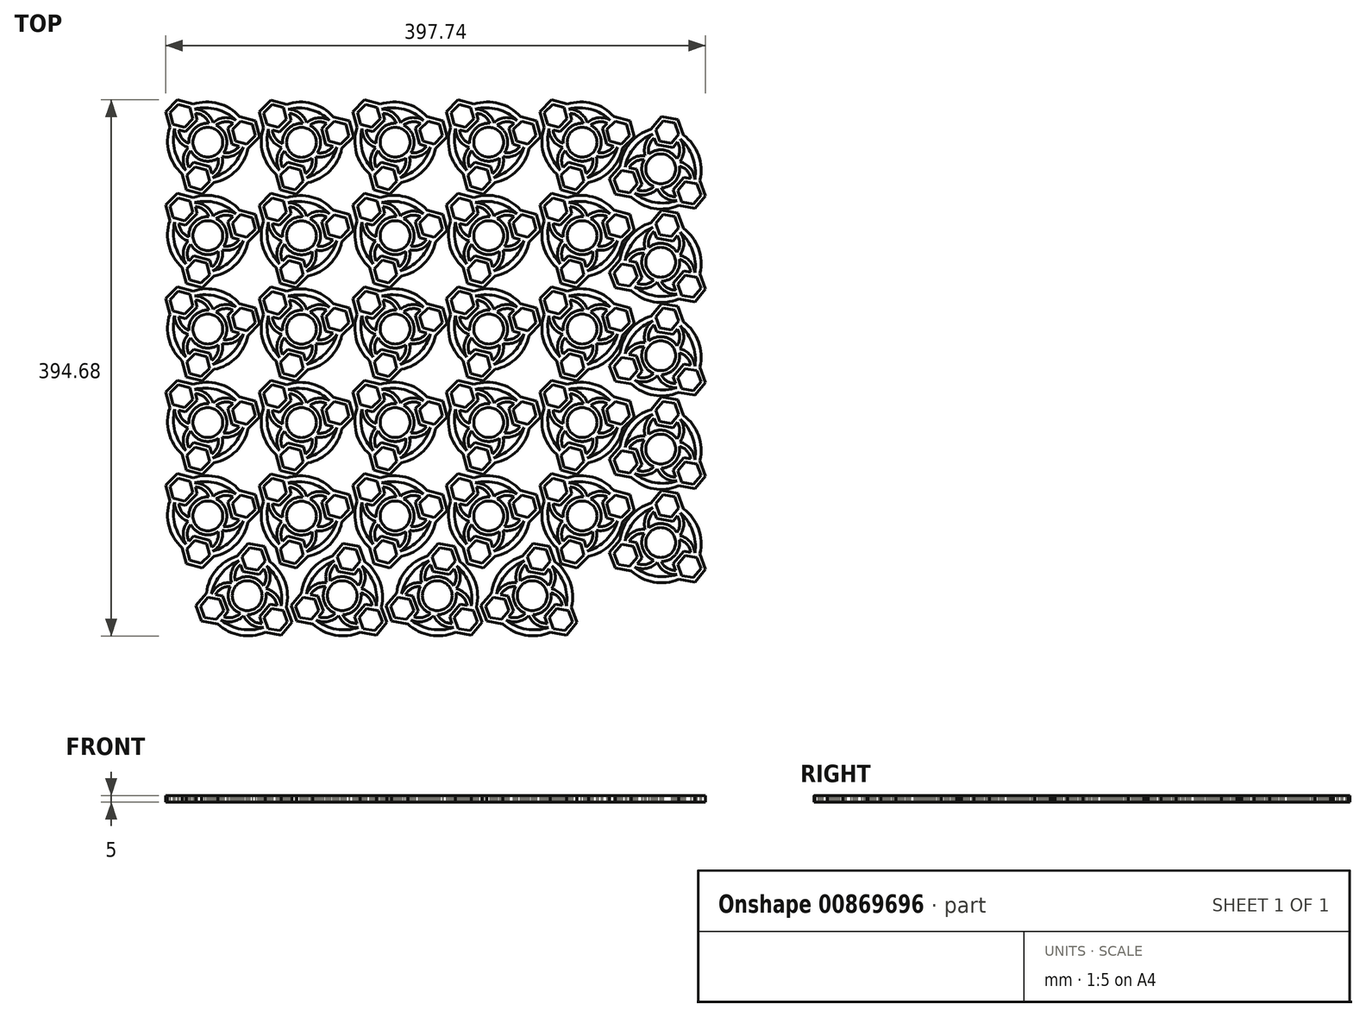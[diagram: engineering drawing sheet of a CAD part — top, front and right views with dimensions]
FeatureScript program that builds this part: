
annotation { "Feature Type Name" : "Feature", "Feature Type Description" : "" }
export const myFeature = defineFeature(function(context is Context, id is Id, definition is map)
    precondition{}
    {
        {
            var Q0;
            Q0=qCreatedBy(makeId("Top.planeOp"),FACE);
            var sketch = newSketch(context, id + "F0", { "sketchPlane" : qUnion([Q0])});
            skArc(sketch, "E0", {"start": v(-13.28, 4.44) * mm, "mid": v(-12.12, -7) * mm, "end": v(-2.8, -13.72) * mm});
            skCircle(sketch, "E1", {"center": v(0, 0) * mm, "radius": 11 * mm});
            skLineSegment(sketch, "E2.0", {"start": v(-4.34, 34.98) * mm, "end": v(4.34, 34.98) * mm});
            skLineSegment(sketch, "E2.1", {"start": v(4.34, 34.98) * mm, "end": v(8.68, 27.46) * mm});
            skLineSegment(sketch, "E2.2", {"start": v(8.68, 27.46) * mm, "end": v(4.34, 19.95) * mm});
            skLineSegment(sketch, "E2.3", {"start": v(4.34, 19.95) * mm, "end": v(-4.34, 19.95) * mm});
            skLineSegment(sketch, "E2.4", {"start": v(-4.34, 19.95) * mm, "end": v(-8.68, 27.46) * mm});
            skLineSegment(sketch, "E2.5", {"start": v(-8.68, 27.46) * mm, "end": v(-4.34, 34.98) * mm});
            skPoint(sketch, "E2.0.midPoint", {"position": v(0, 34.98) * mm});
            skArc(sketch, "E3", {"start": v(-10.28, 24.23) * mm, "mid": v(-14.32, 16.28) * mm, "end": v(-12.95, 7.48) * mm});
            skArc(sketch, "E4", {"start": v(-8.7, 21.51) * mm, "mid": v(-11.38, 15.65) * mm, "end": v(-10.49, 9.28) * mm});
            skLineSegment(sketch, "E5.0", {"start": v(-6.07, 37.98) * mm, "end": v(6.07, 37.98) * mm});
            skLineSegment(sketch, "E5.1", {"start": v(6.07, 37.98) * mm, "end": v(12.14, 27.46) * mm});
            skLineSegment(sketch, "E5.3", {"start": v(6.07, 16.95) * mm, "end": v(-6.07, 16.95) * mm});
            skLineSegment(sketch, "E5.4", {"start": v(-6.07, 16.95) * mm, "end": v(-8.7, 21.51) * mm});
            skLineSegment(sketch, "E5.5", {"start": v(-12.14, 27.46) * mm, "end": v(-6.07, 37.98) * mm});
            skPoint(sketch, "E5.0.midPoint", {"position": v(0, 37.98) * mm});
            skLineSegment(sketch, "E6.trimOffspring", {"start": v(8.7, 21.51) * mm, "end": v(6.07, 16.95) * mm});
            skArc(sketch, "E7.trimOffspring", {"start": v(10.49, 9.28) * mm, "mid": v(11.38, 15.65) * mm, "end": v(8.7, 21.51) * mm});
            skArc(sketch, "E8.trimOffspring", {"start": v(10.49, 9.28) * mm, "mid": v(0, 14) * mm, "end": v(-10.49, 9.28) * mm});
            skArc(sketch, "E9.trimOffspring", {"start": v(12.95, 7.48) * mm, "mid": v(14.32, 16.28) * mm, "end": v(10.28, 24.23) * mm});
            skLineSegment(sketch, "E10.1.0", {"start": v(-32.46, -13.73) * mm, "end": v(-28.12, -6.22) * mm});
            skLineSegment(sketch, "E10.1.1", {"start": v(-17.71, -3.22) * mm, "end": v(-11.64, -13.73) * mm});
            skLineSegment(sketch, "E10.1.2", {"start": v(-22.98, -3.22) * mm, "end": v(-17.71, -3.22) * mm});
            skArc(sketch, "E10.1.3", {"start": v(-12.95, 7.48) * mm, "mid": v(-21.26, 4.26) * mm, "end": v(-26.12, -3.22) * mm});
            skLineSegment(sketch, "E10.1.5", {"start": v(-29.85, -24.25) * mm, "end": v(-35.92, -13.73) * mm});
            skArc(sketch, "E10.1.6", {"start": v(2.8, -13.72) * mm, "mid": v(12.12, -7) * mm, "end": v(13.28, 4.44) * mm});
            skArc(sketch, "E10.1.7", {"start": v(-13.28, 4.44) * mm, "mid": v(-19.25, 2.03) * mm, "end": v(-22.98, -3.22) * mm});
            skLineSegment(sketch, "E10.1.8", {"start": v(-15.1, -13.73) * mm, "end": v(-19.44, -21.25) * mm});
            skLineSegment(sketch, "E10.1.9", {"start": v(-28.12, -6.22) * mm, "end": v(-19.44, -6.22) * mm});
            skLineSegment(sketch, "E10.1.10", {"start": v(-19.44, -6.22) * mm, "end": v(-15.1, -13.73) * mm});
            skLineSegment(sketch, "E10.1.11", {"start": v(-11.64, -13.73) * mm, "end": v(-14.28, -18.3) * mm});
            skArc(sketch, "E10.1.12", {"start": v(-14.28, -18.3) * mm, "mid": v(-7.87, -17.68) * mm, "end": v(-2.8, -13.72) * mm});
            skArc(sketch, "E10.1.14", {"start": v(-15.85, -21.01) * mm, "mid": v(-6.94, -20.54) * mm, "end": v(0, -14.95) * mm});
            skLineSegment(sketch, "E10.1.15", {"start": v(-17.71, -24.25) * mm, "end": v(-29.85, -24.25) * mm});
            skLineSegment(sketch, "E10.1.16", {"start": v(-19.44, -21.25) * mm, "end": v(-28.12, -21.25) * mm});
            skPoint(sketch, "E10.1.17", {"position": v(-30.29, -17.49) * mm});
            skLineSegment(sketch, "E10.1.18", {"start": v(-35.92, -13.73) * mm, "end": v(-29.85, -3.22) * mm});
            skPoint(sketch, "E10.1.19", {"position": v(-32.89, -18.99) * mm});
            skLineSegment(sketch, "E10.1.20", {"start": v(-28.12, -21.25) * mm, "end": v(-32.46, -13.73) * mm});
            skLineSegment(sketch, "E10.2.0", {"start": v(28.12, -21.25) * mm, "end": v(19.44, -21.25) * mm});
            skLineSegment(sketch, "E10.2.1", {"start": v(11.64, -13.73) * mm, "end": v(17.71, -3.22) * mm});
            skLineSegment(sketch, "E10.2.2", {"start": v(14.28, -18.3) * mm, "end": v(11.64, -13.73) * mm});
            skArc(sketch, "E10.2.3", {"start": v(0, -14.95) * mm, "mid": v(6.94, -20.54) * mm, "end": v(15.85, -21.01) * mm});
            skArc(sketch, "E10.2.4", {"start": v(2.8, -13.72) * mm, "mid": v(12.12, -7) * mm, "end": v(13.28, 4.44) * mm});
            skLineSegment(sketch, "E10.2.5", {"start": v(35.92, -13.73) * mm, "end": v(29.85, -24.25) * mm});
            skArc(sketch, "E10.2.7", {"start": v(2.8, -13.72) * mm, "mid": v(7.87, -17.68) * mm, "end": v(14.28, -18.3) * mm});
            skLineSegment(sketch, "E10.2.8", {"start": v(19.44, -6.22) * mm, "end": v(28.12, -6.22) * mm});
            skLineSegment(sketch, "E10.2.9", {"start": v(19.44, -21.25) * mm, "end": v(15.1, -13.73) * mm});
            skLineSegment(sketch, "E10.2.10", {"start": v(15.1, -13.73) * mm, "end": v(19.44, -6.22) * mm});
            skLineSegment(sketch, "E10.2.11", {"start": v(17.71, -3.22) * mm, "end": v(22.98, -3.22) * mm});
            skArc(sketch, "E10.2.12", {"start": v(22.98, -3.22) * mm, "mid": v(19.25, 2.03) * mm, "end": v(13.28, 4.44) * mm});
            skArc(sketch, "E10.2.14", {"start": v(26.12, -3.22) * mm, "mid": v(21.26, 4.26) * mm, "end": v(12.95, 7.48) * mm});
            skLineSegment(sketch, "E10.2.15", {"start": v(29.85, -3.22) * mm, "end": v(35.92, -13.73) * mm});
            skLineSegment(sketch, "E10.2.16", {"start": v(28.12, -6.22) * mm, "end": v(32.46, -13.73) * mm});
            skPoint(sketch, "E10.2.17", {"position": v(30.29, -17.49) * mm});
            skLineSegment(sketch, "E10.2.18", {"start": v(29.85, -24.25) * mm, "end": v(17.71, -24.25) * mm});
            skPoint(sketch, "E10.2.19", {"position": v(32.89, -18.99) * mm});
            skLineSegment(sketch, "E10.2.20", {"start": v(32.46, -13.73) * mm, "end": v(28.12, -21.25) * mm});
            skArc(sketch, "E11", {"start": v(-10.28, 24.23) * mm, "mid": v(-21.68, 12.52) * mm, "end": v(-26.12, -3.22) * mm});
            skArc(sketch, "E12", {"start": v(-12.14, 27.46) * mm, "mid": v(-25.63, 14.8) * mm, "end": v(-29.85, -3.22) * mm});
            skArc(sketch, "E13.1.0", {"start": v(-15.85, -21.01) * mm, "mid": v(0, -25.04) * mm, "end": v(15.85, -21.01) * mm});
            skArc(sketch, "E13.1.1", {"start": v(-17.71, -24.25) * mm, "mid": v(0, -29.6) * mm, "end": v(17.71, -24.25) * mm});
            skArc(sketch, "E13.2.0", {"start": v(26.12, -3.22) * mm, "mid": v(21.68, 12.52) * mm, "end": v(10.28, 24.23) * mm});
            skArc(sketch, "E13.2.1", {"start": v(29.85, -3.22) * mm, "mid": v(25.63, 14.8) * mm, "end": v(12.14, 27.46) * mm});
            skSolve(sketch);
        }
        {
            var Q0;
            Q0=makeQuery(id+"F0.imprint","IMPRINT",FACE,{"disambiguationData":[TD([[makeQuery(id+"F0.imprint","IMPRINT",EDGE,{"derivedFrom":sQuery(id+"F0.wireOp",EDGE,"E2.0")}),1.0]])]});
            extrude(context, id + "F1", {"entities" : qUnion([Q0]), "depth" : 5 * mm, "offsetDistance" : 25 * mm});
        }
        {
            var Q0;
            Q0=makeQuery(id+"F1.opExtrude","SWEPT_BODY",BODY,{"disambiguationData":[OSD([sQuery(id+"F0.wireOp",EDGE,"E2.0"),sQuery(id+"F0.wireOp",EDGE,"E2.1"),sQuery(id+"F0.wireOp",EDGE,"E2.2"),sQuery(id+"F0.wireOp",EDGE,"E2.3"),sQuery(id+"F0.wireOp",EDGE,"E2.4"),sQuery(id+"F0.wireOp",EDGE,"E2.5"),sQuery(id+"F0.wireOp",EDGE,"E3"),sQuery(id+"F0.wireOp",EDGE,"E4"),sQuery(id+"F0.wireOp",EDGE,"E5.0"),sQuery(id+"F0.wireOp",EDGE,"E5.1"),sQuery(id+"F0.wireOp",EDGE,"E5.3"),sQuery(id+"F0.wireOp",EDGE,"E5.4"),sQuery(id+"F0.wireOp",EDGE,"E5.5"),sQuery(id+"F0.wireOp",EDGE,"E6.trimOffspring"),sQuery(id+"F0.wireOp",EDGE,"E7.trimOffspring"),sQuery(id+"F0.wireOp",EDGE,"E9.trimOffspring"),sQuery(id+"F0.wireOp",EDGE,"E10.1.0"),sQuery(id+"F0.wireOp",EDGE,"E10.1.1"),sQuery(id+"F0.wireOp",EDGE,"E10.1.2"),sQuery(id+"F0.wireOp",EDGE,"E10.1.3"),sQuery(id+"F0.wireOp",EDGE,"E10.1.5"),sQuery(id+"F0.wireOp",EDGE,"E10.1.7"),sQuery(id+"F0.wireOp",EDGE,"E10.1.8"),sQuery(id+"F0.wireOp",EDGE,"E10.1.9"),sQuery(id+"F0.wireOp",EDGE,"E10.1.10"),sQuery(id+"F0.wireOp",EDGE,"E10.1.11"),sQuery(id+"F0.wireOp",EDGE,"E10.1.12"),sQuery(id+"F0.wireOp",EDGE,"E10.1.14"),sQuery(id+"F0.wireOp",EDGE,"E10.1.15"),sQuery(id+"F0.wireOp",EDGE,"E10.1.16"),sQuery(id+"F0.wireOp",EDGE,"E10.1.18"),sQuery(id+"F0.wireOp",EDGE,"E10.1.20"),sQuery(id+"F0.wireOp",EDGE,"E10.2.0"),sQuery(id+"F0.wireOp",EDGE,"E10.2.1"),sQuery(id+"F0.wireOp",EDGE,"E10.2.2"),sQuery(id+"F0.wireOp",EDGE,"E10.2.3"),sQuery(id+"F0.wireOp",EDGE,"E10.2.5"),sQuery(id+"F0.wireOp",EDGE,"E10.2.7"),sQuery(id+"F0.wireOp",EDGE,"E10.2.8"),sQuery(id+"F0.wireOp",EDGE,"E10.2.9"),sQuery(id+"F0.wireOp",EDGE,"E10.2.10"),sQuery(id+"F0.wireOp",EDGE,"E10.2.11"),sQuery(id+"F0.wireOp",EDGE,"E10.2.12"),sQuery(id+"F0.wireOp",EDGE,"E1"),sQuery(id+"F0.wireOp",EDGE,"E10.2.14"),sQuery(id+"F0.wireOp",EDGE,"E10.2.15"),sQuery(id+"F0.wireOp",EDGE,"E10.2.16"),sQuery(id+"F0.wireOp",EDGE,"E10.2.18"),sQuery(id+"F0.wireOp",EDGE,"E10.2.20"),sQuery(id+"F0.wireOp",EDGE,"E8.trimOffspring"),sQuery(id+"F0.wireOp",EDGE,"E0"),sQuery(id+"F0.wireOp",EDGE,"E10.1.6"),sQuery(id+"F0.wireOp",EDGE,"E11"),sQuery(id+"F0.wireOp",EDGE,"E12"),sQuery(id+"F0.wireOp",EDGE,"E13.1.0"),sQuery(id+"F0.wireOp",EDGE,"E13.1.1"),sQuery(id+"F0.wireOp",EDGE,"E13.2.0"),sQuery(id+"F0.wireOp",EDGE,"E13.2.1")])]});
            transform(context, id + "F2", {"entities" : qUnion([Q0]), "transformType" : TransformType.TRANSLATION_3D, "dx" : -159 * mm, "dy" : 162 * mm, "dz" : 0 * mm, "makeCopy" : false});
        }
        {
            var Q0;
            Q0=makeQuery(id+"F1.opExtrude","SWEPT_BODY",BODY,{"disambiguationData":[OSD([sQuery(id+"F0.wireOp",EDGE,"E2.0"),sQuery(id+"F0.wireOp",EDGE,"E2.1"),sQuery(id+"F0.wireOp",EDGE,"E2.2"),sQuery(id+"F0.wireOp",EDGE,"E2.3"),sQuery(id+"F0.wireOp",EDGE,"E2.4"),sQuery(id+"F0.wireOp",EDGE,"E2.5"),sQuery(id+"F0.wireOp",EDGE,"E3"),sQuery(id+"F0.wireOp",EDGE,"E4"),sQuery(id+"F0.wireOp",EDGE,"E5.0"),sQuery(id+"F0.wireOp",EDGE,"E5.1"),sQuery(id+"F0.wireOp",EDGE,"E5.3"),sQuery(id+"F0.wireOp",EDGE,"E5.4"),sQuery(id+"F0.wireOp",EDGE,"E5.5"),sQuery(id+"F0.wireOp",EDGE,"E6.trimOffspring"),sQuery(id+"F0.wireOp",EDGE,"E7.trimOffspring"),sQuery(id+"F0.wireOp",EDGE,"E9.trimOffspring"),sQuery(id+"F0.wireOp",EDGE,"E10.1.0"),sQuery(id+"F0.wireOp",EDGE,"E10.1.1"),sQuery(id+"F0.wireOp",EDGE,"E10.1.2"),sQuery(id+"F0.wireOp",EDGE,"E10.1.3"),sQuery(id+"F0.wireOp",EDGE,"E10.1.5"),sQuery(id+"F0.wireOp",EDGE,"E10.1.7"),sQuery(id+"F0.wireOp",EDGE,"E10.1.8"),sQuery(id+"F0.wireOp",EDGE,"E10.1.9"),sQuery(id+"F0.wireOp",EDGE,"E10.1.10"),sQuery(id+"F0.wireOp",EDGE,"E10.1.11"),sQuery(id+"F0.wireOp",EDGE,"E10.1.12"),sQuery(id+"F0.wireOp",EDGE,"E10.1.14"),sQuery(id+"F0.wireOp",EDGE,"E10.1.15"),sQuery(id+"F0.wireOp",EDGE,"E10.1.16"),sQuery(id+"F0.wireOp",EDGE,"E10.1.18"),sQuery(id+"F0.wireOp",EDGE,"E10.1.20"),sQuery(id+"F0.wireOp",EDGE,"E10.2.0"),sQuery(id+"F0.wireOp",EDGE,"E10.2.1"),sQuery(id+"F0.wireOp",EDGE,"E10.2.2"),sQuery(id+"F0.wireOp",EDGE,"E10.2.3"),sQuery(id+"F0.wireOp",EDGE,"E10.2.5"),sQuery(id+"F0.wireOp",EDGE,"E10.2.7"),sQuery(id+"F0.wireOp",EDGE,"E10.2.8"),sQuery(id+"F0.wireOp",EDGE,"E10.2.9"),sQuery(id+"F0.wireOp",EDGE,"E10.2.10"),sQuery(id+"F0.wireOp",EDGE,"E10.2.11"),sQuery(id+"F0.wireOp",EDGE,"E10.2.12"),sQuery(id+"F0.wireOp",EDGE,"E1"),sQuery(id+"F0.wireOp",EDGE,"E10.2.14"),sQuery(id+"F0.wireOp",EDGE,"E10.2.15"),sQuery(id+"F0.wireOp",EDGE,"E10.2.16"),sQuery(id+"F0.wireOp",EDGE,"E10.2.18"),sQuery(id+"F0.wireOp",EDGE,"E10.2.20"),sQuery(id+"F0.wireOp",EDGE,"E8.trimOffspring"),sQuery(id+"F0.wireOp",EDGE,"E0"),sQuery(id+"F0.wireOp",EDGE,"E10.1.6"),sQuery(id+"F0.wireOp",EDGE,"E11"),sQuery(id+"F0.wireOp",EDGE,"E12"),sQuery(id+"F0.wireOp",EDGE,"E13.1.0"),sQuery(id+"F0.wireOp",EDGE,"E13.1.1"),sQuery(id+"F0.wireOp",EDGE,"E13.2.0"),sQuery(id+"F0.wireOp",EDGE,"E13.2.1")])]});
            var Q1;
            Q1=makeQuery(id+"F1.opExtrude","CAP_EDGE",EDGE,{"disambiguationData":[OSD([sQuery(id+"F0.wireOp",EDGE,"E1")])],"isStart":false});
            transform(context, id + "F3", {"entities" : qUnion([Q0]), "transformType" : TransformType.ROTATION, "transformAxis" : qUnion([Q1]), "angle" : 45 * degree, "makeCopy" : false});
        }
        {
            var Q0;
            Q0=makeQuery(id+"F1.opExtrude","SWEPT_BODY",BODY,{"disambiguationData":[OSD([sQuery(id+"F0.wireOp",EDGE,"E2.0"),sQuery(id+"F0.wireOp",EDGE,"E2.1"),sQuery(id+"F0.wireOp",EDGE,"E2.2"),sQuery(id+"F0.wireOp",EDGE,"E2.3"),sQuery(id+"F0.wireOp",EDGE,"E2.4"),sQuery(id+"F0.wireOp",EDGE,"E2.5"),sQuery(id+"F0.wireOp",EDGE,"E3"),sQuery(id+"F0.wireOp",EDGE,"E4"),sQuery(id+"F0.wireOp",EDGE,"E5.0"),sQuery(id+"F0.wireOp",EDGE,"E5.1"),sQuery(id+"F0.wireOp",EDGE,"E5.3"),sQuery(id+"F0.wireOp",EDGE,"E5.4"),sQuery(id+"F0.wireOp",EDGE,"E5.5"),sQuery(id+"F0.wireOp",EDGE,"E6.trimOffspring"),sQuery(id+"F0.wireOp",EDGE,"E7.trimOffspring"),sQuery(id+"F0.wireOp",EDGE,"E9.trimOffspring"),sQuery(id+"F0.wireOp",EDGE,"E10.1.0"),sQuery(id+"F0.wireOp",EDGE,"E10.1.1"),sQuery(id+"F0.wireOp",EDGE,"E10.1.2"),sQuery(id+"F0.wireOp",EDGE,"E10.1.3"),sQuery(id+"F0.wireOp",EDGE,"E10.1.5"),sQuery(id+"F0.wireOp",EDGE,"E10.1.7"),sQuery(id+"F0.wireOp",EDGE,"E10.1.8"),sQuery(id+"F0.wireOp",EDGE,"E10.1.9"),sQuery(id+"F0.wireOp",EDGE,"E10.1.10"),sQuery(id+"F0.wireOp",EDGE,"E10.1.11"),sQuery(id+"F0.wireOp",EDGE,"E10.1.12"),sQuery(id+"F0.wireOp",EDGE,"E10.1.14"),sQuery(id+"F0.wireOp",EDGE,"E10.1.15"),sQuery(id+"F0.wireOp",EDGE,"E10.1.16"),sQuery(id+"F0.wireOp",EDGE,"E10.1.18"),sQuery(id+"F0.wireOp",EDGE,"E10.1.20"),sQuery(id+"F0.wireOp",EDGE,"E10.2.0"),sQuery(id+"F0.wireOp",EDGE,"E10.2.1"),sQuery(id+"F0.wireOp",EDGE,"E10.2.2"),sQuery(id+"F0.wireOp",EDGE,"E10.2.3"),sQuery(id+"F0.wireOp",EDGE,"E10.2.5"),sQuery(id+"F0.wireOp",EDGE,"E10.2.7"),sQuery(id+"F0.wireOp",EDGE,"E10.2.8"),sQuery(id+"F0.wireOp",EDGE,"E10.2.9"),sQuery(id+"F0.wireOp",EDGE,"E10.2.10"),sQuery(id+"F0.wireOp",EDGE,"E10.2.11"),sQuery(id+"F0.wireOp",EDGE,"E10.2.12"),sQuery(id+"F0.wireOp",EDGE,"E1"),sQuery(id+"F0.wireOp",EDGE,"E10.2.14"),sQuery(id+"F0.wireOp",EDGE,"E10.2.15"),sQuery(id+"F0.wireOp",EDGE,"E10.2.16"),sQuery(id+"F0.wireOp",EDGE,"E10.2.18"),sQuery(id+"F0.wireOp",EDGE,"E10.2.20"),sQuery(id+"F0.wireOp",EDGE,"E8.trimOffspring"),sQuery(id+"F0.wireOp",EDGE,"E0"),sQuery(id+"F0.wireOp",EDGE,"E10.1.6"),sQuery(id+"F0.wireOp",EDGE,"E11"),sQuery(id+"F0.wireOp",EDGE,"E12"),sQuery(id+"F0.wireOp",EDGE,"E13.1.0"),sQuery(id+"F0.wireOp",EDGE,"E13.1.1"),sQuery(id+"F0.wireOp",EDGE,"E13.2.0"),sQuery(id+"F0.wireOp",EDGE,"E13.2.1")])]});
            transform(context, id + "F4", {"entities" : qUnion([Q0]), "transformType" : TransformType.TRANSLATION_3D, "dx" : -4.9 * mm, "dy" : 7.3 * mm, "dz" : 0 * mm, "makeCopy" : false});
        }
        {
            var Q0;
            Q0=makeQuery(id+"F1.opExtrude","SWEPT_BODY",BODY,{"disambiguationData":[OSD([sQuery(id+"F0.wireOp",EDGE,"E2.0"),sQuery(id+"F0.wireOp",EDGE,"E2.1"),sQuery(id+"F0.wireOp",EDGE,"E2.2"),sQuery(id+"F0.wireOp",EDGE,"E2.3"),sQuery(id+"F0.wireOp",EDGE,"E2.4"),sQuery(id+"F0.wireOp",EDGE,"E2.5"),sQuery(id+"F0.wireOp",EDGE,"E3"),sQuery(id+"F0.wireOp",EDGE,"E4"),sQuery(id+"F0.wireOp",EDGE,"E5.0"),sQuery(id+"F0.wireOp",EDGE,"E5.1"),sQuery(id+"F0.wireOp",EDGE,"E5.3"),sQuery(id+"F0.wireOp",EDGE,"E5.4"),sQuery(id+"F0.wireOp",EDGE,"E5.5"),sQuery(id+"F0.wireOp",EDGE,"E6.trimOffspring"),sQuery(id+"F0.wireOp",EDGE,"E7.trimOffspring"),sQuery(id+"F0.wireOp",EDGE,"E9.trimOffspring"),sQuery(id+"F0.wireOp",EDGE,"E10.1.0"),sQuery(id+"F0.wireOp",EDGE,"E10.1.1"),sQuery(id+"F0.wireOp",EDGE,"E10.1.2"),sQuery(id+"F0.wireOp",EDGE,"E10.1.3"),sQuery(id+"F0.wireOp",EDGE,"E10.1.5"),sQuery(id+"F0.wireOp",EDGE,"E10.1.7"),sQuery(id+"F0.wireOp",EDGE,"E10.1.8"),sQuery(id+"F0.wireOp",EDGE,"E10.1.9"),sQuery(id+"F0.wireOp",EDGE,"E10.1.10"),sQuery(id+"F0.wireOp",EDGE,"E10.1.11"),sQuery(id+"F0.wireOp",EDGE,"E10.1.12"),sQuery(id+"F0.wireOp",EDGE,"E10.1.14"),sQuery(id+"F0.wireOp",EDGE,"E10.1.15"),sQuery(id+"F0.wireOp",EDGE,"E10.1.16"),sQuery(id+"F0.wireOp",EDGE,"E10.1.18"),sQuery(id+"F0.wireOp",EDGE,"E10.1.20"),sQuery(id+"F0.wireOp",EDGE,"E10.2.0"),sQuery(id+"F0.wireOp",EDGE,"E10.2.1"),sQuery(id+"F0.wireOp",EDGE,"E10.2.2"),sQuery(id+"F0.wireOp",EDGE,"E10.2.3"),sQuery(id+"F0.wireOp",EDGE,"E10.2.5"),sQuery(id+"F0.wireOp",EDGE,"E10.2.7"),sQuery(id+"F0.wireOp",EDGE,"E10.2.8"),sQuery(id+"F0.wireOp",EDGE,"E10.2.9"),sQuery(id+"F0.wireOp",EDGE,"E10.2.10"),sQuery(id+"F0.wireOp",EDGE,"E10.2.11"),sQuery(id+"F0.wireOp",EDGE,"E10.2.12"),sQuery(id+"F0.wireOp",EDGE,"E1"),sQuery(id+"F0.wireOp",EDGE,"E10.2.14"),sQuery(id+"F0.wireOp",EDGE,"E10.2.15"),sQuery(id+"F0.wireOp",EDGE,"E10.2.16"),sQuery(id+"F0.wireOp",EDGE,"E10.2.18"),sQuery(id+"F0.wireOp",EDGE,"E10.2.20"),sQuery(id+"F0.wireOp",EDGE,"E8.trimOffspring"),sQuery(id+"F0.wireOp",EDGE,"E0"),sQuery(id+"F0.wireOp",EDGE,"E10.1.6"),sQuery(id+"F0.wireOp",EDGE,"E11"),sQuery(id+"F0.wireOp",EDGE,"E12"),sQuery(id+"F0.wireOp",EDGE,"E13.1.0"),sQuery(id+"F0.wireOp",EDGE,"E13.1.1"),sQuery(id+"F0.wireOp",EDGE,"E13.2.0"),sQuery(id+"F0.wireOp",EDGE,"E13.2.1")])]});
            transform(context, id + "F5", {"entities" : qUnion([Q0]), "transformType" : TransformType.TRANSLATION_3D, "dx" : 69 * mm, "dy" : -0.1 * mm, "dz" : 0 * mm, "makeCopy" : true});
        }
        {
            var Q0;
            Q0=makeQuery(id+"F5.opPattern","COPY",BODY,{"derivedFrom":makeQuery(id+"F1.opExtrude","SWEPT_BODY",BODY,{"disambiguationData":[OSD([sQuery(id+"F0.wireOp",EDGE,"E2.0"),sQuery(id+"F0.wireOp",EDGE,"E2.1"),sQuery(id+"F0.wireOp",EDGE,"E2.2"),sQuery(id+"F0.wireOp",EDGE,"E2.3"),sQuery(id+"F0.wireOp",EDGE,"E2.4"),sQuery(id+"F0.wireOp",EDGE,"E2.5"),sQuery(id+"F0.wireOp",EDGE,"E3"),sQuery(id+"F0.wireOp",EDGE,"E4"),sQuery(id+"F0.wireOp",EDGE,"E5.0"),sQuery(id+"F0.wireOp",EDGE,"E5.1"),sQuery(id+"F0.wireOp",EDGE,"E5.3"),sQuery(id+"F0.wireOp",EDGE,"E5.4"),sQuery(id+"F0.wireOp",EDGE,"E5.5"),sQuery(id+"F0.wireOp",EDGE,"E6.trimOffspring"),sQuery(id+"F0.wireOp",EDGE,"E7.trimOffspring"),sQuery(id+"F0.wireOp",EDGE,"E9.trimOffspring"),sQuery(id+"F0.wireOp",EDGE,"E10.1.0"),sQuery(id+"F0.wireOp",EDGE,"E10.1.1"),sQuery(id+"F0.wireOp",EDGE,"E10.1.2"),sQuery(id+"F0.wireOp",EDGE,"E10.1.3"),sQuery(id+"F0.wireOp",EDGE,"E10.1.5"),sQuery(id+"F0.wireOp",EDGE,"E10.1.7"),sQuery(id+"F0.wireOp",EDGE,"E10.1.8"),sQuery(id+"F0.wireOp",EDGE,"E10.1.9"),sQuery(id+"F0.wireOp",EDGE,"E10.1.10"),sQuery(id+"F0.wireOp",EDGE,"E10.1.11"),sQuery(id+"F0.wireOp",EDGE,"E10.1.12"),sQuery(id+"F0.wireOp",EDGE,"E10.1.14"),sQuery(id+"F0.wireOp",EDGE,"E10.1.15"),sQuery(id+"F0.wireOp",EDGE,"E10.1.16"),sQuery(id+"F0.wireOp",EDGE,"E10.1.18"),sQuery(id+"F0.wireOp",EDGE,"E10.1.20"),sQuery(id+"F0.wireOp",EDGE,"E10.2.0"),sQuery(id+"F0.wireOp",EDGE,"E10.2.1"),sQuery(id+"F0.wireOp",EDGE,"E10.2.2"),sQuery(id+"F0.wireOp",EDGE,"E10.2.3"),sQuery(id+"F0.wireOp",EDGE,"E10.2.5"),sQuery(id+"F0.wireOp",EDGE,"E10.2.7"),sQuery(id+"F0.wireOp",EDGE,"E10.2.8"),sQuery(id+"F0.wireOp",EDGE,"E10.2.9"),sQuery(id+"F0.wireOp",EDGE,"E10.2.10"),sQuery(id+"F0.wireOp",EDGE,"E10.2.11"),sQuery(id+"F0.wireOp",EDGE,"E10.2.12"),sQuery(id+"F0.wireOp",EDGE,"E1"),sQuery(id+"F0.wireOp",EDGE,"E10.2.14"),sQuery(id+"F0.wireOp",EDGE,"E10.2.15"),sQuery(id+"F0.wireOp",EDGE,"E10.2.16"),sQuery(id+"F0.wireOp",EDGE,"E10.2.18"),sQuery(id+"F0.wireOp",EDGE,"E10.2.20"),sQuery(id+"F0.wireOp",EDGE,"E8.trimOffspring"),sQuery(id+"F0.wireOp",EDGE,"E0"),sQuery(id+"F0.wireOp",EDGE,"E10.1.6"),sQuery(id+"F0.wireOp",EDGE,"E11"),sQuery(id+"F0.wireOp",EDGE,"E12"),sQuery(id+"F0.wireOp",EDGE,"E13.1.0"),sQuery(id+"F0.wireOp",EDGE,"E13.1.1"),sQuery(id+"F0.wireOp",EDGE,"E13.2.0"),sQuery(id+"F0.wireOp",EDGE,"E13.2.1")])]}),"instanceName":"1"});
            var Q1;
            Q1=makeQuery(id+"F5.opPattern","COPY",EDGE,{"derivedFrom":makeQuery(id+"F1.opExtrude","CAP_EDGE",EDGE,{"disambiguationData":[OSD([sQuery(id+"F0.wireOp",EDGE,"E1")])],"isStart":false}),"instanceName":"1"});
            transform(context, id + "F6", {"entities" : qUnion([Q0]), "transformType" : TransformType.ROTATION, "transformAxis" : qUnion([Q1]), "angle" : 120 * degree, "makeCopy" : false});
        }
        {
            var Q0;
            Q0=makeQuery(id+"F1.opExtrude","SWEPT_BODY",BODY,{"disambiguationData":[OSD([sQuery(id+"F0.wireOp",EDGE,"E2.0"),sQuery(id+"F0.wireOp",EDGE,"E2.1"),sQuery(id+"F0.wireOp",EDGE,"E2.2"),sQuery(id+"F0.wireOp",EDGE,"E2.3"),sQuery(id+"F0.wireOp",EDGE,"E2.4"),sQuery(id+"F0.wireOp",EDGE,"E2.5"),sQuery(id+"F0.wireOp",EDGE,"E3"),sQuery(id+"F0.wireOp",EDGE,"E4"),sQuery(id+"F0.wireOp",EDGE,"E5.0"),sQuery(id+"F0.wireOp",EDGE,"E5.1"),sQuery(id+"F0.wireOp",EDGE,"E5.3"),sQuery(id+"F0.wireOp",EDGE,"E5.4"),sQuery(id+"F0.wireOp",EDGE,"E5.5"),sQuery(id+"F0.wireOp",EDGE,"E6.trimOffspring"),sQuery(id+"F0.wireOp",EDGE,"E7.trimOffspring"),sQuery(id+"F0.wireOp",EDGE,"E9.trimOffspring"),sQuery(id+"F0.wireOp",EDGE,"E10.1.0"),sQuery(id+"F0.wireOp",EDGE,"E10.1.1"),sQuery(id+"F0.wireOp",EDGE,"E10.1.2"),sQuery(id+"F0.wireOp",EDGE,"E10.1.3"),sQuery(id+"F0.wireOp",EDGE,"E10.1.5"),sQuery(id+"F0.wireOp",EDGE,"E10.1.7"),sQuery(id+"F0.wireOp",EDGE,"E10.1.8"),sQuery(id+"F0.wireOp",EDGE,"E10.1.9"),sQuery(id+"F0.wireOp",EDGE,"E10.1.10"),sQuery(id+"F0.wireOp",EDGE,"E10.1.11"),sQuery(id+"F0.wireOp",EDGE,"E10.1.12"),sQuery(id+"F0.wireOp",EDGE,"E10.1.14"),sQuery(id+"F0.wireOp",EDGE,"E10.1.15"),sQuery(id+"F0.wireOp",EDGE,"E10.1.16"),sQuery(id+"F0.wireOp",EDGE,"E10.1.18"),sQuery(id+"F0.wireOp",EDGE,"E10.1.20"),sQuery(id+"F0.wireOp",EDGE,"E10.2.0"),sQuery(id+"F0.wireOp",EDGE,"E10.2.1"),sQuery(id+"F0.wireOp",EDGE,"E10.2.2"),sQuery(id+"F0.wireOp",EDGE,"E10.2.3"),sQuery(id+"F0.wireOp",EDGE,"E10.2.5"),sQuery(id+"F0.wireOp",EDGE,"E10.2.7"),sQuery(id+"F0.wireOp",EDGE,"E10.2.8"),sQuery(id+"F0.wireOp",EDGE,"E10.2.9"),sQuery(id+"F0.wireOp",EDGE,"E10.2.10"),sQuery(id+"F0.wireOp",EDGE,"E10.2.11"),sQuery(id+"F0.wireOp",EDGE,"E10.2.12"),sQuery(id+"F0.wireOp",EDGE,"E1"),sQuery(id+"F0.wireOp",EDGE,"E10.2.14"),sQuery(id+"F0.wireOp",EDGE,"E10.2.15"),sQuery(id+"F0.wireOp",EDGE,"E10.2.16"),sQuery(id+"F0.wireOp",EDGE,"E10.2.18"),sQuery(id+"F0.wireOp",EDGE,"E10.2.20"),sQuery(id+"F0.wireOp",EDGE,"E8.trimOffspring"),sQuery(id+"F0.wireOp",EDGE,"E0"),sQuery(id+"F0.wireOp",EDGE,"E10.1.6"),sQuery(id+"F0.wireOp",EDGE,"E11"),sQuery(id+"F0.wireOp",EDGE,"E12"),sQuery(id+"F0.wireOp",EDGE,"E13.1.0"),sQuery(id+"F0.wireOp",EDGE,"E13.1.1"),sQuery(id+"F0.wireOp",EDGE,"E13.2.0"),sQuery(id+"F0.wireOp",EDGE,"E13.2.1")])]});
            transform(context, id + "F7", {"entities" : qUnion([Q0]), "transformType" : TransformType.TRANSLATION_3D, "dx" : 138 * mm, "dy" : 0 * mm, "dz" : 0 * mm, "makeCopy" : true});
        }
        {
            var Q0;
            Q0=makeQuery(id+"F7.opPattern","COPY",BODY,{"derivedFrom":makeQuery(id+"F1.opExtrude","SWEPT_BODY",BODY,{"disambiguationData":[OSD([sQuery(id+"F0.wireOp",EDGE,"E2.0"),sQuery(id+"F0.wireOp",EDGE,"E2.1"),sQuery(id+"F0.wireOp",EDGE,"E2.2"),sQuery(id+"F0.wireOp",EDGE,"E2.3"),sQuery(id+"F0.wireOp",EDGE,"E2.4"),sQuery(id+"F0.wireOp",EDGE,"E2.5"),sQuery(id+"F0.wireOp",EDGE,"E3"),sQuery(id+"F0.wireOp",EDGE,"E4"),sQuery(id+"F0.wireOp",EDGE,"E5.0"),sQuery(id+"F0.wireOp",EDGE,"E5.1"),sQuery(id+"F0.wireOp",EDGE,"E5.3"),sQuery(id+"F0.wireOp",EDGE,"E5.4"),sQuery(id+"F0.wireOp",EDGE,"E5.5"),sQuery(id+"F0.wireOp",EDGE,"E6.trimOffspring"),sQuery(id+"F0.wireOp",EDGE,"E7.trimOffspring"),sQuery(id+"F0.wireOp",EDGE,"E9.trimOffspring"),sQuery(id+"F0.wireOp",EDGE,"E10.1.0"),sQuery(id+"F0.wireOp",EDGE,"E10.1.1"),sQuery(id+"F0.wireOp",EDGE,"E10.1.2"),sQuery(id+"F0.wireOp",EDGE,"E10.1.3"),sQuery(id+"F0.wireOp",EDGE,"E10.1.5"),sQuery(id+"F0.wireOp",EDGE,"E10.1.7"),sQuery(id+"F0.wireOp",EDGE,"E10.1.8"),sQuery(id+"F0.wireOp",EDGE,"E10.1.9"),sQuery(id+"F0.wireOp",EDGE,"E10.1.10"),sQuery(id+"F0.wireOp",EDGE,"E10.1.11"),sQuery(id+"F0.wireOp",EDGE,"E10.1.12"),sQuery(id+"F0.wireOp",EDGE,"E10.1.14"),sQuery(id+"F0.wireOp",EDGE,"E10.1.15"),sQuery(id+"F0.wireOp",EDGE,"E10.1.16"),sQuery(id+"F0.wireOp",EDGE,"E10.1.18"),sQuery(id+"F0.wireOp",EDGE,"E10.1.20"),sQuery(id+"F0.wireOp",EDGE,"E10.2.0"),sQuery(id+"F0.wireOp",EDGE,"E10.2.1"),sQuery(id+"F0.wireOp",EDGE,"E10.2.2"),sQuery(id+"F0.wireOp",EDGE,"E10.2.3"),sQuery(id+"F0.wireOp",EDGE,"E10.2.5"),sQuery(id+"F0.wireOp",EDGE,"E10.2.7"),sQuery(id+"F0.wireOp",EDGE,"E10.2.8"),sQuery(id+"F0.wireOp",EDGE,"E10.2.9"),sQuery(id+"F0.wireOp",EDGE,"E10.2.10"),sQuery(id+"F0.wireOp",EDGE,"E10.2.11"),sQuery(id+"F0.wireOp",EDGE,"E10.2.12"),sQuery(id+"F0.wireOp",EDGE,"E1"),sQuery(id+"F0.wireOp",EDGE,"E10.2.14"),sQuery(id+"F0.wireOp",EDGE,"E10.2.15"),sQuery(id+"F0.wireOp",EDGE,"E10.2.16"),sQuery(id+"F0.wireOp",EDGE,"E10.2.18"),sQuery(id+"F0.wireOp",EDGE,"E10.2.20"),sQuery(id+"F0.wireOp",EDGE,"E8.trimOffspring"),sQuery(id+"F0.wireOp",EDGE,"E0"),sQuery(id+"F0.wireOp",EDGE,"E10.1.6"),sQuery(id+"F0.wireOp",EDGE,"E11"),sQuery(id+"F0.wireOp",EDGE,"E12"),sQuery(id+"F0.wireOp",EDGE,"E13.1.0"),sQuery(id+"F0.wireOp",EDGE,"E13.1.1"),sQuery(id+"F0.wireOp",EDGE,"E13.2.0"),sQuery(id+"F0.wireOp",EDGE,"E13.2.1")])]}),"instanceName":"1"});
            transform(context, id + "F8", {"entities" : qUnion([Q0]), "transformType" : TransformType.TRANSLATION_3D, "dx" : 68.9 * mm, "dy" : 0 * mm, "dz" : 0 * mm, "makeCopy" : true});
        }
        {
            var Q0;
            Q0=makeQuery(id+"F8.opPattern","COPY",BODY,{"derivedFrom":makeQuery(id+"F7.opPattern","COPY",BODY,{"derivedFrom":makeQuery(id+"F1.opExtrude","SWEPT_BODY",BODY,{"disambiguationData":[OSD([sQuery(id+"F0.wireOp",EDGE,"E2.0"),sQuery(id+"F0.wireOp",EDGE,"E2.1"),sQuery(id+"F0.wireOp",EDGE,"E2.2"),sQuery(id+"F0.wireOp",EDGE,"E2.3"),sQuery(id+"F0.wireOp",EDGE,"E2.4"),sQuery(id+"F0.wireOp",EDGE,"E2.5"),sQuery(id+"F0.wireOp",EDGE,"E3"),sQuery(id+"F0.wireOp",EDGE,"E4"),sQuery(id+"F0.wireOp",EDGE,"E5.0"),sQuery(id+"F0.wireOp",EDGE,"E5.1"),sQuery(id+"F0.wireOp",EDGE,"E5.3"),sQuery(id+"F0.wireOp",EDGE,"E5.4"),sQuery(id+"F0.wireOp",EDGE,"E5.5"),sQuery(id+"F0.wireOp",EDGE,"E6.trimOffspring"),sQuery(id+"F0.wireOp",EDGE,"E7.trimOffspring"),sQuery(id+"F0.wireOp",EDGE,"E9.trimOffspring"),sQuery(id+"F0.wireOp",EDGE,"E10.1.0"),sQuery(id+"F0.wireOp",EDGE,"E10.1.1"),sQuery(id+"F0.wireOp",EDGE,"E10.1.2"),sQuery(id+"F0.wireOp",EDGE,"E10.1.3"),sQuery(id+"F0.wireOp",EDGE,"E10.1.5"),sQuery(id+"F0.wireOp",EDGE,"E10.1.7"),sQuery(id+"F0.wireOp",EDGE,"E10.1.8"),sQuery(id+"F0.wireOp",EDGE,"E10.1.9"),sQuery(id+"F0.wireOp",EDGE,"E10.1.10"),sQuery(id+"F0.wireOp",EDGE,"E10.1.11"),sQuery(id+"F0.wireOp",EDGE,"E10.1.12"),sQuery(id+"F0.wireOp",EDGE,"E10.1.14"),sQuery(id+"F0.wireOp",EDGE,"E10.1.15"),sQuery(id+"F0.wireOp",EDGE,"E10.1.16"),sQuery(id+"F0.wireOp",EDGE,"E10.1.18"),sQuery(id+"F0.wireOp",EDGE,"E10.1.20"),sQuery(id+"F0.wireOp",EDGE,"E10.2.0"),sQuery(id+"F0.wireOp",EDGE,"E10.2.1"),sQuery(id+"F0.wireOp",EDGE,"E10.2.2"),sQuery(id+"F0.wireOp",EDGE,"E10.2.3"),sQuery(id+"F0.wireOp",EDGE,"E10.2.5"),sQuery(id+"F0.wireOp",EDGE,"E10.2.7"),sQuery(id+"F0.wireOp",EDGE,"E10.2.8"),sQuery(id+"F0.wireOp",EDGE,"E10.2.9"),sQuery(id+"F0.wireOp",EDGE,"E10.2.10"),sQuery(id+"F0.wireOp",EDGE,"E10.2.11"),sQuery(id+"F0.wireOp",EDGE,"E10.2.12"),sQuery(id+"F0.wireOp",EDGE,"E1"),sQuery(id+"F0.wireOp",EDGE,"E10.2.14"),sQuery(id+"F0.wireOp",EDGE,"E10.2.15"),sQuery(id+"F0.wireOp",EDGE,"E10.2.16"),sQuery(id+"F0.wireOp",EDGE,"E10.2.18"),sQuery(id+"F0.wireOp",EDGE,"E10.2.20"),sQuery(id+"F0.wireOp",EDGE,"E8.trimOffspring"),sQuery(id+"F0.wireOp",EDGE,"E0"),sQuery(id+"F0.wireOp",EDGE,"E10.1.6"),sQuery(id+"F0.wireOp",EDGE,"E11"),sQuery(id+"F0.wireOp",EDGE,"E12"),sQuery(id+"F0.wireOp",EDGE,"E13.1.0"),sQuery(id+"F0.wireOp",EDGE,"E13.1.1"),sQuery(id+"F0.wireOp",EDGE,"E13.2.0"),sQuery(id+"F0.wireOp",EDGE,"E13.2.1")])]}),"instanceName":"1"}),"instanceName":"1"});
            transform(context, id + "F9", {"entities" : qUnion([Q0]), "transformType" : TransformType.TRANSLATION_3D, "dx" : 68.8 * mm, "dy" : 0 * mm, "dz" : 0 * mm, "makeCopy" : true});
        }
        {
            var Q0;
            Q0=makeQuery(id+"F9.opPattern","COPY",BODY,{"derivedFrom":makeQuery(id+"F8.opPattern","COPY",BODY,{"derivedFrom":makeQuery(id+"F7.opPattern","COPY",BODY,{"derivedFrom":makeQuery(id+"F1.opExtrude","SWEPT_BODY",BODY,{"disambiguationData":[OSD([sQuery(id+"F0.wireOp",EDGE,"E2.0"),sQuery(id+"F0.wireOp",EDGE,"E2.1"),sQuery(id+"F0.wireOp",EDGE,"E2.2"),sQuery(id+"F0.wireOp",EDGE,"E2.3"),sQuery(id+"F0.wireOp",EDGE,"E2.4"),sQuery(id+"F0.wireOp",EDGE,"E2.5"),sQuery(id+"F0.wireOp",EDGE,"E3"),sQuery(id+"F0.wireOp",EDGE,"E4"),sQuery(id+"F0.wireOp",EDGE,"E5.0"),sQuery(id+"F0.wireOp",EDGE,"E5.1"),sQuery(id+"F0.wireOp",EDGE,"E5.3"),sQuery(id+"F0.wireOp",EDGE,"E5.4"),sQuery(id+"F0.wireOp",EDGE,"E5.5"),sQuery(id+"F0.wireOp",EDGE,"E6.trimOffspring"),sQuery(id+"F0.wireOp",EDGE,"E7.trimOffspring"),sQuery(id+"F0.wireOp",EDGE,"E9.trimOffspring"),sQuery(id+"F0.wireOp",EDGE,"E10.1.0"),sQuery(id+"F0.wireOp",EDGE,"E10.1.1"),sQuery(id+"F0.wireOp",EDGE,"E10.1.2"),sQuery(id+"F0.wireOp",EDGE,"E10.1.3"),sQuery(id+"F0.wireOp",EDGE,"E10.1.5"),sQuery(id+"F0.wireOp",EDGE,"E10.1.7"),sQuery(id+"F0.wireOp",EDGE,"E10.1.8"),sQuery(id+"F0.wireOp",EDGE,"E10.1.9"),sQuery(id+"F0.wireOp",EDGE,"E10.1.10"),sQuery(id+"F0.wireOp",EDGE,"E10.1.11"),sQuery(id+"F0.wireOp",EDGE,"E10.1.12"),sQuery(id+"F0.wireOp",EDGE,"E10.1.14"),sQuery(id+"F0.wireOp",EDGE,"E10.1.15"),sQuery(id+"F0.wireOp",EDGE,"E10.1.16"),sQuery(id+"F0.wireOp",EDGE,"E10.1.18"),sQuery(id+"F0.wireOp",EDGE,"E10.1.20"),sQuery(id+"F0.wireOp",EDGE,"E10.2.0"),sQuery(id+"F0.wireOp",EDGE,"E10.2.1"),sQuery(id+"F0.wireOp",EDGE,"E10.2.2"),sQuery(id+"F0.wireOp",EDGE,"E10.2.3"),sQuery(id+"F0.wireOp",EDGE,"E10.2.5"),sQuery(id+"F0.wireOp",EDGE,"E10.2.7"),sQuery(id+"F0.wireOp",EDGE,"E10.2.8"),sQuery(id+"F0.wireOp",EDGE,"E10.2.9"),sQuery(id+"F0.wireOp",EDGE,"E10.2.10"),sQuery(id+"F0.wireOp",EDGE,"E10.2.11"),sQuery(id+"F0.wireOp",EDGE,"E10.2.12"),sQuery(id+"F0.wireOp",EDGE,"E1"),sQuery(id+"F0.wireOp",EDGE,"E10.2.14"),sQuery(id+"F0.wireOp",EDGE,"E10.2.15"),sQuery(id+"F0.wireOp",EDGE,"E10.2.16"),sQuery(id+"F0.wireOp",EDGE,"E10.2.18"),sQuery(id+"F0.wireOp",EDGE,"E10.2.20"),sQuery(id+"F0.wireOp",EDGE,"E8.trimOffspring"),sQuery(id+"F0.wireOp",EDGE,"E0"),sQuery(id+"F0.wireOp",EDGE,"E10.1.6"),sQuery(id+"F0.wireOp",EDGE,"E11"),sQuery(id+"F0.wireOp",EDGE,"E12"),sQuery(id+"F0.wireOp",EDGE,"E13.1.0"),sQuery(id+"F0.wireOp",EDGE,"E13.1.1"),sQuery(id+"F0.wireOp",EDGE,"E13.2.0"),sQuery(id+"F0.wireOp",EDGE,"E13.2.1")])]}),"instanceName":"1"}),"instanceName":"1"}),"instanceName":"1"});
            transform(context, id + "F10", {"entities" : qUnion([Q0]), "transformType" : TransformType.TRANSLATION_3D, "dx" : 53.1 * mm, "dy" : -25.6 * mm, "dz" : 0 * mm, "makeCopy" : true});
        }
        {
            var Q0;
            Q0=makeQuery(id+"F10.opPattern","COPY",BODY,{"derivedFrom":makeQuery(id+"F9.opPattern","COPY",BODY,{"derivedFrom":makeQuery(id+"F8.opPattern","COPY",BODY,{"derivedFrom":makeQuery(id+"F7.opPattern","COPY",BODY,{"derivedFrom":makeQuery(id+"F1.opExtrude","SWEPT_BODY",BODY,{"disambiguationData":[OSD([sQuery(id+"F0.wireOp",EDGE,"E2.0"),sQuery(id+"F0.wireOp",EDGE,"E2.1"),sQuery(id+"F0.wireOp",EDGE,"E2.2"),sQuery(id+"F0.wireOp",EDGE,"E2.3"),sQuery(id+"F0.wireOp",EDGE,"E2.4"),sQuery(id+"F0.wireOp",EDGE,"E2.5"),sQuery(id+"F0.wireOp",EDGE,"E3"),sQuery(id+"F0.wireOp",EDGE,"E4"),sQuery(id+"F0.wireOp",EDGE,"E5.0"),sQuery(id+"F0.wireOp",EDGE,"E5.1"),sQuery(id+"F0.wireOp",EDGE,"E5.3"),sQuery(id+"F0.wireOp",EDGE,"E5.4"),sQuery(id+"F0.wireOp",EDGE,"E5.5"),sQuery(id+"F0.wireOp",EDGE,"E6.trimOffspring"),sQuery(id+"F0.wireOp",EDGE,"E7.trimOffspring"),sQuery(id+"F0.wireOp",EDGE,"E9.trimOffspring"),sQuery(id+"F0.wireOp",EDGE,"E10.1.0"),sQuery(id+"F0.wireOp",EDGE,"E10.1.1"),sQuery(id+"F0.wireOp",EDGE,"E10.1.2"),sQuery(id+"F0.wireOp",EDGE,"E10.1.3"),sQuery(id+"F0.wireOp",EDGE,"E10.1.5"),sQuery(id+"F0.wireOp",EDGE,"E10.1.7"),sQuery(id+"F0.wireOp",EDGE,"E10.1.8"),sQuery(id+"F0.wireOp",EDGE,"E10.1.9"),sQuery(id+"F0.wireOp",EDGE,"E10.1.10"),sQuery(id+"F0.wireOp",EDGE,"E10.1.11"),sQuery(id+"F0.wireOp",EDGE,"E10.1.12"),sQuery(id+"F0.wireOp",EDGE,"E10.1.14"),sQuery(id+"F0.wireOp",EDGE,"E10.1.15"),sQuery(id+"F0.wireOp",EDGE,"E10.1.16"),sQuery(id+"F0.wireOp",EDGE,"E10.1.18"),sQuery(id+"F0.wireOp",EDGE,"E10.1.20"),sQuery(id+"F0.wireOp",EDGE,"E10.2.0"),sQuery(id+"F0.wireOp",EDGE,"E10.2.1"),sQuery(id+"F0.wireOp",EDGE,"E10.2.2"),sQuery(id+"F0.wireOp",EDGE,"E10.2.3"),sQuery(id+"F0.wireOp",EDGE,"E10.2.5"),sQuery(id+"F0.wireOp",EDGE,"E10.2.7"),sQuery(id+"F0.wireOp",EDGE,"E10.2.8"),sQuery(id+"F0.wireOp",EDGE,"E10.2.9"),sQuery(id+"F0.wireOp",EDGE,"E10.2.10"),sQuery(id+"F0.wireOp",EDGE,"E10.2.11"),sQuery(id+"F0.wireOp",EDGE,"E10.2.12"),sQuery(id+"F0.wireOp",EDGE,"E1"),sQuery(id+"F0.wireOp",EDGE,"E10.2.14"),sQuery(id+"F0.wireOp",EDGE,"E10.2.15"),sQuery(id+"F0.wireOp",EDGE,"E10.2.16"),sQuery(id+"F0.wireOp",EDGE,"E10.2.18"),sQuery(id+"F0.wireOp",EDGE,"E10.2.20"),sQuery(id+"F0.wireOp",EDGE,"E8.trimOffspring"),sQuery(id+"F0.wireOp",EDGE,"E0"),sQuery(id+"F0.wireOp",EDGE,"E10.1.6"),sQuery(id+"F0.wireOp",EDGE,"E11"),sQuery(id+"F0.wireOp",EDGE,"E12"),sQuery(id+"F0.wireOp",EDGE,"E13.1.0"),sQuery(id+"F0.wireOp",EDGE,"E13.1.1"),sQuery(id+"F0.wireOp",EDGE,"E13.2.0"),sQuery(id+"F0.wireOp",EDGE,"E13.2.1")])]}),"instanceName":"1"}),"instanceName":"1"}),"instanceName":"1"}),"instanceName":"1"});
            var Q1;
            Q1=makeQuery(id+"F10.opPattern","COPY",EDGE,{"derivedFrom":makeQuery(id+"F9.opPattern","COPY",EDGE,{"derivedFrom":makeQuery(id+"F8.opPattern","COPY",EDGE,{"derivedFrom":makeQuery(id+"F7.opPattern","COPY",EDGE,{"derivedFrom":makeQuery(id+"F1.opExtrude","CAP_EDGE",EDGE,{"disambiguationData":[OSD([sQuery(id+"F0.wireOp",EDGE,"E1")])],"isStart":false}),"instanceName":"1"}),"instanceName":"1"}),"instanceName":"1"}),"instanceName":"1"});
            transform(context, id + "F11", {"entities" : qUnion([Q0]), "transformType" : TransformType.ROTATION, "transformAxis" : qUnion([Q1]), "angle" : 55 * degree, "oppositeDirection" : true, "makeCopy" : false});
        }
        {
            var Q0;
            Q0=makeQuery(id+"F10.opPattern","COPY",BODY,{"derivedFrom":makeQuery(id+"F9.opPattern","COPY",BODY,{"derivedFrom":makeQuery(id+"F8.opPattern","COPY",BODY,{"derivedFrom":makeQuery(id+"F7.opPattern","COPY",BODY,{"derivedFrom":makeQuery(id+"F1.opExtrude","SWEPT_BODY",BODY,{"disambiguationData":[OSD([sQuery(id+"F0.wireOp",EDGE,"E2.0"),sQuery(id+"F0.wireOp",EDGE,"E2.1"),sQuery(id+"F0.wireOp",EDGE,"E2.2"),sQuery(id+"F0.wireOp",EDGE,"E2.3"),sQuery(id+"F0.wireOp",EDGE,"E2.4"),sQuery(id+"F0.wireOp",EDGE,"E2.5"),sQuery(id+"F0.wireOp",EDGE,"E3"),sQuery(id+"F0.wireOp",EDGE,"E4"),sQuery(id+"F0.wireOp",EDGE,"E5.0"),sQuery(id+"F0.wireOp",EDGE,"E5.1"),sQuery(id+"F0.wireOp",EDGE,"E5.3"),sQuery(id+"F0.wireOp",EDGE,"E5.4"),sQuery(id+"F0.wireOp",EDGE,"E5.5"),sQuery(id+"F0.wireOp",EDGE,"E6.trimOffspring"),sQuery(id+"F0.wireOp",EDGE,"E7.trimOffspring"),sQuery(id+"F0.wireOp",EDGE,"E9.trimOffspring"),sQuery(id+"F0.wireOp",EDGE,"E10.1.0"),sQuery(id+"F0.wireOp",EDGE,"E10.1.1"),sQuery(id+"F0.wireOp",EDGE,"E10.1.2"),sQuery(id+"F0.wireOp",EDGE,"E10.1.3"),sQuery(id+"F0.wireOp",EDGE,"E10.1.5"),sQuery(id+"F0.wireOp",EDGE,"E10.1.7"),sQuery(id+"F0.wireOp",EDGE,"E10.1.8"),sQuery(id+"F0.wireOp",EDGE,"E10.1.9"),sQuery(id+"F0.wireOp",EDGE,"E10.1.10"),sQuery(id+"F0.wireOp",EDGE,"E10.1.11"),sQuery(id+"F0.wireOp",EDGE,"E10.1.12"),sQuery(id+"F0.wireOp",EDGE,"E10.1.14"),sQuery(id+"F0.wireOp",EDGE,"E10.1.15"),sQuery(id+"F0.wireOp",EDGE,"E10.1.16"),sQuery(id+"F0.wireOp",EDGE,"E10.1.18"),sQuery(id+"F0.wireOp",EDGE,"E10.1.20"),sQuery(id+"F0.wireOp",EDGE,"E10.2.0"),sQuery(id+"F0.wireOp",EDGE,"E10.2.1"),sQuery(id+"F0.wireOp",EDGE,"E10.2.2"),sQuery(id+"F0.wireOp",EDGE,"E10.2.3"),sQuery(id+"F0.wireOp",EDGE,"E10.2.5"),sQuery(id+"F0.wireOp",EDGE,"E10.2.7"),sQuery(id+"F0.wireOp",EDGE,"E10.2.8"),sQuery(id+"F0.wireOp",EDGE,"E10.2.9"),sQuery(id+"F0.wireOp",EDGE,"E10.2.10"),sQuery(id+"F0.wireOp",EDGE,"E10.2.11"),sQuery(id+"F0.wireOp",EDGE,"E10.2.12"),sQuery(id+"F0.wireOp",EDGE,"E1"),sQuery(id+"F0.wireOp",EDGE,"E10.2.14"),sQuery(id+"F0.wireOp",EDGE,"E10.2.15"),sQuery(id+"F0.wireOp",EDGE,"E10.2.16"),sQuery(id+"F0.wireOp",EDGE,"E10.2.18"),sQuery(id+"F0.wireOp",EDGE,"E10.2.20"),sQuery(id+"F0.wireOp",EDGE,"E8.trimOffspring"),sQuery(id+"F0.wireOp",EDGE,"E0"),sQuery(id+"F0.wireOp",EDGE,"E10.1.6"),sQuery(id+"F0.wireOp",EDGE,"E11"),sQuery(id+"F0.wireOp",EDGE,"E12"),sQuery(id+"F0.wireOp",EDGE,"E13.1.0"),sQuery(id+"F0.wireOp",EDGE,"E13.1.1"),sQuery(id+"F0.wireOp",EDGE,"E13.2.0"),sQuery(id+"F0.wireOp",EDGE,"E13.2.1")])]}),"instanceName":"1"}),"instanceName":"1"}),"instanceName":"1"}),"instanceName":"1"});
            transform(context, id + "F12", {"entities" : qUnion([Q0]), "transformType" : TransformType.TRANSLATION_3D, "dx" : 4.8 * mm, "dy" : 6 * mm, "dz" : 0 * mm, "makeCopy" : false});
        }
        {
            var Q0;
            Q0=makeQuery(id+"F1.opExtrude","SWEPT_BODY",BODY,{"disambiguationData":[OSD([sQuery(id+"F0.wireOp",EDGE,"E2.0"),sQuery(id+"F0.wireOp",EDGE,"E2.1"),sQuery(id+"F0.wireOp",EDGE,"E2.2"),sQuery(id+"F0.wireOp",EDGE,"E2.3"),sQuery(id+"F0.wireOp",EDGE,"E2.4"),sQuery(id+"F0.wireOp",EDGE,"E2.5"),sQuery(id+"F0.wireOp",EDGE,"E3"),sQuery(id+"F0.wireOp",EDGE,"E4"),sQuery(id+"F0.wireOp",EDGE,"E5.0"),sQuery(id+"F0.wireOp",EDGE,"E5.1"),sQuery(id+"F0.wireOp",EDGE,"E5.3"),sQuery(id+"F0.wireOp",EDGE,"E5.4"),sQuery(id+"F0.wireOp",EDGE,"E5.5"),sQuery(id+"F0.wireOp",EDGE,"E6.trimOffspring"),sQuery(id+"F0.wireOp",EDGE,"E7.trimOffspring"),sQuery(id+"F0.wireOp",EDGE,"E9.trimOffspring"),sQuery(id+"F0.wireOp",EDGE,"E10.1.0"),sQuery(id+"F0.wireOp",EDGE,"E10.1.1"),sQuery(id+"F0.wireOp",EDGE,"E10.1.2"),sQuery(id+"F0.wireOp",EDGE,"E10.1.3"),sQuery(id+"F0.wireOp",EDGE,"E10.1.5"),sQuery(id+"F0.wireOp",EDGE,"E10.1.7"),sQuery(id+"F0.wireOp",EDGE,"E10.1.8"),sQuery(id+"F0.wireOp",EDGE,"E10.1.9"),sQuery(id+"F0.wireOp",EDGE,"E10.1.10"),sQuery(id+"F0.wireOp",EDGE,"E10.1.11"),sQuery(id+"F0.wireOp",EDGE,"E10.1.12"),sQuery(id+"F0.wireOp",EDGE,"E10.1.14"),sQuery(id+"F0.wireOp",EDGE,"E10.1.15"),sQuery(id+"F0.wireOp",EDGE,"E10.1.16"),sQuery(id+"F0.wireOp",EDGE,"E10.1.18"),sQuery(id+"F0.wireOp",EDGE,"E10.1.20"),sQuery(id+"F0.wireOp",EDGE,"E10.2.0"),sQuery(id+"F0.wireOp",EDGE,"E10.2.1"),sQuery(id+"F0.wireOp",EDGE,"E10.2.2"),sQuery(id+"F0.wireOp",EDGE,"E10.2.3"),sQuery(id+"F0.wireOp",EDGE,"E10.2.5"),sQuery(id+"F0.wireOp",EDGE,"E10.2.7"),sQuery(id+"F0.wireOp",EDGE,"E10.2.8"),sQuery(id+"F0.wireOp",EDGE,"E10.2.9"),sQuery(id+"F0.wireOp",EDGE,"E10.2.10"),sQuery(id+"F0.wireOp",EDGE,"E10.2.11"),sQuery(id+"F0.wireOp",EDGE,"E10.2.12"),sQuery(id+"F0.wireOp",EDGE,"E1"),sQuery(id+"F0.wireOp",EDGE,"E10.2.14"),sQuery(id+"F0.wireOp",EDGE,"E10.2.15"),sQuery(id+"F0.wireOp",EDGE,"E10.2.16"),sQuery(id+"F0.wireOp",EDGE,"E10.2.18"),sQuery(id+"F0.wireOp",EDGE,"E10.2.20"),sQuery(id+"F0.wireOp",EDGE,"E8.trimOffspring"),sQuery(id+"F0.wireOp",EDGE,"E0"),sQuery(id+"F0.wireOp",EDGE,"E10.1.6"),sQuery(id+"F0.wireOp",EDGE,"E11"),sQuery(id+"F0.wireOp",EDGE,"E12"),sQuery(id+"F0.wireOp",EDGE,"E13.1.0"),sQuery(id+"F0.wireOp",EDGE,"E13.1.1"),sQuery(id+"F0.wireOp",EDGE,"E13.2.0"),sQuery(id+"F0.wireOp",EDGE,"E13.2.1")])]});
            transform(context, id + "F13", {"entities" : qUnion([Q0]), "transformType" : TransformType.TRANSLATION_3D, "dx" : 36.7 * mm, "dy" : -60.6 * mm, "dz" : 0 * mm, "makeCopy" : true});
        }
        {
            var Q0;
            Q0=makeQuery(id+"F13.opPattern","COPY",BODY,{"derivedFrom":makeQuery(id+"F1.opExtrude","SWEPT_BODY",BODY,{"disambiguationData":[OSD([sQuery(id+"F0.wireOp",EDGE,"E2.0"),sQuery(id+"F0.wireOp",EDGE,"E2.1"),sQuery(id+"F0.wireOp",EDGE,"E2.2"),sQuery(id+"F0.wireOp",EDGE,"E2.3"),sQuery(id+"F0.wireOp",EDGE,"E2.4"),sQuery(id+"F0.wireOp",EDGE,"E2.5"),sQuery(id+"F0.wireOp",EDGE,"E3"),sQuery(id+"F0.wireOp",EDGE,"E4"),sQuery(id+"F0.wireOp",EDGE,"E5.0"),sQuery(id+"F0.wireOp",EDGE,"E5.1"),sQuery(id+"F0.wireOp",EDGE,"E5.3"),sQuery(id+"F0.wireOp",EDGE,"E5.4"),sQuery(id+"F0.wireOp",EDGE,"E5.5"),sQuery(id+"F0.wireOp",EDGE,"E6.trimOffspring"),sQuery(id+"F0.wireOp",EDGE,"E7.trimOffspring"),sQuery(id+"F0.wireOp",EDGE,"E9.trimOffspring"),sQuery(id+"F0.wireOp",EDGE,"E10.1.0"),sQuery(id+"F0.wireOp",EDGE,"E10.1.1"),sQuery(id+"F0.wireOp",EDGE,"E10.1.2"),sQuery(id+"F0.wireOp",EDGE,"E10.1.3"),sQuery(id+"F0.wireOp",EDGE,"E10.1.5"),sQuery(id+"F0.wireOp",EDGE,"E10.1.7"),sQuery(id+"F0.wireOp",EDGE,"E10.1.8"),sQuery(id+"F0.wireOp",EDGE,"E10.1.9"),sQuery(id+"F0.wireOp",EDGE,"E10.1.10"),sQuery(id+"F0.wireOp",EDGE,"E10.1.11"),sQuery(id+"F0.wireOp",EDGE,"E10.1.12"),sQuery(id+"F0.wireOp",EDGE,"E10.1.14"),sQuery(id+"F0.wireOp",EDGE,"E10.1.15"),sQuery(id+"F0.wireOp",EDGE,"E10.1.16"),sQuery(id+"F0.wireOp",EDGE,"E10.1.18"),sQuery(id+"F0.wireOp",EDGE,"E10.1.20"),sQuery(id+"F0.wireOp",EDGE,"E10.2.0"),sQuery(id+"F0.wireOp",EDGE,"E10.2.1"),sQuery(id+"F0.wireOp",EDGE,"E10.2.2"),sQuery(id+"F0.wireOp",EDGE,"E10.2.3"),sQuery(id+"F0.wireOp",EDGE,"E10.2.5"),sQuery(id+"F0.wireOp",EDGE,"E10.2.7"),sQuery(id+"F0.wireOp",EDGE,"E10.2.8"),sQuery(id+"F0.wireOp",EDGE,"E10.2.9"),sQuery(id+"F0.wireOp",EDGE,"E10.2.10"),sQuery(id+"F0.wireOp",EDGE,"E10.2.11"),sQuery(id+"F0.wireOp",EDGE,"E10.2.12"),sQuery(id+"F0.wireOp",EDGE,"E1"),sQuery(id+"F0.wireOp",EDGE,"E10.2.14"),sQuery(id+"F0.wireOp",EDGE,"E10.2.15"),sQuery(id+"F0.wireOp",EDGE,"E10.2.16"),sQuery(id+"F0.wireOp",EDGE,"E10.2.18"),sQuery(id+"F0.wireOp",EDGE,"E10.2.20"),sQuery(id+"F0.wireOp",EDGE,"E8.trimOffspring"),sQuery(id+"F0.wireOp",EDGE,"E0"),sQuery(id+"F0.wireOp",EDGE,"E10.1.6"),sQuery(id+"F0.wireOp",EDGE,"E11"),sQuery(id+"F0.wireOp",EDGE,"E12"),sQuery(id+"F0.wireOp",EDGE,"E13.1.0"),sQuery(id+"F0.wireOp",EDGE,"E13.1.1"),sQuery(id+"F0.wireOp",EDGE,"E13.2.0"),sQuery(id+"F0.wireOp",EDGE,"E13.2.1")])]}),"instanceName":"1"});
            var Q1;
            Q1=makeQuery(id+"F13.opPattern","COPY",EDGE,{"derivedFrom":makeQuery(id+"F1.opExtrude","CAP_EDGE",EDGE,{"disambiguationData":[OSD([sQuery(id+"F0.wireOp",EDGE,"E1")])],"isStart":false}),"instanceName":"1"});
            transform(context, id + "F14", {"entities" : qUnion([Q0]), "transformType" : TransformType.ROTATION, "transformAxis" : qUnion([Q1]), "angle" : 45 * degree, "oppositeDirection" : true, "makeCopy" : false});
        }
        {
            var Q0;
            Q0=makeQuery(id+"F13.opPattern","COPY",BODY,{"derivedFrom":makeQuery(id+"F1.opExtrude","SWEPT_BODY",BODY,{"disambiguationData":[OSD([sQuery(id+"F0.wireOp",EDGE,"E2.0"),sQuery(id+"F0.wireOp",EDGE,"E2.1"),sQuery(id+"F0.wireOp",EDGE,"E2.2"),sQuery(id+"F0.wireOp",EDGE,"E2.3"),sQuery(id+"F0.wireOp",EDGE,"E2.4"),sQuery(id+"F0.wireOp",EDGE,"E2.5"),sQuery(id+"F0.wireOp",EDGE,"E3"),sQuery(id+"F0.wireOp",EDGE,"E4"),sQuery(id+"F0.wireOp",EDGE,"E5.0"),sQuery(id+"F0.wireOp",EDGE,"E5.1"),sQuery(id+"F0.wireOp",EDGE,"E5.3"),sQuery(id+"F0.wireOp",EDGE,"E5.4"),sQuery(id+"F0.wireOp",EDGE,"E5.5"),sQuery(id+"F0.wireOp",EDGE,"E6.trimOffspring"),sQuery(id+"F0.wireOp",EDGE,"E7.trimOffspring"),sQuery(id+"F0.wireOp",EDGE,"E9.trimOffspring"),sQuery(id+"F0.wireOp",EDGE,"E10.1.0"),sQuery(id+"F0.wireOp",EDGE,"E10.1.1"),sQuery(id+"F0.wireOp",EDGE,"E10.1.2"),sQuery(id+"F0.wireOp",EDGE,"E10.1.3"),sQuery(id+"F0.wireOp",EDGE,"E10.1.5"),sQuery(id+"F0.wireOp",EDGE,"E10.1.7"),sQuery(id+"F0.wireOp",EDGE,"E10.1.8"),sQuery(id+"F0.wireOp",EDGE,"E10.1.9"),sQuery(id+"F0.wireOp",EDGE,"E10.1.10"),sQuery(id+"F0.wireOp",EDGE,"E10.1.11"),sQuery(id+"F0.wireOp",EDGE,"E10.1.12"),sQuery(id+"F0.wireOp",EDGE,"E10.1.14"),sQuery(id+"F0.wireOp",EDGE,"E10.1.15"),sQuery(id+"F0.wireOp",EDGE,"E10.1.16"),sQuery(id+"F0.wireOp",EDGE,"E10.1.18"),sQuery(id+"F0.wireOp",EDGE,"E10.1.20"),sQuery(id+"F0.wireOp",EDGE,"E10.2.0"),sQuery(id+"F0.wireOp",EDGE,"E10.2.1"),sQuery(id+"F0.wireOp",EDGE,"E10.2.2"),sQuery(id+"F0.wireOp",EDGE,"E10.2.3"),sQuery(id+"F0.wireOp",EDGE,"E10.2.5"),sQuery(id+"F0.wireOp",EDGE,"E10.2.7"),sQuery(id+"F0.wireOp",EDGE,"E10.2.8"),sQuery(id+"F0.wireOp",EDGE,"E10.2.9"),sQuery(id+"F0.wireOp",EDGE,"E10.2.10"),sQuery(id+"F0.wireOp",EDGE,"E10.2.11"),sQuery(id+"F0.wireOp",EDGE,"E10.2.12"),sQuery(id+"F0.wireOp",EDGE,"E1"),sQuery(id+"F0.wireOp",EDGE,"E10.2.14"),sQuery(id+"F0.wireOp",EDGE,"E10.2.15"),sQuery(id+"F0.wireOp",EDGE,"E10.2.16"),sQuery(id+"F0.wireOp",EDGE,"E10.2.18"),sQuery(id+"F0.wireOp",EDGE,"E10.2.20"),sQuery(id+"F0.wireOp",EDGE,"E8.trimOffspring"),sQuery(id+"F0.wireOp",EDGE,"E0"),sQuery(id+"F0.wireOp",EDGE,"E10.1.6"),sQuery(id+"F0.wireOp",EDGE,"E11"),sQuery(id+"F0.wireOp",EDGE,"E12"),sQuery(id+"F0.wireOp",EDGE,"E13.1.0"),sQuery(id+"F0.wireOp",EDGE,"E13.1.1"),sQuery(id+"F0.wireOp",EDGE,"E13.2.0"),sQuery(id+"F0.wireOp",EDGE,"E13.2.1")])]}),"instanceName":"1"});
            transform(context, id + "F15", {"entities" : qUnion([Q0]), "transformType" : TransformType.TRANSLATION_3D, "dx" : -10.1 * mm, "dy" : 10.3 * mm, "dz" : 0 * mm, "makeCopy" : false});
        }
        {
            var Q0;
            Q0=makeQuery(id+"F13.opPattern","COPY",BODY,{"derivedFrom":makeQuery(id+"F1.opExtrude","SWEPT_BODY",BODY,{"disambiguationData":[OSD([sQuery(id+"F0.wireOp",EDGE,"E2.0"),sQuery(id+"F0.wireOp",EDGE,"E2.1"),sQuery(id+"F0.wireOp",EDGE,"E2.2"),sQuery(id+"F0.wireOp",EDGE,"E2.3"),sQuery(id+"F0.wireOp",EDGE,"E2.4"),sQuery(id+"F0.wireOp",EDGE,"E2.5"),sQuery(id+"F0.wireOp",EDGE,"E3"),sQuery(id+"F0.wireOp",EDGE,"E4"),sQuery(id+"F0.wireOp",EDGE,"E5.0"),sQuery(id+"F0.wireOp",EDGE,"E5.1"),sQuery(id+"F0.wireOp",EDGE,"E5.3"),sQuery(id+"F0.wireOp",EDGE,"E5.4"),sQuery(id+"F0.wireOp",EDGE,"E5.5"),sQuery(id+"F0.wireOp",EDGE,"E6.trimOffspring"),sQuery(id+"F0.wireOp",EDGE,"E7.trimOffspring"),sQuery(id+"F0.wireOp",EDGE,"E9.trimOffspring"),sQuery(id+"F0.wireOp",EDGE,"E10.1.0"),sQuery(id+"F0.wireOp",EDGE,"E10.1.1"),sQuery(id+"F0.wireOp",EDGE,"E10.1.2"),sQuery(id+"F0.wireOp",EDGE,"E10.1.3"),sQuery(id+"F0.wireOp",EDGE,"E10.1.5"),sQuery(id+"F0.wireOp",EDGE,"E10.1.7"),sQuery(id+"F0.wireOp",EDGE,"E10.1.8"),sQuery(id+"F0.wireOp",EDGE,"E10.1.9"),sQuery(id+"F0.wireOp",EDGE,"E10.1.10"),sQuery(id+"F0.wireOp",EDGE,"E10.1.11"),sQuery(id+"F0.wireOp",EDGE,"E10.1.12"),sQuery(id+"F0.wireOp",EDGE,"E10.1.14"),sQuery(id+"F0.wireOp",EDGE,"E10.1.15"),sQuery(id+"F0.wireOp",EDGE,"E10.1.16"),sQuery(id+"F0.wireOp",EDGE,"E10.1.18"),sQuery(id+"F0.wireOp",EDGE,"E10.1.20"),sQuery(id+"F0.wireOp",EDGE,"E10.2.0"),sQuery(id+"F0.wireOp",EDGE,"E10.2.1"),sQuery(id+"F0.wireOp",EDGE,"E10.2.2"),sQuery(id+"F0.wireOp",EDGE,"E10.2.3"),sQuery(id+"F0.wireOp",EDGE,"E10.2.5"),sQuery(id+"F0.wireOp",EDGE,"E10.2.7"),sQuery(id+"F0.wireOp",EDGE,"E10.2.8"),sQuery(id+"F0.wireOp",EDGE,"E10.2.9"),sQuery(id+"F0.wireOp",EDGE,"E10.2.10"),sQuery(id+"F0.wireOp",EDGE,"E10.2.11"),sQuery(id+"F0.wireOp",EDGE,"E10.2.12"),sQuery(id+"F0.wireOp",EDGE,"E1"),sQuery(id+"F0.wireOp",EDGE,"E10.2.14"),sQuery(id+"F0.wireOp",EDGE,"E10.2.15"),sQuery(id+"F0.wireOp",EDGE,"E10.2.16"),sQuery(id+"F0.wireOp",EDGE,"E10.2.18"),sQuery(id+"F0.wireOp",EDGE,"E10.2.20"),sQuery(id+"F0.wireOp",EDGE,"E8.trimOffspring"),sQuery(id+"F0.wireOp",EDGE,"E0"),sQuery(id+"F0.wireOp",EDGE,"E10.1.6"),sQuery(id+"F0.wireOp",EDGE,"E11"),sQuery(id+"F0.wireOp",EDGE,"E12"),sQuery(id+"F0.wireOp",EDGE,"E13.1.0"),sQuery(id+"F0.wireOp",EDGE,"E13.1.1"),sQuery(id+"F0.wireOp",EDGE,"E13.2.0"),sQuery(id+"F0.wireOp",EDGE,"E13.2.1")])]}),"instanceName":"1"});
            var Q1;
            Q1=makeQuery(id+"F13.opPattern","COPY",EDGE,{"derivedFrom":makeQuery(id+"F1.opExtrude","CAP_EDGE",EDGE,{"disambiguationData":[OSD([sQuery(id+"F0.wireOp",EDGE,"E1")])],"isStart":false}),"instanceName":"1"});
            transform(context, id + "F16", {"entities" : qUnion([Q0]), "transformType" : TransformType.ROTATION, "transformAxis" : qUnion([Q1]), "angle" : 15 * degree, "oppositeDirection" : true, "makeCopy" : false});
        }
        {
            var Q0;
            Q0=makeQuery(id+"F13.opPattern","COPY",BODY,{"derivedFrom":makeQuery(id+"F1.opExtrude","SWEPT_BODY",BODY,{"disambiguationData":[OSD([sQuery(id+"F0.wireOp",EDGE,"E2.0"),sQuery(id+"F0.wireOp",EDGE,"E2.1"),sQuery(id+"F0.wireOp",EDGE,"E2.2"),sQuery(id+"F0.wireOp",EDGE,"E2.3"),sQuery(id+"F0.wireOp",EDGE,"E2.4"),sQuery(id+"F0.wireOp",EDGE,"E2.5"),sQuery(id+"F0.wireOp",EDGE,"E3"),sQuery(id+"F0.wireOp",EDGE,"E4"),sQuery(id+"F0.wireOp",EDGE,"E5.0"),sQuery(id+"F0.wireOp",EDGE,"E5.1"),sQuery(id+"F0.wireOp",EDGE,"E5.3"),sQuery(id+"F0.wireOp",EDGE,"E5.4"),sQuery(id+"F0.wireOp",EDGE,"E5.5"),sQuery(id+"F0.wireOp",EDGE,"E6.trimOffspring"),sQuery(id+"F0.wireOp",EDGE,"E7.trimOffspring"),sQuery(id+"F0.wireOp",EDGE,"E9.trimOffspring"),sQuery(id+"F0.wireOp",EDGE,"E10.1.0"),sQuery(id+"F0.wireOp",EDGE,"E10.1.1"),sQuery(id+"F0.wireOp",EDGE,"E10.1.2"),sQuery(id+"F0.wireOp",EDGE,"E10.1.3"),sQuery(id+"F0.wireOp",EDGE,"E10.1.5"),sQuery(id+"F0.wireOp",EDGE,"E10.1.7"),sQuery(id+"F0.wireOp",EDGE,"E10.1.8"),sQuery(id+"F0.wireOp",EDGE,"E10.1.9"),sQuery(id+"F0.wireOp",EDGE,"E10.1.10"),sQuery(id+"F0.wireOp",EDGE,"E10.1.11"),sQuery(id+"F0.wireOp",EDGE,"E10.1.12"),sQuery(id+"F0.wireOp",EDGE,"E10.1.14"),sQuery(id+"F0.wireOp",EDGE,"E10.1.15"),sQuery(id+"F0.wireOp",EDGE,"E10.1.16"),sQuery(id+"F0.wireOp",EDGE,"E10.1.18"),sQuery(id+"F0.wireOp",EDGE,"E10.1.20"),sQuery(id+"F0.wireOp",EDGE,"E10.2.0"),sQuery(id+"F0.wireOp",EDGE,"E10.2.1"),sQuery(id+"F0.wireOp",EDGE,"E10.2.2"),sQuery(id+"F0.wireOp",EDGE,"E10.2.3"),sQuery(id+"F0.wireOp",EDGE,"E10.2.5"),sQuery(id+"F0.wireOp",EDGE,"E10.2.7"),sQuery(id+"F0.wireOp",EDGE,"E10.2.8"),sQuery(id+"F0.wireOp",EDGE,"E10.2.9"),sQuery(id+"F0.wireOp",EDGE,"E10.2.10"),sQuery(id+"F0.wireOp",EDGE,"E10.2.11"),sQuery(id+"F0.wireOp",EDGE,"E10.2.12"),sQuery(id+"F0.wireOp",EDGE,"E1"),sQuery(id+"F0.wireOp",EDGE,"E10.2.14"),sQuery(id+"F0.wireOp",EDGE,"E10.2.15"),sQuery(id+"F0.wireOp",EDGE,"E10.2.16"),sQuery(id+"F0.wireOp",EDGE,"E10.2.18"),sQuery(id+"F0.wireOp",EDGE,"E10.2.20"),sQuery(id+"F0.wireOp",EDGE,"E8.trimOffspring"),sQuery(id+"F0.wireOp",EDGE,"E0"),sQuery(id+"F0.wireOp",EDGE,"E10.1.6"),sQuery(id+"F0.wireOp",EDGE,"E11"),sQuery(id+"F0.wireOp",EDGE,"E12"),sQuery(id+"F0.wireOp",EDGE,"E13.1.0"),sQuery(id+"F0.wireOp",EDGE,"E13.1.1"),sQuery(id+"F0.wireOp",EDGE,"E13.2.0"),sQuery(id+"F0.wireOp",EDGE,"E13.2.1")])]}),"instanceName":"1"});
            transform(context, id + "F17", {"entities" : qUnion([Q0]), "transformType" : TransformType.TRANSLATION_3D, "dx" : 1.6 * mm, "dy" : -3.2 * mm, "dz" : 0 * mm, "makeCopy" : false});
        }
        {
            var Q0;
            Q0=makeQuery(id+"F13.opPattern","COPY",BODY,{"derivedFrom":makeQuery(id+"F1.opExtrude","SWEPT_BODY",BODY,{"disambiguationData":[OSD([sQuery(id+"F0.wireOp",EDGE,"E2.0"),sQuery(id+"F0.wireOp",EDGE,"E2.1"),sQuery(id+"F0.wireOp",EDGE,"E2.2"),sQuery(id+"F0.wireOp",EDGE,"E2.3"),sQuery(id+"F0.wireOp",EDGE,"E2.4"),sQuery(id+"F0.wireOp",EDGE,"E2.5"),sQuery(id+"F0.wireOp",EDGE,"E3"),sQuery(id+"F0.wireOp",EDGE,"E4"),sQuery(id+"F0.wireOp",EDGE,"E5.0"),sQuery(id+"F0.wireOp",EDGE,"E5.1"),sQuery(id+"F0.wireOp",EDGE,"E5.3"),sQuery(id+"F0.wireOp",EDGE,"E5.4"),sQuery(id+"F0.wireOp",EDGE,"E5.5"),sQuery(id+"F0.wireOp",EDGE,"E6.trimOffspring"),sQuery(id+"F0.wireOp",EDGE,"E7.trimOffspring"),sQuery(id+"F0.wireOp",EDGE,"E9.trimOffspring"),sQuery(id+"F0.wireOp",EDGE,"E10.1.0"),sQuery(id+"F0.wireOp",EDGE,"E10.1.1"),sQuery(id+"F0.wireOp",EDGE,"E10.1.2"),sQuery(id+"F0.wireOp",EDGE,"E10.1.3"),sQuery(id+"F0.wireOp",EDGE,"E10.1.5"),sQuery(id+"F0.wireOp",EDGE,"E10.1.7"),sQuery(id+"F0.wireOp",EDGE,"E10.1.8"),sQuery(id+"F0.wireOp",EDGE,"E10.1.9"),sQuery(id+"F0.wireOp",EDGE,"E10.1.10"),sQuery(id+"F0.wireOp",EDGE,"E10.1.11"),sQuery(id+"F0.wireOp",EDGE,"E10.1.12"),sQuery(id+"F0.wireOp",EDGE,"E10.1.14"),sQuery(id+"F0.wireOp",EDGE,"E10.1.15"),sQuery(id+"F0.wireOp",EDGE,"E10.1.16"),sQuery(id+"F0.wireOp",EDGE,"E10.1.18"),sQuery(id+"F0.wireOp",EDGE,"E10.1.20"),sQuery(id+"F0.wireOp",EDGE,"E10.2.0"),sQuery(id+"F0.wireOp",EDGE,"E10.2.1"),sQuery(id+"F0.wireOp",EDGE,"E10.2.2"),sQuery(id+"F0.wireOp",EDGE,"E10.2.3"),sQuery(id+"F0.wireOp",EDGE,"E10.2.5"),sQuery(id+"F0.wireOp",EDGE,"E10.2.7"),sQuery(id+"F0.wireOp",EDGE,"E10.2.8"),sQuery(id+"F0.wireOp",EDGE,"E10.2.9"),sQuery(id+"F0.wireOp",EDGE,"E10.2.10"),sQuery(id+"F0.wireOp",EDGE,"E10.2.11"),sQuery(id+"F0.wireOp",EDGE,"E10.2.12"),sQuery(id+"F0.wireOp",EDGE,"E1"),sQuery(id+"F0.wireOp",EDGE,"E10.2.14"),sQuery(id+"F0.wireOp",EDGE,"E10.2.15"),sQuery(id+"F0.wireOp",EDGE,"E10.2.16"),sQuery(id+"F0.wireOp",EDGE,"E10.2.18"),sQuery(id+"F0.wireOp",EDGE,"E10.2.20"),sQuery(id+"F0.wireOp",EDGE,"E8.trimOffspring"),sQuery(id+"F0.wireOp",EDGE,"E0"),sQuery(id+"F0.wireOp",EDGE,"E10.1.6"),sQuery(id+"F0.wireOp",EDGE,"E11"),sQuery(id+"F0.wireOp",EDGE,"E12"),sQuery(id+"F0.wireOp",EDGE,"E13.1.0"),sQuery(id+"F0.wireOp",EDGE,"E13.1.1"),sQuery(id+"F0.wireOp",EDGE,"E13.2.0"),sQuery(id+"F0.wireOp",EDGE,"E13.2.1")])]}),"instanceName":"1"});
            transform(context, id + "F18", {"entities" : qUnion([Q0]), "transformType" : TransformType.TRANSLATION_3D, "dx" : 69.1 * mm, "dy" : 0 * mm, "dz" : 0 * mm, "makeCopy" : true});
        }
        {
            var Q0;
            Q0=makeQuery(id+"F18.opPattern","COPY",BODY,{"derivedFrom":makeQuery(id+"F13.opPattern","COPY",BODY,{"derivedFrom":makeQuery(id+"F1.opExtrude","SWEPT_BODY",BODY,{"disambiguationData":[OSD([sQuery(id+"F0.wireOp",EDGE,"E2.0"),sQuery(id+"F0.wireOp",EDGE,"E2.1"),sQuery(id+"F0.wireOp",EDGE,"E2.2"),sQuery(id+"F0.wireOp",EDGE,"E2.3"),sQuery(id+"F0.wireOp",EDGE,"E2.4"),sQuery(id+"F0.wireOp",EDGE,"E2.5"),sQuery(id+"F0.wireOp",EDGE,"E3"),sQuery(id+"F0.wireOp",EDGE,"E4"),sQuery(id+"F0.wireOp",EDGE,"E5.0"),sQuery(id+"F0.wireOp",EDGE,"E5.1"),sQuery(id+"F0.wireOp",EDGE,"E5.3"),sQuery(id+"F0.wireOp",EDGE,"E5.4"),sQuery(id+"F0.wireOp",EDGE,"E5.5"),sQuery(id+"F0.wireOp",EDGE,"E6.trimOffspring"),sQuery(id+"F0.wireOp",EDGE,"E7.trimOffspring"),sQuery(id+"F0.wireOp",EDGE,"E9.trimOffspring"),sQuery(id+"F0.wireOp",EDGE,"E10.1.0"),sQuery(id+"F0.wireOp",EDGE,"E10.1.1"),sQuery(id+"F0.wireOp",EDGE,"E10.1.2"),sQuery(id+"F0.wireOp",EDGE,"E10.1.3"),sQuery(id+"F0.wireOp",EDGE,"E10.1.5"),sQuery(id+"F0.wireOp",EDGE,"E10.1.7"),sQuery(id+"F0.wireOp",EDGE,"E10.1.8"),sQuery(id+"F0.wireOp",EDGE,"E10.1.9"),sQuery(id+"F0.wireOp",EDGE,"E10.1.10"),sQuery(id+"F0.wireOp",EDGE,"E10.1.11"),sQuery(id+"F0.wireOp",EDGE,"E10.1.12"),sQuery(id+"F0.wireOp",EDGE,"E10.1.14"),sQuery(id+"F0.wireOp",EDGE,"E10.1.15"),sQuery(id+"F0.wireOp",EDGE,"E10.1.16"),sQuery(id+"F0.wireOp",EDGE,"E10.1.18"),sQuery(id+"F0.wireOp",EDGE,"E10.1.20"),sQuery(id+"F0.wireOp",EDGE,"E10.2.0"),sQuery(id+"F0.wireOp",EDGE,"E10.2.1"),sQuery(id+"F0.wireOp",EDGE,"E10.2.2"),sQuery(id+"F0.wireOp",EDGE,"E10.2.3"),sQuery(id+"F0.wireOp",EDGE,"E10.2.5"),sQuery(id+"F0.wireOp",EDGE,"E10.2.7"),sQuery(id+"F0.wireOp",EDGE,"E10.2.8"),sQuery(id+"F0.wireOp",EDGE,"E10.2.9"),sQuery(id+"F0.wireOp",EDGE,"E10.2.10"),sQuery(id+"F0.wireOp",EDGE,"E10.2.11"),sQuery(id+"F0.wireOp",EDGE,"E10.2.12"),sQuery(id+"F0.wireOp",EDGE,"E1"),sQuery(id+"F0.wireOp",EDGE,"E10.2.14"),sQuery(id+"F0.wireOp",EDGE,"E10.2.15"),sQuery(id+"F0.wireOp",EDGE,"E10.2.16"),sQuery(id+"F0.wireOp",EDGE,"E10.2.18"),sQuery(id+"F0.wireOp",EDGE,"E10.2.20"),sQuery(id+"F0.wireOp",EDGE,"E8.trimOffspring"),sQuery(id+"F0.wireOp",EDGE,"E0"),sQuery(id+"F0.wireOp",EDGE,"E10.1.6"),sQuery(id+"F0.wireOp",EDGE,"E11"),sQuery(id+"F0.wireOp",EDGE,"E12"),sQuery(id+"F0.wireOp",EDGE,"E13.1.0"),sQuery(id+"F0.wireOp",EDGE,"E13.1.1"),sQuery(id+"F0.wireOp",EDGE,"E13.2.0"),sQuery(id+"F0.wireOp",EDGE,"E13.2.1")])]}),"instanceName":"1"}),"instanceName":"1"});
            transform(context, id + "F19", {"entities" : qUnion([Q0]), "transformType" : TransformType.TRANSLATION_3D, "dx" : 69.1 * mm, "dy" : 0 * mm, "dz" : 0 * mm, "makeCopy" : true});
        }
        {
            var Q0;
            Q0=makeQuery(id+"F19.opPattern","COPY",BODY,{"derivedFrom":makeQuery(id+"F18.opPattern","COPY",BODY,{"derivedFrom":makeQuery(id+"F13.opPattern","COPY",BODY,{"derivedFrom":makeQuery(id+"F1.opExtrude","SWEPT_BODY",BODY,{"disambiguationData":[OSD([sQuery(id+"F0.wireOp",EDGE,"E2.0"),sQuery(id+"F0.wireOp",EDGE,"E2.1"),sQuery(id+"F0.wireOp",EDGE,"E2.2"),sQuery(id+"F0.wireOp",EDGE,"E2.3"),sQuery(id+"F0.wireOp",EDGE,"E2.4"),sQuery(id+"F0.wireOp",EDGE,"E2.5"),sQuery(id+"F0.wireOp",EDGE,"E3"),sQuery(id+"F0.wireOp",EDGE,"E4"),sQuery(id+"F0.wireOp",EDGE,"E5.0"),sQuery(id+"F0.wireOp",EDGE,"E5.1"),sQuery(id+"F0.wireOp",EDGE,"E5.3"),sQuery(id+"F0.wireOp",EDGE,"E5.4"),sQuery(id+"F0.wireOp",EDGE,"E5.5"),sQuery(id+"F0.wireOp",EDGE,"E6.trimOffspring"),sQuery(id+"F0.wireOp",EDGE,"E7.trimOffspring"),sQuery(id+"F0.wireOp",EDGE,"E9.trimOffspring"),sQuery(id+"F0.wireOp",EDGE,"E10.1.0"),sQuery(id+"F0.wireOp",EDGE,"E10.1.1"),sQuery(id+"F0.wireOp",EDGE,"E10.1.2"),sQuery(id+"F0.wireOp",EDGE,"E10.1.3"),sQuery(id+"F0.wireOp",EDGE,"E10.1.5"),sQuery(id+"F0.wireOp",EDGE,"E10.1.7"),sQuery(id+"F0.wireOp",EDGE,"E10.1.8"),sQuery(id+"F0.wireOp",EDGE,"E10.1.9"),sQuery(id+"F0.wireOp",EDGE,"E10.1.10"),sQuery(id+"F0.wireOp",EDGE,"E10.1.11"),sQuery(id+"F0.wireOp",EDGE,"E10.1.12"),sQuery(id+"F0.wireOp",EDGE,"E10.1.14"),sQuery(id+"F0.wireOp",EDGE,"E10.1.15"),sQuery(id+"F0.wireOp",EDGE,"E10.1.16"),sQuery(id+"F0.wireOp",EDGE,"E10.1.18"),sQuery(id+"F0.wireOp",EDGE,"E10.1.20"),sQuery(id+"F0.wireOp",EDGE,"E10.2.0"),sQuery(id+"F0.wireOp",EDGE,"E10.2.1"),sQuery(id+"F0.wireOp",EDGE,"E10.2.2"),sQuery(id+"F0.wireOp",EDGE,"E10.2.3"),sQuery(id+"F0.wireOp",EDGE,"E10.2.5"),sQuery(id+"F0.wireOp",EDGE,"E10.2.7"),sQuery(id+"F0.wireOp",EDGE,"E10.2.8"),sQuery(id+"F0.wireOp",EDGE,"E10.2.9"),sQuery(id+"F0.wireOp",EDGE,"E10.2.10"),sQuery(id+"F0.wireOp",EDGE,"E10.2.11"),sQuery(id+"F0.wireOp",EDGE,"E10.2.12"),sQuery(id+"F0.wireOp",EDGE,"E1"),sQuery(id+"F0.wireOp",EDGE,"E10.2.14"),sQuery(id+"F0.wireOp",EDGE,"E10.2.15"),sQuery(id+"F0.wireOp",EDGE,"E10.2.16"),sQuery(id+"F0.wireOp",EDGE,"E10.2.18"),sQuery(id+"F0.wireOp",EDGE,"E10.2.20"),sQuery(id+"F0.wireOp",EDGE,"E8.trimOffspring"),sQuery(id+"F0.wireOp",EDGE,"E0"),sQuery(id+"F0.wireOp",EDGE,"E10.1.6"),sQuery(id+"F0.wireOp",EDGE,"E11"),sQuery(id+"F0.wireOp",EDGE,"E12"),sQuery(id+"F0.wireOp",EDGE,"E13.1.0"),sQuery(id+"F0.wireOp",EDGE,"E13.1.1"),sQuery(id+"F0.wireOp",EDGE,"E13.2.0"),sQuery(id+"F0.wireOp",EDGE,"E13.2.1")])]}),"instanceName":"1"}),"instanceName":"1"}),"instanceName":"1"});
            transform(context, id + "F20", {"entities" : qUnion([Q0]), "transformType" : TransformType.TRANSLATION_3D, "dx" : 69.1 * mm, "dy" : 0 * mm, "dz" : 0 * mm, "makeCopy" : true});
        }
        {
            var Q0;
            Q0=makeQuery(id+"F20.opPattern","COPY",BODY,{"derivedFrom":makeQuery(id+"F19.opPattern","COPY",BODY,{"derivedFrom":makeQuery(id+"F18.opPattern","COPY",BODY,{"derivedFrom":makeQuery(id+"F13.opPattern","COPY",BODY,{"derivedFrom":makeQuery(id+"F1.opExtrude","SWEPT_BODY",BODY,{"disambiguationData":[OSD([sQuery(id+"F0.wireOp",EDGE,"E2.0"),sQuery(id+"F0.wireOp",EDGE,"E2.1"),sQuery(id+"F0.wireOp",EDGE,"E2.2"),sQuery(id+"F0.wireOp",EDGE,"E2.3"),sQuery(id+"F0.wireOp",EDGE,"E2.4"),sQuery(id+"F0.wireOp",EDGE,"E2.5"),sQuery(id+"F0.wireOp",EDGE,"E3"),sQuery(id+"F0.wireOp",EDGE,"E4"),sQuery(id+"F0.wireOp",EDGE,"E5.0"),sQuery(id+"F0.wireOp",EDGE,"E5.1"),sQuery(id+"F0.wireOp",EDGE,"E5.3"),sQuery(id+"F0.wireOp",EDGE,"E5.4"),sQuery(id+"F0.wireOp",EDGE,"E5.5"),sQuery(id+"F0.wireOp",EDGE,"E6.trimOffspring"),sQuery(id+"F0.wireOp",EDGE,"E7.trimOffspring"),sQuery(id+"F0.wireOp",EDGE,"E9.trimOffspring"),sQuery(id+"F0.wireOp",EDGE,"E10.1.0"),sQuery(id+"F0.wireOp",EDGE,"E10.1.1"),sQuery(id+"F0.wireOp",EDGE,"E10.1.2"),sQuery(id+"F0.wireOp",EDGE,"E10.1.3"),sQuery(id+"F0.wireOp",EDGE,"E10.1.5"),sQuery(id+"F0.wireOp",EDGE,"E10.1.7"),sQuery(id+"F0.wireOp",EDGE,"E10.1.8"),sQuery(id+"F0.wireOp",EDGE,"E10.1.9"),sQuery(id+"F0.wireOp",EDGE,"E10.1.10"),sQuery(id+"F0.wireOp",EDGE,"E10.1.11"),sQuery(id+"F0.wireOp",EDGE,"E10.1.12"),sQuery(id+"F0.wireOp",EDGE,"E10.1.14"),sQuery(id+"F0.wireOp",EDGE,"E10.1.15"),sQuery(id+"F0.wireOp",EDGE,"E10.1.16"),sQuery(id+"F0.wireOp",EDGE,"E10.1.18"),sQuery(id+"F0.wireOp",EDGE,"E10.1.20"),sQuery(id+"F0.wireOp",EDGE,"E10.2.0"),sQuery(id+"F0.wireOp",EDGE,"E10.2.1"),sQuery(id+"F0.wireOp",EDGE,"E10.2.2"),sQuery(id+"F0.wireOp",EDGE,"E10.2.3"),sQuery(id+"F0.wireOp",EDGE,"E10.2.5"),sQuery(id+"F0.wireOp",EDGE,"E10.2.7"),sQuery(id+"F0.wireOp",EDGE,"E10.2.8"),sQuery(id+"F0.wireOp",EDGE,"E10.2.9"),sQuery(id+"F0.wireOp",EDGE,"E10.2.10"),sQuery(id+"F0.wireOp",EDGE,"E10.2.11"),sQuery(id+"F0.wireOp",EDGE,"E10.2.12"),sQuery(id+"F0.wireOp",EDGE,"E1"),sQuery(id+"F0.wireOp",EDGE,"E10.2.14"),sQuery(id+"F0.wireOp",EDGE,"E10.2.15"),sQuery(id+"F0.wireOp",EDGE,"E10.2.16"),sQuery(id+"F0.wireOp",EDGE,"E10.2.18"),sQuery(id+"F0.wireOp",EDGE,"E10.2.20"),sQuery(id+"F0.wireOp",EDGE,"E8.trimOffspring"),sQuery(id+"F0.wireOp",EDGE,"E0"),sQuery(id+"F0.wireOp",EDGE,"E10.1.6"),sQuery(id+"F0.wireOp",EDGE,"E11"),sQuery(id+"F0.wireOp",EDGE,"E12"),sQuery(id+"F0.wireOp",EDGE,"E13.1.0"),sQuery(id+"F0.wireOp",EDGE,"E13.1.1"),sQuery(id+"F0.wireOp",EDGE,"E13.2.0"),sQuery(id+"F0.wireOp",EDGE,"E13.2.1")])]}),"instanceName":"1"}),"instanceName":"1"}),"instanceName":"1"}),"instanceName":"1"});
            var Q1;
            Q1=makeQuery(id+"F20.opPattern","COPY",EDGE,{"derivedFrom":makeQuery(id+"F19.opPattern","COPY",EDGE,{"derivedFrom":makeQuery(id+"F18.opPattern","COPY",EDGE,{"derivedFrom":makeQuery(id+"F13.opPattern","COPY",EDGE,{"derivedFrom":makeQuery(id+"F1.opExtrude","CAP_EDGE",EDGE,{"disambiguationData":[OSD([sQuery(id+"F0.wireOp",EDGE,"E1")])],"isStart":false}),"instanceName":"1"}),"instanceName":"1"}),"instanceName":"1"}),"instanceName":"1"});
            transform(context, id + "F21", {"entities" : qUnion([Q0]), "transformType" : TransformType.ROTATION, "transformAxis" : qUnion([Q1]), "angle" : 38 * degree, "makeCopy" : true});
        }
        {
            var Q0;
            Q0=makeQuery(id+"F21.opPattern","COPY",BODY,{"derivedFrom":makeQuery(id+"F20.opPattern","COPY",BODY,{"derivedFrom":makeQuery(id+"F19.opPattern","COPY",BODY,{"derivedFrom":makeQuery(id+"F18.opPattern","COPY",BODY,{"derivedFrom":makeQuery(id+"F13.opPattern","COPY",BODY,{"derivedFrom":makeQuery(id+"F1.opExtrude","SWEPT_BODY",BODY,{"disambiguationData":[OSD([sQuery(id+"F0.wireOp",EDGE,"E2.0"),sQuery(id+"F0.wireOp",EDGE,"E2.1"),sQuery(id+"F0.wireOp",EDGE,"E2.2"),sQuery(id+"F0.wireOp",EDGE,"E2.3"),sQuery(id+"F0.wireOp",EDGE,"E2.4"),sQuery(id+"F0.wireOp",EDGE,"E2.5"),sQuery(id+"F0.wireOp",EDGE,"E3"),sQuery(id+"F0.wireOp",EDGE,"E4"),sQuery(id+"F0.wireOp",EDGE,"E5.0"),sQuery(id+"F0.wireOp",EDGE,"E5.1"),sQuery(id+"F0.wireOp",EDGE,"E5.3"),sQuery(id+"F0.wireOp",EDGE,"E5.4"),sQuery(id+"F0.wireOp",EDGE,"E5.5"),sQuery(id+"F0.wireOp",EDGE,"E6.trimOffspring"),sQuery(id+"F0.wireOp",EDGE,"E7.trimOffspring"),sQuery(id+"F0.wireOp",EDGE,"E9.trimOffspring"),sQuery(id+"F0.wireOp",EDGE,"E10.1.0"),sQuery(id+"F0.wireOp",EDGE,"E10.1.1"),sQuery(id+"F0.wireOp",EDGE,"E10.1.2"),sQuery(id+"F0.wireOp",EDGE,"E10.1.3"),sQuery(id+"F0.wireOp",EDGE,"E10.1.5"),sQuery(id+"F0.wireOp",EDGE,"E10.1.7"),sQuery(id+"F0.wireOp",EDGE,"E10.1.8"),sQuery(id+"F0.wireOp",EDGE,"E10.1.9"),sQuery(id+"F0.wireOp",EDGE,"E10.1.10"),sQuery(id+"F0.wireOp",EDGE,"E10.1.11"),sQuery(id+"F0.wireOp",EDGE,"E10.1.12"),sQuery(id+"F0.wireOp",EDGE,"E10.1.14"),sQuery(id+"F0.wireOp",EDGE,"E10.1.15"),sQuery(id+"F0.wireOp",EDGE,"E10.1.16"),sQuery(id+"F0.wireOp",EDGE,"E10.1.18"),sQuery(id+"F0.wireOp",EDGE,"E10.1.20"),sQuery(id+"F0.wireOp",EDGE,"E10.2.0"),sQuery(id+"F0.wireOp",EDGE,"E10.2.1"),sQuery(id+"F0.wireOp",EDGE,"E10.2.2"),sQuery(id+"F0.wireOp",EDGE,"E10.2.3"),sQuery(id+"F0.wireOp",EDGE,"E10.2.5"),sQuery(id+"F0.wireOp",EDGE,"E10.2.7"),sQuery(id+"F0.wireOp",EDGE,"E10.2.8"),sQuery(id+"F0.wireOp",EDGE,"E10.2.9"),sQuery(id+"F0.wireOp",EDGE,"E10.2.10"),sQuery(id+"F0.wireOp",EDGE,"E10.2.11"),sQuery(id+"F0.wireOp",EDGE,"E10.2.12"),sQuery(id+"F0.wireOp",EDGE,"E1"),sQuery(id+"F0.wireOp",EDGE,"E10.2.14"),sQuery(id+"F0.wireOp",EDGE,"E10.2.15"),sQuery(id+"F0.wireOp",EDGE,"E10.2.16"),sQuery(id+"F0.wireOp",EDGE,"E10.2.18"),sQuery(id+"F0.wireOp",EDGE,"E10.2.20"),sQuery(id+"F0.wireOp",EDGE,"E8.trimOffspring"),sQuery(id+"F0.wireOp",EDGE,"E0"),sQuery(id+"F0.wireOp",EDGE,"E10.1.6"),sQuery(id+"F0.wireOp",EDGE,"E11"),sQuery(id+"F0.wireOp",EDGE,"E12"),sQuery(id+"F0.wireOp",EDGE,"E13.1.0"),sQuery(id+"F0.wireOp",EDGE,"E13.1.1"),sQuery(id+"F0.wireOp",EDGE,"E13.2.0"),sQuery(id+"F0.wireOp",EDGE,"E13.2.1")])]}),"instanceName":"1"}),"instanceName":"1"}),"instanceName":"1"}),"instanceName":"1"}),"instanceName":"1"});
            transform(context, id + "F22", {"entities" : qUnion([Q0]), "transformType" : TransformType.TRANSLATION_3D, "dx" : 61.5 * mm, "dy" : -15.8 * mm, "dz" : 0 * mm, "makeCopy" : false});
        }
        {
            var Q0;
            Q0=makeQuery(id+"F5.opPattern","COPY",BODY,{"derivedFrom":makeQuery(id+"F1.opExtrude","SWEPT_BODY",BODY,{"disambiguationData":[OSD([sQuery(id+"F0.wireOp",EDGE,"E2.0"),sQuery(id+"F0.wireOp",EDGE,"E2.1"),sQuery(id+"F0.wireOp",EDGE,"E2.2"),sQuery(id+"F0.wireOp",EDGE,"E2.3"),sQuery(id+"F0.wireOp",EDGE,"E2.4"),sQuery(id+"F0.wireOp",EDGE,"E2.5"),sQuery(id+"F0.wireOp",EDGE,"E3"),sQuery(id+"F0.wireOp",EDGE,"E4"),sQuery(id+"F0.wireOp",EDGE,"E5.0"),sQuery(id+"F0.wireOp",EDGE,"E5.1"),sQuery(id+"F0.wireOp",EDGE,"E5.3"),sQuery(id+"F0.wireOp",EDGE,"E5.4"),sQuery(id+"F0.wireOp",EDGE,"E5.5"),sQuery(id+"F0.wireOp",EDGE,"E6.trimOffspring"),sQuery(id+"F0.wireOp",EDGE,"E7.trimOffspring"),sQuery(id+"F0.wireOp",EDGE,"E9.trimOffspring"),sQuery(id+"F0.wireOp",EDGE,"E10.1.0"),sQuery(id+"F0.wireOp",EDGE,"E10.1.1"),sQuery(id+"F0.wireOp",EDGE,"E10.1.2"),sQuery(id+"F0.wireOp",EDGE,"E10.1.3"),sQuery(id+"F0.wireOp",EDGE,"E10.1.5"),sQuery(id+"F0.wireOp",EDGE,"E10.1.7"),sQuery(id+"F0.wireOp",EDGE,"E10.1.8"),sQuery(id+"F0.wireOp",EDGE,"E10.1.9"),sQuery(id+"F0.wireOp",EDGE,"E10.1.10"),sQuery(id+"F0.wireOp",EDGE,"E10.1.11"),sQuery(id+"F0.wireOp",EDGE,"E10.1.12"),sQuery(id+"F0.wireOp",EDGE,"E10.1.14"),sQuery(id+"F0.wireOp",EDGE,"E10.1.15"),sQuery(id+"F0.wireOp",EDGE,"E10.1.16"),sQuery(id+"F0.wireOp",EDGE,"E10.1.18"),sQuery(id+"F0.wireOp",EDGE,"E10.1.20"),sQuery(id+"F0.wireOp",EDGE,"E10.2.0"),sQuery(id+"F0.wireOp",EDGE,"E10.2.1"),sQuery(id+"F0.wireOp",EDGE,"E10.2.2"),sQuery(id+"F0.wireOp",EDGE,"E10.2.3"),sQuery(id+"F0.wireOp",EDGE,"E10.2.5"),sQuery(id+"F0.wireOp",EDGE,"E10.2.7"),sQuery(id+"F0.wireOp",EDGE,"E10.2.8"),sQuery(id+"F0.wireOp",EDGE,"E10.2.9"),sQuery(id+"F0.wireOp",EDGE,"E10.2.10"),sQuery(id+"F0.wireOp",EDGE,"E10.2.11"),sQuery(id+"F0.wireOp",EDGE,"E10.2.12"),sQuery(id+"F0.wireOp",EDGE,"E1"),sQuery(id+"F0.wireOp",EDGE,"E10.2.14"),sQuery(id+"F0.wireOp",EDGE,"E10.2.15"),sQuery(id+"F0.wireOp",EDGE,"E10.2.16"),sQuery(id+"F0.wireOp",EDGE,"E10.2.18"),sQuery(id+"F0.wireOp",EDGE,"E10.2.20"),sQuery(id+"F0.wireOp",EDGE,"E8.trimOffspring"),sQuery(id+"F0.wireOp",EDGE,"E0"),sQuery(id+"F0.wireOp",EDGE,"E10.1.6"),sQuery(id+"F0.wireOp",EDGE,"E11"),sQuery(id+"F0.wireOp",EDGE,"E12"),sQuery(id+"F0.wireOp",EDGE,"E13.1.0"),sQuery(id+"F0.wireOp",EDGE,"E13.1.1"),sQuery(id+"F0.wireOp",EDGE,"E13.2.0"),sQuery(id+"F0.wireOp",EDGE,"E13.2.1")])]}),"instanceName":"1"});
            var Q1;
            Q1=makeQuery(id+"F1.opExtrude","SWEPT_BODY",BODY,{"disambiguationData":[OSD([sQuery(id+"F0.wireOp",EDGE,"E2.0"),sQuery(id+"F0.wireOp",EDGE,"E2.1"),sQuery(id+"F0.wireOp",EDGE,"E2.2"),sQuery(id+"F0.wireOp",EDGE,"E2.3"),sQuery(id+"F0.wireOp",EDGE,"E2.4"),sQuery(id+"F0.wireOp",EDGE,"E2.5"),sQuery(id+"F0.wireOp",EDGE,"E3"),sQuery(id+"F0.wireOp",EDGE,"E4"),sQuery(id+"F0.wireOp",EDGE,"E5.0"),sQuery(id+"F0.wireOp",EDGE,"E5.1"),sQuery(id+"F0.wireOp",EDGE,"E5.3"),sQuery(id+"F0.wireOp",EDGE,"E5.4"),sQuery(id+"F0.wireOp",EDGE,"E5.5"),sQuery(id+"F0.wireOp",EDGE,"E6.trimOffspring"),sQuery(id+"F0.wireOp",EDGE,"E7.trimOffspring"),sQuery(id+"F0.wireOp",EDGE,"E9.trimOffspring"),sQuery(id+"F0.wireOp",EDGE,"E10.1.0"),sQuery(id+"F0.wireOp",EDGE,"E10.1.1"),sQuery(id+"F0.wireOp",EDGE,"E10.1.2"),sQuery(id+"F0.wireOp",EDGE,"E10.1.3"),sQuery(id+"F0.wireOp",EDGE,"E10.1.5"),sQuery(id+"F0.wireOp",EDGE,"E10.1.7"),sQuery(id+"F0.wireOp",EDGE,"E10.1.8"),sQuery(id+"F0.wireOp",EDGE,"E10.1.9"),sQuery(id+"F0.wireOp",EDGE,"E10.1.10"),sQuery(id+"F0.wireOp",EDGE,"E10.1.11"),sQuery(id+"F0.wireOp",EDGE,"E10.1.12"),sQuery(id+"F0.wireOp",EDGE,"E10.1.14"),sQuery(id+"F0.wireOp",EDGE,"E10.1.15"),sQuery(id+"F0.wireOp",EDGE,"E10.1.16"),sQuery(id+"F0.wireOp",EDGE,"E10.1.18"),sQuery(id+"F0.wireOp",EDGE,"E10.1.20"),sQuery(id+"F0.wireOp",EDGE,"E10.2.0"),sQuery(id+"F0.wireOp",EDGE,"E10.2.1"),sQuery(id+"F0.wireOp",EDGE,"E10.2.2"),sQuery(id+"F0.wireOp",EDGE,"E10.2.3"),sQuery(id+"F0.wireOp",EDGE,"E10.2.5"),sQuery(id+"F0.wireOp",EDGE,"E10.2.7"),sQuery(id+"F0.wireOp",EDGE,"E10.2.8"),sQuery(id+"F0.wireOp",EDGE,"E10.2.9"),sQuery(id+"F0.wireOp",EDGE,"E10.2.10"),sQuery(id+"F0.wireOp",EDGE,"E10.2.11"),sQuery(id+"F0.wireOp",EDGE,"E10.2.12"),sQuery(id+"F0.wireOp",EDGE,"E1"),sQuery(id+"F0.wireOp",EDGE,"E10.2.14"),sQuery(id+"F0.wireOp",EDGE,"E10.2.15"),sQuery(id+"F0.wireOp",EDGE,"E10.2.16"),sQuery(id+"F0.wireOp",EDGE,"E10.2.18"),sQuery(id+"F0.wireOp",EDGE,"E10.2.20"),sQuery(id+"F0.wireOp",EDGE,"E8.trimOffspring"),sQuery(id+"F0.wireOp",EDGE,"E0"),sQuery(id+"F0.wireOp",EDGE,"E10.1.6"),sQuery(id+"F0.wireOp",EDGE,"E11"),sQuery(id+"F0.wireOp",EDGE,"E12"),sQuery(id+"F0.wireOp",EDGE,"E13.1.0"),sQuery(id+"F0.wireOp",EDGE,"E13.1.1"),sQuery(id+"F0.wireOp",EDGE,"E13.2.0"),sQuery(id+"F0.wireOp",EDGE,"E13.2.1")])]});
            var Q2;
            Q2=makeQuery(id+"F7.opPattern","COPY",BODY,{"derivedFrom":makeQuery(id+"F1.opExtrude","SWEPT_BODY",BODY,{"disambiguationData":[OSD([sQuery(id+"F0.wireOp",EDGE,"E2.0"),sQuery(id+"F0.wireOp",EDGE,"E2.1"),sQuery(id+"F0.wireOp",EDGE,"E2.2"),sQuery(id+"F0.wireOp",EDGE,"E2.3"),sQuery(id+"F0.wireOp",EDGE,"E2.4"),sQuery(id+"F0.wireOp",EDGE,"E2.5"),sQuery(id+"F0.wireOp",EDGE,"E3"),sQuery(id+"F0.wireOp",EDGE,"E4"),sQuery(id+"F0.wireOp",EDGE,"E5.0"),sQuery(id+"F0.wireOp",EDGE,"E5.1"),sQuery(id+"F0.wireOp",EDGE,"E5.3"),sQuery(id+"F0.wireOp",EDGE,"E5.4"),sQuery(id+"F0.wireOp",EDGE,"E5.5"),sQuery(id+"F0.wireOp",EDGE,"E6.trimOffspring"),sQuery(id+"F0.wireOp",EDGE,"E7.trimOffspring"),sQuery(id+"F0.wireOp",EDGE,"E9.trimOffspring"),sQuery(id+"F0.wireOp",EDGE,"E10.1.0"),sQuery(id+"F0.wireOp",EDGE,"E10.1.1"),sQuery(id+"F0.wireOp",EDGE,"E10.1.2"),sQuery(id+"F0.wireOp",EDGE,"E10.1.3"),sQuery(id+"F0.wireOp",EDGE,"E10.1.5"),sQuery(id+"F0.wireOp",EDGE,"E10.1.7"),sQuery(id+"F0.wireOp",EDGE,"E10.1.8"),sQuery(id+"F0.wireOp",EDGE,"E10.1.9"),sQuery(id+"F0.wireOp",EDGE,"E10.1.10"),sQuery(id+"F0.wireOp",EDGE,"E10.1.11"),sQuery(id+"F0.wireOp",EDGE,"E10.1.12"),sQuery(id+"F0.wireOp",EDGE,"E10.1.14"),sQuery(id+"F0.wireOp",EDGE,"E10.1.15"),sQuery(id+"F0.wireOp",EDGE,"E10.1.16"),sQuery(id+"F0.wireOp",EDGE,"E10.1.18"),sQuery(id+"F0.wireOp",EDGE,"E10.1.20"),sQuery(id+"F0.wireOp",EDGE,"E10.2.0"),sQuery(id+"F0.wireOp",EDGE,"E10.2.1"),sQuery(id+"F0.wireOp",EDGE,"E10.2.2"),sQuery(id+"F0.wireOp",EDGE,"E10.2.3"),sQuery(id+"F0.wireOp",EDGE,"E10.2.5"),sQuery(id+"F0.wireOp",EDGE,"E10.2.7"),sQuery(id+"F0.wireOp",EDGE,"E10.2.8"),sQuery(id+"F0.wireOp",EDGE,"E10.2.9"),sQuery(id+"F0.wireOp",EDGE,"E10.2.10"),sQuery(id+"F0.wireOp",EDGE,"E10.2.11"),sQuery(id+"F0.wireOp",EDGE,"E10.2.12"),sQuery(id+"F0.wireOp",EDGE,"E1"),sQuery(id+"F0.wireOp",EDGE,"E10.2.14"),sQuery(id+"F0.wireOp",EDGE,"E10.2.15"),sQuery(id+"F0.wireOp",EDGE,"E10.2.16"),sQuery(id+"F0.wireOp",EDGE,"E10.2.18"),sQuery(id+"F0.wireOp",EDGE,"E10.2.20"),sQuery(id+"F0.wireOp",EDGE,"E8.trimOffspring"),sQuery(id+"F0.wireOp",EDGE,"E0"),sQuery(id+"F0.wireOp",EDGE,"E10.1.6"),sQuery(id+"F0.wireOp",EDGE,"E11"),sQuery(id+"F0.wireOp",EDGE,"E12"),sQuery(id+"F0.wireOp",EDGE,"E13.1.0"),sQuery(id+"F0.wireOp",EDGE,"E13.1.1"),sQuery(id+"F0.wireOp",EDGE,"E13.2.0"),sQuery(id+"F0.wireOp",EDGE,"E13.2.1")])]}),"instanceName":"1"});
            var Q3;
            Q3=makeQuery(id+"F8.opPattern","COPY",BODY,{"derivedFrom":makeQuery(id+"F7.opPattern","COPY",BODY,{"derivedFrom":makeQuery(id+"F1.opExtrude","SWEPT_BODY",BODY,{"disambiguationData":[OSD([sQuery(id+"F0.wireOp",EDGE,"E2.0"),sQuery(id+"F0.wireOp",EDGE,"E2.1"),sQuery(id+"F0.wireOp",EDGE,"E2.2"),sQuery(id+"F0.wireOp",EDGE,"E2.3"),sQuery(id+"F0.wireOp",EDGE,"E2.4"),sQuery(id+"F0.wireOp",EDGE,"E2.5"),sQuery(id+"F0.wireOp",EDGE,"E3"),sQuery(id+"F0.wireOp",EDGE,"E4"),sQuery(id+"F0.wireOp",EDGE,"E5.0"),sQuery(id+"F0.wireOp",EDGE,"E5.1"),sQuery(id+"F0.wireOp",EDGE,"E5.3"),sQuery(id+"F0.wireOp",EDGE,"E5.4"),sQuery(id+"F0.wireOp",EDGE,"E5.5"),sQuery(id+"F0.wireOp",EDGE,"E6.trimOffspring"),sQuery(id+"F0.wireOp",EDGE,"E7.trimOffspring"),sQuery(id+"F0.wireOp",EDGE,"E9.trimOffspring"),sQuery(id+"F0.wireOp",EDGE,"E10.1.0"),sQuery(id+"F0.wireOp",EDGE,"E10.1.1"),sQuery(id+"F0.wireOp",EDGE,"E10.1.2"),sQuery(id+"F0.wireOp",EDGE,"E10.1.3"),sQuery(id+"F0.wireOp",EDGE,"E10.1.5"),sQuery(id+"F0.wireOp",EDGE,"E10.1.7"),sQuery(id+"F0.wireOp",EDGE,"E10.1.8"),sQuery(id+"F0.wireOp",EDGE,"E10.1.9"),sQuery(id+"F0.wireOp",EDGE,"E10.1.10"),sQuery(id+"F0.wireOp",EDGE,"E10.1.11"),sQuery(id+"F0.wireOp",EDGE,"E10.1.12"),sQuery(id+"F0.wireOp",EDGE,"E10.1.14"),sQuery(id+"F0.wireOp",EDGE,"E10.1.15"),sQuery(id+"F0.wireOp",EDGE,"E10.1.16"),sQuery(id+"F0.wireOp",EDGE,"E10.1.18"),sQuery(id+"F0.wireOp",EDGE,"E10.1.20"),sQuery(id+"F0.wireOp",EDGE,"E10.2.0"),sQuery(id+"F0.wireOp",EDGE,"E10.2.1"),sQuery(id+"F0.wireOp",EDGE,"E10.2.2"),sQuery(id+"F0.wireOp",EDGE,"E10.2.3"),sQuery(id+"F0.wireOp",EDGE,"E10.2.5"),sQuery(id+"F0.wireOp",EDGE,"E10.2.7"),sQuery(id+"F0.wireOp",EDGE,"E10.2.8"),sQuery(id+"F0.wireOp",EDGE,"E10.2.9"),sQuery(id+"F0.wireOp",EDGE,"E10.2.10"),sQuery(id+"F0.wireOp",EDGE,"E10.2.11"),sQuery(id+"F0.wireOp",EDGE,"E10.2.12"),sQuery(id+"F0.wireOp",EDGE,"E1"),sQuery(id+"F0.wireOp",EDGE,"E10.2.14"),sQuery(id+"F0.wireOp",EDGE,"E10.2.15"),sQuery(id+"F0.wireOp",EDGE,"E10.2.16"),sQuery(id+"F0.wireOp",EDGE,"E10.2.18"),sQuery(id+"F0.wireOp",EDGE,"E10.2.20"),sQuery(id+"F0.wireOp",EDGE,"E8.trimOffspring"),sQuery(id+"F0.wireOp",EDGE,"E0"),sQuery(id+"F0.wireOp",EDGE,"E10.1.6"),sQuery(id+"F0.wireOp",EDGE,"E11"),sQuery(id+"F0.wireOp",EDGE,"E12"),sQuery(id+"F0.wireOp",EDGE,"E13.1.0"),sQuery(id+"F0.wireOp",EDGE,"E13.1.1"),sQuery(id+"F0.wireOp",EDGE,"E13.2.0"),sQuery(id+"F0.wireOp",EDGE,"E13.2.1")])]}),"instanceName":"1"}),"instanceName":"1"});
            transform(context, id + "F23", {"entities" : qUnion([Q0, Q1, Q2, Q3]), "transformType" : TransformType.TRANSLATION_3D, "dx" : 0 * mm, "dy" : -108 * mm, "dz" : 0 * mm, "makeCopy" : true});
        }
        {
            var Q0;
            Q0=makeQuery(id+"F23.opPattern","COPY",BODY,{"derivedFrom":makeQuery(id+"F5.opPattern","COPY",BODY,{"derivedFrom":makeQuery(id+"F1.opExtrude","SWEPT_BODY",BODY,{"disambiguationData":[OSD([sQuery(id+"F0.wireOp",EDGE,"E2.0"),sQuery(id+"F0.wireOp",EDGE,"E2.1"),sQuery(id+"F0.wireOp",EDGE,"E2.2"),sQuery(id+"F0.wireOp",EDGE,"E2.3"),sQuery(id+"F0.wireOp",EDGE,"E2.4"),sQuery(id+"F0.wireOp",EDGE,"E2.5"),sQuery(id+"F0.wireOp",EDGE,"E3"),sQuery(id+"F0.wireOp",EDGE,"E4"),sQuery(id+"F0.wireOp",EDGE,"E5.0"),sQuery(id+"F0.wireOp",EDGE,"E5.1"),sQuery(id+"F0.wireOp",EDGE,"E5.3"),sQuery(id+"F0.wireOp",EDGE,"E5.4"),sQuery(id+"F0.wireOp",EDGE,"E5.5"),sQuery(id+"F0.wireOp",EDGE,"E6.trimOffspring"),sQuery(id+"F0.wireOp",EDGE,"E7.trimOffspring"),sQuery(id+"F0.wireOp",EDGE,"E9.trimOffspring"),sQuery(id+"F0.wireOp",EDGE,"E10.1.0"),sQuery(id+"F0.wireOp",EDGE,"E10.1.1"),sQuery(id+"F0.wireOp",EDGE,"E10.1.2"),sQuery(id+"F0.wireOp",EDGE,"E10.1.3"),sQuery(id+"F0.wireOp",EDGE,"E10.1.5"),sQuery(id+"F0.wireOp",EDGE,"E10.1.7"),sQuery(id+"F0.wireOp",EDGE,"E10.1.8"),sQuery(id+"F0.wireOp",EDGE,"E10.1.9"),sQuery(id+"F0.wireOp",EDGE,"E10.1.10"),sQuery(id+"F0.wireOp",EDGE,"E10.1.11"),sQuery(id+"F0.wireOp",EDGE,"E10.1.12"),sQuery(id+"F0.wireOp",EDGE,"E10.1.14"),sQuery(id+"F0.wireOp",EDGE,"E10.1.15"),sQuery(id+"F0.wireOp",EDGE,"E10.1.16"),sQuery(id+"F0.wireOp",EDGE,"E10.1.18"),sQuery(id+"F0.wireOp",EDGE,"E10.1.20"),sQuery(id+"F0.wireOp",EDGE,"E10.2.0"),sQuery(id+"F0.wireOp",EDGE,"E10.2.1"),sQuery(id+"F0.wireOp",EDGE,"E10.2.2"),sQuery(id+"F0.wireOp",EDGE,"E10.2.3"),sQuery(id+"F0.wireOp",EDGE,"E10.2.5"),sQuery(id+"F0.wireOp",EDGE,"E10.2.7"),sQuery(id+"F0.wireOp",EDGE,"E10.2.8"),sQuery(id+"F0.wireOp",EDGE,"E10.2.9"),sQuery(id+"F0.wireOp",EDGE,"E10.2.10"),sQuery(id+"F0.wireOp",EDGE,"E10.2.11"),sQuery(id+"F0.wireOp",EDGE,"E10.2.12"),sQuery(id+"F0.wireOp",EDGE,"E1"),sQuery(id+"F0.wireOp",EDGE,"E10.2.14"),sQuery(id+"F0.wireOp",EDGE,"E10.2.15"),sQuery(id+"F0.wireOp",EDGE,"E10.2.16"),sQuery(id+"F0.wireOp",EDGE,"E10.2.18"),sQuery(id+"F0.wireOp",EDGE,"E10.2.20"),sQuery(id+"F0.wireOp",EDGE,"E8.trimOffspring"),sQuery(id+"F0.wireOp",EDGE,"E0"),sQuery(id+"F0.wireOp",EDGE,"E10.1.6"),sQuery(id+"F0.wireOp",EDGE,"E11"),sQuery(id+"F0.wireOp",EDGE,"E12"),sQuery(id+"F0.wireOp",EDGE,"E13.1.0"),sQuery(id+"F0.wireOp",EDGE,"E13.1.1"),sQuery(id+"F0.wireOp",EDGE,"E13.2.0"),sQuery(id+"F0.wireOp",EDGE,"E13.2.1")])]}),"instanceName":"1"}),"instanceName":"1"});
            var Q1;
            Q1=makeQuery(id+"F23.opPattern","COPY",EDGE,{"derivedFrom":makeQuery(id+"F5.opPattern","COPY",EDGE,{"derivedFrom":makeQuery(id+"F1.opExtrude","CAP_EDGE",EDGE,{"disambiguationData":[OSD([sQuery(id+"F0.wireOp",EDGE,"E1")])],"isStart":false}),"instanceName":"1"}),"instanceName":"1"});
            transform(context, id + "F24", {"entities" : qUnion([Q0]), "transformType" : TransformType.ROTATION, "transformAxis" : qUnion([Q1]), "angle" : 42 * degree, "oppositeDirection" : true, "makeCopy" : false});
        }
        {
            var Q0;
            Q0=makeQuery(id+"F23.opPattern","COPY",BODY,{"derivedFrom":makeQuery(id+"F1.opExtrude","SWEPT_BODY",BODY,{"disambiguationData":[OSD([sQuery(id+"F0.wireOp",EDGE,"E2.0"),sQuery(id+"F0.wireOp",EDGE,"E2.1"),sQuery(id+"F0.wireOp",EDGE,"E2.2"),sQuery(id+"F0.wireOp",EDGE,"E2.3"),sQuery(id+"F0.wireOp",EDGE,"E2.4"),sQuery(id+"F0.wireOp",EDGE,"E2.5"),sQuery(id+"F0.wireOp",EDGE,"E3"),sQuery(id+"F0.wireOp",EDGE,"E4"),sQuery(id+"F0.wireOp",EDGE,"E5.0"),sQuery(id+"F0.wireOp",EDGE,"E5.1"),sQuery(id+"F0.wireOp",EDGE,"E5.3"),sQuery(id+"F0.wireOp",EDGE,"E5.4"),sQuery(id+"F0.wireOp",EDGE,"E5.5"),sQuery(id+"F0.wireOp",EDGE,"E6.trimOffspring"),sQuery(id+"F0.wireOp",EDGE,"E7.trimOffspring"),sQuery(id+"F0.wireOp",EDGE,"E9.trimOffspring"),sQuery(id+"F0.wireOp",EDGE,"E10.1.0"),sQuery(id+"F0.wireOp",EDGE,"E10.1.1"),sQuery(id+"F0.wireOp",EDGE,"E10.1.2"),sQuery(id+"F0.wireOp",EDGE,"E10.1.3"),sQuery(id+"F0.wireOp",EDGE,"E10.1.5"),sQuery(id+"F0.wireOp",EDGE,"E10.1.7"),sQuery(id+"F0.wireOp",EDGE,"E10.1.8"),sQuery(id+"F0.wireOp",EDGE,"E10.1.9"),sQuery(id+"F0.wireOp",EDGE,"E10.1.10"),sQuery(id+"F0.wireOp",EDGE,"E10.1.11"),sQuery(id+"F0.wireOp",EDGE,"E10.1.12"),sQuery(id+"F0.wireOp",EDGE,"E10.1.14"),sQuery(id+"F0.wireOp",EDGE,"E10.1.15"),sQuery(id+"F0.wireOp",EDGE,"E10.1.16"),sQuery(id+"F0.wireOp",EDGE,"E10.1.18"),sQuery(id+"F0.wireOp",EDGE,"E10.1.20"),sQuery(id+"F0.wireOp",EDGE,"E10.2.0"),sQuery(id+"F0.wireOp",EDGE,"E10.2.1"),sQuery(id+"F0.wireOp",EDGE,"E10.2.2"),sQuery(id+"F0.wireOp",EDGE,"E10.2.3"),sQuery(id+"F0.wireOp",EDGE,"E10.2.5"),sQuery(id+"F0.wireOp",EDGE,"E10.2.7"),sQuery(id+"F0.wireOp",EDGE,"E10.2.8"),sQuery(id+"F0.wireOp",EDGE,"E10.2.9"),sQuery(id+"F0.wireOp",EDGE,"E10.2.10"),sQuery(id+"F0.wireOp",EDGE,"E10.2.11"),sQuery(id+"F0.wireOp",EDGE,"E10.2.12"),sQuery(id+"F0.wireOp",EDGE,"E1"),sQuery(id+"F0.wireOp",EDGE,"E10.2.14"),sQuery(id+"F0.wireOp",EDGE,"E10.2.15"),sQuery(id+"F0.wireOp",EDGE,"E10.2.16"),sQuery(id+"F0.wireOp",EDGE,"E10.2.18"),sQuery(id+"F0.wireOp",EDGE,"E10.2.20"),sQuery(id+"F0.wireOp",EDGE,"E8.trimOffspring"),sQuery(id+"F0.wireOp",EDGE,"E0"),sQuery(id+"F0.wireOp",EDGE,"E10.1.6"),sQuery(id+"F0.wireOp",EDGE,"E11"),sQuery(id+"F0.wireOp",EDGE,"E12"),sQuery(id+"F0.wireOp",EDGE,"E13.1.0"),sQuery(id+"F0.wireOp",EDGE,"E13.1.1"),sQuery(id+"F0.wireOp",EDGE,"E13.2.0"),sQuery(id+"F0.wireOp",EDGE,"E13.2.1")])]}),"instanceName":"1"});
            var Q1;
            Q1=makeQuery(id+"F23.opPattern","COPY",EDGE,{"derivedFrom":makeQuery(id+"F1.opExtrude","CAP_EDGE",EDGE,{"disambiguationData":[OSD([sQuery(id+"F0.wireOp",EDGE,"E1")])],"isStart":false}),"instanceName":"1"});
            transform(context, id + "F25", {"entities" : qUnion([Q0]), "transformType" : TransformType.ROTATION, "transformAxis" : qUnion([Q1]), "angle" : 10 * degree, "oppositeDirection" : true, "makeCopy" : false});
        }
        {
            var Q0;
            Q0=makeQuery(id+"F23.opPattern","COPY",BODY,{"derivedFrom":makeQuery(id+"F1.opExtrude","SWEPT_BODY",BODY,{"disambiguationData":[OSD([sQuery(id+"F0.wireOp",EDGE,"E2.0"),sQuery(id+"F0.wireOp",EDGE,"E2.1"),sQuery(id+"F0.wireOp",EDGE,"E2.2"),sQuery(id+"F0.wireOp",EDGE,"E2.3"),sQuery(id+"F0.wireOp",EDGE,"E2.4"),sQuery(id+"F0.wireOp",EDGE,"E2.5"),sQuery(id+"F0.wireOp",EDGE,"E3"),sQuery(id+"F0.wireOp",EDGE,"E4"),sQuery(id+"F0.wireOp",EDGE,"E5.0"),sQuery(id+"F0.wireOp",EDGE,"E5.1"),sQuery(id+"F0.wireOp",EDGE,"E5.3"),sQuery(id+"F0.wireOp",EDGE,"E5.4"),sQuery(id+"F0.wireOp",EDGE,"E5.5"),sQuery(id+"F0.wireOp",EDGE,"E6.trimOffspring"),sQuery(id+"F0.wireOp",EDGE,"E7.trimOffspring"),sQuery(id+"F0.wireOp",EDGE,"E9.trimOffspring"),sQuery(id+"F0.wireOp",EDGE,"E10.1.0"),sQuery(id+"F0.wireOp",EDGE,"E10.1.1"),sQuery(id+"F0.wireOp",EDGE,"E10.1.2"),sQuery(id+"F0.wireOp",EDGE,"E10.1.3"),sQuery(id+"F0.wireOp",EDGE,"E10.1.5"),sQuery(id+"F0.wireOp",EDGE,"E10.1.7"),sQuery(id+"F0.wireOp",EDGE,"E10.1.8"),sQuery(id+"F0.wireOp",EDGE,"E10.1.9"),sQuery(id+"F0.wireOp",EDGE,"E10.1.10"),sQuery(id+"F0.wireOp",EDGE,"E10.1.11"),sQuery(id+"F0.wireOp",EDGE,"E10.1.12"),sQuery(id+"F0.wireOp",EDGE,"E10.1.14"),sQuery(id+"F0.wireOp",EDGE,"E10.1.15"),sQuery(id+"F0.wireOp",EDGE,"E10.1.16"),sQuery(id+"F0.wireOp",EDGE,"E10.1.18"),sQuery(id+"F0.wireOp",EDGE,"E10.1.20"),sQuery(id+"F0.wireOp",EDGE,"E10.2.0"),sQuery(id+"F0.wireOp",EDGE,"E10.2.1"),sQuery(id+"F0.wireOp",EDGE,"E10.2.2"),sQuery(id+"F0.wireOp",EDGE,"E10.2.3"),sQuery(id+"F0.wireOp",EDGE,"E10.2.5"),sQuery(id+"F0.wireOp",EDGE,"E10.2.7"),sQuery(id+"F0.wireOp",EDGE,"E10.2.8"),sQuery(id+"F0.wireOp",EDGE,"E10.2.9"),sQuery(id+"F0.wireOp",EDGE,"E10.2.10"),sQuery(id+"F0.wireOp",EDGE,"E10.2.11"),sQuery(id+"F0.wireOp",EDGE,"E10.2.12"),sQuery(id+"F0.wireOp",EDGE,"E1"),sQuery(id+"F0.wireOp",EDGE,"E10.2.14"),sQuery(id+"F0.wireOp",EDGE,"E10.2.15"),sQuery(id+"F0.wireOp",EDGE,"E10.2.16"),sQuery(id+"F0.wireOp",EDGE,"E10.2.18"),sQuery(id+"F0.wireOp",EDGE,"E10.2.20"),sQuery(id+"F0.wireOp",EDGE,"E8.trimOffspring"),sQuery(id+"F0.wireOp",EDGE,"E0"),sQuery(id+"F0.wireOp",EDGE,"E10.1.6"),sQuery(id+"F0.wireOp",EDGE,"E11"),sQuery(id+"F0.wireOp",EDGE,"E12"),sQuery(id+"F0.wireOp",EDGE,"E13.1.0"),sQuery(id+"F0.wireOp",EDGE,"E13.1.1"),sQuery(id+"F0.wireOp",EDGE,"E13.2.0"),sQuery(id+"F0.wireOp",EDGE,"E13.2.1")])]}),"instanceName":"1"});
            transform(context, id + "F26", {"entities" : qUnion([Q0]), "transformType" : TransformType.TRANSLATION_3D, "dx" : 0 * mm, "dy" : 1.1 * mm, "dz" : 0 * mm, "makeCopy" : false});
        }
        {
            var Q0;
            Q0=makeQuery(id+"F23.opPattern","COPY",BODY,{"derivedFrom":makeQuery(id+"F5.opPattern","COPY",BODY,{"derivedFrom":makeQuery(id+"F1.opExtrude","SWEPT_BODY",BODY,{"disambiguationData":[OSD([sQuery(id+"F0.wireOp",EDGE,"E2.0"),sQuery(id+"F0.wireOp",EDGE,"E2.1"),sQuery(id+"F0.wireOp",EDGE,"E2.2"),sQuery(id+"F0.wireOp",EDGE,"E2.3"),sQuery(id+"F0.wireOp",EDGE,"E2.4"),sQuery(id+"F0.wireOp",EDGE,"E2.5"),sQuery(id+"F0.wireOp",EDGE,"E3"),sQuery(id+"F0.wireOp",EDGE,"E4"),sQuery(id+"F0.wireOp",EDGE,"E5.0"),sQuery(id+"F0.wireOp",EDGE,"E5.1"),sQuery(id+"F0.wireOp",EDGE,"E5.3"),sQuery(id+"F0.wireOp",EDGE,"E5.4"),sQuery(id+"F0.wireOp",EDGE,"E5.5"),sQuery(id+"F0.wireOp",EDGE,"E6.trimOffspring"),sQuery(id+"F0.wireOp",EDGE,"E7.trimOffspring"),sQuery(id+"F0.wireOp",EDGE,"E9.trimOffspring"),sQuery(id+"F0.wireOp",EDGE,"E10.1.0"),sQuery(id+"F0.wireOp",EDGE,"E10.1.1"),sQuery(id+"F0.wireOp",EDGE,"E10.1.2"),sQuery(id+"F0.wireOp",EDGE,"E10.1.3"),sQuery(id+"F0.wireOp",EDGE,"E10.1.5"),sQuery(id+"F0.wireOp",EDGE,"E10.1.7"),sQuery(id+"F0.wireOp",EDGE,"E10.1.8"),sQuery(id+"F0.wireOp",EDGE,"E10.1.9"),sQuery(id+"F0.wireOp",EDGE,"E10.1.10"),sQuery(id+"F0.wireOp",EDGE,"E10.1.11"),sQuery(id+"F0.wireOp",EDGE,"E10.1.12"),sQuery(id+"F0.wireOp",EDGE,"E10.1.14"),sQuery(id+"F0.wireOp",EDGE,"E10.1.15"),sQuery(id+"F0.wireOp",EDGE,"E10.1.16"),sQuery(id+"F0.wireOp",EDGE,"E10.1.18"),sQuery(id+"F0.wireOp",EDGE,"E10.1.20"),sQuery(id+"F0.wireOp",EDGE,"E10.2.0"),sQuery(id+"F0.wireOp",EDGE,"E10.2.1"),sQuery(id+"F0.wireOp",EDGE,"E10.2.2"),sQuery(id+"F0.wireOp",EDGE,"E10.2.3"),sQuery(id+"F0.wireOp",EDGE,"E10.2.5"),sQuery(id+"F0.wireOp",EDGE,"E10.2.7"),sQuery(id+"F0.wireOp",EDGE,"E10.2.8"),sQuery(id+"F0.wireOp",EDGE,"E10.2.9"),sQuery(id+"F0.wireOp",EDGE,"E10.2.10"),sQuery(id+"F0.wireOp",EDGE,"E10.2.11"),sQuery(id+"F0.wireOp",EDGE,"E10.2.12"),sQuery(id+"F0.wireOp",EDGE,"E1"),sQuery(id+"F0.wireOp",EDGE,"E10.2.14"),sQuery(id+"F0.wireOp",EDGE,"E10.2.15"),sQuery(id+"F0.wireOp",EDGE,"E10.2.16"),sQuery(id+"F0.wireOp",EDGE,"E10.2.18"),sQuery(id+"F0.wireOp",EDGE,"E10.2.20"),sQuery(id+"F0.wireOp",EDGE,"E8.trimOffspring"),sQuery(id+"F0.wireOp",EDGE,"E0"),sQuery(id+"F0.wireOp",EDGE,"E10.1.6"),sQuery(id+"F0.wireOp",EDGE,"E11"),sQuery(id+"F0.wireOp",EDGE,"E12"),sQuery(id+"F0.wireOp",EDGE,"E13.1.0"),sQuery(id+"F0.wireOp",EDGE,"E13.1.1"),sQuery(id+"F0.wireOp",EDGE,"E13.2.0"),sQuery(id+"F0.wireOp",EDGE,"E13.2.1")])]}),"instanceName":"1"}),"instanceName":"1"});
            transform(context, id + "F27", {"entities" : qUnion([Q0]), "transformType" : TransformType.TRANSLATION_3D, "dx" : 0.2 * mm, "dy" : -4.8 * mm, "dz" : 0 * mm, "makeCopy" : false});
        }
        {
            var Q0;
            Q0=makeQuery(id+"F23.opPattern","COPY",BODY,{"derivedFrom":makeQuery(id+"F7.opPattern","COPY",BODY,{"derivedFrom":makeQuery(id+"F1.opExtrude","SWEPT_BODY",BODY,{"disambiguationData":[OSD([sQuery(id+"F0.wireOp",EDGE,"E2.0"),sQuery(id+"F0.wireOp",EDGE,"E2.1"),sQuery(id+"F0.wireOp",EDGE,"E2.2"),sQuery(id+"F0.wireOp",EDGE,"E2.3"),sQuery(id+"F0.wireOp",EDGE,"E2.4"),sQuery(id+"F0.wireOp",EDGE,"E2.5"),sQuery(id+"F0.wireOp",EDGE,"E3"),sQuery(id+"F0.wireOp",EDGE,"E4"),sQuery(id+"F0.wireOp",EDGE,"E5.0"),sQuery(id+"F0.wireOp",EDGE,"E5.1"),sQuery(id+"F0.wireOp",EDGE,"E5.3"),sQuery(id+"F0.wireOp",EDGE,"E5.4"),sQuery(id+"F0.wireOp",EDGE,"E5.5"),sQuery(id+"F0.wireOp",EDGE,"E6.trimOffspring"),sQuery(id+"F0.wireOp",EDGE,"E7.trimOffspring"),sQuery(id+"F0.wireOp",EDGE,"E9.trimOffspring"),sQuery(id+"F0.wireOp",EDGE,"E10.1.0"),sQuery(id+"F0.wireOp",EDGE,"E10.1.1"),sQuery(id+"F0.wireOp",EDGE,"E10.1.2"),sQuery(id+"F0.wireOp",EDGE,"E10.1.3"),sQuery(id+"F0.wireOp",EDGE,"E10.1.5"),sQuery(id+"F0.wireOp",EDGE,"E10.1.7"),sQuery(id+"F0.wireOp",EDGE,"E10.1.8"),sQuery(id+"F0.wireOp",EDGE,"E10.1.9"),sQuery(id+"F0.wireOp",EDGE,"E10.1.10"),sQuery(id+"F0.wireOp",EDGE,"E10.1.11"),sQuery(id+"F0.wireOp",EDGE,"E10.1.12"),sQuery(id+"F0.wireOp",EDGE,"E10.1.14"),sQuery(id+"F0.wireOp",EDGE,"E10.1.15"),sQuery(id+"F0.wireOp",EDGE,"E10.1.16"),sQuery(id+"F0.wireOp",EDGE,"E10.1.18"),sQuery(id+"F0.wireOp",EDGE,"E10.1.20"),sQuery(id+"F0.wireOp",EDGE,"E10.2.0"),sQuery(id+"F0.wireOp",EDGE,"E10.2.1"),sQuery(id+"F0.wireOp",EDGE,"E10.2.2"),sQuery(id+"F0.wireOp",EDGE,"E10.2.3"),sQuery(id+"F0.wireOp",EDGE,"E10.2.5"),sQuery(id+"F0.wireOp",EDGE,"E10.2.7"),sQuery(id+"F0.wireOp",EDGE,"E10.2.8"),sQuery(id+"F0.wireOp",EDGE,"E10.2.9"),sQuery(id+"F0.wireOp",EDGE,"E10.2.10"),sQuery(id+"F0.wireOp",EDGE,"E10.2.11"),sQuery(id+"F0.wireOp",EDGE,"E10.2.12"),sQuery(id+"F0.wireOp",EDGE,"E1"),sQuery(id+"F0.wireOp",EDGE,"E10.2.14"),sQuery(id+"F0.wireOp",EDGE,"E10.2.15"),sQuery(id+"F0.wireOp",EDGE,"E10.2.16"),sQuery(id+"F0.wireOp",EDGE,"E10.2.18"),sQuery(id+"F0.wireOp",EDGE,"E10.2.20"),sQuery(id+"F0.wireOp",EDGE,"E8.trimOffspring"),sQuery(id+"F0.wireOp",EDGE,"E0"),sQuery(id+"F0.wireOp",EDGE,"E10.1.6"),sQuery(id+"F0.wireOp",EDGE,"E11"),sQuery(id+"F0.wireOp",EDGE,"E12"),sQuery(id+"F0.wireOp",EDGE,"E13.1.0"),sQuery(id+"F0.wireOp",EDGE,"E13.1.1"),sQuery(id+"F0.wireOp",EDGE,"E13.2.0"),sQuery(id+"F0.wireOp",EDGE,"E13.2.1")])]}),"instanceName":"1"}),"instanceName":"1"});
            var Q1;
            Q1=makeQuery(id+"F23.opPattern","COPY",EDGE,{"derivedFrom":makeQuery(id+"F7.opPattern","COPY",EDGE,{"derivedFrom":makeQuery(id+"F1.opExtrude","CAP_EDGE",EDGE,{"disambiguationData":[OSD([sQuery(id+"F0.wireOp",EDGE,"E1")])],"isStart":false}),"instanceName":"1"}),"instanceName":"1"});
            transform(context, id + "F28", {"entities" : qUnion([Q0]), "transformType" : TransformType.ROTATION, "transformAxis" : qUnion([Q1]), "angle" : 42 * degree, "makeCopy" : false});
        }
        {
            var Q0;
            Q0=makeQuery(id+"F23.opPattern","COPY",BODY,{"derivedFrom":makeQuery(id+"F7.opPattern","COPY",BODY,{"derivedFrom":makeQuery(id+"F1.opExtrude","SWEPT_BODY",BODY,{"disambiguationData":[OSD([sQuery(id+"F0.wireOp",EDGE,"E2.0"),sQuery(id+"F0.wireOp",EDGE,"E2.1"),sQuery(id+"F0.wireOp",EDGE,"E2.2"),sQuery(id+"F0.wireOp",EDGE,"E2.3"),sQuery(id+"F0.wireOp",EDGE,"E2.4"),sQuery(id+"F0.wireOp",EDGE,"E2.5"),sQuery(id+"F0.wireOp",EDGE,"E3"),sQuery(id+"F0.wireOp",EDGE,"E4"),sQuery(id+"F0.wireOp",EDGE,"E5.0"),sQuery(id+"F0.wireOp",EDGE,"E5.1"),sQuery(id+"F0.wireOp",EDGE,"E5.3"),sQuery(id+"F0.wireOp",EDGE,"E5.4"),sQuery(id+"F0.wireOp",EDGE,"E5.5"),sQuery(id+"F0.wireOp",EDGE,"E6.trimOffspring"),sQuery(id+"F0.wireOp",EDGE,"E7.trimOffspring"),sQuery(id+"F0.wireOp",EDGE,"E9.trimOffspring"),sQuery(id+"F0.wireOp",EDGE,"E10.1.0"),sQuery(id+"F0.wireOp",EDGE,"E10.1.1"),sQuery(id+"F0.wireOp",EDGE,"E10.1.2"),sQuery(id+"F0.wireOp",EDGE,"E10.1.3"),sQuery(id+"F0.wireOp",EDGE,"E10.1.5"),sQuery(id+"F0.wireOp",EDGE,"E10.1.7"),sQuery(id+"F0.wireOp",EDGE,"E10.1.8"),sQuery(id+"F0.wireOp",EDGE,"E10.1.9"),sQuery(id+"F0.wireOp",EDGE,"E10.1.10"),sQuery(id+"F0.wireOp",EDGE,"E10.1.11"),sQuery(id+"F0.wireOp",EDGE,"E10.1.12"),sQuery(id+"F0.wireOp",EDGE,"E10.1.14"),sQuery(id+"F0.wireOp",EDGE,"E10.1.15"),sQuery(id+"F0.wireOp",EDGE,"E10.1.16"),sQuery(id+"F0.wireOp",EDGE,"E10.1.18"),sQuery(id+"F0.wireOp",EDGE,"E10.1.20"),sQuery(id+"F0.wireOp",EDGE,"E10.2.0"),sQuery(id+"F0.wireOp",EDGE,"E10.2.1"),sQuery(id+"F0.wireOp",EDGE,"E10.2.2"),sQuery(id+"F0.wireOp",EDGE,"E10.2.3"),sQuery(id+"F0.wireOp",EDGE,"E10.2.5"),sQuery(id+"F0.wireOp",EDGE,"E10.2.7"),sQuery(id+"F0.wireOp",EDGE,"E10.2.8"),sQuery(id+"F0.wireOp",EDGE,"E10.2.9"),sQuery(id+"F0.wireOp",EDGE,"E10.2.10"),sQuery(id+"F0.wireOp",EDGE,"E10.2.11"),sQuery(id+"F0.wireOp",EDGE,"E10.2.12"),sQuery(id+"F0.wireOp",EDGE,"E1"),sQuery(id+"F0.wireOp",EDGE,"E10.2.14"),sQuery(id+"F0.wireOp",EDGE,"E10.2.15"),sQuery(id+"F0.wireOp",EDGE,"E10.2.16"),sQuery(id+"F0.wireOp",EDGE,"E10.2.18"),sQuery(id+"F0.wireOp",EDGE,"E10.2.20"),sQuery(id+"F0.wireOp",EDGE,"E8.trimOffspring"),sQuery(id+"F0.wireOp",EDGE,"E0"),sQuery(id+"F0.wireOp",EDGE,"E10.1.6"),sQuery(id+"F0.wireOp",EDGE,"E11"),sQuery(id+"F0.wireOp",EDGE,"E12"),sQuery(id+"F0.wireOp",EDGE,"E13.1.0"),sQuery(id+"F0.wireOp",EDGE,"E13.1.1"),sQuery(id+"F0.wireOp",EDGE,"E13.2.0"),sQuery(id+"F0.wireOp",EDGE,"E13.2.1")])]}),"instanceName":"1"}),"instanceName":"1"});
            var Q1;
            Q1=makeQuery(id+"F23.opPattern","COPY",EDGE,{"derivedFrom":makeQuery(id+"F7.opPattern","COPY",EDGE,{"derivedFrom":makeQuery(id+"F1.opExtrude","CAP_EDGE",EDGE,{"disambiguationData":[OSD([sQuery(id+"F0.wireOp",EDGE,"E1")])],"isStart":false}),"instanceName":"1"}),"instanceName":"1"});
            transform(context, id + "F29", {"entities" : qUnion([Q0]), "transformType" : TransformType.ROTATION, "transformAxis" : qUnion([Q1]), "angle" : 82 * degree, "oppositeDirection" : true, "makeCopy" : false});
        }
        {
            var Q0;
            Q0=makeQuery(id+"F23.opPattern","COPY",BODY,{"derivedFrom":makeQuery(id+"F7.opPattern","COPY",BODY,{"derivedFrom":makeQuery(id+"F1.opExtrude","SWEPT_BODY",BODY,{"disambiguationData":[OSD([sQuery(id+"F0.wireOp",EDGE,"E2.0"),sQuery(id+"F0.wireOp",EDGE,"E2.1"),sQuery(id+"F0.wireOp",EDGE,"E2.2"),sQuery(id+"F0.wireOp",EDGE,"E2.3"),sQuery(id+"F0.wireOp",EDGE,"E2.4"),sQuery(id+"F0.wireOp",EDGE,"E2.5"),sQuery(id+"F0.wireOp",EDGE,"E3"),sQuery(id+"F0.wireOp",EDGE,"E4"),sQuery(id+"F0.wireOp",EDGE,"E5.0"),sQuery(id+"F0.wireOp",EDGE,"E5.1"),sQuery(id+"F0.wireOp",EDGE,"E5.3"),sQuery(id+"F0.wireOp",EDGE,"E5.4"),sQuery(id+"F0.wireOp",EDGE,"E5.5"),sQuery(id+"F0.wireOp",EDGE,"E6.trimOffspring"),sQuery(id+"F0.wireOp",EDGE,"E7.trimOffspring"),sQuery(id+"F0.wireOp",EDGE,"E9.trimOffspring"),sQuery(id+"F0.wireOp",EDGE,"E10.1.0"),sQuery(id+"F0.wireOp",EDGE,"E10.1.1"),sQuery(id+"F0.wireOp",EDGE,"E10.1.2"),sQuery(id+"F0.wireOp",EDGE,"E10.1.3"),sQuery(id+"F0.wireOp",EDGE,"E10.1.5"),sQuery(id+"F0.wireOp",EDGE,"E10.1.7"),sQuery(id+"F0.wireOp",EDGE,"E10.1.8"),sQuery(id+"F0.wireOp",EDGE,"E10.1.9"),sQuery(id+"F0.wireOp",EDGE,"E10.1.10"),sQuery(id+"F0.wireOp",EDGE,"E10.1.11"),sQuery(id+"F0.wireOp",EDGE,"E10.1.12"),sQuery(id+"F0.wireOp",EDGE,"E10.1.14"),sQuery(id+"F0.wireOp",EDGE,"E10.1.15"),sQuery(id+"F0.wireOp",EDGE,"E10.1.16"),sQuery(id+"F0.wireOp",EDGE,"E10.1.18"),sQuery(id+"F0.wireOp",EDGE,"E10.1.20"),sQuery(id+"F0.wireOp",EDGE,"E10.2.0"),sQuery(id+"F0.wireOp",EDGE,"E10.2.1"),sQuery(id+"F0.wireOp",EDGE,"E10.2.2"),sQuery(id+"F0.wireOp",EDGE,"E10.2.3"),sQuery(id+"F0.wireOp",EDGE,"E10.2.5"),sQuery(id+"F0.wireOp",EDGE,"E10.2.7"),sQuery(id+"F0.wireOp",EDGE,"E10.2.8"),sQuery(id+"F0.wireOp",EDGE,"E10.2.9"),sQuery(id+"F0.wireOp",EDGE,"E10.2.10"),sQuery(id+"F0.wireOp",EDGE,"E10.2.11"),sQuery(id+"F0.wireOp",EDGE,"E10.2.12"),sQuery(id+"F0.wireOp",EDGE,"E1"),sQuery(id+"F0.wireOp",EDGE,"E10.2.14"),sQuery(id+"F0.wireOp",EDGE,"E10.2.15"),sQuery(id+"F0.wireOp",EDGE,"E10.2.16"),sQuery(id+"F0.wireOp",EDGE,"E10.2.18"),sQuery(id+"F0.wireOp",EDGE,"E10.2.20"),sQuery(id+"F0.wireOp",EDGE,"E8.trimOffspring"),sQuery(id+"F0.wireOp",EDGE,"E0"),sQuery(id+"F0.wireOp",EDGE,"E10.1.6"),sQuery(id+"F0.wireOp",EDGE,"E11"),sQuery(id+"F0.wireOp",EDGE,"E12"),sQuery(id+"F0.wireOp",EDGE,"E13.1.0"),sQuery(id+"F0.wireOp",EDGE,"E13.1.1"),sQuery(id+"F0.wireOp",EDGE,"E13.2.0"),sQuery(id+"F0.wireOp",EDGE,"E13.2.1")])]}),"instanceName":"1"}),"instanceName":"1"});
            transform(context, id + "F30", {"entities" : qUnion([Q0]), "transformType" : TransformType.TRANSLATION_3D, "dx" : 2.4 * mm, "dy" : -4.7 * mm, "dz" : 0 * mm, "makeCopy" : false});
        }
        {
            var Q0;
            Q0=makeQuery(id+"F23.opPattern","COPY",BODY,{"derivedFrom":makeQuery(id+"F8.opPattern","COPY",BODY,{"derivedFrom":makeQuery(id+"F7.opPattern","COPY",BODY,{"derivedFrom":makeQuery(id+"F1.opExtrude","SWEPT_BODY",BODY,{"disambiguationData":[OSD([sQuery(id+"F0.wireOp",EDGE,"E2.0"),sQuery(id+"F0.wireOp",EDGE,"E2.1"),sQuery(id+"F0.wireOp",EDGE,"E2.2"),sQuery(id+"F0.wireOp",EDGE,"E2.3"),sQuery(id+"F0.wireOp",EDGE,"E2.4"),sQuery(id+"F0.wireOp",EDGE,"E2.5"),sQuery(id+"F0.wireOp",EDGE,"E3"),sQuery(id+"F0.wireOp",EDGE,"E4"),sQuery(id+"F0.wireOp",EDGE,"E5.0"),sQuery(id+"F0.wireOp",EDGE,"E5.1"),sQuery(id+"F0.wireOp",EDGE,"E5.3"),sQuery(id+"F0.wireOp",EDGE,"E5.4"),sQuery(id+"F0.wireOp",EDGE,"E5.5"),sQuery(id+"F0.wireOp",EDGE,"E6.trimOffspring"),sQuery(id+"F0.wireOp",EDGE,"E7.trimOffspring"),sQuery(id+"F0.wireOp",EDGE,"E9.trimOffspring"),sQuery(id+"F0.wireOp",EDGE,"E10.1.0"),sQuery(id+"F0.wireOp",EDGE,"E10.1.1"),sQuery(id+"F0.wireOp",EDGE,"E10.1.2"),sQuery(id+"F0.wireOp",EDGE,"E10.1.3"),sQuery(id+"F0.wireOp",EDGE,"E10.1.5"),sQuery(id+"F0.wireOp",EDGE,"E10.1.7"),sQuery(id+"F0.wireOp",EDGE,"E10.1.8"),sQuery(id+"F0.wireOp",EDGE,"E10.1.9"),sQuery(id+"F0.wireOp",EDGE,"E10.1.10"),sQuery(id+"F0.wireOp",EDGE,"E10.1.11"),sQuery(id+"F0.wireOp",EDGE,"E10.1.12"),sQuery(id+"F0.wireOp",EDGE,"E10.1.14"),sQuery(id+"F0.wireOp",EDGE,"E10.1.15"),sQuery(id+"F0.wireOp",EDGE,"E10.1.16"),sQuery(id+"F0.wireOp",EDGE,"E10.1.18"),sQuery(id+"F0.wireOp",EDGE,"E10.1.20"),sQuery(id+"F0.wireOp",EDGE,"E10.2.0"),sQuery(id+"F0.wireOp",EDGE,"E10.2.1"),sQuery(id+"F0.wireOp",EDGE,"E10.2.2"),sQuery(id+"F0.wireOp",EDGE,"E10.2.3"),sQuery(id+"F0.wireOp",EDGE,"E10.2.5"),sQuery(id+"F0.wireOp",EDGE,"E10.2.7"),sQuery(id+"F0.wireOp",EDGE,"E10.2.8"),sQuery(id+"F0.wireOp",EDGE,"E10.2.9"),sQuery(id+"F0.wireOp",EDGE,"E10.2.10"),sQuery(id+"F0.wireOp",EDGE,"E10.2.11"),sQuery(id+"F0.wireOp",EDGE,"E10.2.12"),sQuery(id+"F0.wireOp",EDGE,"E1"),sQuery(id+"F0.wireOp",EDGE,"E10.2.14"),sQuery(id+"F0.wireOp",EDGE,"E10.2.15"),sQuery(id+"F0.wireOp",EDGE,"E10.2.16"),sQuery(id+"F0.wireOp",EDGE,"E10.2.18"),sQuery(id+"F0.wireOp",EDGE,"E10.2.20"),sQuery(id+"F0.wireOp",EDGE,"E8.trimOffspring"),sQuery(id+"F0.wireOp",EDGE,"E0"),sQuery(id+"F0.wireOp",EDGE,"E10.1.6"),sQuery(id+"F0.wireOp",EDGE,"E11"),sQuery(id+"F0.wireOp",EDGE,"E12"),sQuery(id+"F0.wireOp",EDGE,"E13.1.0"),sQuery(id+"F0.wireOp",EDGE,"E13.1.1"),sQuery(id+"F0.wireOp",EDGE,"E13.2.0"),sQuery(id+"F0.wireOp",EDGE,"E13.2.1")])]}),"instanceName":"1"}),"instanceName":"1"}),"instanceName":"1"});
            var Q1;
            Q1=makeQuery(id+"F23.opPattern","COPY",EDGE,{"derivedFrom":makeQuery(id+"F8.opPattern","COPY",EDGE,{"derivedFrom":makeQuery(id+"F7.opPattern","COPY",EDGE,{"derivedFrom":makeQuery(id+"F1.opExtrude","CAP_EDGE",EDGE,{"disambiguationData":[OSD([sQuery(id+"F0.wireOp",EDGE,"E1")])],"isStart":false}),"instanceName":"1"}),"instanceName":"1"}),"instanceName":"1"});
            transform(context, id + "F31", {"entities" : qUnion([Q0]), "transformType" : TransformType.ROTATION, "transformAxis" : qUnion([Q1]), "angle" : 82 * degree, "makeCopy" : false});
        }
        {
            var Q0;
            Q0=makeQuery(id+"F23.opPattern","COPY",BODY,{"derivedFrom":makeQuery(id+"F8.opPattern","COPY",BODY,{"derivedFrom":makeQuery(id+"F7.opPattern","COPY",BODY,{"derivedFrom":makeQuery(id+"F1.opExtrude","SWEPT_BODY",BODY,{"disambiguationData":[OSD([sQuery(id+"F0.wireOp",EDGE,"E2.0"),sQuery(id+"F0.wireOp",EDGE,"E2.1"),sQuery(id+"F0.wireOp",EDGE,"E2.2"),sQuery(id+"F0.wireOp",EDGE,"E2.3"),sQuery(id+"F0.wireOp",EDGE,"E2.4"),sQuery(id+"F0.wireOp",EDGE,"E2.5"),sQuery(id+"F0.wireOp",EDGE,"E3"),sQuery(id+"F0.wireOp",EDGE,"E4"),sQuery(id+"F0.wireOp",EDGE,"E5.0"),sQuery(id+"F0.wireOp",EDGE,"E5.1"),sQuery(id+"F0.wireOp",EDGE,"E5.3"),sQuery(id+"F0.wireOp",EDGE,"E5.4"),sQuery(id+"F0.wireOp",EDGE,"E5.5"),sQuery(id+"F0.wireOp",EDGE,"E6.trimOffspring"),sQuery(id+"F0.wireOp",EDGE,"E7.trimOffspring"),sQuery(id+"F0.wireOp",EDGE,"E9.trimOffspring"),sQuery(id+"F0.wireOp",EDGE,"E10.1.0"),sQuery(id+"F0.wireOp",EDGE,"E10.1.1"),sQuery(id+"F0.wireOp",EDGE,"E10.1.2"),sQuery(id+"F0.wireOp",EDGE,"E10.1.3"),sQuery(id+"F0.wireOp",EDGE,"E10.1.5"),sQuery(id+"F0.wireOp",EDGE,"E10.1.7"),sQuery(id+"F0.wireOp",EDGE,"E10.1.8"),sQuery(id+"F0.wireOp",EDGE,"E10.1.9"),sQuery(id+"F0.wireOp",EDGE,"E10.1.10"),sQuery(id+"F0.wireOp",EDGE,"E10.1.11"),sQuery(id+"F0.wireOp",EDGE,"E10.1.12"),sQuery(id+"F0.wireOp",EDGE,"E10.1.14"),sQuery(id+"F0.wireOp",EDGE,"E10.1.15"),sQuery(id+"F0.wireOp",EDGE,"E10.1.16"),sQuery(id+"F0.wireOp",EDGE,"E10.1.18"),sQuery(id+"F0.wireOp",EDGE,"E10.1.20"),sQuery(id+"F0.wireOp",EDGE,"E10.2.0"),sQuery(id+"F0.wireOp",EDGE,"E10.2.1"),sQuery(id+"F0.wireOp",EDGE,"E10.2.2"),sQuery(id+"F0.wireOp",EDGE,"E10.2.3"),sQuery(id+"F0.wireOp",EDGE,"E10.2.5"),sQuery(id+"F0.wireOp",EDGE,"E10.2.7"),sQuery(id+"F0.wireOp",EDGE,"E10.2.8"),sQuery(id+"F0.wireOp",EDGE,"E10.2.9"),sQuery(id+"F0.wireOp",EDGE,"E10.2.10"),sQuery(id+"F0.wireOp",EDGE,"E10.2.11"),sQuery(id+"F0.wireOp",EDGE,"E10.2.12"),sQuery(id+"F0.wireOp",EDGE,"E1"),sQuery(id+"F0.wireOp",EDGE,"E10.2.14"),sQuery(id+"F0.wireOp",EDGE,"E10.2.15"),sQuery(id+"F0.wireOp",EDGE,"E10.2.16"),sQuery(id+"F0.wireOp",EDGE,"E10.2.18"),sQuery(id+"F0.wireOp",EDGE,"E10.2.20"),sQuery(id+"F0.wireOp",EDGE,"E8.trimOffspring"),sQuery(id+"F0.wireOp",EDGE,"E0"),sQuery(id+"F0.wireOp",EDGE,"E10.1.6"),sQuery(id+"F0.wireOp",EDGE,"E11"),sQuery(id+"F0.wireOp",EDGE,"E12"),sQuery(id+"F0.wireOp",EDGE,"E13.1.0"),sQuery(id+"F0.wireOp",EDGE,"E13.1.1"),sQuery(id+"F0.wireOp",EDGE,"E13.2.0"),sQuery(id+"F0.wireOp",EDGE,"E13.2.1")])]}),"instanceName":"1"}),"instanceName":"1"}),"instanceName":"1"});
            transform(context, id + "F32", {"entities" : qUnion([Q0]), "transformType" : TransformType.TRANSLATION_3D, "dx" : 3.2 * mm, "dy" : -4.7 * mm, "dz" : 0 * mm, "makeCopy" : false});
        }
        {
            var Q0;
            Q0=makeQuery(id+"F23.opPattern","COPY",BODY,{"derivedFrom":makeQuery(id+"F8.opPattern","COPY",BODY,{"derivedFrom":makeQuery(id+"F7.opPattern","COPY",BODY,{"derivedFrom":makeQuery(id+"F1.opExtrude","SWEPT_BODY",BODY,{"disambiguationData":[OSD([sQuery(id+"F0.wireOp",EDGE,"E2.0"),sQuery(id+"F0.wireOp",EDGE,"E2.1"),sQuery(id+"F0.wireOp",EDGE,"E2.2"),sQuery(id+"F0.wireOp",EDGE,"E2.3"),sQuery(id+"F0.wireOp",EDGE,"E2.4"),sQuery(id+"F0.wireOp",EDGE,"E2.5"),sQuery(id+"F0.wireOp",EDGE,"E3"),sQuery(id+"F0.wireOp",EDGE,"E4"),sQuery(id+"F0.wireOp",EDGE,"E5.0"),sQuery(id+"F0.wireOp",EDGE,"E5.1"),sQuery(id+"F0.wireOp",EDGE,"E5.3"),sQuery(id+"F0.wireOp",EDGE,"E5.4"),sQuery(id+"F0.wireOp",EDGE,"E5.5"),sQuery(id+"F0.wireOp",EDGE,"E6.trimOffspring"),sQuery(id+"F0.wireOp",EDGE,"E7.trimOffspring"),sQuery(id+"F0.wireOp",EDGE,"E9.trimOffspring"),sQuery(id+"F0.wireOp",EDGE,"E10.1.0"),sQuery(id+"F0.wireOp",EDGE,"E10.1.1"),sQuery(id+"F0.wireOp",EDGE,"E10.1.2"),sQuery(id+"F0.wireOp",EDGE,"E10.1.3"),sQuery(id+"F0.wireOp",EDGE,"E10.1.5"),sQuery(id+"F0.wireOp",EDGE,"E10.1.7"),sQuery(id+"F0.wireOp",EDGE,"E10.1.8"),sQuery(id+"F0.wireOp",EDGE,"E10.1.9"),sQuery(id+"F0.wireOp",EDGE,"E10.1.10"),sQuery(id+"F0.wireOp",EDGE,"E10.1.11"),sQuery(id+"F0.wireOp",EDGE,"E10.1.12"),sQuery(id+"F0.wireOp",EDGE,"E10.1.14"),sQuery(id+"F0.wireOp",EDGE,"E10.1.15"),sQuery(id+"F0.wireOp",EDGE,"E10.1.16"),sQuery(id+"F0.wireOp",EDGE,"E10.1.18"),sQuery(id+"F0.wireOp",EDGE,"E10.1.20"),sQuery(id+"F0.wireOp",EDGE,"E10.2.0"),sQuery(id+"F0.wireOp",EDGE,"E10.2.1"),sQuery(id+"F0.wireOp",EDGE,"E10.2.2"),sQuery(id+"F0.wireOp",EDGE,"E10.2.3"),sQuery(id+"F0.wireOp",EDGE,"E10.2.5"),sQuery(id+"F0.wireOp",EDGE,"E10.2.7"),sQuery(id+"F0.wireOp",EDGE,"E10.2.8"),sQuery(id+"F0.wireOp",EDGE,"E10.2.9"),sQuery(id+"F0.wireOp",EDGE,"E10.2.10"),sQuery(id+"F0.wireOp",EDGE,"E10.2.11"),sQuery(id+"F0.wireOp",EDGE,"E10.2.12"),sQuery(id+"F0.wireOp",EDGE,"E1"),sQuery(id+"F0.wireOp",EDGE,"E10.2.14"),sQuery(id+"F0.wireOp",EDGE,"E10.2.15"),sQuery(id+"F0.wireOp",EDGE,"E10.2.16"),sQuery(id+"F0.wireOp",EDGE,"E10.2.18"),sQuery(id+"F0.wireOp",EDGE,"E10.2.20"),sQuery(id+"F0.wireOp",EDGE,"E8.trimOffspring"),sQuery(id+"F0.wireOp",EDGE,"E0"),sQuery(id+"F0.wireOp",EDGE,"E10.1.6"),sQuery(id+"F0.wireOp",EDGE,"E11"),sQuery(id+"F0.wireOp",EDGE,"E12"),sQuery(id+"F0.wireOp",EDGE,"E13.1.0"),sQuery(id+"F0.wireOp",EDGE,"E13.1.1"),sQuery(id+"F0.wireOp",EDGE,"E13.2.0"),sQuery(id+"F0.wireOp",EDGE,"E13.2.1")])]}),"instanceName":"1"}),"instanceName":"1"}),"instanceName":"1"});
            transform(context, id + "F33", {"entities" : qUnion([Q0]), "transformType" : TransformType.TRANSLATION_3D, "dx" : 119 * mm, "dy" : -8 * mm, "dz" : 0 * mm, "makeCopy" : false});
        }
        {
            var Q0;
            Q0=makeQuery(id+"F23.opPattern","COPY",BODY,{"derivedFrom":makeQuery(id+"F8.opPattern","COPY",BODY,{"derivedFrom":makeQuery(id+"F7.opPattern","COPY",BODY,{"derivedFrom":makeQuery(id+"F1.opExtrude","SWEPT_BODY",BODY,{"disambiguationData":[OSD([sQuery(id+"F0.wireOp",EDGE,"E2.0"),sQuery(id+"F0.wireOp",EDGE,"E2.1"),sQuery(id+"F0.wireOp",EDGE,"E2.2"),sQuery(id+"F0.wireOp",EDGE,"E2.3"),sQuery(id+"F0.wireOp",EDGE,"E2.4"),sQuery(id+"F0.wireOp",EDGE,"E2.5"),sQuery(id+"F0.wireOp",EDGE,"E3"),sQuery(id+"F0.wireOp",EDGE,"E4"),sQuery(id+"F0.wireOp",EDGE,"E5.0"),sQuery(id+"F0.wireOp",EDGE,"E5.1"),sQuery(id+"F0.wireOp",EDGE,"E5.3"),sQuery(id+"F0.wireOp",EDGE,"E5.4"),sQuery(id+"F0.wireOp",EDGE,"E5.5"),sQuery(id+"F0.wireOp",EDGE,"E6.trimOffspring"),sQuery(id+"F0.wireOp",EDGE,"E7.trimOffspring"),sQuery(id+"F0.wireOp",EDGE,"E9.trimOffspring"),sQuery(id+"F0.wireOp",EDGE,"E10.1.0"),sQuery(id+"F0.wireOp",EDGE,"E10.1.1"),sQuery(id+"F0.wireOp",EDGE,"E10.1.2"),sQuery(id+"F0.wireOp",EDGE,"E10.1.3"),sQuery(id+"F0.wireOp",EDGE,"E10.1.5"),sQuery(id+"F0.wireOp",EDGE,"E10.1.7"),sQuery(id+"F0.wireOp",EDGE,"E10.1.8"),sQuery(id+"F0.wireOp",EDGE,"E10.1.9"),sQuery(id+"F0.wireOp",EDGE,"E10.1.10"),sQuery(id+"F0.wireOp",EDGE,"E10.1.11"),sQuery(id+"F0.wireOp",EDGE,"E10.1.12"),sQuery(id+"F0.wireOp",EDGE,"E10.1.14"),sQuery(id+"F0.wireOp",EDGE,"E10.1.15"),sQuery(id+"F0.wireOp",EDGE,"E10.1.16"),sQuery(id+"F0.wireOp",EDGE,"E10.1.18"),sQuery(id+"F0.wireOp",EDGE,"E10.1.20"),sQuery(id+"F0.wireOp",EDGE,"E10.2.0"),sQuery(id+"F0.wireOp",EDGE,"E10.2.1"),sQuery(id+"F0.wireOp",EDGE,"E10.2.2"),sQuery(id+"F0.wireOp",EDGE,"E10.2.3"),sQuery(id+"F0.wireOp",EDGE,"E10.2.5"),sQuery(id+"F0.wireOp",EDGE,"E10.2.7"),sQuery(id+"F0.wireOp",EDGE,"E10.2.8"),sQuery(id+"F0.wireOp",EDGE,"E10.2.9"),sQuery(id+"F0.wireOp",EDGE,"E10.2.10"),sQuery(id+"F0.wireOp",EDGE,"E10.2.11"),sQuery(id+"F0.wireOp",EDGE,"E10.2.12"),sQuery(id+"F0.wireOp",EDGE,"E1"),sQuery(id+"F0.wireOp",EDGE,"E10.2.14"),sQuery(id+"F0.wireOp",EDGE,"E10.2.15"),sQuery(id+"F0.wireOp",EDGE,"E10.2.16"),sQuery(id+"F0.wireOp",EDGE,"E10.2.18"),sQuery(id+"F0.wireOp",EDGE,"E10.2.20"),sQuery(id+"F0.wireOp",EDGE,"E8.trimOffspring"),sQuery(id+"F0.wireOp",EDGE,"E0"),sQuery(id+"F0.wireOp",EDGE,"E10.1.6"),sQuery(id+"F0.wireOp",EDGE,"E11"),sQuery(id+"F0.wireOp",EDGE,"E12"),sQuery(id+"F0.wireOp",EDGE,"E13.1.0"),sQuery(id+"F0.wireOp",EDGE,"E13.1.1"),sQuery(id+"F0.wireOp",EDGE,"E13.2.0"),sQuery(id+"F0.wireOp",EDGE,"E13.2.1")])]}),"instanceName":"1"}),"instanceName":"1"}),"instanceName":"1"});
            var Q1;
            Q1=makeQuery(id+"F23.opPattern","COPY",EDGE,{"derivedFrom":makeQuery(id+"F8.opPattern","COPY",EDGE,{"derivedFrom":makeQuery(id+"F7.opPattern","COPY",EDGE,{"derivedFrom":makeQuery(id+"F1.opExtrude","CAP_EDGE",EDGE,{"disambiguationData":[OSD([sQuery(id+"F0.wireOp",EDGE,"E1")])],"isStart":false}),"instanceName":"1"}),"instanceName":"1"}),"instanceName":"1"});
            transform(context, id + "F34", {"entities" : qUnion([Q0]), "transformType" : TransformType.ROTATION, "transformAxis" : qUnion([Q1]), "angle" : 40 * degree, "oppositeDirection" : true, "makeCopy" : false});
        }
        {
            var Q0;
            Q0=makeQuery(id+"F23.opPattern","COPY",BODY,{"derivedFrom":makeQuery(id+"F8.opPattern","COPY",BODY,{"derivedFrom":makeQuery(id+"F7.opPattern","COPY",BODY,{"derivedFrom":makeQuery(id+"F1.opExtrude","SWEPT_BODY",BODY,{"disambiguationData":[OSD([sQuery(id+"F0.wireOp",EDGE,"E2.0"),sQuery(id+"F0.wireOp",EDGE,"E2.1"),sQuery(id+"F0.wireOp",EDGE,"E2.2"),sQuery(id+"F0.wireOp",EDGE,"E2.3"),sQuery(id+"F0.wireOp",EDGE,"E2.4"),sQuery(id+"F0.wireOp",EDGE,"E2.5"),sQuery(id+"F0.wireOp",EDGE,"E3"),sQuery(id+"F0.wireOp",EDGE,"E4"),sQuery(id+"F0.wireOp",EDGE,"E5.0"),sQuery(id+"F0.wireOp",EDGE,"E5.1"),sQuery(id+"F0.wireOp",EDGE,"E5.3"),sQuery(id+"F0.wireOp",EDGE,"E5.4"),sQuery(id+"F0.wireOp",EDGE,"E5.5"),sQuery(id+"F0.wireOp",EDGE,"E6.trimOffspring"),sQuery(id+"F0.wireOp",EDGE,"E7.trimOffspring"),sQuery(id+"F0.wireOp",EDGE,"E9.trimOffspring"),sQuery(id+"F0.wireOp",EDGE,"E10.1.0"),sQuery(id+"F0.wireOp",EDGE,"E10.1.1"),sQuery(id+"F0.wireOp",EDGE,"E10.1.2"),sQuery(id+"F0.wireOp",EDGE,"E10.1.3"),sQuery(id+"F0.wireOp",EDGE,"E10.1.5"),sQuery(id+"F0.wireOp",EDGE,"E10.1.7"),sQuery(id+"F0.wireOp",EDGE,"E10.1.8"),sQuery(id+"F0.wireOp",EDGE,"E10.1.9"),sQuery(id+"F0.wireOp",EDGE,"E10.1.10"),sQuery(id+"F0.wireOp",EDGE,"E10.1.11"),sQuery(id+"F0.wireOp",EDGE,"E10.1.12"),sQuery(id+"F0.wireOp",EDGE,"E10.1.14"),sQuery(id+"F0.wireOp",EDGE,"E10.1.15"),sQuery(id+"F0.wireOp",EDGE,"E10.1.16"),sQuery(id+"F0.wireOp",EDGE,"E10.1.18"),sQuery(id+"F0.wireOp",EDGE,"E10.1.20"),sQuery(id+"F0.wireOp",EDGE,"E10.2.0"),sQuery(id+"F0.wireOp",EDGE,"E10.2.1"),sQuery(id+"F0.wireOp",EDGE,"E10.2.2"),sQuery(id+"F0.wireOp",EDGE,"E10.2.3"),sQuery(id+"F0.wireOp",EDGE,"E10.2.5"),sQuery(id+"F0.wireOp",EDGE,"E10.2.7"),sQuery(id+"F0.wireOp",EDGE,"E10.2.8"),sQuery(id+"F0.wireOp",EDGE,"E10.2.9"),sQuery(id+"F0.wireOp",EDGE,"E10.2.10"),sQuery(id+"F0.wireOp",EDGE,"E10.2.11"),sQuery(id+"F0.wireOp",EDGE,"E10.2.12"),sQuery(id+"F0.wireOp",EDGE,"E1"),sQuery(id+"F0.wireOp",EDGE,"E10.2.14"),sQuery(id+"F0.wireOp",EDGE,"E10.2.15"),sQuery(id+"F0.wireOp",EDGE,"E10.2.16"),sQuery(id+"F0.wireOp",EDGE,"E10.2.18"),sQuery(id+"F0.wireOp",EDGE,"E10.2.20"),sQuery(id+"F0.wireOp",EDGE,"E8.trimOffspring"),sQuery(id+"F0.wireOp",EDGE,"E0"),sQuery(id+"F0.wireOp",EDGE,"E10.1.6"),sQuery(id+"F0.wireOp",EDGE,"E11"),sQuery(id+"F0.wireOp",EDGE,"E12"),sQuery(id+"F0.wireOp",EDGE,"E13.1.0"),sQuery(id+"F0.wireOp",EDGE,"E13.1.1"),sQuery(id+"F0.wireOp",EDGE,"E13.2.0"),sQuery(id+"F0.wireOp",EDGE,"E13.2.1")])]}),"instanceName":"1"}),"instanceName":"1"}),"instanceName":"1"});
            transform(context, id + "F35", {"entities" : qUnion([Q0]), "transformType" : TransformType.TRANSLATION_3D, "dx" : 7.9 * mm, "dy" : 6.2 * mm, "dz" : 0 * mm, "makeCopy" : false});
        }
        {
            var Q0;
            Q0=makeQuery(id+"F23.opPattern","COPY",BODY,{"derivedFrom":makeQuery(id+"F7.opPattern","COPY",BODY,{"derivedFrom":makeQuery(id+"F1.opExtrude","SWEPT_BODY",BODY,{"disambiguationData":[OSD([sQuery(id+"F0.wireOp",EDGE,"E2.0"),sQuery(id+"F0.wireOp",EDGE,"E2.1"),sQuery(id+"F0.wireOp",EDGE,"E2.2"),sQuery(id+"F0.wireOp",EDGE,"E2.3"),sQuery(id+"F0.wireOp",EDGE,"E2.4"),sQuery(id+"F0.wireOp",EDGE,"E2.5"),sQuery(id+"F0.wireOp",EDGE,"E3"),sQuery(id+"F0.wireOp",EDGE,"E4"),sQuery(id+"F0.wireOp",EDGE,"E5.0"),sQuery(id+"F0.wireOp",EDGE,"E5.1"),sQuery(id+"F0.wireOp",EDGE,"E5.3"),sQuery(id+"F0.wireOp",EDGE,"E5.4"),sQuery(id+"F0.wireOp",EDGE,"E5.5"),sQuery(id+"F0.wireOp",EDGE,"E6.trimOffspring"),sQuery(id+"F0.wireOp",EDGE,"E7.trimOffspring"),sQuery(id+"F0.wireOp",EDGE,"E9.trimOffspring"),sQuery(id+"F0.wireOp",EDGE,"E10.1.0"),sQuery(id+"F0.wireOp",EDGE,"E10.1.1"),sQuery(id+"F0.wireOp",EDGE,"E10.1.2"),sQuery(id+"F0.wireOp",EDGE,"E10.1.3"),sQuery(id+"F0.wireOp",EDGE,"E10.1.5"),sQuery(id+"F0.wireOp",EDGE,"E10.1.7"),sQuery(id+"F0.wireOp",EDGE,"E10.1.8"),sQuery(id+"F0.wireOp",EDGE,"E10.1.9"),sQuery(id+"F0.wireOp",EDGE,"E10.1.10"),sQuery(id+"F0.wireOp",EDGE,"E10.1.11"),sQuery(id+"F0.wireOp",EDGE,"E10.1.12"),sQuery(id+"F0.wireOp",EDGE,"E10.1.14"),sQuery(id+"F0.wireOp",EDGE,"E10.1.15"),sQuery(id+"F0.wireOp",EDGE,"E10.1.16"),sQuery(id+"F0.wireOp",EDGE,"E10.1.18"),sQuery(id+"F0.wireOp",EDGE,"E10.1.20"),sQuery(id+"F0.wireOp",EDGE,"E10.2.0"),sQuery(id+"F0.wireOp",EDGE,"E10.2.1"),sQuery(id+"F0.wireOp",EDGE,"E10.2.2"),sQuery(id+"F0.wireOp",EDGE,"E10.2.3"),sQuery(id+"F0.wireOp",EDGE,"E10.2.5"),sQuery(id+"F0.wireOp",EDGE,"E10.2.7"),sQuery(id+"F0.wireOp",EDGE,"E10.2.8"),sQuery(id+"F0.wireOp",EDGE,"E10.2.9"),sQuery(id+"F0.wireOp",EDGE,"E10.2.10"),sQuery(id+"F0.wireOp",EDGE,"E10.2.11"),sQuery(id+"F0.wireOp",EDGE,"E10.2.12"),sQuery(id+"F0.wireOp",EDGE,"E1"),sQuery(id+"F0.wireOp",EDGE,"E10.2.14"),sQuery(id+"F0.wireOp",EDGE,"E10.2.15"),sQuery(id+"F0.wireOp",EDGE,"E10.2.16"),sQuery(id+"F0.wireOp",EDGE,"E10.2.18"),sQuery(id+"F0.wireOp",EDGE,"E10.2.20"),sQuery(id+"F0.wireOp",EDGE,"E8.trimOffspring"),sQuery(id+"F0.wireOp",EDGE,"E0"),sQuery(id+"F0.wireOp",EDGE,"E10.1.6"),sQuery(id+"F0.wireOp",EDGE,"E11"),sQuery(id+"F0.wireOp",EDGE,"E12"),sQuery(id+"F0.wireOp",EDGE,"E13.1.0"),sQuery(id+"F0.wireOp",EDGE,"E13.1.1"),sQuery(id+"F0.wireOp",EDGE,"E13.2.0"),sQuery(id+"F0.wireOp",EDGE,"E13.2.1")])]}),"instanceName":"1"}),"instanceName":"1"});
            transform(context, id + "F36", {"entities" : qUnion([Q0]), "transformType" : TransformType.TRANSLATION_3D, "dx" : 69.7 * mm, "dy" : 0 * mm, "dz" : 0 * mm, "makeCopy" : true});
        }
        {
            var Q0;
            Q0=makeQuery(id+"F36.opPattern","COPY",BODY,{"derivedFrom":makeQuery(id+"F23.opPattern","COPY",BODY,{"derivedFrom":makeQuery(id+"F7.opPattern","COPY",BODY,{"derivedFrom":makeQuery(id+"F1.opExtrude","SWEPT_BODY",BODY,{"disambiguationData":[OSD([sQuery(id+"F0.wireOp",EDGE,"E2.0"),sQuery(id+"F0.wireOp",EDGE,"E2.1"),sQuery(id+"F0.wireOp",EDGE,"E2.2"),sQuery(id+"F0.wireOp",EDGE,"E2.3"),sQuery(id+"F0.wireOp",EDGE,"E2.4"),sQuery(id+"F0.wireOp",EDGE,"E2.5"),sQuery(id+"F0.wireOp",EDGE,"E3"),sQuery(id+"F0.wireOp",EDGE,"E4"),sQuery(id+"F0.wireOp",EDGE,"E5.0"),sQuery(id+"F0.wireOp",EDGE,"E5.1"),sQuery(id+"F0.wireOp",EDGE,"E5.3"),sQuery(id+"F0.wireOp",EDGE,"E5.4"),sQuery(id+"F0.wireOp",EDGE,"E5.5"),sQuery(id+"F0.wireOp",EDGE,"E6.trimOffspring"),sQuery(id+"F0.wireOp",EDGE,"E7.trimOffspring"),sQuery(id+"F0.wireOp",EDGE,"E9.trimOffspring"),sQuery(id+"F0.wireOp",EDGE,"E10.1.0"),sQuery(id+"F0.wireOp",EDGE,"E10.1.1"),sQuery(id+"F0.wireOp",EDGE,"E10.1.2"),sQuery(id+"F0.wireOp",EDGE,"E10.1.3"),sQuery(id+"F0.wireOp",EDGE,"E10.1.5"),sQuery(id+"F0.wireOp",EDGE,"E10.1.7"),sQuery(id+"F0.wireOp",EDGE,"E10.1.8"),sQuery(id+"F0.wireOp",EDGE,"E10.1.9"),sQuery(id+"F0.wireOp",EDGE,"E10.1.10"),sQuery(id+"F0.wireOp",EDGE,"E10.1.11"),sQuery(id+"F0.wireOp",EDGE,"E10.1.12"),sQuery(id+"F0.wireOp",EDGE,"E10.1.14"),sQuery(id+"F0.wireOp",EDGE,"E10.1.15"),sQuery(id+"F0.wireOp",EDGE,"E10.1.16"),sQuery(id+"F0.wireOp",EDGE,"E10.1.18"),sQuery(id+"F0.wireOp",EDGE,"E10.1.20"),sQuery(id+"F0.wireOp",EDGE,"E10.2.0"),sQuery(id+"F0.wireOp",EDGE,"E10.2.1"),sQuery(id+"F0.wireOp",EDGE,"E10.2.2"),sQuery(id+"F0.wireOp",EDGE,"E10.2.3"),sQuery(id+"F0.wireOp",EDGE,"E10.2.5"),sQuery(id+"F0.wireOp",EDGE,"E10.2.7"),sQuery(id+"F0.wireOp",EDGE,"E10.2.8"),sQuery(id+"F0.wireOp",EDGE,"E10.2.9"),sQuery(id+"F0.wireOp",EDGE,"E10.2.10"),sQuery(id+"F0.wireOp",EDGE,"E10.2.11"),sQuery(id+"F0.wireOp",EDGE,"E10.2.12"),sQuery(id+"F0.wireOp",EDGE,"E1"),sQuery(id+"F0.wireOp",EDGE,"E10.2.14"),sQuery(id+"F0.wireOp",EDGE,"E10.2.15"),sQuery(id+"F0.wireOp",EDGE,"E10.2.16"),sQuery(id+"F0.wireOp",EDGE,"E10.2.18"),sQuery(id+"F0.wireOp",EDGE,"E10.2.20"),sQuery(id+"F0.wireOp",EDGE,"E8.trimOffspring"),sQuery(id+"F0.wireOp",EDGE,"E0"),sQuery(id+"F0.wireOp",EDGE,"E10.1.6"),sQuery(id+"F0.wireOp",EDGE,"E11"),sQuery(id+"F0.wireOp",EDGE,"E12"),sQuery(id+"F0.wireOp",EDGE,"E13.1.0"),sQuery(id+"F0.wireOp",EDGE,"E13.1.1"),sQuery(id+"F0.wireOp",EDGE,"E13.2.0"),sQuery(id+"F0.wireOp",EDGE,"E13.2.1")])]}),"instanceName":"1"}),"instanceName":"1"}),"instanceName":"1"});
            var Q1;
            Q1=makeQuery(id+"F36.opPattern","COPY",EDGE,{"derivedFrom":makeQuery(id+"F23.opPattern","COPY",EDGE,{"derivedFrom":makeQuery(id+"F7.opPattern","COPY",EDGE,{"derivedFrom":makeQuery(id+"F1.opExtrude","CAP_EDGE",EDGE,{"disambiguationData":[OSD([sQuery(id+"F0.wireOp",EDGE,"E1")])],"isStart":false}),"instanceName":"1"}),"instanceName":"1"}),"instanceName":"1"});
            transform(context, id + "F37", {"entities" : qUnion([Q0]), "transformType" : TransformType.ROTATION, "transformAxis" : qUnion([Q1]), "angle" : 5 * degree, "makeCopy" : false});
        }
        {
            var Q0;
            Q0=makeQuery(id+"F36.opPattern","COPY",BODY,{"derivedFrom":makeQuery(id+"F23.opPattern","COPY",BODY,{"derivedFrom":makeQuery(id+"F7.opPattern","COPY",BODY,{"derivedFrom":makeQuery(id+"F1.opExtrude","SWEPT_BODY",BODY,{"disambiguationData":[OSD([sQuery(id+"F0.wireOp",EDGE,"E2.0"),sQuery(id+"F0.wireOp",EDGE,"E2.1"),sQuery(id+"F0.wireOp",EDGE,"E2.2"),sQuery(id+"F0.wireOp",EDGE,"E2.3"),sQuery(id+"F0.wireOp",EDGE,"E2.4"),sQuery(id+"F0.wireOp",EDGE,"E2.5"),sQuery(id+"F0.wireOp",EDGE,"E3"),sQuery(id+"F0.wireOp",EDGE,"E4"),sQuery(id+"F0.wireOp",EDGE,"E5.0"),sQuery(id+"F0.wireOp",EDGE,"E5.1"),sQuery(id+"F0.wireOp",EDGE,"E5.3"),sQuery(id+"F0.wireOp",EDGE,"E5.4"),sQuery(id+"F0.wireOp",EDGE,"E5.5"),sQuery(id+"F0.wireOp",EDGE,"E6.trimOffspring"),sQuery(id+"F0.wireOp",EDGE,"E7.trimOffspring"),sQuery(id+"F0.wireOp",EDGE,"E9.trimOffspring"),sQuery(id+"F0.wireOp",EDGE,"E10.1.0"),sQuery(id+"F0.wireOp",EDGE,"E10.1.1"),sQuery(id+"F0.wireOp",EDGE,"E10.1.2"),sQuery(id+"F0.wireOp",EDGE,"E10.1.3"),sQuery(id+"F0.wireOp",EDGE,"E10.1.5"),sQuery(id+"F0.wireOp",EDGE,"E10.1.7"),sQuery(id+"F0.wireOp",EDGE,"E10.1.8"),sQuery(id+"F0.wireOp",EDGE,"E10.1.9"),sQuery(id+"F0.wireOp",EDGE,"E10.1.10"),sQuery(id+"F0.wireOp",EDGE,"E10.1.11"),sQuery(id+"F0.wireOp",EDGE,"E10.1.12"),sQuery(id+"F0.wireOp",EDGE,"E10.1.14"),sQuery(id+"F0.wireOp",EDGE,"E10.1.15"),sQuery(id+"F0.wireOp",EDGE,"E10.1.16"),sQuery(id+"F0.wireOp",EDGE,"E10.1.18"),sQuery(id+"F0.wireOp",EDGE,"E10.1.20"),sQuery(id+"F0.wireOp",EDGE,"E10.2.0"),sQuery(id+"F0.wireOp",EDGE,"E10.2.1"),sQuery(id+"F0.wireOp",EDGE,"E10.2.2"),sQuery(id+"F0.wireOp",EDGE,"E10.2.3"),sQuery(id+"F0.wireOp",EDGE,"E10.2.5"),sQuery(id+"F0.wireOp",EDGE,"E10.2.7"),sQuery(id+"F0.wireOp",EDGE,"E10.2.8"),sQuery(id+"F0.wireOp",EDGE,"E10.2.9"),sQuery(id+"F0.wireOp",EDGE,"E10.2.10"),sQuery(id+"F0.wireOp",EDGE,"E10.2.11"),sQuery(id+"F0.wireOp",EDGE,"E10.2.12"),sQuery(id+"F0.wireOp",EDGE,"E1"),sQuery(id+"F0.wireOp",EDGE,"E10.2.14"),sQuery(id+"F0.wireOp",EDGE,"E10.2.15"),sQuery(id+"F0.wireOp",EDGE,"E10.2.16"),sQuery(id+"F0.wireOp",EDGE,"E10.2.18"),sQuery(id+"F0.wireOp",EDGE,"E10.2.20"),sQuery(id+"F0.wireOp",EDGE,"E8.trimOffspring"),sQuery(id+"F0.wireOp",EDGE,"E0"),sQuery(id+"F0.wireOp",EDGE,"E10.1.6"),sQuery(id+"F0.wireOp",EDGE,"E11"),sQuery(id+"F0.wireOp",EDGE,"E12"),sQuery(id+"F0.wireOp",EDGE,"E13.1.0"),sQuery(id+"F0.wireOp",EDGE,"E13.1.1"),sQuery(id+"F0.wireOp",EDGE,"E13.2.0"),sQuery(id+"F0.wireOp",EDGE,"E13.2.1")])]}),"instanceName":"1"}),"instanceName":"1"}),"instanceName":"1"});
            transform(context, id + "F38", {"entities" : qUnion([Q0]), "transformType" : TransformType.TRANSLATION_3D, "dx" : 2 * mm, "dy" : 0 * mm, "dz" : 0 * mm, "makeCopy" : false});
        }
        {
            var Q0;
            Q0=makeQuery(id+"F36.opPattern","COPY",BODY,{"derivedFrom":makeQuery(id+"F23.opPattern","COPY",BODY,{"derivedFrom":makeQuery(id+"F7.opPattern","COPY",BODY,{"derivedFrom":makeQuery(id+"F1.opExtrude","SWEPT_BODY",BODY,{"disambiguationData":[OSD([sQuery(id+"F0.wireOp",EDGE,"E2.0"),sQuery(id+"F0.wireOp",EDGE,"E2.1"),sQuery(id+"F0.wireOp",EDGE,"E2.2"),sQuery(id+"F0.wireOp",EDGE,"E2.3"),sQuery(id+"F0.wireOp",EDGE,"E2.4"),sQuery(id+"F0.wireOp",EDGE,"E2.5"),sQuery(id+"F0.wireOp",EDGE,"E3"),sQuery(id+"F0.wireOp",EDGE,"E4"),sQuery(id+"F0.wireOp",EDGE,"E5.0"),sQuery(id+"F0.wireOp",EDGE,"E5.1"),sQuery(id+"F0.wireOp",EDGE,"E5.3"),sQuery(id+"F0.wireOp",EDGE,"E5.4"),sQuery(id+"F0.wireOp",EDGE,"E5.5"),sQuery(id+"F0.wireOp",EDGE,"E6.trimOffspring"),sQuery(id+"F0.wireOp",EDGE,"E7.trimOffspring"),sQuery(id+"F0.wireOp",EDGE,"E9.trimOffspring"),sQuery(id+"F0.wireOp",EDGE,"E10.1.0"),sQuery(id+"F0.wireOp",EDGE,"E10.1.1"),sQuery(id+"F0.wireOp",EDGE,"E10.1.2"),sQuery(id+"F0.wireOp",EDGE,"E10.1.3"),sQuery(id+"F0.wireOp",EDGE,"E10.1.5"),sQuery(id+"F0.wireOp",EDGE,"E10.1.7"),sQuery(id+"F0.wireOp",EDGE,"E10.1.8"),sQuery(id+"F0.wireOp",EDGE,"E10.1.9"),sQuery(id+"F0.wireOp",EDGE,"E10.1.10"),sQuery(id+"F0.wireOp",EDGE,"E10.1.11"),sQuery(id+"F0.wireOp",EDGE,"E10.1.12"),sQuery(id+"F0.wireOp",EDGE,"E10.1.14"),sQuery(id+"F0.wireOp",EDGE,"E10.1.15"),sQuery(id+"F0.wireOp",EDGE,"E10.1.16"),sQuery(id+"F0.wireOp",EDGE,"E10.1.18"),sQuery(id+"F0.wireOp",EDGE,"E10.1.20"),sQuery(id+"F0.wireOp",EDGE,"E10.2.0"),sQuery(id+"F0.wireOp",EDGE,"E10.2.1"),sQuery(id+"F0.wireOp",EDGE,"E10.2.2"),sQuery(id+"F0.wireOp",EDGE,"E10.2.3"),sQuery(id+"F0.wireOp",EDGE,"E10.2.5"),sQuery(id+"F0.wireOp",EDGE,"E10.2.7"),sQuery(id+"F0.wireOp",EDGE,"E10.2.8"),sQuery(id+"F0.wireOp",EDGE,"E10.2.9"),sQuery(id+"F0.wireOp",EDGE,"E10.2.10"),sQuery(id+"F0.wireOp",EDGE,"E10.2.11"),sQuery(id+"F0.wireOp",EDGE,"E10.2.12"),sQuery(id+"F0.wireOp",EDGE,"E1"),sQuery(id+"F0.wireOp",EDGE,"E10.2.14"),sQuery(id+"F0.wireOp",EDGE,"E10.2.15"),sQuery(id+"F0.wireOp",EDGE,"E10.2.16"),sQuery(id+"F0.wireOp",EDGE,"E10.2.18"),sQuery(id+"F0.wireOp",EDGE,"E10.2.20"),sQuery(id+"F0.wireOp",EDGE,"E8.trimOffspring"),sQuery(id+"F0.wireOp",EDGE,"E0"),sQuery(id+"F0.wireOp",EDGE,"E10.1.6"),sQuery(id+"F0.wireOp",EDGE,"E11"),sQuery(id+"F0.wireOp",EDGE,"E12"),sQuery(id+"F0.wireOp",EDGE,"E13.1.0"),sQuery(id+"F0.wireOp",EDGE,"E13.1.1"),sQuery(id+"F0.wireOp",EDGE,"E13.2.0"),sQuery(id+"F0.wireOp",EDGE,"E13.2.1")])]}),"instanceName":"1"}),"instanceName":"1"}),"instanceName":"1"});
            transform(context, id + "F39", {"entities" : qUnion([Q0]), "transformType" : TransformType.TRANSLATION_3D, "dx" : 63.8 * mm, "dy" : -27.7 * mm, "dz" : 0 * mm, "makeCopy" : true});
        }
        {
            var Q0;
            Q0=makeQuery(id+"F39.opPattern","COPY",BODY,{"derivedFrom":makeQuery(id+"F36.opPattern","COPY",BODY,{"derivedFrom":makeQuery(id+"F23.opPattern","COPY",BODY,{"derivedFrom":makeQuery(id+"F7.opPattern","COPY",BODY,{"derivedFrom":makeQuery(id+"F1.opExtrude","SWEPT_BODY",BODY,{"disambiguationData":[OSD([sQuery(id+"F0.wireOp",EDGE,"E2.0"),sQuery(id+"F0.wireOp",EDGE,"E2.1"),sQuery(id+"F0.wireOp",EDGE,"E2.2"),sQuery(id+"F0.wireOp",EDGE,"E2.3"),sQuery(id+"F0.wireOp",EDGE,"E2.4"),sQuery(id+"F0.wireOp",EDGE,"E2.5"),sQuery(id+"F0.wireOp",EDGE,"E3"),sQuery(id+"F0.wireOp",EDGE,"E4"),sQuery(id+"F0.wireOp",EDGE,"E5.0"),sQuery(id+"F0.wireOp",EDGE,"E5.1"),sQuery(id+"F0.wireOp",EDGE,"E5.3"),sQuery(id+"F0.wireOp",EDGE,"E5.4"),sQuery(id+"F0.wireOp",EDGE,"E5.5"),sQuery(id+"F0.wireOp",EDGE,"E6.trimOffspring"),sQuery(id+"F0.wireOp",EDGE,"E7.trimOffspring"),sQuery(id+"F0.wireOp",EDGE,"E9.trimOffspring"),sQuery(id+"F0.wireOp",EDGE,"E10.1.0"),sQuery(id+"F0.wireOp",EDGE,"E10.1.1"),sQuery(id+"F0.wireOp",EDGE,"E10.1.2"),sQuery(id+"F0.wireOp",EDGE,"E10.1.3"),sQuery(id+"F0.wireOp",EDGE,"E10.1.5"),sQuery(id+"F0.wireOp",EDGE,"E10.1.7"),sQuery(id+"F0.wireOp",EDGE,"E10.1.8"),sQuery(id+"F0.wireOp",EDGE,"E10.1.9"),sQuery(id+"F0.wireOp",EDGE,"E10.1.10"),sQuery(id+"F0.wireOp",EDGE,"E10.1.11"),sQuery(id+"F0.wireOp",EDGE,"E10.1.12"),sQuery(id+"F0.wireOp",EDGE,"E10.1.14"),sQuery(id+"F0.wireOp",EDGE,"E10.1.15"),sQuery(id+"F0.wireOp",EDGE,"E10.1.16"),sQuery(id+"F0.wireOp",EDGE,"E10.1.18"),sQuery(id+"F0.wireOp",EDGE,"E10.1.20"),sQuery(id+"F0.wireOp",EDGE,"E10.2.0"),sQuery(id+"F0.wireOp",EDGE,"E10.2.1"),sQuery(id+"F0.wireOp",EDGE,"E10.2.2"),sQuery(id+"F0.wireOp",EDGE,"E10.2.3"),sQuery(id+"F0.wireOp",EDGE,"E10.2.5"),sQuery(id+"F0.wireOp",EDGE,"E10.2.7"),sQuery(id+"F0.wireOp",EDGE,"E10.2.8"),sQuery(id+"F0.wireOp",EDGE,"E10.2.9"),sQuery(id+"F0.wireOp",EDGE,"E10.2.10"),sQuery(id+"F0.wireOp",EDGE,"E10.2.11"),sQuery(id+"F0.wireOp",EDGE,"E10.2.12"),sQuery(id+"F0.wireOp",EDGE,"E1"),sQuery(id+"F0.wireOp",EDGE,"E10.2.14"),sQuery(id+"F0.wireOp",EDGE,"E10.2.15"),sQuery(id+"F0.wireOp",EDGE,"E10.2.16"),sQuery(id+"F0.wireOp",EDGE,"E10.2.18"),sQuery(id+"F0.wireOp",EDGE,"E10.2.20"),sQuery(id+"F0.wireOp",EDGE,"E8.trimOffspring"),sQuery(id+"F0.wireOp",EDGE,"E0"),sQuery(id+"F0.wireOp",EDGE,"E10.1.6"),sQuery(id+"F0.wireOp",EDGE,"E11"),sQuery(id+"F0.wireOp",EDGE,"E12"),sQuery(id+"F0.wireOp",EDGE,"E13.1.0"),sQuery(id+"F0.wireOp",EDGE,"E13.1.1"),sQuery(id+"F0.wireOp",EDGE,"E13.2.0"),sQuery(id+"F0.wireOp",EDGE,"E13.2.1")])]}),"instanceName":"1"}),"instanceName":"1"}),"instanceName":"1"}),"instanceName":"1"});
            var Q1;
            Q1=makeQuery(id+"F39.opPattern","COPY",EDGE,{"derivedFrom":makeQuery(id+"F36.opPattern","COPY",EDGE,{"derivedFrom":makeQuery(id+"F23.opPattern","COPY",EDGE,{"derivedFrom":makeQuery(id+"F7.opPattern","COPY",EDGE,{"derivedFrom":makeQuery(id+"F1.opExtrude","CAP_EDGE",EDGE,{"disambiguationData":[OSD([sQuery(id+"F0.wireOp",EDGE,"E1")])],"isStart":false}),"instanceName":"1"}),"instanceName":"1"}),"instanceName":"1"}),"instanceName":"1"});
            transform(context, id + "F40", {"entities" : qUnion([Q0]), "transformType" : TransformType.ROTATION, "transformAxis" : qUnion([Q1]), "angle" : 10 * degree, "makeCopy" : false});
        }
        {
            var Q0;
            Q0=makeQuery(id+"F39.opPattern","COPY",BODY,{"derivedFrom":makeQuery(id+"F36.opPattern","COPY",BODY,{"derivedFrom":makeQuery(id+"F23.opPattern","COPY",BODY,{"derivedFrom":makeQuery(id+"F7.opPattern","COPY",BODY,{"derivedFrom":makeQuery(id+"F1.opExtrude","SWEPT_BODY",BODY,{"disambiguationData":[OSD([sQuery(id+"F0.wireOp",EDGE,"E2.0"),sQuery(id+"F0.wireOp",EDGE,"E2.1"),sQuery(id+"F0.wireOp",EDGE,"E2.2"),sQuery(id+"F0.wireOp",EDGE,"E2.3"),sQuery(id+"F0.wireOp",EDGE,"E2.4"),sQuery(id+"F0.wireOp",EDGE,"E2.5"),sQuery(id+"F0.wireOp",EDGE,"E3"),sQuery(id+"F0.wireOp",EDGE,"E4"),sQuery(id+"F0.wireOp",EDGE,"E5.0"),sQuery(id+"F0.wireOp",EDGE,"E5.1"),sQuery(id+"F0.wireOp",EDGE,"E5.3"),sQuery(id+"F0.wireOp",EDGE,"E5.4"),sQuery(id+"F0.wireOp",EDGE,"E5.5"),sQuery(id+"F0.wireOp",EDGE,"E6.trimOffspring"),sQuery(id+"F0.wireOp",EDGE,"E7.trimOffspring"),sQuery(id+"F0.wireOp",EDGE,"E9.trimOffspring"),sQuery(id+"F0.wireOp",EDGE,"E10.1.0"),sQuery(id+"F0.wireOp",EDGE,"E10.1.1"),sQuery(id+"F0.wireOp",EDGE,"E10.1.2"),sQuery(id+"F0.wireOp",EDGE,"E10.1.3"),sQuery(id+"F0.wireOp",EDGE,"E10.1.5"),sQuery(id+"F0.wireOp",EDGE,"E10.1.7"),sQuery(id+"F0.wireOp",EDGE,"E10.1.8"),sQuery(id+"F0.wireOp",EDGE,"E10.1.9"),sQuery(id+"F0.wireOp",EDGE,"E10.1.10"),sQuery(id+"F0.wireOp",EDGE,"E10.1.11"),sQuery(id+"F0.wireOp",EDGE,"E10.1.12"),sQuery(id+"F0.wireOp",EDGE,"E10.1.14"),sQuery(id+"F0.wireOp",EDGE,"E10.1.15"),sQuery(id+"F0.wireOp",EDGE,"E10.1.16"),sQuery(id+"F0.wireOp",EDGE,"E10.1.18"),sQuery(id+"F0.wireOp",EDGE,"E10.1.20"),sQuery(id+"F0.wireOp",EDGE,"E10.2.0"),sQuery(id+"F0.wireOp",EDGE,"E10.2.1"),sQuery(id+"F0.wireOp",EDGE,"E10.2.2"),sQuery(id+"F0.wireOp",EDGE,"E10.2.3"),sQuery(id+"F0.wireOp",EDGE,"E10.2.5"),sQuery(id+"F0.wireOp",EDGE,"E10.2.7"),sQuery(id+"F0.wireOp",EDGE,"E10.2.8"),sQuery(id+"F0.wireOp",EDGE,"E10.2.9"),sQuery(id+"F0.wireOp",EDGE,"E10.2.10"),sQuery(id+"F0.wireOp",EDGE,"E10.2.11"),sQuery(id+"F0.wireOp",EDGE,"E10.2.12"),sQuery(id+"F0.wireOp",EDGE,"E1"),sQuery(id+"F0.wireOp",EDGE,"E10.2.14"),sQuery(id+"F0.wireOp",EDGE,"E10.2.15"),sQuery(id+"F0.wireOp",EDGE,"E10.2.16"),sQuery(id+"F0.wireOp",EDGE,"E10.2.18"),sQuery(id+"F0.wireOp",EDGE,"E10.2.20"),sQuery(id+"F0.wireOp",EDGE,"E8.trimOffspring"),sQuery(id+"F0.wireOp",EDGE,"E0"),sQuery(id+"F0.wireOp",EDGE,"E10.1.6"),sQuery(id+"F0.wireOp",EDGE,"E11"),sQuery(id+"F0.wireOp",EDGE,"E12"),sQuery(id+"F0.wireOp",EDGE,"E13.1.0"),sQuery(id+"F0.wireOp",EDGE,"E13.1.1"),sQuery(id+"F0.wireOp",EDGE,"E13.2.0"),sQuery(id+"F0.wireOp",EDGE,"E13.2.1")])]}),"instanceName":"1"}),"instanceName":"1"}),"instanceName":"1"}),"instanceName":"1"});
            transform(context, id + "F41", {"entities" : qUnion([Q0]), "transformType" : TransformType.TRANSLATION_3D, "dx" : 0 * mm, "dy" : 1.1 * mm, "dz" : 0 * mm, "makeCopy" : false});
        }
        {
            var Q0;
            Q0=makeQuery(id+"F13.opPattern","COPY",BODY,{"derivedFrom":makeQuery(id+"F1.opExtrude","SWEPT_BODY",BODY,{"disambiguationData":[OSD([sQuery(id+"F0.wireOp",EDGE,"E2.0"),sQuery(id+"F0.wireOp",EDGE,"E2.1"),sQuery(id+"F0.wireOp",EDGE,"E2.2"),sQuery(id+"F0.wireOp",EDGE,"E2.3"),sQuery(id+"F0.wireOp",EDGE,"E2.4"),sQuery(id+"F0.wireOp",EDGE,"E2.5"),sQuery(id+"F0.wireOp",EDGE,"E3"),sQuery(id+"F0.wireOp",EDGE,"E4"),sQuery(id+"F0.wireOp",EDGE,"E5.0"),sQuery(id+"F0.wireOp",EDGE,"E5.1"),sQuery(id+"F0.wireOp",EDGE,"E5.3"),sQuery(id+"F0.wireOp",EDGE,"E5.4"),sQuery(id+"F0.wireOp",EDGE,"E5.5"),sQuery(id+"F0.wireOp",EDGE,"E6.trimOffspring"),sQuery(id+"F0.wireOp",EDGE,"E7.trimOffspring"),sQuery(id+"F0.wireOp",EDGE,"E9.trimOffspring"),sQuery(id+"F0.wireOp",EDGE,"E10.1.0"),sQuery(id+"F0.wireOp",EDGE,"E10.1.1"),sQuery(id+"F0.wireOp",EDGE,"E10.1.2"),sQuery(id+"F0.wireOp",EDGE,"E10.1.3"),sQuery(id+"F0.wireOp",EDGE,"E10.1.5"),sQuery(id+"F0.wireOp",EDGE,"E10.1.7"),sQuery(id+"F0.wireOp",EDGE,"E10.1.8"),sQuery(id+"F0.wireOp",EDGE,"E10.1.9"),sQuery(id+"F0.wireOp",EDGE,"E10.1.10"),sQuery(id+"F0.wireOp",EDGE,"E10.1.11"),sQuery(id+"F0.wireOp",EDGE,"E10.1.12"),sQuery(id+"F0.wireOp",EDGE,"E10.1.14"),sQuery(id+"F0.wireOp",EDGE,"E10.1.15"),sQuery(id+"F0.wireOp",EDGE,"E10.1.16"),sQuery(id+"F0.wireOp",EDGE,"E10.1.18"),sQuery(id+"F0.wireOp",EDGE,"E10.1.20"),sQuery(id+"F0.wireOp",EDGE,"E10.2.0"),sQuery(id+"F0.wireOp",EDGE,"E10.2.1"),sQuery(id+"F0.wireOp",EDGE,"E10.2.2"),sQuery(id+"F0.wireOp",EDGE,"E10.2.3"),sQuery(id+"F0.wireOp",EDGE,"E10.2.5"),sQuery(id+"F0.wireOp",EDGE,"E10.2.7"),sQuery(id+"F0.wireOp",EDGE,"E10.2.8"),sQuery(id+"F0.wireOp",EDGE,"E10.2.9"),sQuery(id+"F0.wireOp",EDGE,"E10.2.10"),sQuery(id+"F0.wireOp",EDGE,"E10.2.11"),sQuery(id+"F0.wireOp",EDGE,"E10.2.12"),sQuery(id+"F0.wireOp",EDGE,"E1"),sQuery(id+"F0.wireOp",EDGE,"E10.2.14"),sQuery(id+"F0.wireOp",EDGE,"E10.2.15"),sQuery(id+"F0.wireOp",EDGE,"E10.2.16"),sQuery(id+"F0.wireOp",EDGE,"E10.2.18"),sQuery(id+"F0.wireOp",EDGE,"E10.2.20"),sQuery(id+"F0.wireOp",EDGE,"E8.trimOffspring"),sQuery(id+"F0.wireOp",EDGE,"E0"),sQuery(id+"F0.wireOp",EDGE,"E10.1.6"),sQuery(id+"F0.wireOp",EDGE,"E11"),sQuery(id+"F0.wireOp",EDGE,"E12"),sQuery(id+"F0.wireOp",EDGE,"E13.1.0"),sQuery(id+"F0.wireOp",EDGE,"E13.1.1"),sQuery(id+"F0.wireOp",EDGE,"E13.2.0"),sQuery(id+"F0.wireOp",EDGE,"E13.2.1")])]}),"instanceName":"1"});
            transform(context, id + "F42", {"entities" : qUnion([Q0]), "transformType" : TransformType.TRANSLATION_3D, "dx" : 0 * mm, "dy" : -114 * mm, "dz" : 0 * mm, "makeCopy" : true});
        }
        {
            var Q0;
            Q0=makeQuery(id+"F42.opPattern","COPY",BODY,{"derivedFrom":makeQuery(id+"F13.opPattern","COPY",BODY,{"derivedFrom":makeQuery(id+"F1.opExtrude","SWEPT_BODY",BODY,{"disambiguationData":[OSD([sQuery(id+"F0.wireOp",EDGE,"E2.0"),sQuery(id+"F0.wireOp",EDGE,"E2.1"),sQuery(id+"F0.wireOp",EDGE,"E2.2"),sQuery(id+"F0.wireOp",EDGE,"E2.3"),sQuery(id+"F0.wireOp",EDGE,"E2.4"),sQuery(id+"F0.wireOp",EDGE,"E2.5"),sQuery(id+"F0.wireOp",EDGE,"E3"),sQuery(id+"F0.wireOp",EDGE,"E4"),sQuery(id+"F0.wireOp",EDGE,"E5.0"),sQuery(id+"F0.wireOp",EDGE,"E5.1"),sQuery(id+"F0.wireOp",EDGE,"E5.3"),sQuery(id+"F0.wireOp",EDGE,"E5.4"),sQuery(id+"F0.wireOp",EDGE,"E5.5"),sQuery(id+"F0.wireOp",EDGE,"E6.trimOffspring"),sQuery(id+"F0.wireOp",EDGE,"E7.trimOffspring"),sQuery(id+"F0.wireOp",EDGE,"E9.trimOffspring"),sQuery(id+"F0.wireOp",EDGE,"E10.1.0"),sQuery(id+"F0.wireOp",EDGE,"E10.1.1"),sQuery(id+"F0.wireOp",EDGE,"E10.1.2"),sQuery(id+"F0.wireOp",EDGE,"E10.1.3"),sQuery(id+"F0.wireOp",EDGE,"E10.1.5"),sQuery(id+"F0.wireOp",EDGE,"E10.1.7"),sQuery(id+"F0.wireOp",EDGE,"E10.1.8"),sQuery(id+"F0.wireOp",EDGE,"E10.1.9"),sQuery(id+"F0.wireOp",EDGE,"E10.1.10"),sQuery(id+"F0.wireOp",EDGE,"E10.1.11"),sQuery(id+"F0.wireOp",EDGE,"E10.1.12"),sQuery(id+"F0.wireOp",EDGE,"E10.1.14"),sQuery(id+"F0.wireOp",EDGE,"E10.1.15"),sQuery(id+"F0.wireOp",EDGE,"E10.1.16"),sQuery(id+"F0.wireOp",EDGE,"E10.1.18"),sQuery(id+"F0.wireOp",EDGE,"E10.1.20"),sQuery(id+"F0.wireOp",EDGE,"E10.2.0"),sQuery(id+"F0.wireOp",EDGE,"E10.2.1"),sQuery(id+"F0.wireOp",EDGE,"E10.2.2"),sQuery(id+"F0.wireOp",EDGE,"E10.2.3"),sQuery(id+"F0.wireOp",EDGE,"E10.2.5"),sQuery(id+"F0.wireOp",EDGE,"E10.2.7"),sQuery(id+"F0.wireOp",EDGE,"E10.2.8"),sQuery(id+"F0.wireOp",EDGE,"E10.2.9"),sQuery(id+"F0.wireOp",EDGE,"E10.2.10"),sQuery(id+"F0.wireOp",EDGE,"E10.2.11"),sQuery(id+"F0.wireOp",EDGE,"E10.2.12"),sQuery(id+"F0.wireOp",EDGE,"E1"),sQuery(id+"F0.wireOp",EDGE,"E10.2.14"),sQuery(id+"F0.wireOp",EDGE,"E10.2.15"),sQuery(id+"F0.wireOp",EDGE,"E10.2.16"),sQuery(id+"F0.wireOp",EDGE,"E10.2.18"),sQuery(id+"F0.wireOp",EDGE,"E10.2.20"),sQuery(id+"F0.wireOp",EDGE,"E8.trimOffspring"),sQuery(id+"F0.wireOp",EDGE,"E0"),sQuery(id+"F0.wireOp",EDGE,"E10.1.6"),sQuery(id+"F0.wireOp",EDGE,"E11"),sQuery(id+"F0.wireOp",EDGE,"E12"),sQuery(id+"F0.wireOp",EDGE,"E13.1.0"),sQuery(id+"F0.wireOp",EDGE,"E13.1.1"),sQuery(id+"F0.wireOp",EDGE,"E13.2.0"),sQuery(id+"F0.wireOp",EDGE,"E13.2.1")])]}),"instanceName":"1"}),"instanceName":"1"});
            var Q1;
            Q1=makeQuery(id+"F42.opPattern","COPY",EDGE,{"derivedFrom":makeQuery(id+"F13.opPattern","COPY",EDGE,{"derivedFrom":makeQuery(id+"F1.opExtrude","CAP_EDGE",EDGE,{"disambiguationData":[OSD([sQuery(id+"F0.wireOp",EDGE,"E1")])],"isStart":false}),"instanceName":"1"}),"instanceName":"1"});
            transform(context, id + "F43", {"entities" : qUnion([Q0]), "transformType" : TransformType.ROTATION, "transformAxis" : qUnion([Q1]), "angle" : 30 * degree, "makeCopy" : false});
        }
        {
            var Q0;
            Q0=makeQuery(id+"F42.opPattern","COPY",BODY,{"derivedFrom":makeQuery(id+"F13.opPattern","COPY",BODY,{"derivedFrom":makeQuery(id+"F1.opExtrude","SWEPT_BODY",BODY,{"disambiguationData":[OSD([sQuery(id+"F0.wireOp",EDGE,"E2.0"),sQuery(id+"F0.wireOp",EDGE,"E2.1"),sQuery(id+"F0.wireOp",EDGE,"E2.2"),sQuery(id+"F0.wireOp",EDGE,"E2.3"),sQuery(id+"F0.wireOp",EDGE,"E2.4"),sQuery(id+"F0.wireOp",EDGE,"E2.5"),sQuery(id+"F0.wireOp",EDGE,"E3"),sQuery(id+"F0.wireOp",EDGE,"E4"),sQuery(id+"F0.wireOp",EDGE,"E5.0"),sQuery(id+"F0.wireOp",EDGE,"E5.1"),sQuery(id+"F0.wireOp",EDGE,"E5.3"),sQuery(id+"F0.wireOp",EDGE,"E5.4"),sQuery(id+"F0.wireOp",EDGE,"E5.5"),sQuery(id+"F0.wireOp",EDGE,"E6.trimOffspring"),sQuery(id+"F0.wireOp",EDGE,"E7.trimOffspring"),sQuery(id+"F0.wireOp",EDGE,"E9.trimOffspring"),sQuery(id+"F0.wireOp",EDGE,"E10.1.0"),sQuery(id+"F0.wireOp",EDGE,"E10.1.1"),sQuery(id+"F0.wireOp",EDGE,"E10.1.2"),sQuery(id+"F0.wireOp",EDGE,"E10.1.3"),sQuery(id+"F0.wireOp",EDGE,"E10.1.5"),sQuery(id+"F0.wireOp",EDGE,"E10.1.7"),sQuery(id+"F0.wireOp",EDGE,"E10.1.8"),sQuery(id+"F0.wireOp",EDGE,"E10.1.9"),sQuery(id+"F0.wireOp",EDGE,"E10.1.10"),sQuery(id+"F0.wireOp",EDGE,"E10.1.11"),sQuery(id+"F0.wireOp",EDGE,"E10.1.12"),sQuery(id+"F0.wireOp",EDGE,"E10.1.14"),sQuery(id+"F0.wireOp",EDGE,"E10.1.15"),sQuery(id+"F0.wireOp",EDGE,"E10.1.16"),sQuery(id+"F0.wireOp",EDGE,"E10.1.18"),sQuery(id+"F0.wireOp",EDGE,"E10.1.20"),sQuery(id+"F0.wireOp",EDGE,"E10.2.0"),sQuery(id+"F0.wireOp",EDGE,"E10.2.1"),sQuery(id+"F0.wireOp",EDGE,"E10.2.2"),sQuery(id+"F0.wireOp",EDGE,"E10.2.3"),sQuery(id+"F0.wireOp",EDGE,"E10.2.5"),sQuery(id+"F0.wireOp",EDGE,"E10.2.7"),sQuery(id+"F0.wireOp",EDGE,"E10.2.8"),sQuery(id+"F0.wireOp",EDGE,"E10.2.9"),sQuery(id+"F0.wireOp",EDGE,"E10.2.10"),sQuery(id+"F0.wireOp",EDGE,"E10.2.11"),sQuery(id+"F0.wireOp",EDGE,"E10.2.12"),sQuery(id+"F0.wireOp",EDGE,"E1"),sQuery(id+"F0.wireOp",EDGE,"E10.2.14"),sQuery(id+"F0.wireOp",EDGE,"E10.2.15"),sQuery(id+"F0.wireOp",EDGE,"E10.2.16"),sQuery(id+"F0.wireOp",EDGE,"E10.2.18"),sQuery(id+"F0.wireOp",EDGE,"E10.2.20"),sQuery(id+"F0.wireOp",EDGE,"E8.trimOffspring"),sQuery(id+"F0.wireOp",EDGE,"E0"),sQuery(id+"F0.wireOp",EDGE,"E10.1.6"),sQuery(id+"F0.wireOp",EDGE,"E11"),sQuery(id+"F0.wireOp",EDGE,"E12"),sQuery(id+"F0.wireOp",EDGE,"E13.1.0"),sQuery(id+"F0.wireOp",EDGE,"E13.1.1"),sQuery(id+"F0.wireOp",EDGE,"E13.2.0"),sQuery(id+"F0.wireOp",EDGE,"E13.2.1")])]}),"instanceName":"1"}),"instanceName":"1"});
            transform(context, id + "F44", {"entities" : qUnion([Q0]), "transformType" : TransformType.TRANSLATION_3D, "dx" : 3.5 * mm, "dy" : -1 * mm, "dz" : 0 * mm, "makeCopy" : false});
        }
        {
            var Q0;
            Q0=makeQuery(id+"F5.opPattern","COPY",BODY,{"derivedFrom":makeQuery(id+"F1.opExtrude","SWEPT_BODY",BODY,{"disambiguationData":[OSD([sQuery(id+"F0.wireOp",EDGE,"E2.0"),sQuery(id+"F0.wireOp",EDGE,"E2.1"),sQuery(id+"F0.wireOp",EDGE,"E2.2"),sQuery(id+"F0.wireOp",EDGE,"E2.3"),sQuery(id+"F0.wireOp",EDGE,"E2.4"),sQuery(id+"F0.wireOp",EDGE,"E2.5"),sQuery(id+"F0.wireOp",EDGE,"E3"),sQuery(id+"F0.wireOp",EDGE,"E4"),sQuery(id+"F0.wireOp",EDGE,"E5.0"),sQuery(id+"F0.wireOp",EDGE,"E5.1"),sQuery(id+"F0.wireOp",EDGE,"E5.3"),sQuery(id+"F0.wireOp",EDGE,"E5.4"),sQuery(id+"F0.wireOp",EDGE,"E5.5"),sQuery(id+"F0.wireOp",EDGE,"E6.trimOffspring"),sQuery(id+"F0.wireOp",EDGE,"E7.trimOffspring"),sQuery(id+"F0.wireOp",EDGE,"E9.trimOffspring"),sQuery(id+"F0.wireOp",EDGE,"E10.1.0"),sQuery(id+"F0.wireOp",EDGE,"E10.1.1"),sQuery(id+"F0.wireOp",EDGE,"E10.1.2"),sQuery(id+"F0.wireOp",EDGE,"E10.1.3"),sQuery(id+"F0.wireOp",EDGE,"E10.1.5"),sQuery(id+"F0.wireOp",EDGE,"E10.1.7"),sQuery(id+"F0.wireOp",EDGE,"E10.1.8"),sQuery(id+"F0.wireOp",EDGE,"E10.1.9"),sQuery(id+"F0.wireOp",EDGE,"E10.1.10"),sQuery(id+"F0.wireOp",EDGE,"E10.1.11"),sQuery(id+"F0.wireOp",EDGE,"E10.1.12"),sQuery(id+"F0.wireOp",EDGE,"E10.1.14"),sQuery(id+"F0.wireOp",EDGE,"E10.1.15"),sQuery(id+"F0.wireOp",EDGE,"E10.1.16"),sQuery(id+"F0.wireOp",EDGE,"E10.1.18"),sQuery(id+"F0.wireOp",EDGE,"E10.1.20"),sQuery(id+"F0.wireOp",EDGE,"E10.2.0"),sQuery(id+"F0.wireOp",EDGE,"E10.2.1"),sQuery(id+"F0.wireOp",EDGE,"E10.2.2"),sQuery(id+"F0.wireOp",EDGE,"E10.2.3"),sQuery(id+"F0.wireOp",EDGE,"E10.2.5"),sQuery(id+"F0.wireOp",EDGE,"E10.2.7"),sQuery(id+"F0.wireOp",EDGE,"E10.2.8"),sQuery(id+"F0.wireOp",EDGE,"E10.2.9"),sQuery(id+"F0.wireOp",EDGE,"E10.2.10"),sQuery(id+"F0.wireOp",EDGE,"E10.2.11"),sQuery(id+"F0.wireOp",EDGE,"E10.2.12"),sQuery(id+"F0.wireOp",EDGE,"E1"),sQuery(id+"F0.wireOp",EDGE,"E10.2.14"),sQuery(id+"F0.wireOp",EDGE,"E10.2.15"),sQuery(id+"F0.wireOp",EDGE,"E10.2.16"),sQuery(id+"F0.wireOp",EDGE,"E10.2.18"),sQuery(id+"F0.wireOp",EDGE,"E10.2.20"),sQuery(id+"F0.wireOp",EDGE,"E8.trimOffspring"),sQuery(id+"F0.wireOp",EDGE,"E0"),sQuery(id+"F0.wireOp",EDGE,"E10.1.6"),sQuery(id+"F0.wireOp",EDGE,"E11"),sQuery(id+"F0.wireOp",EDGE,"E12"),sQuery(id+"F0.wireOp",EDGE,"E13.1.0"),sQuery(id+"F0.wireOp",EDGE,"E13.1.1"),sQuery(id+"F0.wireOp",EDGE,"E13.2.0"),sQuery(id+"F0.wireOp",EDGE,"E13.2.1")])]}),"instanceName":"1"});
            transform(context, id + "F45", {"entities" : qUnion([Q0]), "transformType" : TransformType.TRANSLATION_3D, "dx" : 32 * mm, "dy" : -173.8 * mm, "dz" : 0 * mm, "makeCopy" : true});
        }
        {
            var Q0;
            Q0=makeQuery(id+"F45.opPattern","COPY",BODY,{"derivedFrom":makeQuery(id+"F5.opPattern","COPY",BODY,{"derivedFrom":makeQuery(id+"F1.opExtrude","SWEPT_BODY",BODY,{"disambiguationData":[OSD([sQuery(id+"F0.wireOp",EDGE,"E2.0"),sQuery(id+"F0.wireOp",EDGE,"E2.1"),sQuery(id+"F0.wireOp",EDGE,"E2.2"),sQuery(id+"F0.wireOp",EDGE,"E2.3"),sQuery(id+"F0.wireOp",EDGE,"E2.4"),sQuery(id+"F0.wireOp",EDGE,"E2.5"),sQuery(id+"F0.wireOp",EDGE,"E3"),sQuery(id+"F0.wireOp",EDGE,"E4"),sQuery(id+"F0.wireOp",EDGE,"E5.0"),sQuery(id+"F0.wireOp",EDGE,"E5.1"),sQuery(id+"F0.wireOp",EDGE,"E5.3"),sQuery(id+"F0.wireOp",EDGE,"E5.4"),sQuery(id+"F0.wireOp",EDGE,"E5.5"),sQuery(id+"F0.wireOp",EDGE,"E6.trimOffspring"),sQuery(id+"F0.wireOp",EDGE,"E7.trimOffspring"),sQuery(id+"F0.wireOp",EDGE,"E9.trimOffspring"),sQuery(id+"F0.wireOp",EDGE,"E10.1.0"),sQuery(id+"F0.wireOp",EDGE,"E10.1.1"),sQuery(id+"F0.wireOp",EDGE,"E10.1.2"),sQuery(id+"F0.wireOp",EDGE,"E10.1.3"),sQuery(id+"F0.wireOp",EDGE,"E10.1.5"),sQuery(id+"F0.wireOp",EDGE,"E10.1.7"),sQuery(id+"F0.wireOp",EDGE,"E10.1.8"),sQuery(id+"F0.wireOp",EDGE,"E10.1.9"),sQuery(id+"F0.wireOp",EDGE,"E10.1.10"),sQuery(id+"F0.wireOp",EDGE,"E10.1.11"),sQuery(id+"F0.wireOp",EDGE,"E10.1.12"),sQuery(id+"F0.wireOp",EDGE,"E10.1.14"),sQuery(id+"F0.wireOp",EDGE,"E10.1.15"),sQuery(id+"F0.wireOp",EDGE,"E10.1.16"),sQuery(id+"F0.wireOp",EDGE,"E10.1.18"),sQuery(id+"F0.wireOp",EDGE,"E10.1.20"),sQuery(id+"F0.wireOp",EDGE,"E10.2.0"),sQuery(id+"F0.wireOp",EDGE,"E10.2.1"),sQuery(id+"F0.wireOp",EDGE,"E10.2.2"),sQuery(id+"F0.wireOp",EDGE,"E10.2.3"),sQuery(id+"F0.wireOp",EDGE,"E10.2.5"),sQuery(id+"F0.wireOp",EDGE,"E10.2.7"),sQuery(id+"F0.wireOp",EDGE,"E10.2.8"),sQuery(id+"F0.wireOp",EDGE,"E10.2.9"),sQuery(id+"F0.wireOp",EDGE,"E10.2.10"),sQuery(id+"F0.wireOp",EDGE,"E10.2.11"),sQuery(id+"F0.wireOp",EDGE,"E10.2.12"),sQuery(id+"F0.wireOp",EDGE,"E1"),sQuery(id+"F0.wireOp",EDGE,"E10.2.14"),sQuery(id+"F0.wireOp",EDGE,"E10.2.15"),sQuery(id+"F0.wireOp",EDGE,"E10.2.16"),sQuery(id+"F0.wireOp",EDGE,"E10.2.18"),sQuery(id+"F0.wireOp",EDGE,"E10.2.20"),sQuery(id+"F0.wireOp",EDGE,"E8.trimOffspring"),sQuery(id+"F0.wireOp",EDGE,"E0"),sQuery(id+"F0.wireOp",EDGE,"E10.1.6"),sQuery(id+"F0.wireOp",EDGE,"E11"),sQuery(id+"F0.wireOp",EDGE,"E12"),sQuery(id+"F0.wireOp",EDGE,"E13.1.0"),sQuery(id+"F0.wireOp",EDGE,"E13.1.1"),sQuery(id+"F0.wireOp",EDGE,"E13.2.0"),sQuery(id+"F0.wireOp",EDGE,"E13.2.1")])]}),"instanceName":"1"}),"instanceName":"1"});
            transform(context, id + "F46", {"entities" : qUnion([Q0]), "transformType" : TransformType.TRANSLATION_3D, "dx" : 68.8 * mm, "dy" : 0 * mm, "dz" : 0 * mm, "makeCopy" : true});
        }
        {
            var Q0;
            Q0=makeQuery(id+"F42.opPattern","COPY",BODY,{"derivedFrom":makeQuery(id+"F13.opPattern","COPY",BODY,{"derivedFrom":makeQuery(id+"F1.opExtrude","SWEPT_BODY",BODY,{"disambiguationData":[OSD([sQuery(id+"F0.wireOp",EDGE,"E2.0"),sQuery(id+"F0.wireOp",EDGE,"E2.1"),sQuery(id+"F0.wireOp",EDGE,"E2.2"),sQuery(id+"F0.wireOp",EDGE,"E2.3"),sQuery(id+"F0.wireOp",EDGE,"E2.4"),sQuery(id+"F0.wireOp",EDGE,"E2.5"),sQuery(id+"F0.wireOp",EDGE,"E3"),sQuery(id+"F0.wireOp",EDGE,"E4"),sQuery(id+"F0.wireOp",EDGE,"E5.0"),sQuery(id+"F0.wireOp",EDGE,"E5.1"),sQuery(id+"F0.wireOp",EDGE,"E5.3"),sQuery(id+"F0.wireOp",EDGE,"E5.4"),sQuery(id+"F0.wireOp",EDGE,"E5.5"),sQuery(id+"F0.wireOp",EDGE,"E6.trimOffspring"),sQuery(id+"F0.wireOp",EDGE,"E7.trimOffspring"),sQuery(id+"F0.wireOp",EDGE,"E9.trimOffspring"),sQuery(id+"F0.wireOp",EDGE,"E10.1.0"),sQuery(id+"F0.wireOp",EDGE,"E10.1.1"),sQuery(id+"F0.wireOp",EDGE,"E10.1.2"),sQuery(id+"F0.wireOp",EDGE,"E10.1.3"),sQuery(id+"F0.wireOp",EDGE,"E10.1.5"),sQuery(id+"F0.wireOp",EDGE,"E10.1.7"),sQuery(id+"F0.wireOp",EDGE,"E10.1.8"),sQuery(id+"F0.wireOp",EDGE,"E10.1.9"),sQuery(id+"F0.wireOp",EDGE,"E10.1.10"),sQuery(id+"F0.wireOp",EDGE,"E10.1.11"),sQuery(id+"F0.wireOp",EDGE,"E10.1.12"),sQuery(id+"F0.wireOp",EDGE,"E10.1.14"),sQuery(id+"F0.wireOp",EDGE,"E10.1.15"),sQuery(id+"F0.wireOp",EDGE,"E10.1.16"),sQuery(id+"F0.wireOp",EDGE,"E10.1.18"),sQuery(id+"F0.wireOp",EDGE,"E10.1.20"),sQuery(id+"F0.wireOp",EDGE,"E10.2.0"),sQuery(id+"F0.wireOp",EDGE,"E10.2.1"),sQuery(id+"F0.wireOp",EDGE,"E10.2.2"),sQuery(id+"F0.wireOp",EDGE,"E10.2.3"),sQuery(id+"F0.wireOp",EDGE,"E10.2.5"),sQuery(id+"F0.wireOp",EDGE,"E10.2.7"),sQuery(id+"F0.wireOp",EDGE,"E10.2.8"),sQuery(id+"F0.wireOp",EDGE,"E10.2.9"),sQuery(id+"F0.wireOp",EDGE,"E10.2.10"),sQuery(id+"F0.wireOp",EDGE,"E10.2.11"),sQuery(id+"F0.wireOp",EDGE,"E10.2.12"),sQuery(id+"F0.wireOp",EDGE,"E1"),sQuery(id+"F0.wireOp",EDGE,"E10.2.14"),sQuery(id+"F0.wireOp",EDGE,"E10.2.15"),sQuery(id+"F0.wireOp",EDGE,"E10.2.16"),sQuery(id+"F0.wireOp",EDGE,"E10.2.18"),sQuery(id+"F0.wireOp",EDGE,"E10.2.20"),sQuery(id+"F0.wireOp",EDGE,"E8.trimOffspring"),sQuery(id+"F0.wireOp",EDGE,"E0"),sQuery(id+"F0.wireOp",EDGE,"E10.1.6"),sQuery(id+"F0.wireOp",EDGE,"E11"),sQuery(id+"F0.wireOp",EDGE,"E12"),sQuery(id+"F0.wireOp",EDGE,"E13.1.0"),sQuery(id+"F0.wireOp",EDGE,"E13.1.1"),sQuery(id+"F0.wireOp",EDGE,"E13.2.0"),sQuery(id+"F0.wireOp",EDGE,"E13.2.1")])]}),"instanceName":"1"}),"instanceName":"1"});
            transform(context, id + "F47", {"entities" : qUnion([Q0]), "transformType" : TransformType.TRANSLATION_3D, "dx" : 199 * mm, "dy" : -23.5 * mm, "dz" : 0 * mm, "makeCopy" : true});
        }
        {
            var Q0;
            Q0=makeQuery(id+"F39.opPattern","COPY",BODY,{"derivedFrom":makeQuery(id+"F36.opPattern","COPY",BODY,{"derivedFrom":makeQuery(id+"F23.opPattern","COPY",BODY,{"derivedFrom":makeQuery(id+"F7.opPattern","COPY",BODY,{"derivedFrom":makeQuery(id+"F1.opExtrude","SWEPT_BODY",BODY,{"disambiguationData":[OSD([sQuery(id+"F0.wireOp",EDGE,"E2.0"),sQuery(id+"F0.wireOp",EDGE,"E2.1"),sQuery(id+"F0.wireOp",EDGE,"E2.2"),sQuery(id+"F0.wireOp",EDGE,"E2.3"),sQuery(id+"F0.wireOp",EDGE,"E2.4"),sQuery(id+"F0.wireOp",EDGE,"E2.5"),sQuery(id+"F0.wireOp",EDGE,"E3"),sQuery(id+"F0.wireOp",EDGE,"E4"),sQuery(id+"F0.wireOp",EDGE,"E5.0"),sQuery(id+"F0.wireOp",EDGE,"E5.1"),sQuery(id+"F0.wireOp",EDGE,"E5.3"),sQuery(id+"F0.wireOp",EDGE,"E5.4"),sQuery(id+"F0.wireOp",EDGE,"E5.5"),sQuery(id+"F0.wireOp",EDGE,"E6.trimOffspring"),sQuery(id+"F0.wireOp",EDGE,"E7.trimOffspring"),sQuery(id+"F0.wireOp",EDGE,"E9.trimOffspring"),sQuery(id+"F0.wireOp",EDGE,"E10.1.0"),sQuery(id+"F0.wireOp",EDGE,"E10.1.1"),sQuery(id+"F0.wireOp",EDGE,"E10.1.2"),sQuery(id+"F0.wireOp",EDGE,"E10.1.3"),sQuery(id+"F0.wireOp",EDGE,"E10.1.5"),sQuery(id+"F0.wireOp",EDGE,"E10.1.7"),sQuery(id+"F0.wireOp",EDGE,"E10.1.8"),sQuery(id+"F0.wireOp",EDGE,"E10.1.9"),sQuery(id+"F0.wireOp",EDGE,"E10.1.10"),sQuery(id+"F0.wireOp",EDGE,"E10.1.11"),sQuery(id+"F0.wireOp",EDGE,"E10.1.12"),sQuery(id+"F0.wireOp",EDGE,"E10.1.14"),sQuery(id+"F0.wireOp",EDGE,"E10.1.15"),sQuery(id+"F0.wireOp",EDGE,"E10.1.16"),sQuery(id+"F0.wireOp",EDGE,"E10.1.18"),sQuery(id+"F0.wireOp",EDGE,"E10.1.20"),sQuery(id+"F0.wireOp",EDGE,"E10.2.0"),sQuery(id+"F0.wireOp",EDGE,"E10.2.1"),sQuery(id+"F0.wireOp",EDGE,"E10.2.2"),sQuery(id+"F0.wireOp",EDGE,"E10.2.3"),sQuery(id+"F0.wireOp",EDGE,"E10.2.5"),sQuery(id+"F0.wireOp",EDGE,"E10.2.7"),sQuery(id+"F0.wireOp",EDGE,"E10.2.8"),sQuery(id+"F0.wireOp",EDGE,"E10.2.9"),sQuery(id+"F0.wireOp",EDGE,"E10.2.10"),sQuery(id+"F0.wireOp",EDGE,"E10.2.11"),sQuery(id+"F0.wireOp",EDGE,"E10.2.12"),sQuery(id+"F0.wireOp",EDGE,"E1"),sQuery(id+"F0.wireOp",EDGE,"E10.2.14"),sQuery(id+"F0.wireOp",EDGE,"E10.2.15"),sQuery(id+"F0.wireOp",EDGE,"E10.2.16"),sQuery(id+"F0.wireOp",EDGE,"E10.2.18"),sQuery(id+"F0.wireOp",EDGE,"E10.2.20"),sQuery(id+"F0.wireOp",EDGE,"E8.trimOffspring"),sQuery(id+"F0.wireOp",EDGE,"E0"),sQuery(id+"F0.wireOp",EDGE,"E10.1.6"),sQuery(id+"F0.wireOp",EDGE,"E11"),sQuery(id+"F0.wireOp",EDGE,"E12"),sQuery(id+"F0.wireOp",EDGE,"E13.1.0"),sQuery(id+"F0.wireOp",EDGE,"E13.1.1"),sQuery(id+"F0.wireOp",EDGE,"E13.2.0"),sQuery(id+"F0.wireOp",EDGE,"E13.2.1")])]}),"instanceName":"1"}),"instanceName":"1"}),"instanceName":"1"}),"instanceName":"1"});
            transform(context, id + "F48", {"entities" : qUnion([Q0]), "transformType" : TransformType.TRANSLATION_3D, "dx" : 52.9 * mm, "dy" : -47.6 * mm, "dz" : 0 * mm, "makeCopy" : true});
        }
        {
            var Q0;
            Q0=makeQuery(id+"F48.opPattern","COPY",BODY,{"derivedFrom":makeQuery(id+"F39.opPattern","COPY",BODY,{"derivedFrom":makeQuery(id+"F36.opPattern","COPY",BODY,{"derivedFrom":makeQuery(id+"F23.opPattern","COPY",BODY,{"derivedFrom":makeQuery(id+"F7.opPattern","COPY",BODY,{"derivedFrom":makeQuery(id+"F1.opExtrude","SWEPT_BODY",BODY,{"disambiguationData":[OSD([sQuery(id+"F0.wireOp",EDGE,"E2.0"),sQuery(id+"F0.wireOp",EDGE,"E2.1"),sQuery(id+"F0.wireOp",EDGE,"E2.2"),sQuery(id+"F0.wireOp",EDGE,"E2.3"),sQuery(id+"F0.wireOp",EDGE,"E2.4"),sQuery(id+"F0.wireOp",EDGE,"E2.5"),sQuery(id+"F0.wireOp",EDGE,"E3"),sQuery(id+"F0.wireOp",EDGE,"E4"),sQuery(id+"F0.wireOp",EDGE,"E5.0"),sQuery(id+"F0.wireOp",EDGE,"E5.1"),sQuery(id+"F0.wireOp",EDGE,"E5.3"),sQuery(id+"F0.wireOp",EDGE,"E5.4"),sQuery(id+"F0.wireOp",EDGE,"E5.5"),sQuery(id+"F0.wireOp",EDGE,"E6.trimOffspring"),sQuery(id+"F0.wireOp",EDGE,"E7.trimOffspring"),sQuery(id+"F0.wireOp",EDGE,"E9.trimOffspring"),sQuery(id+"F0.wireOp",EDGE,"E10.1.0"),sQuery(id+"F0.wireOp",EDGE,"E10.1.1"),sQuery(id+"F0.wireOp",EDGE,"E10.1.2"),sQuery(id+"F0.wireOp",EDGE,"E10.1.3"),sQuery(id+"F0.wireOp",EDGE,"E10.1.5"),sQuery(id+"F0.wireOp",EDGE,"E10.1.7"),sQuery(id+"F0.wireOp",EDGE,"E10.1.8"),sQuery(id+"F0.wireOp",EDGE,"E10.1.9"),sQuery(id+"F0.wireOp",EDGE,"E10.1.10"),sQuery(id+"F0.wireOp",EDGE,"E10.1.11"),sQuery(id+"F0.wireOp",EDGE,"E10.1.12"),sQuery(id+"F0.wireOp",EDGE,"E10.1.14"),sQuery(id+"F0.wireOp",EDGE,"E10.1.15"),sQuery(id+"F0.wireOp",EDGE,"E10.1.16"),sQuery(id+"F0.wireOp",EDGE,"E10.1.18"),sQuery(id+"F0.wireOp",EDGE,"E10.1.20"),sQuery(id+"F0.wireOp",EDGE,"E10.2.0"),sQuery(id+"F0.wireOp",EDGE,"E10.2.1"),sQuery(id+"F0.wireOp",EDGE,"E10.2.2"),sQuery(id+"F0.wireOp",EDGE,"E10.2.3"),sQuery(id+"F0.wireOp",EDGE,"E10.2.5"),sQuery(id+"F0.wireOp",EDGE,"E10.2.7"),sQuery(id+"F0.wireOp",EDGE,"E10.2.8"),sQuery(id+"F0.wireOp",EDGE,"E10.2.9"),sQuery(id+"F0.wireOp",EDGE,"E10.2.10"),sQuery(id+"F0.wireOp",EDGE,"E10.2.11"),sQuery(id+"F0.wireOp",EDGE,"E10.2.12"),sQuery(id+"F0.wireOp",EDGE,"E1"),sQuery(id+"F0.wireOp",EDGE,"E10.2.14"),sQuery(id+"F0.wireOp",EDGE,"E10.2.15"),sQuery(id+"F0.wireOp",EDGE,"E10.2.16"),sQuery(id+"F0.wireOp",EDGE,"E10.2.18"),sQuery(id+"F0.wireOp",EDGE,"E10.2.20"),sQuery(id+"F0.wireOp",EDGE,"E8.trimOffspring"),sQuery(id+"F0.wireOp",EDGE,"E0"),sQuery(id+"F0.wireOp",EDGE,"E10.1.6"),sQuery(id+"F0.wireOp",EDGE,"E11"),sQuery(id+"F0.wireOp",EDGE,"E12"),sQuery(id+"F0.wireOp",EDGE,"E13.1.0"),sQuery(id+"F0.wireOp",EDGE,"E13.1.1"),sQuery(id+"F0.wireOp",EDGE,"E13.2.0"),sQuery(id+"F0.wireOp",EDGE,"E13.2.1")])]}),"instanceName":"1"}),"instanceName":"1"}),"instanceName":"1"}),"instanceName":"1"}),"instanceName":"1"});
            var Q1;
            Q1=makeQuery(id+"F48.opPattern","COPY",EDGE,{"derivedFrom":makeQuery(id+"F39.opPattern","COPY",EDGE,{"derivedFrom":makeQuery(id+"F36.opPattern","COPY",EDGE,{"derivedFrom":makeQuery(id+"F23.opPattern","COPY",EDGE,{"derivedFrom":makeQuery(id+"F7.opPattern","COPY",EDGE,{"derivedFrom":makeQuery(id+"F1.opExtrude","CAP_EDGE",EDGE,{"disambiguationData":[OSD([sQuery(id+"F0.wireOp",EDGE,"E1")])],"isStart":false}),"instanceName":"1"}),"instanceName":"1"}),"instanceName":"1"}),"instanceName":"1"}),"instanceName":"1"});
            transform(context, id + "F49", {"entities" : qUnion([Q0]), "transformType" : TransformType.ROTATION, "transformAxis" : qUnion([Q1]), "angle" : 70 * degree, "makeCopy" : false});
        }
        {
            var Q0;
            Q0=makeQuery(id+"F48.opPattern","COPY",BODY,{"derivedFrom":makeQuery(id+"F39.opPattern","COPY",BODY,{"derivedFrom":makeQuery(id+"F36.opPattern","COPY",BODY,{"derivedFrom":makeQuery(id+"F23.opPattern","COPY",BODY,{"derivedFrom":makeQuery(id+"F7.opPattern","COPY",BODY,{"derivedFrom":makeQuery(id+"F1.opExtrude","SWEPT_BODY",BODY,{"disambiguationData":[OSD([sQuery(id+"F0.wireOp",EDGE,"E2.0"),sQuery(id+"F0.wireOp",EDGE,"E2.1"),sQuery(id+"F0.wireOp",EDGE,"E2.2"),sQuery(id+"F0.wireOp",EDGE,"E2.3"),sQuery(id+"F0.wireOp",EDGE,"E2.4"),sQuery(id+"F0.wireOp",EDGE,"E2.5"),sQuery(id+"F0.wireOp",EDGE,"E3"),sQuery(id+"F0.wireOp",EDGE,"E4"),sQuery(id+"F0.wireOp",EDGE,"E5.0"),sQuery(id+"F0.wireOp",EDGE,"E5.1"),sQuery(id+"F0.wireOp",EDGE,"E5.3"),sQuery(id+"F0.wireOp",EDGE,"E5.4"),sQuery(id+"F0.wireOp",EDGE,"E5.5"),sQuery(id+"F0.wireOp",EDGE,"E6.trimOffspring"),sQuery(id+"F0.wireOp",EDGE,"E7.trimOffspring"),sQuery(id+"F0.wireOp",EDGE,"E9.trimOffspring"),sQuery(id+"F0.wireOp",EDGE,"E10.1.0"),sQuery(id+"F0.wireOp",EDGE,"E10.1.1"),sQuery(id+"F0.wireOp",EDGE,"E10.1.2"),sQuery(id+"F0.wireOp",EDGE,"E10.1.3"),sQuery(id+"F0.wireOp",EDGE,"E10.1.5"),sQuery(id+"F0.wireOp",EDGE,"E10.1.7"),sQuery(id+"F0.wireOp",EDGE,"E10.1.8"),sQuery(id+"F0.wireOp",EDGE,"E10.1.9"),sQuery(id+"F0.wireOp",EDGE,"E10.1.10"),sQuery(id+"F0.wireOp",EDGE,"E10.1.11"),sQuery(id+"F0.wireOp",EDGE,"E10.1.12"),sQuery(id+"F0.wireOp",EDGE,"E10.1.14"),sQuery(id+"F0.wireOp",EDGE,"E10.1.15"),sQuery(id+"F0.wireOp",EDGE,"E10.1.16"),sQuery(id+"F0.wireOp",EDGE,"E10.1.18"),sQuery(id+"F0.wireOp",EDGE,"E10.1.20"),sQuery(id+"F0.wireOp",EDGE,"E10.2.0"),sQuery(id+"F0.wireOp",EDGE,"E10.2.1"),sQuery(id+"F0.wireOp",EDGE,"E10.2.2"),sQuery(id+"F0.wireOp",EDGE,"E10.2.3"),sQuery(id+"F0.wireOp",EDGE,"E10.2.5"),sQuery(id+"F0.wireOp",EDGE,"E10.2.7"),sQuery(id+"F0.wireOp",EDGE,"E10.2.8"),sQuery(id+"F0.wireOp",EDGE,"E10.2.9"),sQuery(id+"F0.wireOp",EDGE,"E10.2.10"),sQuery(id+"F0.wireOp",EDGE,"E10.2.11"),sQuery(id+"F0.wireOp",EDGE,"E10.2.12"),sQuery(id+"F0.wireOp",EDGE,"E1"),sQuery(id+"F0.wireOp",EDGE,"E10.2.14"),sQuery(id+"F0.wireOp",EDGE,"E10.2.15"),sQuery(id+"F0.wireOp",EDGE,"E10.2.16"),sQuery(id+"F0.wireOp",EDGE,"E10.2.18"),sQuery(id+"F0.wireOp",EDGE,"E10.2.20"),sQuery(id+"F0.wireOp",EDGE,"E8.trimOffspring"),sQuery(id+"F0.wireOp",EDGE,"E0"),sQuery(id+"F0.wireOp",EDGE,"E10.1.6"),sQuery(id+"F0.wireOp",EDGE,"E11"),sQuery(id+"F0.wireOp",EDGE,"E12"),sQuery(id+"F0.wireOp",EDGE,"E13.1.0"),sQuery(id+"F0.wireOp",EDGE,"E13.1.1"),sQuery(id+"F0.wireOp",EDGE,"E13.2.0"),sQuery(id+"F0.wireOp",EDGE,"E13.2.1")])]}),"instanceName":"1"}),"instanceName":"1"}),"instanceName":"1"}),"instanceName":"1"}),"instanceName":"1"});
            transform(context, id + "F50", {"entities" : qUnion([Q0]), "transformType" : TransformType.TRANSLATION_3D, "dx" : 9.2 * mm, "dy" : 0 * mm, "dz" : 0 * mm, "makeCopy" : false});
        }
        {
            var Q0;
            Q0=makeQuery(id+"F39.opPattern","COPY",BODY,{"derivedFrom":makeQuery(id+"F36.opPattern","COPY",BODY,{"derivedFrom":makeQuery(id+"F23.opPattern","COPY",BODY,{"derivedFrom":makeQuery(id+"F7.opPattern","COPY",BODY,{"derivedFrom":makeQuery(id+"F1.opExtrude","SWEPT_BODY",BODY,{"disambiguationData":[OSD([sQuery(id+"F0.wireOp",EDGE,"E2.0"),sQuery(id+"F0.wireOp",EDGE,"E2.1"),sQuery(id+"F0.wireOp",EDGE,"E2.2"),sQuery(id+"F0.wireOp",EDGE,"E2.3"),sQuery(id+"F0.wireOp",EDGE,"E2.4"),sQuery(id+"F0.wireOp",EDGE,"E2.5"),sQuery(id+"F0.wireOp",EDGE,"E3"),sQuery(id+"F0.wireOp",EDGE,"E4"),sQuery(id+"F0.wireOp",EDGE,"E5.0"),sQuery(id+"F0.wireOp",EDGE,"E5.1"),sQuery(id+"F0.wireOp",EDGE,"E5.3"),sQuery(id+"F0.wireOp",EDGE,"E5.4"),sQuery(id+"F0.wireOp",EDGE,"E5.5"),sQuery(id+"F0.wireOp",EDGE,"E6.trimOffspring"),sQuery(id+"F0.wireOp",EDGE,"E7.trimOffspring"),sQuery(id+"F0.wireOp",EDGE,"E9.trimOffspring"),sQuery(id+"F0.wireOp",EDGE,"E10.1.0"),sQuery(id+"F0.wireOp",EDGE,"E10.1.1"),sQuery(id+"F0.wireOp",EDGE,"E10.1.2"),sQuery(id+"F0.wireOp",EDGE,"E10.1.3"),sQuery(id+"F0.wireOp",EDGE,"E10.1.5"),sQuery(id+"F0.wireOp",EDGE,"E10.1.7"),sQuery(id+"F0.wireOp",EDGE,"E10.1.8"),sQuery(id+"F0.wireOp",EDGE,"E10.1.9"),sQuery(id+"F0.wireOp",EDGE,"E10.1.10"),sQuery(id+"F0.wireOp",EDGE,"E10.1.11"),sQuery(id+"F0.wireOp",EDGE,"E10.1.12"),sQuery(id+"F0.wireOp",EDGE,"E10.1.14"),sQuery(id+"F0.wireOp",EDGE,"E10.1.15"),sQuery(id+"F0.wireOp",EDGE,"E10.1.16"),sQuery(id+"F0.wireOp",EDGE,"E10.1.18"),sQuery(id+"F0.wireOp",EDGE,"E10.1.20"),sQuery(id+"F0.wireOp",EDGE,"E10.2.0"),sQuery(id+"F0.wireOp",EDGE,"E10.2.1"),sQuery(id+"F0.wireOp",EDGE,"E10.2.2"),sQuery(id+"F0.wireOp",EDGE,"E10.2.3"),sQuery(id+"F0.wireOp",EDGE,"E10.2.5"),sQuery(id+"F0.wireOp",EDGE,"E10.2.7"),sQuery(id+"F0.wireOp",EDGE,"E10.2.8"),sQuery(id+"F0.wireOp",EDGE,"E10.2.9"),sQuery(id+"F0.wireOp",EDGE,"E10.2.10"),sQuery(id+"F0.wireOp",EDGE,"E10.2.11"),sQuery(id+"F0.wireOp",EDGE,"E10.2.12"),sQuery(id+"F0.wireOp",EDGE,"E1"),sQuery(id+"F0.wireOp",EDGE,"E10.2.14"),sQuery(id+"F0.wireOp",EDGE,"E10.2.15"),sQuery(id+"F0.wireOp",EDGE,"E10.2.16"),sQuery(id+"F0.wireOp",EDGE,"E10.2.18"),sQuery(id+"F0.wireOp",EDGE,"E10.2.20"),sQuery(id+"F0.wireOp",EDGE,"E8.trimOffspring"),sQuery(id+"F0.wireOp",EDGE,"E0"),sQuery(id+"F0.wireOp",EDGE,"E10.1.6"),sQuery(id+"F0.wireOp",EDGE,"E11"),sQuery(id+"F0.wireOp",EDGE,"E12"),sQuery(id+"F0.wireOp",EDGE,"E13.1.0"),sQuery(id+"F0.wireOp",EDGE,"E13.1.1"),sQuery(id+"F0.wireOp",EDGE,"E13.2.0"),sQuery(id+"F0.wireOp",EDGE,"E13.2.1")])]}),"instanceName":"1"}),"instanceName":"1"}),"instanceName":"1"}),"instanceName":"1"});
            transform(context, id + "F51", {"entities" : qUnion([Q0]), "transformType" : TransformType.TRANSLATION_3D, "dx" : 14.9 * mm, "dy" : -87 * mm, "dz" : 0 * mm, "makeCopy" : true});
        }
        {
            var Q0;
            Q0=makeQuery(id+"F39.opPattern","COPY",BODY,{"derivedFrom":makeQuery(id+"F36.opPattern","COPY",BODY,{"derivedFrom":makeQuery(id+"F23.opPattern","COPY",BODY,{"derivedFrom":makeQuery(id+"F7.opPattern","COPY",BODY,{"derivedFrom":makeQuery(id+"F1.opExtrude","SWEPT_BODY",BODY,{"disambiguationData":[OSD([sQuery(id+"F0.wireOp",EDGE,"E2.0"),sQuery(id+"F0.wireOp",EDGE,"E2.1"),sQuery(id+"F0.wireOp",EDGE,"E2.2"),sQuery(id+"F0.wireOp",EDGE,"E2.3"),sQuery(id+"F0.wireOp",EDGE,"E2.4"),sQuery(id+"F0.wireOp",EDGE,"E2.5"),sQuery(id+"F0.wireOp",EDGE,"E3"),sQuery(id+"F0.wireOp",EDGE,"E4"),sQuery(id+"F0.wireOp",EDGE,"E5.0"),sQuery(id+"F0.wireOp",EDGE,"E5.1"),sQuery(id+"F0.wireOp",EDGE,"E5.3"),sQuery(id+"F0.wireOp",EDGE,"E5.4"),sQuery(id+"F0.wireOp",EDGE,"E5.5"),sQuery(id+"F0.wireOp",EDGE,"E6.trimOffspring"),sQuery(id+"F0.wireOp",EDGE,"E7.trimOffspring"),sQuery(id+"F0.wireOp",EDGE,"E9.trimOffspring"),sQuery(id+"F0.wireOp",EDGE,"E10.1.0"),sQuery(id+"F0.wireOp",EDGE,"E10.1.1"),sQuery(id+"F0.wireOp",EDGE,"E10.1.2"),sQuery(id+"F0.wireOp",EDGE,"E10.1.3"),sQuery(id+"F0.wireOp",EDGE,"E10.1.5"),sQuery(id+"F0.wireOp",EDGE,"E10.1.7"),sQuery(id+"F0.wireOp",EDGE,"E10.1.8"),sQuery(id+"F0.wireOp",EDGE,"E10.1.9"),sQuery(id+"F0.wireOp",EDGE,"E10.1.10"),sQuery(id+"F0.wireOp",EDGE,"E10.1.11"),sQuery(id+"F0.wireOp",EDGE,"E10.1.12"),sQuery(id+"F0.wireOp",EDGE,"E10.1.14"),sQuery(id+"F0.wireOp",EDGE,"E10.1.15"),sQuery(id+"F0.wireOp",EDGE,"E10.1.16"),sQuery(id+"F0.wireOp",EDGE,"E10.1.18"),sQuery(id+"F0.wireOp",EDGE,"E10.1.20"),sQuery(id+"F0.wireOp",EDGE,"E10.2.0"),sQuery(id+"F0.wireOp",EDGE,"E10.2.1"),sQuery(id+"F0.wireOp",EDGE,"E10.2.2"),sQuery(id+"F0.wireOp",EDGE,"E10.2.3"),sQuery(id+"F0.wireOp",EDGE,"E10.2.5"),sQuery(id+"F0.wireOp",EDGE,"E10.2.7"),sQuery(id+"F0.wireOp",EDGE,"E10.2.8"),sQuery(id+"F0.wireOp",EDGE,"E10.2.9"),sQuery(id+"F0.wireOp",EDGE,"E10.2.10"),sQuery(id+"F0.wireOp",EDGE,"E10.2.11"),sQuery(id+"F0.wireOp",EDGE,"E10.2.12"),sQuery(id+"F0.wireOp",EDGE,"E1"),sQuery(id+"F0.wireOp",EDGE,"E10.2.14"),sQuery(id+"F0.wireOp",EDGE,"E10.2.15"),sQuery(id+"F0.wireOp",EDGE,"E10.2.16"),sQuery(id+"F0.wireOp",EDGE,"E10.2.18"),sQuery(id+"F0.wireOp",EDGE,"E10.2.20"),sQuery(id+"F0.wireOp",EDGE,"E8.trimOffspring"),sQuery(id+"F0.wireOp",EDGE,"E0"),sQuery(id+"F0.wireOp",EDGE,"E10.1.6"),sQuery(id+"F0.wireOp",EDGE,"E11"),sQuery(id+"F0.wireOp",EDGE,"E12"),sQuery(id+"F0.wireOp",EDGE,"E13.1.0"),sQuery(id+"F0.wireOp",EDGE,"E13.1.1"),sQuery(id+"F0.wireOp",EDGE,"E13.2.0"),sQuery(id+"F0.wireOp",EDGE,"E13.2.1")])]}),"instanceName":"1"}),"instanceName":"1"}),"instanceName":"1"}),"instanceName":"1"});
            transform(context, id + "F52", {"entities" : qUnion([Q0]), "transformType" : TransformType.TRANSLATION_3D, "dx" : -277.2 * mm, "dy" : -90.1 * mm, "dz" : 0 * mm, "makeCopy" : true});
        }
        {
            var Q0;
            Q0=makeQuery(id+"F52.opPattern","COPY",BODY,{"derivedFrom":makeQuery(id+"F39.opPattern","COPY",BODY,{"derivedFrom":makeQuery(id+"F36.opPattern","COPY",BODY,{"derivedFrom":makeQuery(id+"F23.opPattern","COPY",BODY,{"derivedFrom":makeQuery(id+"F7.opPattern","COPY",BODY,{"derivedFrom":makeQuery(id+"F1.opExtrude","SWEPT_BODY",BODY,{"disambiguationData":[OSD([sQuery(id+"F0.wireOp",EDGE,"E2.0"),sQuery(id+"F0.wireOp",EDGE,"E2.1"),sQuery(id+"F0.wireOp",EDGE,"E2.2"),sQuery(id+"F0.wireOp",EDGE,"E2.3"),sQuery(id+"F0.wireOp",EDGE,"E2.4"),sQuery(id+"F0.wireOp",EDGE,"E2.5"),sQuery(id+"F0.wireOp",EDGE,"E3"),sQuery(id+"F0.wireOp",EDGE,"E4"),sQuery(id+"F0.wireOp",EDGE,"E5.0"),sQuery(id+"F0.wireOp",EDGE,"E5.1"),sQuery(id+"F0.wireOp",EDGE,"E5.3"),sQuery(id+"F0.wireOp",EDGE,"E5.4"),sQuery(id+"F0.wireOp",EDGE,"E5.5"),sQuery(id+"F0.wireOp",EDGE,"E6.trimOffspring"),sQuery(id+"F0.wireOp",EDGE,"E7.trimOffspring"),sQuery(id+"F0.wireOp",EDGE,"E9.trimOffspring"),sQuery(id+"F0.wireOp",EDGE,"E10.1.0"),sQuery(id+"F0.wireOp",EDGE,"E10.1.1"),sQuery(id+"F0.wireOp",EDGE,"E10.1.2"),sQuery(id+"F0.wireOp",EDGE,"E10.1.3"),sQuery(id+"F0.wireOp",EDGE,"E10.1.5"),sQuery(id+"F0.wireOp",EDGE,"E10.1.7"),sQuery(id+"F0.wireOp",EDGE,"E10.1.8"),sQuery(id+"F0.wireOp",EDGE,"E10.1.9"),sQuery(id+"F0.wireOp",EDGE,"E10.1.10"),sQuery(id+"F0.wireOp",EDGE,"E10.1.11"),sQuery(id+"F0.wireOp",EDGE,"E10.1.12"),sQuery(id+"F0.wireOp",EDGE,"E10.1.14"),sQuery(id+"F0.wireOp",EDGE,"E10.1.15"),sQuery(id+"F0.wireOp",EDGE,"E10.1.16"),sQuery(id+"F0.wireOp",EDGE,"E10.1.18"),sQuery(id+"F0.wireOp",EDGE,"E10.1.20"),sQuery(id+"F0.wireOp",EDGE,"E10.2.0"),sQuery(id+"F0.wireOp",EDGE,"E10.2.1"),sQuery(id+"F0.wireOp",EDGE,"E10.2.2"),sQuery(id+"F0.wireOp",EDGE,"E10.2.3"),sQuery(id+"F0.wireOp",EDGE,"E10.2.5"),sQuery(id+"F0.wireOp",EDGE,"E10.2.7"),sQuery(id+"F0.wireOp",EDGE,"E10.2.8"),sQuery(id+"F0.wireOp",EDGE,"E10.2.9"),sQuery(id+"F0.wireOp",EDGE,"E10.2.10"),sQuery(id+"F0.wireOp",EDGE,"E10.2.11"),sQuery(id+"F0.wireOp",EDGE,"E10.2.12"),sQuery(id+"F0.wireOp",EDGE,"E1"),sQuery(id+"F0.wireOp",EDGE,"E10.2.14"),sQuery(id+"F0.wireOp",EDGE,"E10.2.15"),sQuery(id+"F0.wireOp",EDGE,"E10.2.16"),sQuery(id+"F0.wireOp",EDGE,"E10.2.18"),sQuery(id+"F0.wireOp",EDGE,"E10.2.20"),sQuery(id+"F0.wireOp",EDGE,"E8.trimOffspring"),sQuery(id+"F0.wireOp",EDGE,"E0"),sQuery(id+"F0.wireOp",EDGE,"E10.1.6"),sQuery(id+"F0.wireOp",EDGE,"E11"),sQuery(id+"F0.wireOp",EDGE,"E12"),sQuery(id+"F0.wireOp",EDGE,"E13.1.0"),sQuery(id+"F0.wireOp",EDGE,"E13.1.1"),sQuery(id+"F0.wireOp",EDGE,"E13.2.0"),sQuery(id+"F0.wireOp",EDGE,"E13.2.1")])]}),"instanceName":"1"}),"instanceName":"1"}),"instanceName":"1"}),"instanceName":"1"}),"instanceName":"1"});
            transform(context, id + "F53", {"entities" : qUnion([Q0]), "transformType" : TransformType.TRANSLATION_3D, "dx" : 69.1 * mm, "dy" : -4.4 * mm, "dz" : 0 * mm, "makeCopy" : true});
        }
        {
            var Q0;
            Q0=makeQuery(id+"F36.opPattern","COPY",BODY,{"derivedFrom":makeQuery(id+"F23.opPattern","COPY",BODY,{"derivedFrom":makeQuery(id+"F7.opPattern","COPY",BODY,{"derivedFrom":makeQuery(id+"F1.opExtrude","SWEPT_BODY",BODY,{"disambiguationData":[OSD([sQuery(id+"F0.wireOp",EDGE,"E2.0"),sQuery(id+"F0.wireOp",EDGE,"E2.1"),sQuery(id+"F0.wireOp",EDGE,"E2.2"),sQuery(id+"F0.wireOp",EDGE,"E2.3"),sQuery(id+"F0.wireOp",EDGE,"E2.4"),sQuery(id+"F0.wireOp",EDGE,"E2.5"),sQuery(id+"F0.wireOp",EDGE,"E3"),sQuery(id+"F0.wireOp",EDGE,"E4"),sQuery(id+"F0.wireOp",EDGE,"E5.0"),sQuery(id+"F0.wireOp",EDGE,"E5.1"),sQuery(id+"F0.wireOp",EDGE,"E5.3"),sQuery(id+"F0.wireOp",EDGE,"E5.4"),sQuery(id+"F0.wireOp",EDGE,"E5.5"),sQuery(id+"F0.wireOp",EDGE,"E6.trimOffspring"),sQuery(id+"F0.wireOp",EDGE,"E7.trimOffspring"),sQuery(id+"F0.wireOp",EDGE,"E9.trimOffspring"),sQuery(id+"F0.wireOp",EDGE,"E10.1.0"),sQuery(id+"F0.wireOp",EDGE,"E10.1.1"),sQuery(id+"F0.wireOp",EDGE,"E10.1.2"),sQuery(id+"F0.wireOp",EDGE,"E10.1.3"),sQuery(id+"F0.wireOp",EDGE,"E10.1.5"),sQuery(id+"F0.wireOp",EDGE,"E10.1.7"),sQuery(id+"F0.wireOp",EDGE,"E10.1.8"),sQuery(id+"F0.wireOp",EDGE,"E10.1.9"),sQuery(id+"F0.wireOp",EDGE,"E10.1.10"),sQuery(id+"F0.wireOp",EDGE,"E10.1.11"),sQuery(id+"F0.wireOp",EDGE,"E10.1.12"),sQuery(id+"F0.wireOp",EDGE,"E10.1.14"),sQuery(id+"F0.wireOp",EDGE,"E10.1.15"),sQuery(id+"F0.wireOp",EDGE,"E10.1.16"),sQuery(id+"F0.wireOp",EDGE,"E10.1.18"),sQuery(id+"F0.wireOp",EDGE,"E10.1.20"),sQuery(id+"F0.wireOp",EDGE,"E10.2.0"),sQuery(id+"F0.wireOp",EDGE,"E10.2.1"),sQuery(id+"F0.wireOp",EDGE,"E10.2.2"),sQuery(id+"F0.wireOp",EDGE,"E10.2.3"),sQuery(id+"F0.wireOp",EDGE,"E10.2.5"),sQuery(id+"F0.wireOp",EDGE,"E10.2.7"),sQuery(id+"F0.wireOp",EDGE,"E10.2.8"),sQuery(id+"F0.wireOp",EDGE,"E10.2.9"),sQuery(id+"F0.wireOp",EDGE,"E10.2.10"),sQuery(id+"F0.wireOp",EDGE,"E10.2.11"),sQuery(id+"F0.wireOp",EDGE,"E10.2.12"),sQuery(id+"F0.wireOp",EDGE,"E1"),sQuery(id+"F0.wireOp",EDGE,"E10.2.14"),sQuery(id+"F0.wireOp",EDGE,"E10.2.15"),sQuery(id+"F0.wireOp",EDGE,"E10.2.16"),sQuery(id+"F0.wireOp",EDGE,"E10.2.18"),sQuery(id+"F0.wireOp",EDGE,"E10.2.20"),sQuery(id+"F0.wireOp",EDGE,"E8.trimOffspring"),sQuery(id+"F0.wireOp",EDGE,"E0"),sQuery(id+"F0.wireOp",EDGE,"E10.1.6"),sQuery(id+"F0.wireOp",EDGE,"E11"),sQuery(id+"F0.wireOp",EDGE,"E12"),sQuery(id+"F0.wireOp",EDGE,"E13.1.0"),sQuery(id+"F0.wireOp",EDGE,"E13.1.1"),sQuery(id+"F0.wireOp",EDGE,"E13.2.0"),sQuery(id+"F0.wireOp",EDGE,"E13.2.1")])]}),"instanceName":"1"}),"instanceName":"1"}),"instanceName":"1"});
            transform(context, id + "F54", {"entities" : qUnion([Q0]), "transformType" : TransformType.TRANSLATION_3D, "dx" : -74.8 * mm, "dy" : -122.1 * mm, "dz" : 0 * mm, "makeCopy" : true});
        }
        {
            var Q0;
            Q0=makeQuery(id+"F46.opPattern","COPY",BODY,{"derivedFrom":makeQuery(id+"F45.opPattern","COPY",BODY,{"derivedFrom":makeQuery(id+"F5.opPattern","COPY",BODY,{"derivedFrom":makeQuery(id+"F1.opExtrude","SWEPT_BODY",BODY,{"disambiguationData":[OSD([sQuery(id+"F0.wireOp",EDGE,"E2.0"),sQuery(id+"F0.wireOp",EDGE,"E2.1"),sQuery(id+"F0.wireOp",EDGE,"E2.2"),sQuery(id+"F0.wireOp",EDGE,"E2.3"),sQuery(id+"F0.wireOp",EDGE,"E2.4"),sQuery(id+"F0.wireOp",EDGE,"E2.5"),sQuery(id+"F0.wireOp",EDGE,"E3"),sQuery(id+"F0.wireOp",EDGE,"E4"),sQuery(id+"F0.wireOp",EDGE,"E5.0"),sQuery(id+"F0.wireOp",EDGE,"E5.1"),sQuery(id+"F0.wireOp",EDGE,"E5.3"),sQuery(id+"F0.wireOp",EDGE,"E5.4"),sQuery(id+"F0.wireOp",EDGE,"E5.5"),sQuery(id+"F0.wireOp",EDGE,"E6.trimOffspring"),sQuery(id+"F0.wireOp",EDGE,"E7.trimOffspring"),sQuery(id+"F0.wireOp",EDGE,"E9.trimOffspring"),sQuery(id+"F0.wireOp",EDGE,"E10.1.0"),sQuery(id+"F0.wireOp",EDGE,"E10.1.1"),sQuery(id+"F0.wireOp",EDGE,"E10.1.2"),sQuery(id+"F0.wireOp",EDGE,"E10.1.3"),sQuery(id+"F0.wireOp",EDGE,"E10.1.5"),sQuery(id+"F0.wireOp",EDGE,"E10.1.7"),sQuery(id+"F0.wireOp",EDGE,"E10.1.8"),sQuery(id+"F0.wireOp",EDGE,"E10.1.9"),sQuery(id+"F0.wireOp",EDGE,"E10.1.10"),sQuery(id+"F0.wireOp",EDGE,"E10.1.11"),sQuery(id+"F0.wireOp",EDGE,"E10.1.12"),sQuery(id+"F0.wireOp",EDGE,"E10.1.14"),sQuery(id+"F0.wireOp",EDGE,"E10.1.15"),sQuery(id+"F0.wireOp",EDGE,"E10.1.16"),sQuery(id+"F0.wireOp",EDGE,"E10.1.18"),sQuery(id+"F0.wireOp",EDGE,"E10.1.20"),sQuery(id+"F0.wireOp",EDGE,"E10.2.0"),sQuery(id+"F0.wireOp",EDGE,"E10.2.1"),sQuery(id+"F0.wireOp",EDGE,"E10.2.2"),sQuery(id+"F0.wireOp",EDGE,"E10.2.3"),sQuery(id+"F0.wireOp",EDGE,"E10.2.5"),sQuery(id+"F0.wireOp",EDGE,"E10.2.7"),sQuery(id+"F0.wireOp",EDGE,"E10.2.8"),sQuery(id+"F0.wireOp",EDGE,"E10.2.9"),sQuery(id+"F0.wireOp",EDGE,"E10.2.10"),sQuery(id+"F0.wireOp",EDGE,"E10.2.11"),sQuery(id+"F0.wireOp",EDGE,"E10.2.12"),sQuery(id+"F0.wireOp",EDGE,"E1"),sQuery(id+"F0.wireOp",EDGE,"E10.2.14"),sQuery(id+"F0.wireOp",EDGE,"E10.2.15"),sQuery(id+"F0.wireOp",EDGE,"E10.2.16"),sQuery(id+"F0.wireOp",EDGE,"E10.2.18"),sQuery(id+"F0.wireOp",EDGE,"E10.2.20"),sQuery(id+"F0.wireOp",EDGE,"E8.trimOffspring"),sQuery(id+"F0.wireOp",EDGE,"E0"),sQuery(id+"F0.wireOp",EDGE,"E10.1.6"),sQuery(id+"F0.wireOp",EDGE,"E11"),sQuery(id+"F0.wireOp",EDGE,"E12"),sQuery(id+"F0.wireOp",EDGE,"E13.1.0"),sQuery(id+"F0.wireOp",EDGE,"E13.1.1"),sQuery(id+"F0.wireOp",EDGE,"E13.2.0"),sQuery(id+"F0.wireOp",EDGE,"E13.2.1")])]}),"instanceName":"1"}),"instanceName":"1"}),"instanceName":"1"});
            transform(context, id + "F55", {"entities" : qUnion([Q0]), "transformType" : TransformType.TRANSLATION_3D, "dx" : 35.5 * mm, "dy" : -80.4 * mm, "dz" : 0 * mm, "makeCopy" : true});
        }
        {
            var Q0;
            Q0=makeQuery(id+"F18.opPattern","COPY",BODY,{"derivedFrom":makeQuery(id+"F13.opPattern","COPY",BODY,{"derivedFrom":makeQuery(id+"F1.opExtrude","SWEPT_BODY",BODY,{"disambiguationData":[OSD([sQuery(id+"F0.wireOp",EDGE,"E2.0"),sQuery(id+"F0.wireOp",EDGE,"E2.1"),sQuery(id+"F0.wireOp",EDGE,"E2.2"),sQuery(id+"F0.wireOp",EDGE,"E2.3"),sQuery(id+"F0.wireOp",EDGE,"E2.4"),sQuery(id+"F0.wireOp",EDGE,"E2.5"),sQuery(id+"F0.wireOp",EDGE,"E3"),sQuery(id+"F0.wireOp",EDGE,"E4"),sQuery(id+"F0.wireOp",EDGE,"E5.0"),sQuery(id+"F0.wireOp",EDGE,"E5.1"),sQuery(id+"F0.wireOp",EDGE,"E5.3"),sQuery(id+"F0.wireOp",EDGE,"E5.4"),sQuery(id+"F0.wireOp",EDGE,"E5.5"),sQuery(id+"F0.wireOp",EDGE,"E6.trimOffspring"),sQuery(id+"F0.wireOp",EDGE,"E7.trimOffspring"),sQuery(id+"F0.wireOp",EDGE,"E9.trimOffspring"),sQuery(id+"F0.wireOp",EDGE,"E10.1.0"),sQuery(id+"F0.wireOp",EDGE,"E10.1.1"),sQuery(id+"F0.wireOp",EDGE,"E10.1.2"),sQuery(id+"F0.wireOp",EDGE,"E10.1.3"),sQuery(id+"F0.wireOp",EDGE,"E10.1.5"),sQuery(id+"F0.wireOp",EDGE,"E10.1.7"),sQuery(id+"F0.wireOp",EDGE,"E10.1.8"),sQuery(id+"F0.wireOp",EDGE,"E10.1.9"),sQuery(id+"F0.wireOp",EDGE,"E10.1.10"),sQuery(id+"F0.wireOp",EDGE,"E10.1.11"),sQuery(id+"F0.wireOp",EDGE,"E10.1.12"),sQuery(id+"F0.wireOp",EDGE,"E10.1.14"),sQuery(id+"F0.wireOp",EDGE,"E10.1.15"),sQuery(id+"F0.wireOp",EDGE,"E10.1.16"),sQuery(id+"F0.wireOp",EDGE,"E10.1.18"),sQuery(id+"F0.wireOp",EDGE,"E10.1.20"),sQuery(id+"F0.wireOp",EDGE,"E10.2.0"),sQuery(id+"F0.wireOp",EDGE,"E10.2.1"),sQuery(id+"F0.wireOp",EDGE,"E10.2.2"),sQuery(id+"F0.wireOp",EDGE,"E10.2.3"),sQuery(id+"F0.wireOp",EDGE,"E10.2.5"),sQuery(id+"F0.wireOp",EDGE,"E10.2.7"),sQuery(id+"F0.wireOp",EDGE,"E10.2.8"),sQuery(id+"F0.wireOp",EDGE,"E10.2.9"),sQuery(id+"F0.wireOp",EDGE,"E10.2.10"),sQuery(id+"F0.wireOp",EDGE,"E10.2.11"),sQuery(id+"F0.wireOp",EDGE,"E10.2.12"),sQuery(id+"F0.wireOp",EDGE,"E1"),sQuery(id+"F0.wireOp",EDGE,"E10.2.14"),sQuery(id+"F0.wireOp",EDGE,"E10.2.15"),sQuery(id+"F0.wireOp",EDGE,"E10.2.16"),sQuery(id+"F0.wireOp",EDGE,"E10.2.18"),sQuery(id+"F0.wireOp",EDGE,"E10.2.20"),sQuery(id+"F0.wireOp",EDGE,"E8.trimOffspring"),sQuery(id+"F0.wireOp",EDGE,"E0"),sQuery(id+"F0.wireOp",EDGE,"E10.1.6"),sQuery(id+"F0.wireOp",EDGE,"E11"),sQuery(id+"F0.wireOp",EDGE,"E12"),sQuery(id+"F0.wireOp",EDGE,"E13.1.0"),sQuery(id+"F0.wireOp",EDGE,"E13.1.1"),sQuery(id+"F0.wireOp",EDGE,"E13.2.0"),sQuery(id+"F0.wireOp",EDGE,"E13.2.1")])]}),"instanceName":"1"}),"instanceName":"1"});
            var Q1;
            Q1=makeQuery(id+"F13.opPattern","COPY",BODY,{"derivedFrom":makeQuery(id+"F1.opExtrude","SWEPT_BODY",BODY,{"disambiguationData":[OSD([sQuery(id+"F0.wireOp",EDGE,"E2.0"),sQuery(id+"F0.wireOp",EDGE,"E2.1"),sQuery(id+"F0.wireOp",EDGE,"E2.2"),sQuery(id+"F0.wireOp",EDGE,"E2.3"),sQuery(id+"F0.wireOp",EDGE,"E2.4"),sQuery(id+"F0.wireOp",EDGE,"E2.5"),sQuery(id+"F0.wireOp",EDGE,"E3"),sQuery(id+"F0.wireOp",EDGE,"E4"),sQuery(id+"F0.wireOp",EDGE,"E5.0"),sQuery(id+"F0.wireOp",EDGE,"E5.1"),sQuery(id+"F0.wireOp",EDGE,"E5.3"),sQuery(id+"F0.wireOp",EDGE,"E5.4"),sQuery(id+"F0.wireOp",EDGE,"E5.5"),sQuery(id+"F0.wireOp",EDGE,"E6.trimOffspring"),sQuery(id+"F0.wireOp",EDGE,"E7.trimOffspring"),sQuery(id+"F0.wireOp",EDGE,"E9.trimOffspring"),sQuery(id+"F0.wireOp",EDGE,"E10.1.0"),sQuery(id+"F0.wireOp",EDGE,"E10.1.1"),sQuery(id+"F0.wireOp",EDGE,"E10.1.2"),sQuery(id+"F0.wireOp",EDGE,"E10.1.3"),sQuery(id+"F0.wireOp",EDGE,"E10.1.5"),sQuery(id+"F0.wireOp",EDGE,"E10.1.7"),sQuery(id+"F0.wireOp",EDGE,"E10.1.8"),sQuery(id+"F0.wireOp",EDGE,"E10.1.9"),sQuery(id+"F0.wireOp",EDGE,"E10.1.10"),sQuery(id+"F0.wireOp",EDGE,"E10.1.11"),sQuery(id+"F0.wireOp",EDGE,"E10.1.12"),sQuery(id+"F0.wireOp",EDGE,"E10.1.14"),sQuery(id+"F0.wireOp",EDGE,"E10.1.15"),sQuery(id+"F0.wireOp",EDGE,"E10.1.16"),sQuery(id+"F0.wireOp",EDGE,"E10.1.18"),sQuery(id+"F0.wireOp",EDGE,"E10.1.20"),sQuery(id+"F0.wireOp",EDGE,"E10.2.0"),sQuery(id+"F0.wireOp",EDGE,"E10.2.1"),sQuery(id+"F0.wireOp",EDGE,"E10.2.2"),sQuery(id+"F0.wireOp",EDGE,"E10.2.3"),sQuery(id+"F0.wireOp",EDGE,"E10.2.5"),sQuery(id+"F0.wireOp",EDGE,"E10.2.7"),sQuery(id+"F0.wireOp",EDGE,"E10.2.8"),sQuery(id+"F0.wireOp",EDGE,"E10.2.9"),sQuery(id+"F0.wireOp",EDGE,"E10.2.10"),sQuery(id+"F0.wireOp",EDGE,"E10.2.11"),sQuery(id+"F0.wireOp",EDGE,"E10.2.12"),sQuery(id+"F0.wireOp",EDGE,"E1"),sQuery(id+"F0.wireOp",EDGE,"E10.2.14"),sQuery(id+"F0.wireOp",EDGE,"E10.2.15"),sQuery(id+"F0.wireOp",EDGE,"E10.2.16"),sQuery(id+"F0.wireOp",EDGE,"E10.2.18"),sQuery(id+"F0.wireOp",EDGE,"E10.2.20"),sQuery(id+"F0.wireOp",EDGE,"E8.trimOffspring"),sQuery(id+"F0.wireOp",EDGE,"E0"),sQuery(id+"F0.wireOp",EDGE,"E10.1.6"),sQuery(id+"F0.wireOp",EDGE,"E11"),sQuery(id+"F0.wireOp",EDGE,"E12"),sQuery(id+"F0.wireOp",EDGE,"E13.1.0"),sQuery(id+"F0.wireOp",EDGE,"E13.1.1"),sQuery(id+"F0.wireOp",EDGE,"E13.2.0"),sQuery(id+"F0.wireOp",EDGE,"E13.2.1")])]}),"instanceName":"1"});
            var Q2;
            Q2=makeQuery(id+"F19.opPattern","COPY",BODY,{"derivedFrom":makeQuery(id+"F18.opPattern","COPY",BODY,{"derivedFrom":makeQuery(id+"F13.opPattern","COPY",BODY,{"derivedFrom":makeQuery(id+"F1.opExtrude","SWEPT_BODY",BODY,{"disambiguationData":[OSD([sQuery(id+"F0.wireOp",EDGE,"E2.0"),sQuery(id+"F0.wireOp",EDGE,"E2.1"),sQuery(id+"F0.wireOp",EDGE,"E2.2"),sQuery(id+"F0.wireOp",EDGE,"E2.3"),sQuery(id+"F0.wireOp",EDGE,"E2.4"),sQuery(id+"F0.wireOp",EDGE,"E2.5"),sQuery(id+"F0.wireOp",EDGE,"E3"),sQuery(id+"F0.wireOp",EDGE,"E4"),sQuery(id+"F0.wireOp",EDGE,"E5.0"),sQuery(id+"F0.wireOp",EDGE,"E5.1"),sQuery(id+"F0.wireOp",EDGE,"E5.3"),sQuery(id+"F0.wireOp",EDGE,"E5.4"),sQuery(id+"F0.wireOp",EDGE,"E5.5"),sQuery(id+"F0.wireOp",EDGE,"E6.trimOffspring"),sQuery(id+"F0.wireOp",EDGE,"E7.trimOffspring"),sQuery(id+"F0.wireOp",EDGE,"E9.trimOffspring"),sQuery(id+"F0.wireOp",EDGE,"E10.1.0"),sQuery(id+"F0.wireOp",EDGE,"E10.1.1"),sQuery(id+"F0.wireOp",EDGE,"E10.1.2"),sQuery(id+"F0.wireOp",EDGE,"E10.1.3"),sQuery(id+"F0.wireOp",EDGE,"E10.1.5"),sQuery(id+"F0.wireOp",EDGE,"E10.1.7"),sQuery(id+"F0.wireOp",EDGE,"E10.1.8"),sQuery(id+"F0.wireOp",EDGE,"E10.1.9"),sQuery(id+"F0.wireOp",EDGE,"E10.1.10"),sQuery(id+"F0.wireOp",EDGE,"E10.1.11"),sQuery(id+"F0.wireOp",EDGE,"E10.1.12"),sQuery(id+"F0.wireOp",EDGE,"E10.1.14"),sQuery(id+"F0.wireOp",EDGE,"E10.1.15"),sQuery(id+"F0.wireOp",EDGE,"E10.1.16"),sQuery(id+"F0.wireOp",EDGE,"E10.1.18"),sQuery(id+"F0.wireOp",EDGE,"E10.1.20"),sQuery(id+"F0.wireOp",EDGE,"E10.2.0"),sQuery(id+"F0.wireOp",EDGE,"E10.2.1"),sQuery(id+"F0.wireOp",EDGE,"E10.2.2"),sQuery(id+"F0.wireOp",EDGE,"E10.2.3"),sQuery(id+"F0.wireOp",EDGE,"E10.2.5"),sQuery(id+"F0.wireOp",EDGE,"E10.2.7"),sQuery(id+"F0.wireOp",EDGE,"E10.2.8"),sQuery(id+"F0.wireOp",EDGE,"E10.2.9"),sQuery(id+"F0.wireOp",EDGE,"E10.2.10"),sQuery(id+"F0.wireOp",EDGE,"E10.2.11"),sQuery(id+"F0.wireOp",EDGE,"E10.2.12"),sQuery(id+"F0.wireOp",EDGE,"E1"),sQuery(id+"F0.wireOp",EDGE,"E10.2.14"),sQuery(id+"F0.wireOp",EDGE,"E10.2.15"),sQuery(id+"F0.wireOp",EDGE,"E10.2.16"),sQuery(id+"F0.wireOp",EDGE,"E10.2.18"),sQuery(id+"F0.wireOp",EDGE,"E10.2.20"),sQuery(id+"F0.wireOp",EDGE,"E8.trimOffspring"),sQuery(id+"F0.wireOp",EDGE,"E0"),sQuery(id+"F0.wireOp",EDGE,"E10.1.6"),sQuery(id+"F0.wireOp",EDGE,"E11"),sQuery(id+"F0.wireOp",EDGE,"E12"),sQuery(id+"F0.wireOp",EDGE,"E13.1.0"),sQuery(id+"F0.wireOp",EDGE,"E13.1.1"),sQuery(id+"F0.wireOp",EDGE,"E13.2.0"),sQuery(id+"F0.wireOp",EDGE,"E13.2.1")])]}),"instanceName":"1"}),"instanceName":"1"}),"instanceName":"1"});
            transform(context, id + "F56", {"entities" : qUnion([Q0, Q1, Q2]), "transformType" : TransformType.TRANSLATION_3D, "dx" : -8.9 * mm, "dy" : -236.7 * mm, "dz" : 0 * mm, "makeCopy" : true});
        }
        {
            var Q0;
            Q0=makeQuery(id+"F18.opPattern","COPY",BODY,{"derivedFrom":makeQuery(id+"F13.opPattern","COPY",BODY,{"derivedFrom":makeQuery(id+"F1.opExtrude","SWEPT_BODY",BODY,{"disambiguationData":[OSD([sQuery(id+"F0.wireOp",EDGE,"E2.0"),sQuery(id+"F0.wireOp",EDGE,"E2.1"),sQuery(id+"F0.wireOp",EDGE,"E2.2"),sQuery(id+"F0.wireOp",EDGE,"E2.3"),sQuery(id+"F0.wireOp",EDGE,"E2.4"),sQuery(id+"F0.wireOp",EDGE,"E2.5"),sQuery(id+"F0.wireOp",EDGE,"E3"),sQuery(id+"F0.wireOp",EDGE,"E4"),sQuery(id+"F0.wireOp",EDGE,"E5.0"),sQuery(id+"F0.wireOp",EDGE,"E5.1"),sQuery(id+"F0.wireOp",EDGE,"E5.3"),sQuery(id+"F0.wireOp",EDGE,"E5.4"),sQuery(id+"F0.wireOp",EDGE,"E5.5"),sQuery(id+"F0.wireOp",EDGE,"E6.trimOffspring"),sQuery(id+"F0.wireOp",EDGE,"E7.trimOffspring"),sQuery(id+"F0.wireOp",EDGE,"E9.trimOffspring"),sQuery(id+"F0.wireOp",EDGE,"E10.1.0"),sQuery(id+"F0.wireOp",EDGE,"E10.1.1"),sQuery(id+"F0.wireOp",EDGE,"E10.1.2"),sQuery(id+"F0.wireOp",EDGE,"E10.1.3"),sQuery(id+"F0.wireOp",EDGE,"E10.1.5"),sQuery(id+"F0.wireOp",EDGE,"E10.1.7"),sQuery(id+"F0.wireOp",EDGE,"E10.1.8"),sQuery(id+"F0.wireOp",EDGE,"E10.1.9"),sQuery(id+"F0.wireOp",EDGE,"E10.1.10"),sQuery(id+"F0.wireOp",EDGE,"E10.1.11"),sQuery(id+"F0.wireOp",EDGE,"E10.1.12"),sQuery(id+"F0.wireOp",EDGE,"E10.1.14"),sQuery(id+"F0.wireOp",EDGE,"E10.1.15"),sQuery(id+"F0.wireOp",EDGE,"E10.1.16"),sQuery(id+"F0.wireOp",EDGE,"E10.1.18"),sQuery(id+"F0.wireOp",EDGE,"E10.1.20"),sQuery(id+"F0.wireOp",EDGE,"E10.2.0"),sQuery(id+"F0.wireOp",EDGE,"E10.2.1"),sQuery(id+"F0.wireOp",EDGE,"E10.2.2"),sQuery(id+"F0.wireOp",EDGE,"E10.2.3"),sQuery(id+"F0.wireOp",EDGE,"E10.2.5"),sQuery(id+"F0.wireOp",EDGE,"E10.2.7"),sQuery(id+"F0.wireOp",EDGE,"E10.2.8"),sQuery(id+"F0.wireOp",EDGE,"E10.2.9"),sQuery(id+"F0.wireOp",EDGE,"E10.2.10"),sQuery(id+"F0.wireOp",EDGE,"E10.2.11"),sQuery(id+"F0.wireOp",EDGE,"E10.2.12"),sQuery(id+"F0.wireOp",EDGE,"E1"),sQuery(id+"F0.wireOp",EDGE,"E10.2.14"),sQuery(id+"F0.wireOp",EDGE,"E10.2.15"),sQuery(id+"F0.wireOp",EDGE,"E10.2.16"),sQuery(id+"F0.wireOp",EDGE,"E10.2.18"),sQuery(id+"F0.wireOp",EDGE,"E10.2.20"),sQuery(id+"F0.wireOp",EDGE,"E8.trimOffspring"),sQuery(id+"F0.wireOp",EDGE,"E0"),sQuery(id+"F0.wireOp",EDGE,"E10.1.6"),sQuery(id+"F0.wireOp",EDGE,"E11"),sQuery(id+"F0.wireOp",EDGE,"E12"),sQuery(id+"F0.wireOp",EDGE,"E13.1.0"),sQuery(id+"F0.wireOp",EDGE,"E13.1.1"),sQuery(id+"F0.wireOp",EDGE,"E13.2.0"),sQuery(id+"F0.wireOp",EDGE,"E13.2.1")])]}),"instanceName":"1"}),"instanceName":"1"});
            transform(context, id + "F57", {"entities" : qUnion([Q0]), "transformType" : TransformType.TRANSLATION_3D, "dx" : 0 * mm, "dy" : -1.5 * mm, "dz" : 0 * mm, "makeCopy" : false});
        }
        {
            var Q0;
            Q0=makeQuery(id+"F13.opPattern","COPY",BODY,{"derivedFrom":makeQuery(id+"F1.opExtrude","SWEPT_BODY",BODY,{"disambiguationData":[OSD([sQuery(id+"F0.wireOp",EDGE,"E2.0"),sQuery(id+"F0.wireOp",EDGE,"E2.1"),sQuery(id+"F0.wireOp",EDGE,"E2.2"),sQuery(id+"F0.wireOp",EDGE,"E2.3"),sQuery(id+"F0.wireOp",EDGE,"E2.4"),sQuery(id+"F0.wireOp",EDGE,"E2.5"),sQuery(id+"F0.wireOp",EDGE,"E3"),sQuery(id+"F0.wireOp",EDGE,"E4"),sQuery(id+"F0.wireOp",EDGE,"E5.0"),sQuery(id+"F0.wireOp",EDGE,"E5.1"),sQuery(id+"F0.wireOp",EDGE,"E5.3"),sQuery(id+"F0.wireOp",EDGE,"E5.4"),sQuery(id+"F0.wireOp",EDGE,"E5.5"),sQuery(id+"F0.wireOp",EDGE,"E6.trimOffspring"),sQuery(id+"F0.wireOp",EDGE,"E7.trimOffspring"),sQuery(id+"F0.wireOp",EDGE,"E9.trimOffspring"),sQuery(id+"F0.wireOp",EDGE,"E10.1.0"),sQuery(id+"F0.wireOp",EDGE,"E10.1.1"),sQuery(id+"F0.wireOp",EDGE,"E10.1.2"),sQuery(id+"F0.wireOp",EDGE,"E10.1.3"),sQuery(id+"F0.wireOp",EDGE,"E10.1.5"),sQuery(id+"F0.wireOp",EDGE,"E10.1.7"),sQuery(id+"F0.wireOp",EDGE,"E10.1.8"),sQuery(id+"F0.wireOp",EDGE,"E10.1.9"),sQuery(id+"F0.wireOp",EDGE,"E10.1.10"),sQuery(id+"F0.wireOp",EDGE,"E10.1.11"),sQuery(id+"F0.wireOp",EDGE,"E10.1.12"),sQuery(id+"F0.wireOp",EDGE,"E10.1.14"),sQuery(id+"F0.wireOp",EDGE,"E10.1.15"),sQuery(id+"F0.wireOp",EDGE,"E10.1.16"),sQuery(id+"F0.wireOp",EDGE,"E10.1.18"),sQuery(id+"F0.wireOp",EDGE,"E10.1.20"),sQuery(id+"F0.wireOp",EDGE,"E10.2.0"),sQuery(id+"F0.wireOp",EDGE,"E10.2.1"),sQuery(id+"F0.wireOp",EDGE,"E10.2.2"),sQuery(id+"F0.wireOp",EDGE,"E10.2.3"),sQuery(id+"F0.wireOp",EDGE,"E10.2.5"),sQuery(id+"F0.wireOp",EDGE,"E10.2.7"),sQuery(id+"F0.wireOp",EDGE,"E10.2.8"),sQuery(id+"F0.wireOp",EDGE,"E10.2.9"),sQuery(id+"F0.wireOp",EDGE,"E10.2.10"),sQuery(id+"F0.wireOp",EDGE,"E10.2.11"),sQuery(id+"F0.wireOp",EDGE,"E10.2.12"),sQuery(id+"F0.wireOp",EDGE,"E1"),sQuery(id+"F0.wireOp",EDGE,"E10.2.14"),sQuery(id+"F0.wireOp",EDGE,"E10.2.15"),sQuery(id+"F0.wireOp",EDGE,"E10.2.16"),sQuery(id+"F0.wireOp",EDGE,"E10.2.18"),sQuery(id+"F0.wireOp",EDGE,"E10.2.20"),sQuery(id+"F0.wireOp",EDGE,"E8.trimOffspring"),sQuery(id+"F0.wireOp",EDGE,"E0"),sQuery(id+"F0.wireOp",EDGE,"E10.1.6"),sQuery(id+"F0.wireOp",EDGE,"E11"),sQuery(id+"F0.wireOp",EDGE,"E12"),sQuery(id+"F0.wireOp",EDGE,"E13.1.0"),sQuery(id+"F0.wireOp",EDGE,"E13.1.1"),sQuery(id+"F0.wireOp",EDGE,"E13.2.0"),sQuery(id+"F0.wireOp",EDGE,"E13.2.1")])]}),"instanceName":"1"});
            transform(context, id + "F58", {"entities" : qUnion([Q0]), "transformType" : TransformType.TRANSLATION_3D, "dx" : 0.3 * mm, "dy" : 3.2 * mm, "dz" : 0 * mm, "makeCopy" : false});
        }
        {
            var Q0;
            Q0=makeQuery(id+"F19.opPattern","COPY",BODY,{"derivedFrom":makeQuery(id+"F18.opPattern","COPY",BODY,{"derivedFrom":makeQuery(id+"F13.opPattern","COPY",BODY,{"derivedFrom":makeQuery(id+"F1.opExtrude","SWEPT_BODY",BODY,{"disambiguationData":[OSD([sQuery(id+"F0.wireOp",EDGE,"E2.0"),sQuery(id+"F0.wireOp",EDGE,"E2.1"),sQuery(id+"F0.wireOp",EDGE,"E2.2"),sQuery(id+"F0.wireOp",EDGE,"E2.3"),sQuery(id+"F0.wireOp",EDGE,"E2.4"),sQuery(id+"F0.wireOp",EDGE,"E2.5"),sQuery(id+"F0.wireOp",EDGE,"E3"),sQuery(id+"F0.wireOp",EDGE,"E4"),sQuery(id+"F0.wireOp",EDGE,"E5.0"),sQuery(id+"F0.wireOp",EDGE,"E5.1"),sQuery(id+"F0.wireOp",EDGE,"E5.3"),sQuery(id+"F0.wireOp",EDGE,"E5.4"),sQuery(id+"F0.wireOp",EDGE,"E5.5"),sQuery(id+"F0.wireOp",EDGE,"E6.trimOffspring"),sQuery(id+"F0.wireOp",EDGE,"E7.trimOffspring"),sQuery(id+"F0.wireOp",EDGE,"E9.trimOffspring"),sQuery(id+"F0.wireOp",EDGE,"E10.1.0"),sQuery(id+"F0.wireOp",EDGE,"E10.1.1"),sQuery(id+"F0.wireOp",EDGE,"E10.1.2"),sQuery(id+"F0.wireOp",EDGE,"E10.1.3"),sQuery(id+"F0.wireOp",EDGE,"E10.1.5"),sQuery(id+"F0.wireOp",EDGE,"E10.1.7"),sQuery(id+"F0.wireOp",EDGE,"E10.1.8"),sQuery(id+"F0.wireOp",EDGE,"E10.1.9"),sQuery(id+"F0.wireOp",EDGE,"E10.1.10"),sQuery(id+"F0.wireOp",EDGE,"E10.1.11"),sQuery(id+"F0.wireOp",EDGE,"E10.1.12"),sQuery(id+"F0.wireOp",EDGE,"E10.1.14"),sQuery(id+"F0.wireOp",EDGE,"E10.1.15"),sQuery(id+"F0.wireOp",EDGE,"E10.1.16"),sQuery(id+"F0.wireOp",EDGE,"E10.1.18"),sQuery(id+"F0.wireOp",EDGE,"E10.1.20"),sQuery(id+"F0.wireOp",EDGE,"E10.2.0"),sQuery(id+"F0.wireOp",EDGE,"E10.2.1"),sQuery(id+"F0.wireOp",EDGE,"E10.2.2"),sQuery(id+"F0.wireOp",EDGE,"E10.2.3"),sQuery(id+"F0.wireOp",EDGE,"E10.2.5"),sQuery(id+"F0.wireOp",EDGE,"E10.2.7"),sQuery(id+"F0.wireOp",EDGE,"E10.2.8"),sQuery(id+"F0.wireOp",EDGE,"E10.2.9"),sQuery(id+"F0.wireOp",EDGE,"E10.2.10"),sQuery(id+"F0.wireOp",EDGE,"E10.2.11"),sQuery(id+"F0.wireOp",EDGE,"E10.2.12"),sQuery(id+"F0.wireOp",EDGE,"E1"),sQuery(id+"F0.wireOp",EDGE,"E10.2.14"),sQuery(id+"F0.wireOp",EDGE,"E10.2.15"),sQuery(id+"F0.wireOp",EDGE,"E10.2.16"),sQuery(id+"F0.wireOp",EDGE,"E10.2.18"),sQuery(id+"F0.wireOp",EDGE,"E10.2.20"),sQuery(id+"F0.wireOp",EDGE,"E8.trimOffspring"),sQuery(id+"F0.wireOp",EDGE,"E0"),sQuery(id+"F0.wireOp",EDGE,"E10.1.6"),sQuery(id+"F0.wireOp",EDGE,"E11"),sQuery(id+"F0.wireOp",EDGE,"E12"),sQuery(id+"F0.wireOp",EDGE,"E13.1.0"),sQuery(id+"F0.wireOp",EDGE,"E13.1.1"),sQuery(id+"F0.wireOp",EDGE,"E13.2.0"),sQuery(id+"F0.wireOp",EDGE,"E13.2.1")])]}),"instanceName":"1"}),"instanceName":"1"}),"instanceName":"1"});
            transform(context, id + "F59", {"entities" : qUnion([Q0]), "transformType" : TransformType.TRANSLATION_3D, "dx" : 0 * mm, "dy" : -7.9 * mm, "dz" : 0 * mm, "makeCopy" : false});
        }
        {
            var Q0;
            Q0=makeQuery(id+"F56.opPattern","COPY",BODY,{"derivedFrom":makeQuery(id+"F18.opPattern","COPY",BODY,{"derivedFrom":makeQuery(id+"F13.opPattern","COPY",BODY,{"derivedFrom":makeQuery(id+"F1.opExtrude","SWEPT_BODY",BODY,{"disambiguationData":[OSD([sQuery(id+"F0.wireOp",EDGE,"E2.0"),sQuery(id+"F0.wireOp",EDGE,"E2.1"),sQuery(id+"F0.wireOp",EDGE,"E2.2"),sQuery(id+"F0.wireOp",EDGE,"E2.3"),sQuery(id+"F0.wireOp",EDGE,"E2.4"),sQuery(id+"F0.wireOp",EDGE,"E2.5"),sQuery(id+"F0.wireOp",EDGE,"E3"),sQuery(id+"F0.wireOp",EDGE,"E4"),sQuery(id+"F0.wireOp",EDGE,"E5.0"),sQuery(id+"F0.wireOp",EDGE,"E5.1"),sQuery(id+"F0.wireOp",EDGE,"E5.3"),sQuery(id+"F0.wireOp",EDGE,"E5.4"),sQuery(id+"F0.wireOp",EDGE,"E5.5"),sQuery(id+"F0.wireOp",EDGE,"E6.trimOffspring"),sQuery(id+"F0.wireOp",EDGE,"E7.trimOffspring"),sQuery(id+"F0.wireOp",EDGE,"E9.trimOffspring"),sQuery(id+"F0.wireOp",EDGE,"E10.1.0"),sQuery(id+"F0.wireOp",EDGE,"E10.1.1"),sQuery(id+"F0.wireOp",EDGE,"E10.1.2"),sQuery(id+"F0.wireOp",EDGE,"E10.1.3"),sQuery(id+"F0.wireOp",EDGE,"E10.1.5"),sQuery(id+"F0.wireOp",EDGE,"E10.1.7"),sQuery(id+"F0.wireOp",EDGE,"E10.1.8"),sQuery(id+"F0.wireOp",EDGE,"E10.1.9"),sQuery(id+"F0.wireOp",EDGE,"E10.1.10"),sQuery(id+"F0.wireOp",EDGE,"E10.1.11"),sQuery(id+"F0.wireOp",EDGE,"E10.1.12"),sQuery(id+"F0.wireOp",EDGE,"E10.1.14"),sQuery(id+"F0.wireOp",EDGE,"E10.1.15"),sQuery(id+"F0.wireOp",EDGE,"E10.1.16"),sQuery(id+"F0.wireOp",EDGE,"E10.1.18"),sQuery(id+"F0.wireOp",EDGE,"E10.1.20"),sQuery(id+"F0.wireOp",EDGE,"E10.2.0"),sQuery(id+"F0.wireOp",EDGE,"E10.2.1"),sQuery(id+"F0.wireOp",EDGE,"E10.2.2"),sQuery(id+"F0.wireOp",EDGE,"E10.2.3"),sQuery(id+"F0.wireOp",EDGE,"E10.2.5"),sQuery(id+"F0.wireOp",EDGE,"E10.2.7"),sQuery(id+"F0.wireOp",EDGE,"E10.2.8"),sQuery(id+"F0.wireOp",EDGE,"E10.2.9"),sQuery(id+"F0.wireOp",EDGE,"E10.2.10"),sQuery(id+"F0.wireOp",EDGE,"E10.2.11"),sQuery(id+"F0.wireOp",EDGE,"E10.2.12"),sQuery(id+"F0.wireOp",EDGE,"E1"),sQuery(id+"F0.wireOp",EDGE,"E10.2.14"),sQuery(id+"F0.wireOp",EDGE,"E10.2.15"),sQuery(id+"F0.wireOp",EDGE,"E10.2.16"),sQuery(id+"F0.wireOp",EDGE,"E10.2.18"),sQuery(id+"F0.wireOp",EDGE,"E10.2.20"),sQuery(id+"F0.wireOp",EDGE,"E8.trimOffspring"),sQuery(id+"F0.wireOp",EDGE,"E0"),sQuery(id+"F0.wireOp",EDGE,"E10.1.6"),sQuery(id+"F0.wireOp",EDGE,"E11"),sQuery(id+"F0.wireOp",EDGE,"E12"),sQuery(id+"F0.wireOp",EDGE,"E13.1.0"),sQuery(id+"F0.wireOp",EDGE,"E13.1.1"),sQuery(id+"F0.wireOp",EDGE,"E13.2.0"),sQuery(id+"F0.wireOp",EDGE,"E13.2.1")])]}),"instanceName":"1"}),"instanceName":"1"}),"instanceName":"1"});
            transform(context, id + "F60", {"entities" : qUnion([Q0]), "transformType" : TransformType.TRANSLATION_3D, "dx" : 0 * mm, "dy" : -3 * mm, "dz" : 0 * mm, "makeCopy" : false});
        }
        {
            var Q0;
            Q0=makeQuery(id+"F56.opPattern","COPY",BODY,{"derivedFrom":makeQuery(id+"F18.opPattern","COPY",BODY,{"derivedFrom":makeQuery(id+"F13.opPattern","COPY",BODY,{"derivedFrom":makeQuery(id+"F1.opExtrude","SWEPT_BODY",BODY,{"disambiguationData":[OSD([sQuery(id+"F0.wireOp",EDGE,"E2.0"),sQuery(id+"F0.wireOp",EDGE,"E2.1"),sQuery(id+"F0.wireOp",EDGE,"E2.2"),sQuery(id+"F0.wireOp",EDGE,"E2.3"),sQuery(id+"F0.wireOp",EDGE,"E2.4"),sQuery(id+"F0.wireOp",EDGE,"E2.5"),sQuery(id+"F0.wireOp",EDGE,"E3"),sQuery(id+"F0.wireOp",EDGE,"E4"),sQuery(id+"F0.wireOp",EDGE,"E5.0"),sQuery(id+"F0.wireOp",EDGE,"E5.1"),sQuery(id+"F0.wireOp",EDGE,"E5.3"),sQuery(id+"F0.wireOp",EDGE,"E5.4"),sQuery(id+"F0.wireOp",EDGE,"E5.5"),sQuery(id+"F0.wireOp",EDGE,"E6.trimOffspring"),sQuery(id+"F0.wireOp",EDGE,"E7.trimOffspring"),sQuery(id+"F0.wireOp",EDGE,"E9.trimOffspring"),sQuery(id+"F0.wireOp",EDGE,"E10.1.0"),sQuery(id+"F0.wireOp",EDGE,"E10.1.1"),sQuery(id+"F0.wireOp",EDGE,"E10.1.2"),sQuery(id+"F0.wireOp",EDGE,"E10.1.3"),sQuery(id+"F0.wireOp",EDGE,"E10.1.5"),sQuery(id+"F0.wireOp",EDGE,"E10.1.7"),sQuery(id+"F0.wireOp",EDGE,"E10.1.8"),sQuery(id+"F0.wireOp",EDGE,"E10.1.9"),sQuery(id+"F0.wireOp",EDGE,"E10.1.10"),sQuery(id+"F0.wireOp",EDGE,"E10.1.11"),sQuery(id+"F0.wireOp",EDGE,"E10.1.12"),sQuery(id+"F0.wireOp",EDGE,"E10.1.14"),sQuery(id+"F0.wireOp",EDGE,"E10.1.15"),sQuery(id+"F0.wireOp",EDGE,"E10.1.16"),sQuery(id+"F0.wireOp",EDGE,"E10.1.18"),sQuery(id+"F0.wireOp",EDGE,"E10.1.20"),sQuery(id+"F0.wireOp",EDGE,"E10.2.0"),sQuery(id+"F0.wireOp",EDGE,"E10.2.1"),sQuery(id+"F0.wireOp",EDGE,"E10.2.2"),sQuery(id+"F0.wireOp",EDGE,"E10.2.3"),sQuery(id+"F0.wireOp",EDGE,"E10.2.5"),sQuery(id+"F0.wireOp",EDGE,"E10.2.7"),sQuery(id+"F0.wireOp",EDGE,"E10.2.8"),sQuery(id+"F0.wireOp",EDGE,"E10.2.9"),sQuery(id+"F0.wireOp",EDGE,"E10.2.10"),sQuery(id+"F0.wireOp",EDGE,"E10.2.11"),sQuery(id+"F0.wireOp",EDGE,"E10.2.12"),sQuery(id+"F0.wireOp",EDGE,"E1"),sQuery(id+"F0.wireOp",EDGE,"E10.2.14"),sQuery(id+"F0.wireOp",EDGE,"E10.2.15"),sQuery(id+"F0.wireOp",EDGE,"E10.2.16"),sQuery(id+"F0.wireOp",EDGE,"E10.2.18"),sQuery(id+"F0.wireOp",EDGE,"E10.2.20"),sQuery(id+"F0.wireOp",EDGE,"E8.trimOffspring"),sQuery(id+"F0.wireOp",EDGE,"E0"),sQuery(id+"F0.wireOp",EDGE,"E10.1.6"),sQuery(id+"F0.wireOp",EDGE,"E11"),sQuery(id+"F0.wireOp",EDGE,"E12"),sQuery(id+"F0.wireOp",EDGE,"E13.1.0"),sQuery(id+"F0.wireOp",EDGE,"E13.1.1"),sQuery(id+"F0.wireOp",EDGE,"E13.2.0"),sQuery(id+"F0.wireOp",EDGE,"E13.2.1")])]}),"instanceName":"1"}),"instanceName":"1"}),"instanceName":"1"});
            transform(context, id + "F61", {"entities" : qUnion([Q0]), "transformType" : TransformType.TRANSLATION_3D, "dx" : 0 * mm, "dy" : -2 * mm, "dz" : 0 * mm, "makeCopy" : false});
        }
        {
            var Q0;
            Q0=makeQuery(id+"F56.opPattern","COPY",BODY,{"derivedFrom":makeQuery(id+"F19.opPattern","COPY",BODY,{"derivedFrom":makeQuery(id+"F18.opPattern","COPY",BODY,{"derivedFrom":makeQuery(id+"F13.opPattern","COPY",BODY,{"derivedFrom":makeQuery(id+"F1.opExtrude","SWEPT_BODY",BODY,{"disambiguationData":[OSD([sQuery(id+"F0.wireOp",EDGE,"E2.0"),sQuery(id+"F0.wireOp",EDGE,"E2.1"),sQuery(id+"F0.wireOp",EDGE,"E2.2"),sQuery(id+"F0.wireOp",EDGE,"E2.3"),sQuery(id+"F0.wireOp",EDGE,"E2.4"),sQuery(id+"F0.wireOp",EDGE,"E2.5"),sQuery(id+"F0.wireOp",EDGE,"E3"),sQuery(id+"F0.wireOp",EDGE,"E4"),sQuery(id+"F0.wireOp",EDGE,"E5.0"),sQuery(id+"F0.wireOp",EDGE,"E5.1"),sQuery(id+"F0.wireOp",EDGE,"E5.3"),sQuery(id+"F0.wireOp",EDGE,"E5.4"),sQuery(id+"F0.wireOp",EDGE,"E5.5"),sQuery(id+"F0.wireOp",EDGE,"E6.trimOffspring"),sQuery(id+"F0.wireOp",EDGE,"E7.trimOffspring"),sQuery(id+"F0.wireOp",EDGE,"E9.trimOffspring"),sQuery(id+"F0.wireOp",EDGE,"E10.1.0"),sQuery(id+"F0.wireOp",EDGE,"E10.1.1"),sQuery(id+"F0.wireOp",EDGE,"E10.1.2"),sQuery(id+"F0.wireOp",EDGE,"E10.1.3"),sQuery(id+"F0.wireOp",EDGE,"E10.1.5"),sQuery(id+"F0.wireOp",EDGE,"E10.1.7"),sQuery(id+"F0.wireOp",EDGE,"E10.1.8"),sQuery(id+"F0.wireOp",EDGE,"E10.1.9"),sQuery(id+"F0.wireOp",EDGE,"E10.1.10"),sQuery(id+"F0.wireOp",EDGE,"E10.1.11"),sQuery(id+"F0.wireOp",EDGE,"E10.1.12"),sQuery(id+"F0.wireOp",EDGE,"E10.1.14"),sQuery(id+"F0.wireOp",EDGE,"E10.1.15"),sQuery(id+"F0.wireOp",EDGE,"E10.1.16"),sQuery(id+"F0.wireOp",EDGE,"E10.1.18"),sQuery(id+"F0.wireOp",EDGE,"E10.1.20"),sQuery(id+"F0.wireOp",EDGE,"E10.2.0"),sQuery(id+"F0.wireOp",EDGE,"E10.2.1"),sQuery(id+"F0.wireOp",EDGE,"E10.2.2"),sQuery(id+"F0.wireOp",EDGE,"E10.2.3"),sQuery(id+"F0.wireOp",EDGE,"E10.2.5"),sQuery(id+"F0.wireOp",EDGE,"E10.2.7"),sQuery(id+"F0.wireOp",EDGE,"E10.2.8"),sQuery(id+"F0.wireOp",EDGE,"E10.2.9"),sQuery(id+"F0.wireOp",EDGE,"E10.2.10"),sQuery(id+"F0.wireOp",EDGE,"E10.2.11"),sQuery(id+"F0.wireOp",EDGE,"E10.2.12"),sQuery(id+"F0.wireOp",EDGE,"E1"),sQuery(id+"F0.wireOp",EDGE,"E10.2.14"),sQuery(id+"F0.wireOp",EDGE,"E10.2.15"),sQuery(id+"F0.wireOp",EDGE,"E10.2.16"),sQuery(id+"F0.wireOp",EDGE,"E10.2.18"),sQuery(id+"F0.wireOp",EDGE,"E10.2.20"),sQuery(id+"F0.wireOp",EDGE,"E8.trimOffspring"),sQuery(id+"F0.wireOp",EDGE,"E0"),sQuery(id+"F0.wireOp",EDGE,"E10.1.6"),sQuery(id+"F0.wireOp",EDGE,"E11"),sQuery(id+"F0.wireOp",EDGE,"E12"),sQuery(id+"F0.wireOp",EDGE,"E13.1.0"),sQuery(id+"F0.wireOp",EDGE,"E13.1.1"),sQuery(id+"F0.wireOp",EDGE,"E13.2.0"),sQuery(id+"F0.wireOp",EDGE,"E13.2.1")])]}),"instanceName":"1"}),"instanceName":"1"}),"instanceName":"1"}),"instanceName":"1"});
            transform(context, id + "F62", {"entities" : qUnion([Q0]), "transformType" : TransformType.TRANSLATION_3D, "dx" : 0.8 * mm, "dy" : -9 * mm, "dz" : 0 * mm, "makeCopy" : false});
        }
        {
            var Q0;
            Q0=makeQuery(id+"F47.opPattern","COPY",BODY,{"derivedFrom":makeQuery(id+"F42.opPattern","COPY",BODY,{"derivedFrom":makeQuery(id+"F13.opPattern","COPY",BODY,{"derivedFrom":makeQuery(id+"F1.opExtrude","SWEPT_BODY",BODY,{"disambiguationData":[OSD([sQuery(id+"F0.wireOp",EDGE,"E2.0"),sQuery(id+"F0.wireOp",EDGE,"E2.1"),sQuery(id+"F0.wireOp",EDGE,"E2.2"),sQuery(id+"F0.wireOp",EDGE,"E2.3"),sQuery(id+"F0.wireOp",EDGE,"E2.4"),sQuery(id+"F0.wireOp",EDGE,"E2.5"),sQuery(id+"F0.wireOp",EDGE,"E3"),sQuery(id+"F0.wireOp",EDGE,"E4"),sQuery(id+"F0.wireOp",EDGE,"E5.0"),sQuery(id+"F0.wireOp",EDGE,"E5.1"),sQuery(id+"F0.wireOp",EDGE,"E5.3"),sQuery(id+"F0.wireOp",EDGE,"E5.4"),sQuery(id+"F0.wireOp",EDGE,"E5.5"),sQuery(id+"F0.wireOp",EDGE,"E6.trimOffspring"),sQuery(id+"F0.wireOp",EDGE,"E7.trimOffspring"),sQuery(id+"F0.wireOp",EDGE,"E9.trimOffspring"),sQuery(id+"F0.wireOp",EDGE,"E10.1.0"),sQuery(id+"F0.wireOp",EDGE,"E10.1.1"),sQuery(id+"F0.wireOp",EDGE,"E10.1.2"),sQuery(id+"F0.wireOp",EDGE,"E10.1.3"),sQuery(id+"F0.wireOp",EDGE,"E10.1.5"),sQuery(id+"F0.wireOp",EDGE,"E10.1.7"),sQuery(id+"F0.wireOp",EDGE,"E10.1.8"),sQuery(id+"F0.wireOp",EDGE,"E10.1.9"),sQuery(id+"F0.wireOp",EDGE,"E10.1.10"),sQuery(id+"F0.wireOp",EDGE,"E10.1.11"),sQuery(id+"F0.wireOp",EDGE,"E10.1.12"),sQuery(id+"F0.wireOp",EDGE,"E10.1.14"),sQuery(id+"F0.wireOp",EDGE,"E10.1.15"),sQuery(id+"F0.wireOp",EDGE,"E10.1.16"),sQuery(id+"F0.wireOp",EDGE,"E10.1.18"),sQuery(id+"F0.wireOp",EDGE,"E10.1.20"),sQuery(id+"F0.wireOp",EDGE,"E10.2.0"),sQuery(id+"F0.wireOp",EDGE,"E10.2.1"),sQuery(id+"F0.wireOp",EDGE,"E10.2.2"),sQuery(id+"F0.wireOp",EDGE,"E10.2.3"),sQuery(id+"F0.wireOp",EDGE,"E10.2.5"),sQuery(id+"F0.wireOp",EDGE,"E10.2.7"),sQuery(id+"F0.wireOp",EDGE,"E10.2.8"),sQuery(id+"F0.wireOp",EDGE,"E10.2.9"),sQuery(id+"F0.wireOp",EDGE,"E10.2.10"),sQuery(id+"F0.wireOp",EDGE,"E10.2.11"),sQuery(id+"F0.wireOp",EDGE,"E10.2.12"),sQuery(id+"F0.wireOp",EDGE,"E1"),sQuery(id+"F0.wireOp",EDGE,"E10.2.14"),sQuery(id+"F0.wireOp",EDGE,"E10.2.15"),sQuery(id+"F0.wireOp",EDGE,"E10.2.16"),sQuery(id+"F0.wireOp",EDGE,"E10.2.18"),sQuery(id+"F0.wireOp",EDGE,"E10.2.20"),sQuery(id+"F0.wireOp",EDGE,"E8.trimOffspring"),sQuery(id+"F0.wireOp",EDGE,"E0"),sQuery(id+"F0.wireOp",EDGE,"E10.1.6"),sQuery(id+"F0.wireOp",EDGE,"E11"),sQuery(id+"F0.wireOp",EDGE,"E12"),sQuery(id+"F0.wireOp",EDGE,"E13.1.0"),sQuery(id+"F0.wireOp",EDGE,"E13.1.1"),sQuery(id+"F0.wireOp",EDGE,"E13.2.0"),sQuery(id+"F0.wireOp",EDGE,"E13.2.1")])]}),"instanceName":"1"}),"instanceName":"1"}),"instanceName":"1"});
            transform(context, id + "F63", {"entities" : qUnion([Q0]), "transformType" : TransformType.TRANSLATION_3D, "dx" : 30.5 * mm, "dy" : -98.2 * mm, "dz" : 0 * mm, "makeCopy" : true});
        }
        {
            var Q0;
            Q0=makeQuery(id+"F48.opPattern","COPY",BODY,{"derivedFrom":makeQuery(id+"F39.opPattern","COPY",BODY,{"derivedFrom":makeQuery(id+"F36.opPattern","COPY",BODY,{"derivedFrom":makeQuery(id+"F23.opPattern","COPY",BODY,{"derivedFrom":makeQuery(id+"F7.opPattern","COPY",BODY,{"derivedFrom":makeQuery(id+"F1.opExtrude","SWEPT_BODY",BODY,{"disambiguationData":[OSD([sQuery(id+"F0.wireOp",EDGE,"E2.0"),sQuery(id+"F0.wireOp",EDGE,"E2.1"),sQuery(id+"F0.wireOp",EDGE,"E2.2"),sQuery(id+"F0.wireOp",EDGE,"E2.3"),sQuery(id+"F0.wireOp",EDGE,"E2.4"),sQuery(id+"F0.wireOp",EDGE,"E2.5"),sQuery(id+"F0.wireOp",EDGE,"E3"),sQuery(id+"F0.wireOp",EDGE,"E4"),sQuery(id+"F0.wireOp",EDGE,"E5.0"),sQuery(id+"F0.wireOp",EDGE,"E5.1"),sQuery(id+"F0.wireOp",EDGE,"E5.3"),sQuery(id+"F0.wireOp",EDGE,"E5.4"),sQuery(id+"F0.wireOp",EDGE,"E5.5"),sQuery(id+"F0.wireOp",EDGE,"E6.trimOffspring"),sQuery(id+"F0.wireOp",EDGE,"E7.trimOffspring"),sQuery(id+"F0.wireOp",EDGE,"E9.trimOffspring"),sQuery(id+"F0.wireOp",EDGE,"E10.1.0"),sQuery(id+"F0.wireOp",EDGE,"E10.1.1"),sQuery(id+"F0.wireOp",EDGE,"E10.1.2"),sQuery(id+"F0.wireOp",EDGE,"E10.1.3"),sQuery(id+"F0.wireOp",EDGE,"E10.1.5"),sQuery(id+"F0.wireOp",EDGE,"E10.1.7"),sQuery(id+"F0.wireOp",EDGE,"E10.1.8"),sQuery(id+"F0.wireOp",EDGE,"E10.1.9"),sQuery(id+"F0.wireOp",EDGE,"E10.1.10"),sQuery(id+"F0.wireOp",EDGE,"E10.1.11"),sQuery(id+"F0.wireOp",EDGE,"E10.1.12"),sQuery(id+"F0.wireOp",EDGE,"E10.1.14"),sQuery(id+"F0.wireOp",EDGE,"E10.1.15"),sQuery(id+"F0.wireOp",EDGE,"E10.1.16"),sQuery(id+"F0.wireOp",EDGE,"E10.1.18"),sQuery(id+"F0.wireOp",EDGE,"E10.1.20"),sQuery(id+"F0.wireOp",EDGE,"E10.2.0"),sQuery(id+"F0.wireOp",EDGE,"E10.2.1"),sQuery(id+"F0.wireOp",EDGE,"E10.2.2"),sQuery(id+"F0.wireOp",EDGE,"E10.2.3"),sQuery(id+"F0.wireOp",EDGE,"E10.2.5"),sQuery(id+"F0.wireOp",EDGE,"E10.2.7"),sQuery(id+"F0.wireOp",EDGE,"E10.2.8"),sQuery(id+"F0.wireOp",EDGE,"E10.2.9"),sQuery(id+"F0.wireOp",EDGE,"E10.2.10"),sQuery(id+"F0.wireOp",EDGE,"E10.2.11"),sQuery(id+"F0.wireOp",EDGE,"E10.2.12"),sQuery(id+"F0.wireOp",EDGE,"E1"),sQuery(id+"F0.wireOp",EDGE,"E10.2.14"),sQuery(id+"F0.wireOp",EDGE,"E10.2.15"),sQuery(id+"F0.wireOp",EDGE,"E10.2.16"),sQuery(id+"F0.wireOp",EDGE,"E10.2.18"),sQuery(id+"F0.wireOp",EDGE,"E10.2.20"),sQuery(id+"F0.wireOp",EDGE,"E8.trimOffspring"),sQuery(id+"F0.wireOp",EDGE,"E0"),sQuery(id+"F0.wireOp",EDGE,"E10.1.6"),sQuery(id+"F0.wireOp",EDGE,"E11"),sQuery(id+"F0.wireOp",EDGE,"E12"),sQuery(id+"F0.wireOp",EDGE,"E13.1.0"),sQuery(id+"F0.wireOp",EDGE,"E13.1.1"),sQuery(id+"F0.wireOp",EDGE,"E13.2.0"),sQuery(id+"F0.wireOp",EDGE,"E13.2.1")])]}),"instanceName":"1"}),"instanceName":"1"}),"instanceName":"1"}),"instanceName":"1"}),"instanceName":"1"});
            transform(context, id + "F64", {"entities" : qUnion([Q0]), "transformType" : TransformType.TRANSLATION_3D, "dx" : 0 * mm, "dy" : -84.1 * mm, "dz" : 0 * mm, "makeCopy" : true});
        }
        {
            var Q0;
            Q0=makeQuery(id+"F48.opPattern","COPY",BODY,{"derivedFrom":makeQuery(id+"F39.opPattern","COPY",BODY,{"derivedFrom":makeQuery(id+"F36.opPattern","COPY",BODY,{"derivedFrom":makeQuery(id+"F23.opPattern","COPY",BODY,{"derivedFrom":makeQuery(id+"F7.opPattern","COPY",BODY,{"derivedFrom":makeQuery(id+"F1.opExtrude","SWEPT_BODY",BODY,{"disambiguationData":[OSD([sQuery(id+"F0.wireOp",EDGE,"E2.0"),sQuery(id+"F0.wireOp",EDGE,"E2.1"),sQuery(id+"F0.wireOp",EDGE,"E2.2"),sQuery(id+"F0.wireOp",EDGE,"E2.3"),sQuery(id+"F0.wireOp",EDGE,"E2.4"),sQuery(id+"F0.wireOp",EDGE,"E2.5"),sQuery(id+"F0.wireOp",EDGE,"E3"),sQuery(id+"F0.wireOp",EDGE,"E4"),sQuery(id+"F0.wireOp",EDGE,"E5.0"),sQuery(id+"F0.wireOp",EDGE,"E5.1"),sQuery(id+"F0.wireOp",EDGE,"E5.3"),sQuery(id+"F0.wireOp",EDGE,"E5.4"),sQuery(id+"F0.wireOp",EDGE,"E5.5"),sQuery(id+"F0.wireOp",EDGE,"E6.trimOffspring"),sQuery(id+"F0.wireOp",EDGE,"E7.trimOffspring"),sQuery(id+"F0.wireOp",EDGE,"E9.trimOffspring"),sQuery(id+"F0.wireOp",EDGE,"E10.1.0"),sQuery(id+"F0.wireOp",EDGE,"E10.1.1"),sQuery(id+"F0.wireOp",EDGE,"E10.1.2"),sQuery(id+"F0.wireOp",EDGE,"E10.1.3"),sQuery(id+"F0.wireOp",EDGE,"E10.1.5"),sQuery(id+"F0.wireOp",EDGE,"E10.1.7"),sQuery(id+"F0.wireOp",EDGE,"E10.1.8"),sQuery(id+"F0.wireOp",EDGE,"E10.1.9"),sQuery(id+"F0.wireOp",EDGE,"E10.1.10"),sQuery(id+"F0.wireOp",EDGE,"E10.1.11"),sQuery(id+"F0.wireOp",EDGE,"E10.1.12"),sQuery(id+"F0.wireOp",EDGE,"E10.1.14"),sQuery(id+"F0.wireOp",EDGE,"E10.1.15"),sQuery(id+"F0.wireOp",EDGE,"E10.1.16"),sQuery(id+"F0.wireOp",EDGE,"E10.1.18"),sQuery(id+"F0.wireOp",EDGE,"E10.1.20"),sQuery(id+"F0.wireOp",EDGE,"E10.2.0"),sQuery(id+"F0.wireOp",EDGE,"E10.2.1"),sQuery(id+"F0.wireOp",EDGE,"E10.2.2"),sQuery(id+"F0.wireOp",EDGE,"E10.2.3"),sQuery(id+"F0.wireOp",EDGE,"E10.2.5"),sQuery(id+"F0.wireOp",EDGE,"E10.2.7"),sQuery(id+"F0.wireOp",EDGE,"E10.2.8"),sQuery(id+"F0.wireOp",EDGE,"E10.2.9"),sQuery(id+"F0.wireOp",EDGE,"E10.2.10"),sQuery(id+"F0.wireOp",EDGE,"E10.2.11"),sQuery(id+"F0.wireOp",EDGE,"E10.2.12"),sQuery(id+"F0.wireOp",EDGE,"E1"),sQuery(id+"F0.wireOp",EDGE,"E10.2.14"),sQuery(id+"F0.wireOp",EDGE,"E10.2.15"),sQuery(id+"F0.wireOp",EDGE,"E10.2.16"),sQuery(id+"F0.wireOp",EDGE,"E10.2.18"),sQuery(id+"F0.wireOp",EDGE,"E10.2.20"),sQuery(id+"F0.wireOp",EDGE,"E8.trimOffspring"),sQuery(id+"F0.wireOp",EDGE,"E0"),sQuery(id+"F0.wireOp",EDGE,"E10.1.6"),sQuery(id+"F0.wireOp",EDGE,"E11"),sQuery(id+"F0.wireOp",EDGE,"E12"),sQuery(id+"F0.wireOp",EDGE,"E13.1.0"),sQuery(id+"F0.wireOp",EDGE,"E13.1.1"),sQuery(id+"F0.wireOp",EDGE,"E13.2.0"),sQuery(id+"F0.wireOp",EDGE,"E13.2.1")])]}),"instanceName":"1"}),"instanceName":"1"}),"instanceName":"1"}),"instanceName":"1"}),"instanceName":"1"});
            transform(context, id + "F65", {"entities" : qUnion([Q0]), "transformType" : TransformType.TRANSLATION_3D, "dx" : -1 * mm, "dy" : 0 * mm, "dz" : 0 * mm, "makeCopy" : false});
        }
        {
            var Q0;
            Q0=makeQuery(id+"F48.opPattern","COPY",BODY,{"derivedFrom":makeQuery(id+"F39.opPattern","COPY",BODY,{"derivedFrom":makeQuery(id+"F36.opPattern","COPY",BODY,{"derivedFrom":makeQuery(id+"F23.opPattern","COPY",BODY,{"derivedFrom":makeQuery(id+"F7.opPattern","COPY",BODY,{"derivedFrom":makeQuery(id+"F1.opExtrude","SWEPT_BODY",BODY,{"disambiguationData":[OSD([sQuery(id+"F0.wireOp",EDGE,"E2.0"),sQuery(id+"F0.wireOp",EDGE,"E2.1"),sQuery(id+"F0.wireOp",EDGE,"E2.2"),sQuery(id+"F0.wireOp",EDGE,"E2.3"),sQuery(id+"F0.wireOp",EDGE,"E2.4"),sQuery(id+"F0.wireOp",EDGE,"E2.5"),sQuery(id+"F0.wireOp",EDGE,"E3"),sQuery(id+"F0.wireOp",EDGE,"E4"),sQuery(id+"F0.wireOp",EDGE,"E5.0"),sQuery(id+"F0.wireOp",EDGE,"E5.1"),sQuery(id+"F0.wireOp",EDGE,"E5.3"),sQuery(id+"F0.wireOp",EDGE,"E5.4"),sQuery(id+"F0.wireOp",EDGE,"E5.5"),sQuery(id+"F0.wireOp",EDGE,"E6.trimOffspring"),sQuery(id+"F0.wireOp",EDGE,"E7.trimOffspring"),sQuery(id+"F0.wireOp",EDGE,"E9.trimOffspring"),sQuery(id+"F0.wireOp",EDGE,"E10.1.0"),sQuery(id+"F0.wireOp",EDGE,"E10.1.1"),sQuery(id+"F0.wireOp",EDGE,"E10.1.2"),sQuery(id+"F0.wireOp",EDGE,"E10.1.3"),sQuery(id+"F0.wireOp",EDGE,"E10.1.5"),sQuery(id+"F0.wireOp",EDGE,"E10.1.7"),sQuery(id+"F0.wireOp",EDGE,"E10.1.8"),sQuery(id+"F0.wireOp",EDGE,"E10.1.9"),sQuery(id+"F0.wireOp",EDGE,"E10.1.10"),sQuery(id+"F0.wireOp",EDGE,"E10.1.11"),sQuery(id+"F0.wireOp",EDGE,"E10.1.12"),sQuery(id+"F0.wireOp",EDGE,"E10.1.14"),sQuery(id+"F0.wireOp",EDGE,"E10.1.15"),sQuery(id+"F0.wireOp",EDGE,"E10.1.16"),sQuery(id+"F0.wireOp",EDGE,"E10.1.18"),sQuery(id+"F0.wireOp",EDGE,"E10.1.20"),sQuery(id+"F0.wireOp",EDGE,"E10.2.0"),sQuery(id+"F0.wireOp",EDGE,"E10.2.1"),sQuery(id+"F0.wireOp",EDGE,"E10.2.2"),sQuery(id+"F0.wireOp",EDGE,"E10.2.3"),sQuery(id+"F0.wireOp",EDGE,"E10.2.5"),sQuery(id+"F0.wireOp",EDGE,"E10.2.7"),sQuery(id+"F0.wireOp",EDGE,"E10.2.8"),sQuery(id+"F0.wireOp",EDGE,"E10.2.9"),sQuery(id+"F0.wireOp",EDGE,"E10.2.10"),sQuery(id+"F0.wireOp",EDGE,"E10.2.11"),sQuery(id+"F0.wireOp",EDGE,"E10.2.12"),sQuery(id+"F0.wireOp",EDGE,"E1"),sQuery(id+"F0.wireOp",EDGE,"E10.2.14"),sQuery(id+"F0.wireOp",EDGE,"E10.2.15"),sQuery(id+"F0.wireOp",EDGE,"E10.2.16"),sQuery(id+"F0.wireOp",EDGE,"E10.2.18"),sQuery(id+"F0.wireOp",EDGE,"E10.2.20"),sQuery(id+"F0.wireOp",EDGE,"E8.trimOffspring"),sQuery(id+"F0.wireOp",EDGE,"E0"),sQuery(id+"F0.wireOp",EDGE,"E10.1.6"),sQuery(id+"F0.wireOp",EDGE,"E11"),sQuery(id+"F0.wireOp",EDGE,"E12"),sQuery(id+"F0.wireOp",EDGE,"E13.1.0"),sQuery(id+"F0.wireOp",EDGE,"E13.1.1"),sQuery(id+"F0.wireOp",EDGE,"E13.2.0"),sQuery(id+"F0.wireOp",EDGE,"E13.2.1")])]}),"instanceName":"1"}),"instanceName":"1"}),"instanceName":"1"}),"instanceName":"1"}),"instanceName":"1"});
            var Q1;
            Q1=makeQuery(id+"F48.opPattern","COPY",EDGE,{"derivedFrom":makeQuery(id+"F39.opPattern","COPY",EDGE,{"derivedFrom":makeQuery(id+"F36.opPattern","COPY",EDGE,{"derivedFrom":makeQuery(id+"F23.opPattern","COPY",EDGE,{"derivedFrom":makeQuery(id+"F7.opPattern","COPY",EDGE,{"derivedFrom":makeQuery(id+"F1.opExtrude","CAP_EDGE",EDGE,{"disambiguationData":[OSD([sQuery(id+"F0.wireOp",EDGE,"E1")])],"isStart":false}),"instanceName":"1"}),"instanceName":"1"}),"instanceName":"1"}),"instanceName":"1"}),"instanceName":"1"});
            transform(context, id + "F66", {"entities" : qUnion([Q0]), "transformType" : TransformType.ROTATION, "transformAxis" : qUnion([Q1]), "angle" : 10 * degree, "oppositeDirection" : true, "makeCopy" : false});
        }
        {
            var Q0;
            Q0=makeQuery(id+"F51.opPattern","COPY",BODY,{"derivedFrom":makeQuery(id+"F39.opPattern","COPY",BODY,{"derivedFrom":makeQuery(id+"F36.opPattern","COPY",BODY,{"derivedFrom":makeQuery(id+"F23.opPattern","COPY",BODY,{"derivedFrom":makeQuery(id+"F7.opPattern","COPY",BODY,{"derivedFrom":makeQuery(id+"F1.opExtrude","SWEPT_BODY",BODY,{"disambiguationData":[OSD([sQuery(id+"F0.wireOp",EDGE,"E2.0"),sQuery(id+"F0.wireOp",EDGE,"E2.1"),sQuery(id+"F0.wireOp",EDGE,"E2.2"),sQuery(id+"F0.wireOp",EDGE,"E2.3"),sQuery(id+"F0.wireOp",EDGE,"E2.4"),sQuery(id+"F0.wireOp",EDGE,"E2.5"),sQuery(id+"F0.wireOp",EDGE,"E3"),sQuery(id+"F0.wireOp",EDGE,"E4"),sQuery(id+"F0.wireOp",EDGE,"E5.0"),sQuery(id+"F0.wireOp",EDGE,"E5.1"),sQuery(id+"F0.wireOp",EDGE,"E5.3"),sQuery(id+"F0.wireOp",EDGE,"E5.4"),sQuery(id+"F0.wireOp",EDGE,"E5.5"),sQuery(id+"F0.wireOp",EDGE,"E6.trimOffspring"),sQuery(id+"F0.wireOp",EDGE,"E7.trimOffspring"),sQuery(id+"F0.wireOp",EDGE,"E9.trimOffspring"),sQuery(id+"F0.wireOp",EDGE,"E10.1.0"),sQuery(id+"F0.wireOp",EDGE,"E10.1.1"),sQuery(id+"F0.wireOp",EDGE,"E10.1.2"),sQuery(id+"F0.wireOp",EDGE,"E10.1.3"),sQuery(id+"F0.wireOp",EDGE,"E10.1.5"),sQuery(id+"F0.wireOp",EDGE,"E10.1.7"),sQuery(id+"F0.wireOp",EDGE,"E10.1.8"),sQuery(id+"F0.wireOp",EDGE,"E10.1.9"),sQuery(id+"F0.wireOp",EDGE,"E10.1.10"),sQuery(id+"F0.wireOp",EDGE,"E10.1.11"),sQuery(id+"F0.wireOp",EDGE,"E10.1.12"),sQuery(id+"F0.wireOp",EDGE,"E10.1.14"),sQuery(id+"F0.wireOp",EDGE,"E10.1.15"),sQuery(id+"F0.wireOp",EDGE,"E10.1.16"),sQuery(id+"F0.wireOp",EDGE,"E10.1.18"),sQuery(id+"F0.wireOp",EDGE,"E10.1.20"),sQuery(id+"F0.wireOp",EDGE,"E10.2.0"),sQuery(id+"F0.wireOp",EDGE,"E10.2.1"),sQuery(id+"F0.wireOp",EDGE,"E10.2.2"),sQuery(id+"F0.wireOp",EDGE,"E10.2.3"),sQuery(id+"F0.wireOp",EDGE,"E10.2.5"),sQuery(id+"F0.wireOp",EDGE,"E10.2.7"),sQuery(id+"F0.wireOp",EDGE,"E10.2.8"),sQuery(id+"F0.wireOp",EDGE,"E10.2.9"),sQuery(id+"F0.wireOp",EDGE,"E10.2.10"),sQuery(id+"F0.wireOp",EDGE,"E10.2.11"),sQuery(id+"F0.wireOp",EDGE,"E10.2.12"),sQuery(id+"F0.wireOp",EDGE,"E1"),sQuery(id+"F0.wireOp",EDGE,"E10.2.14"),sQuery(id+"F0.wireOp",EDGE,"E10.2.15"),sQuery(id+"F0.wireOp",EDGE,"E10.2.16"),sQuery(id+"F0.wireOp",EDGE,"E10.2.18"),sQuery(id+"F0.wireOp",EDGE,"E10.2.20"),sQuery(id+"F0.wireOp",EDGE,"E8.trimOffspring"),sQuery(id+"F0.wireOp",EDGE,"E0"),sQuery(id+"F0.wireOp",EDGE,"E10.1.6"),sQuery(id+"F0.wireOp",EDGE,"E11"),sQuery(id+"F0.wireOp",EDGE,"E12"),sQuery(id+"F0.wireOp",EDGE,"E13.1.0"),sQuery(id+"F0.wireOp",EDGE,"E13.1.1"),sQuery(id+"F0.wireOp",EDGE,"E13.2.0"),sQuery(id+"F0.wireOp",EDGE,"E13.2.1")])]}),"instanceName":"1"}),"instanceName":"1"}),"instanceName":"1"}),"instanceName":"1"}),"instanceName":"1"});
            transform(context, id + "F67", {"entities" : qUnion([Q0]), "transformType" : TransformType.TRANSLATION_3D, "dx" : 34 * mm, "dy" : -107 * mm, "dz" : 0 * mm, "makeCopy" : true});
        }
        {
            var Q0;
            Q0=makeQuery(id+"F13.opPattern","COPY",BODY,{"derivedFrom":makeQuery(id+"F1.opExtrude","SWEPT_BODY",BODY,{"disambiguationData":[OSD([sQuery(id+"F0.wireOp",EDGE,"E2.0"),sQuery(id+"F0.wireOp",EDGE,"E2.1"),sQuery(id+"F0.wireOp",EDGE,"E2.2"),sQuery(id+"F0.wireOp",EDGE,"E2.3"),sQuery(id+"F0.wireOp",EDGE,"E2.4"),sQuery(id+"F0.wireOp",EDGE,"E2.5"),sQuery(id+"F0.wireOp",EDGE,"E3"),sQuery(id+"F0.wireOp",EDGE,"E4"),sQuery(id+"F0.wireOp",EDGE,"E5.0"),sQuery(id+"F0.wireOp",EDGE,"E5.1"),sQuery(id+"F0.wireOp",EDGE,"E5.3"),sQuery(id+"F0.wireOp",EDGE,"E5.4"),sQuery(id+"F0.wireOp",EDGE,"E5.5"),sQuery(id+"F0.wireOp",EDGE,"E6.trimOffspring"),sQuery(id+"F0.wireOp",EDGE,"E7.trimOffspring"),sQuery(id+"F0.wireOp",EDGE,"E9.trimOffspring"),sQuery(id+"F0.wireOp",EDGE,"E10.1.0"),sQuery(id+"F0.wireOp",EDGE,"E10.1.1"),sQuery(id+"F0.wireOp",EDGE,"E10.1.2"),sQuery(id+"F0.wireOp",EDGE,"E10.1.3"),sQuery(id+"F0.wireOp",EDGE,"E10.1.5"),sQuery(id+"F0.wireOp",EDGE,"E10.1.7"),sQuery(id+"F0.wireOp",EDGE,"E10.1.8"),sQuery(id+"F0.wireOp",EDGE,"E10.1.9"),sQuery(id+"F0.wireOp",EDGE,"E10.1.10"),sQuery(id+"F0.wireOp",EDGE,"E10.1.11"),sQuery(id+"F0.wireOp",EDGE,"E10.1.12"),sQuery(id+"F0.wireOp",EDGE,"E10.1.14"),sQuery(id+"F0.wireOp",EDGE,"E10.1.15"),sQuery(id+"F0.wireOp",EDGE,"E10.1.16"),sQuery(id+"F0.wireOp",EDGE,"E10.1.18"),sQuery(id+"F0.wireOp",EDGE,"E10.1.20"),sQuery(id+"F0.wireOp",EDGE,"E10.2.0"),sQuery(id+"F0.wireOp",EDGE,"E10.2.1"),sQuery(id+"F0.wireOp",EDGE,"E10.2.2"),sQuery(id+"F0.wireOp",EDGE,"E10.2.3"),sQuery(id+"F0.wireOp",EDGE,"E10.2.5"),sQuery(id+"F0.wireOp",EDGE,"E10.2.7"),sQuery(id+"F0.wireOp",EDGE,"E10.2.8"),sQuery(id+"F0.wireOp",EDGE,"E10.2.9"),sQuery(id+"F0.wireOp",EDGE,"E10.2.10"),sQuery(id+"F0.wireOp",EDGE,"E10.2.11"),sQuery(id+"F0.wireOp",EDGE,"E10.2.12"),sQuery(id+"F0.wireOp",EDGE,"E1"),sQuery(id+"F0.wireOp",EDGE,"E10.2.14"),sQuery(id+"F0.wireOp",EDGE,"E10.2.15"),sQuery(id+"F0.wireOp",EDGE,"E10.2.16"),sQuery(id+"F0.wireOp",EDGE,"E10.2.18"),sQuery(id+"F0.wireOp",EDGE,"E10.2.20"),sQuery(id+"F0.wireOp",EDGE,"E8.trimOffspring"),sQuery(id+"F0.wireOp",EDGE,"E0"),sQuery(id+"F0.wireOp",EDGE,"E10.1.6"),sQuery(id+"F0.wireOp",EDGE,"E11"),sQuery(id+"F0.wireOp",EDGE,"E12"),sQuery(id+"F0.wireOp",EDGE,"E13.1.0"),sQuery(id+"F0.wireOp",EDGE,"E13.1.1"),sQuery(id+"F0.wireOp",EDGE,"E13.2.0"),sQuery(id+"F0.wireOp",EDGE,"E13.2.1")])]}),"instanceName":"1"});
            var Q1;
            Q1=makeQuery(id+"F18.opPattern","COPY",BODY,{"derivedFrom":makeQuery(id+"F13.opPattern","COPY",BODY,{"derivedFrom":makeQuery(id+"F1.opExtrude","SWEPT_BODY",BODY,{"disambiguationData":[OSD([sQuery(id+"F0.wireOp",EDGE,"E2.0"),sQuery(id+"F0.wireOp",EDGE,"E2.1"),sQuery(id+"F0.wireOp",EDGE,"E2.2"),sQuery(id+"F0.wireOp",EDGE,"E2.3"),sQuery(id+"F0.wireOp",EDGE,"E2.4"),sQuery(id+"F0.wireOp",EDGE,"E2.5"),sQuery(id+"F0.wireOp",EDGE,"E3"),sQuery(id+"F0.wireOp",EDGE,"E4"),sQuery(id+"F0.wireOp",EDGE,"E5.0"),sQuery(id+"F0.wireOp",EDGE,"E5.1"),sQuery(id+"F0.wireOp",EDGE,"E5.3"),sQuery(id+"F0.wireOp",EDGE,"E5.4"),sQuery(id+"F0.wireOp",EDGE,"E5.5"),sQuery(id+"F0.wireOp",EDGE,"E6.trimOffspring"),sQuery(id+"F0.wireOp",EDGE,"E7.trimOffspring"),sQuery(id+"F0.wireOp",EDGE,"E9.trimOffspring"),sQuery(id+"F0.wireOp",EDGE,"E10.1.0"),sQuery(id+"F0.wireOp",EDGE,"E10.1.1"),sQuery(id+"F0.wireOp",EDGE,"E10.1.2"),sQuery(id+"F0.wireOp",EDGE,"E10.1.3"),sQuery(id+"F0.wireOp",EDGE,"E10.1.5"),sQuery(id+"F0.wireOp",EDGE,"E10.1.7"),sQuery(id+"F0.wireOp",EDGE,"E10.1.8"),sQuery(id+"F0.wireOp",EDGE,"E10.1.9"),sQuery(id+"F0.wireOp",EDGE,"E10.1.10"),sQuery(id+"F0.wireOp",EDGE,"E10.1.11"),sQuery(id+"F0.wireOp",EDGE,"E10.1.12"),sQuery(id+"F0.wireOp",EDGE,"E10.1.14"),sQuery(id+"F0.wireOp",EDGE,"E10.1.15"),sQuery(id+"F0.wireOp",EDGE,"E10.1.16"),sQuery(id+"F0.wireOp",EDGE,"E10.1.18"),sQuery(id+"F0.wireOp",EDGE,"E10.1.20"),sQuery(id+"F0.wireOp",EDGE,"E10.2.0"),sQuery(id+"F0.wireOp",EDGE,"E10.2.1"),sQuery(id+"F0.wireOp",EDGE,"E10.2.2"),sQuery(id+"F0.wireOp",EDGE,"E10.2.3"),sQuery(id+"F0.wireOp",EDGE,"E10.2.5"),sQuery(id+"F0.wireOp",EDGE,"E10.2.7"),sQuery(id+"F0.wireOp",EDGE,"E10.2.8"),sQuery(id+"F0.wireOp",EDGE,"E10.2.9"),sQuery(id+"F0.wireOp",EDGE,"E10.2.10"),sQuery(id+"F0.wireOp",EDGE,"E10.2.11"),sQuery(id+"F0.wireOp",EDGE,"E10.2.12"),sQuery(id+"F0.wireOp",EDGE,"E1"),sQuery(id+"F0.wireOp",EDGE,"E10.2.14"),sQuery(id+"F0.wireOp",EDGE,"E10.2.15"),sQuery(id+"F0.wireOp",EDGE,"E10.2.16"),sQuery(id+"F0.wireOp",EDGE,"E10.2.18"),sQuery(id+"F0.wireOp",EDGE,"E10.2.20"),sQuery(id+"F0.wireOp",EDGE,"E8.trimOffspring"),sQuery(id+"F0.wireOp",EDGE,"E0"),sQuery(id+"F0.wireOp",EDGE,"E10.1.6"),sQuery(id+"F0.wireOp",EDGE,"E11"),sQuery(id+"F0.wireOp",EDGE,"E12"),sQuery(id+"F0.wireOp",EDGE,"E13.1.0"),sQuery(id+"F0.wireOp",EDGE,"E13.1.1"),sQuery(id+"F0.wireOp",EDGE,"E13.2.0"),sQuery(id+"F0.wireOp",EDGE,"E13.2.1")])]}),"instanceName":"1"}),"instanceName":"1"});
            var Q2;
            Q2=makeQuery(id+"F19.opPattern","COPY",BODY,{"derivedFrom":makeQuery(id+"F18.opPattern","COPY",BODY,{"derivedFrom":makeQuery(id+"F13.opPattern","COPY",BODY,{"derivedFrom":makeQuery(id+"F1.opExtrude","SWEPT_BODY",BODY,{"disambiguationData":[OSD([sQuery(id+"F0.wireOp",EDGE,"E2.0"),sQuery(id+"F0.wireOp",EDGE,"E2.1"),sQuery(id+"F0.wireOp",EDGE,"E2.2"),sQuery(id+"F0.wireOp",EDGE,"E2.3"),sQuery(id+"F0.wireOp",EDGE,"E2.4"),sQuery(id+"F0.wireOp",EDGE,"E2.5"),sQuery(id+"F0.wireOp",EDGE,"E3"),sQuery(id+"F0.wireOp",EDGE,"E4"),sQuery(id+"F0.wireOp",EDGE,"E5.0"),sQuery(id+"F0.wireOp",EDGE,"E5.1"),sQuery(id+"F0.wireOp",EDGE,"E5.3"),sQuery(id+"F0.wireOp",EDGE,"E5.4"),sQuery(id+"F0.wireOp",EDGE,"E5.5"),sQuery(id+"F0.wireOp",EDGE,"E6.trimOffspring"),sQuery(id+"F0.wireOp",EDGE,"E7.trimOffspring"),sQuery(id+"F0.wireOp",EDGE,"E9.trimOffspring"),sQuery(id+"F0.wireOp",EDGE,"E10.1.0"),sQuery(id+"F0.wireOp",EDGE,"E10.1.1"),sQuery(id+"F0.wireOp",EDGE,"E10.1.2"),sQuery(id+"F0.wireOp",EDGE,"E10.1.3"),sQuery(id+"F0.wireOp",EDGE,"E10.1.5"),sQuery(id+"F0.wireOp",EDGE,"E10.1.7"),sQuery(id+"F0.wireOp",EDGE,"E10.1.8"),sQuery(id+"F0.wireOp",EDGE,"E10.1.9"),sQuery(id+"F0.wireOp",EDGE,"E10.1.10"),sQuery(id+"F0.wireOp",EDGE,"E10.1.11"),sQuery(id+"F0.wireOp",EDGE,"E10.1.12"),sQuery(id+"F0.wireOp",EDGE,"E10.1.14"),sQuery(id+"F0.wireOp",EDGE,"E10.1.15"),sQuery(id+"F0.wireOp",EDGE,"E10.1.16"),sQuery(id+"F0.wireOp",EDGE,"E10.1.18"),sQuery(id+"F0.wireOp",EDGE,"E10.1.20"),sQuery(id+"F0.wireOp",EDGE,"E10.2.0"),sQuery(id+"F0.wireOp",EDGE,"E10.2.1"),sQuery(id+"F0.wireOp",EDGE,"E10.2.2"),sQuery(id+"F0.wireOp",EDGE,"E10.2.3"),sQuery(id+"F0.wireOp",EDGE,"E10.2.5"),sQuery(id+"F0.wireOp",EDGE,"E10.2.7"),sQuery(id+"F0.wireOp",EDGE,"E10.2.8"),sQuery(id+"F0.wireOp",EDGE,"E10.2.9"),sQuery(id+"F0.wireOp",EDGE,"E10.2.10"),sQuery(id+"F0.wireOp",EDGE,"E10.2.11"),sQuery(id+"F0.wireOp",EDGE,"E10.2.12"),sQuery(id+"F0.wireOp",EDGE,"E1"),sQuery(id+"F0.wireOp",EDGE,"E10.2.14"),sQuery(id+"F0.wireOp",EDGE,"E10.2.15"),sQuery(id+"F0.wireOp",EDGE,"E10.2.16"),sQuery(id+"F0.wireOp",EDGE,"E10.2.18"),sQuery(id+"F0.wireOp",EDGE,"E10.2.20"),sQuery(id+"F0.wireOp",EDGE,"E8.trimOffspring"),sQuery(id+"F0.wireOp",EDGE,"E0"),sQuery(id+"F0.wireOp",EDGE,"E10.1.6"),sQuery(id+"F0.wireOp",EDGE,"E11"),sQuery(id+"F0.wireOp",EDGE,"E12"),sQuery(id+"F0.wireOp",EDGE,"E13.1.0"),sQuery(id+"F0.wireOp",EDGE,"E13.1.1"),sQuery(id+"F0.wireOp",EDGE,"E13.2.0"),sQuery(id+"F0.wireOp",EDGE,"E13.2.1")])]}),"instanceName":"1"}),"instanceName":"1"}),"instanceName":"1"});
            var Q3;
            Q3=makeQuery(id+"F20.opPattern","COPY",BODY,{"derivedFrom":makeQuery(id+"F19.opPattern","COPY",BODY,{"derivedFrom":makeQuery(id+"F18.opPattern","COPY",BODY,{"derivedFrom":makeQuery(id+"F13.opPattern","COPY",BODY,{"derivedFrom":makeQuery(id+"F1.opExtrude","SWEPT_BODY",BODY,{"disambiguationData":[OSD([sQuery(id+"F0.wireOp",EDGE,"E2.0"),sQuery(id+"F0.wireOp",EDGE,"E2.1"),sQuery(id+"F0.wireOp",EDGE,"E2.2"),sQuery(id+"F0.wireOp",EDGE,"E2.3"),sQuery(id+"F0.wireOp",EDGE,"E2.4"),sQuery(id+"F0.wireOp",EDGE,"E2.5"),sQuery(id+"F0.wireOp",EDGE,"E3"),sQuery(id+"F0.wireOp",EDGE,"E4"),sQuery(id+"F0.wireOp",EDGE,"E5.0"),sQuery(id+"F0.wireOp",EDGE,"E5.1"),sQuery(id+"F0.wireOp",EDGE,"E5.3"),sQuery(id+"F0.wireOp",EDGE,"E5.4"),sQuery(id+"F0.wireOp",EDGE,"E5.5"),sQuery(id+"F0.wireOp",EDGE,"E6.trimOffspring"),sQuery(id+"F0.wireOp",EDGE,"E7.trimOffspring"),sQuery(id+"F0.wireOp",EDGE,"E9.trimOffspring"),sQuery(id+"F0.wireOp",EDGE,"E10.1.0"),sQuery(id+"F0.wireOp",EDGE,"E10.1.1"),sQuery(id+"F0.wireOp",EDGE,"E10.1.2"),sQuery(id+"F0.wireOp",EDGE,"E10.1.3"),sQuery(id+"F0.wireOp",EDGE,"E10.1.5"),sQuery(id+"F0.wireOp",EDGE,"E10.1.7"),sQuery(id+"F0.wireOp",EDGE,"E10.1.8"),sQuery(id+"F0.wireOp",EDGE,"E10.1.9"),sQuery(id+"F0.wireOp",EDGE,"E10.1.10"),sQuery(id+"F0.wireOp",EDGE,"E10.1.11"),sQuery(id+"F0.wireOp",EDGE,"E10.1.12"),sQuery(id+"F0.wireOp",EDGE,"E10.1.14"),sQuery(id+"F0.wireOp",EDGE,"E10.1.15"),sQuery(id+"F0.wireOp",EDGE,"E10.1.16"),sQuery(id+"F0.wireOp",EDGE,"E10.1.18"),sQuery(id+"F0.wireOp",EDGE,"E10.1.20"),sQuery(id+"F0.wireOp",EDGE,"E10.2.0"),sQuery(id+"F0.wireOp",EDGE,"E10.2.1"),sQuery(id+"F0.wireOp",EDGE,"E10.2.2"),sQuery(id+"F0.wireOp",EDGE,"E10.2.3"),sQuery(id+"F0.wireOp",EDGE,"E10.2.5"),sQuery(id+"F0.wireOp",EDGE,"E10.2.7"),sQuery(id+"F0.wireOp",EDGE,"E10.2.8"),sQuery(id+"F0.wireOp",EDGE,"E10.2.9"),sQuery(id+"F0.wireOp",EDGE,"E10.2.10"),sQuery(id+"F0.wireOp",EDGE,"E10.2.11"),sQuery(id+"F0.wireOp",EDGE,"E10.2.12"),sQuery(id+"F0.wireOp",EDGE,"E1"),sQuery(id+"F0.wireOp",EDGE,"E10.2.14"),sQuery(id+"F0.wireOp",EDGE,"E10.2.15"),sQuery(id+"F0.wireOp",EDGE,"E10.2.16"),sQuery(id+"F0.wireOp",EDGE,"E10.2.18"),sQuery(id+"F0.wireOp",EDGE,"E10.2.20"),sQuery(id+"F0.wireOp",EDGE,"E8.trimOffspring"),sQuery(id+"F0.wireOp",EDGE,"E0"),sQuery(id+"F0.wireOp",EDGE,"E10.1.6"),sQuery(id+"F0.wireOp",EDGE,"E11"),sQuery(id+"F0.wireOp",EDGE,"E12"),sQuery(id+"F0.wireOp",EDGE,"E13.1.0"),sQuery(id+"F0.wireOp",EDGE,"E13.1.1"),sQuery(id+"F0.wireOp",EDGE,"E13.2.0"),sQuery(id+"F0.wireOp",EDGE,"E13.2.1")])]}),"instanceName":"1"}),"instanceName":"1"}),"instanceName":"1"}),"instanceName":"1"});
            var Q4;
            Q4=makeQuery(id+"F21.opPattern","COPY",BODY,{"derivedFrom":makeQuery(id+"F20.opPattern","COPY",BODY,{"derivedFrom":makeQuery(id+"F19.opPattern","COPY",BODY,{"derivedFrom":makeQuery(id+"F18.opPattern","COPY",BODY,{"derivedFrom":makeQuery(id+"F13.opPattern","COPY",BODY,{"derivedFrom":makeQuery(id+"F1.opExtrude","SWEPT_BODY",BODY,{"disambiguationData":[OSD([sQuery(id+"F0.wireOp",EDGE,"E2.0"),sQuery(id+"F0.wireOp",EDGE,"E2.1"),sQuery(id+"F0.wireOp",EDGE,"E2.2"),sQuery(id+"F0.wireOp",EDGE,"E2.3"),sQuery(id+"F0.wireOp",EDGE,"E2.4"),sQuery(id+"F0.wireOp",EDGE,"E2.5"),sQuery(id+"F0.wireOp",EDGE,"E3"),sQuery(id+"F0.wireOp",EDGE,"E4"),sQuery(id+"F0.wireOp",EDGE,"E5.0"),sQuery(id+"F0.wireOp",EDGE,"E5.1"),sQuery(id+"F0.wireOp",EDGE,"E5.3"),sQuery(id+"F0.wireOp",EDGE,"E5.4"),sQuery(id+"F0.wireOp",EDGE,"E5.5"),sQuery(id+"F0.wireOp",EDGE,"E6.trimOffspring"),sQuery(id+"F0.wireOp",EDGE,"E7.trimOffspring"),sQuery(id+"F0.wireOp",EDGE,"E9.trimOffspring"),sQuery(id+"F0.wireOp",EDGE,"E10.1.0"),sQuery(id+"F0.wireOp",EDGE,"E10.1.1"),sQuery(id+"F0.wireOp",EDGE,"E10.1.2"),sQuery(id+"F0.wireOp",EDGE,"E10.1.3"),sQuery(id+"F0.wireOp",EDGE,"E10.1.5"),sQuery(id+"F0.wireOp",EDGE,"E10.1.7"),sQuery(id+"F0.wireOp",EDGE,"E10.1.8"),sQuery(id+"F0.wireOp",EDGE,"E10.1.9"),sQuery(id+"F0.wireOp",EDGE,"E10.1.10"),sQuery(id+"F0.wireOp",EDGE,"E10.1.11"),sQuery(id+"F0.wireOp",EDGE,"E10.1.12"),sQuery(id+"F0.wireOp",EDGE,"E10.1.14"),sQuery(id+"F0.wireOp",EDGE,"E10.1.15"),sQuery(id+"F0.wireOp",EDGE,"E10.1.16"),sQuery(id+"F0.wireOp",EDGE,"E10.1.18"),sQuery(id+"F0.wireOp",EDGE,"E10.1.20"),sQuery(id+"F0.wireOp",EDGE,"E10.2.0"),sQuery(id+"F0.wireOp",EDGE,"E10.2.1"),sQuery(id+"F0.wireOp",EDGE,"E10.2.2"),sQuery(id+"F0.wireOp",EDGE,"E10.2.3"),sQuery(id+"F0.wireOp",EDGE,"E10.2.5"),sQuery(id+"F0.wireOp",EDGE,"E10.2.7"),sQuery(id+"F0.wireOp",EDGE,"E10.2.8"),sQuery(id+"F0.wireOp",EDGE,"E10.2.9"),sQuery(id+"F0.wireOp",EDGE,"E10.2.10"),sQuery(id+"F0.wireOp",EDGE,"E10.2.11"),sQuery(id+"F0.wireOp",EDGE,"E10.2.12"),sQuery(id+"F0.wireOp",EDGE,"E1"),sQuery(id+"F0.wireOp",EDGE,"E10.2.14"),sQuery(id+"F0.wireOp",EDGE,"E10.2.15"),sQuery(id+"F0.wireOp",EDGE,"E10.2.16"),sQuery(id+"F0.wireOp",EDGE,"E10.2.18"),sQuery(id+"F0.wireOp",EDGE,"E10.2.20"),sQuery(id+"F0.wireOp",EDGE,"E8.trimOffspring"),sQuery(id+"F0.wireOp",EDGE,"E0"),sQuery(id+"F0.wireOp",EDGE,"E10.1.6"),sQuery(id+"F0.wireOp",EDGE,"E11"),sQuery(id+"F0.wireOp",EDGE,"E12"),sQuery(id+"F0.wireOp",EDGE,"E13.1.0"),sQuery(id+"F0.wireOp",EDGE,"E13.1.1"),sQuery(id+"F0.wireOp",EDGE,"E13.2.0"),sQuery(id+"F0.wireOp",EDGE,"E13.2.1")])]}),"instanceName":"1"}),"instanceName":"1"}),"instanceName":"1"}),"instanceName":"1"}),"instanceName":"1"});
            var Q5;
            Q5=makeQuery(id+"F23.opPattern","COPY",BODY,{"derivedFrom":makeQuery(id+"F1.opExtrude","SWEPT_BODY",BODY,{"disambiguationData":[OSD([sQuery(id+"F0.wireOp",EDGE,"E2.0"),sQuery(id+"F0.wireOp",EDGE,"E2.1"),sQuery(id+"F0.wireOp",EDGE,"E2.2"),sQuery(id+"F0.wireOp",EDGE,"E2.3"),sQuery(id+"F0.wireOp",EDGE,"E2.4"),sQuery(id+"F0.wireOp",EDGE,"E2.5"),sQuery(id+"F0.wireOp",EDGE,"E3"),sQuery(id+"F0.wireOp",EDGE,"E4"),sQuery(id+"F0.wireOp",EDGE,"E5.0"),sQuery(id+"F0.wireOp",EDGE,"E5.1"),sQuery(id+"F0.wireOp",EDGE,"E5.3"),sQuery(id+"F0.wireOp",EDGE,"E5.4"),sQuery(id+"F0.wireOp",EDGE,"E5.5"),sQuery(id+"F0.wireOp",EDGE,"E6.trimOffspring"),sQuery(id+"F0.wireOp",EDGE,"E7.trimOffspring"),sQuery(id+"F0.wireOp",EDGE,"E9.trimOffspring"),sQuery(id+"F0.wireOp",EDGE,"E10.1.0"),sQuery(id+"F0.wireOp",EDGE,"E10.1.1"),sQuery(id+"F0.wireOp",EDGE,"E10.1.2"),sQuery(id+"F0.wireOp",EDGE,"E10.1.3"),sQuery(id+"F0.wireOp",EDGE,"E10.1.5"),sQuery(id+"F0.wireOp",EDGE,"E10.1.7"),sQuery(id+"F0.wireOp",EDGE,"E10.1.8"),sQuery(id+"F0.wireOp",EDGE,"E10.1.9"),sQuery(id+"F0.wireOp",EDGE,"E10.1.10"),sQuery(id+"F0.wireOp",EDGE,"E10.1.11"),sQuery(id+"F0.wireOp",EDGE,"E10.1.12"),sQuery(id+"F0.wireOp",EDGE,"E10.1.14"),sQuery(id+"F0.wireOp",EDGE,"E10.1.15"),sQuery(id+"F0.wireOp",EDGE,"E10.1.16"),sQuery(id+"F0.wireOp",EDGE,"E10.1.18"),sQuery(id+"F0.wireOp",EDGE,"E10.1.20"),sQuery(id+"F0.wireOp",EDGE,"E10.2.0"),sQuery(id+"F0.wireOp",EDGE,"E10.2.1"),sQuery(id+"F0.wireOp",EDGE,"E10.2.2"),sQuery(id+"F0.wireOp",EDGE,"E10.2.3"),sQuery(id+"F0.wireOp",EDGE,"E10.2.5"),sQuery(id+"F0.wireOp",EDGE,"E10.2.7"),sQuery(id+"F0.wireOp",EDGE,"E10.2.8"),sQuery(id+"F0.wireOp",EDGE,"E10.2.9"),sQuery(id+"F0.wireOp",EDGE,"E10.2.10"),sQuery(id+"F0.wireOp",EDGE,"E10.2.11"),sQuery(id+"F0.wireOp",EDGE,"E10.2.12"),sQuery(id+"F0.wireOp",EDGE,"E1"),sQuery(id+"F0.wireOp",EDGE,"E10.2.14"),sQuery(id+"F0.wireOp",EDGE,"E10.2.15"),sQuery(id+"F0.wireOp",EDGE,"E10.2.16"),sQuery(id+"F0.wireOp",EDGE,"E10.2.18"),sQuery(id+"F0.wireOp",EDGE,"E10.2.20"),sQuery(id+"F0.wireOp",EDGE,"E8.trimOffspring"),sQuery(id+"F0.wireOp",EDGE,"E0"),sQuery(id+"F0.wireOp",EDGE,"E10.1.6"),sQuery(id+"F0.wireOp",EDGE,"E11"),sQuery(id+"F0.wireOp",EDGE,"E12"),sQuery(id+"F0.wireOp",EDGE,"E13.1.0"),sQuery(id+"F0.wireOp",EDGE,"E13.1.1"),sQuery(id+"F0.wireOp",EDGE,"E13.2.0"),sQuery(id+"F0.wireOp",EDGE,"E13.2.1")])]}),"instanceName":"1"});
            var Q6;
            Q6=makeQuery(id+"F23.opPattern","COPY",BODY,{"derivedFrom":makeQuery(id+"F5.opPattern","COPY",BODY,{"derivedFrom":makeQuery(id+"F1.opExtrude","SWEPT_BODY",BODY,{"disambiguationData":[OSD([sQuery(id+"F0.wireOp",EDGE,"E2.0"),sQuery(id+"F0.wireOp",EDGE,"E2.1"),sQuery(id+"F0.wireOp",EDGE,"E2.2"),sQuery(id+"F0.wireOp",EDGE,"E2.3"),sQuery(id+"F0.wireOp",EDGE,"E2.4"),sQuery(id+"F0.wireOp",EDGE,"E2.5"),sQuery(id+"F0.wireOp",EDGE,"E3"),sQuery(id+"F0.wireOp",EDGE,"E4"),sQuery(id+"F0.wireOp",EDGE,"E5.0"),sQuery(id+"F0.wireOp",EDGE,"E5.1"),sQuery(id+"F0.wireOp",EDGE,"E5.3"),sQuery(id+"F0.wireOp",EDGE,"E5.4"),sQuery(id+"F0.wireOp",EDGE,"E5.5"),sQuery(id+"F0.wireOp",EDGE,"E6.trimOffspring"),sQuery(id+"F0.wireOp",EDGE,"E7.trimOffspring"),sQuery(id+"F0.wireOp",EDGE,"E9.trimOffspring"),sQuery(id+"F0.wireOp",EDGE,"E10.1.0"),sQuery(id+"F0.wireOp",EDGE,"E10.1.1"),sQuery(id+"F0.wireOp",EDGE,"E10.1.2"),sQuery(id+"F0.wireOp",EDGE,"E10.1.3"),sQuery(id+"F0.wireOp",EDGE,"E10.1.5"),sQuery(id+"F0.wireOp",EDGE,"E10.1.7"),sQuery(id+"F0.wireOp",EDGE,"E10.1.8"),sQuery(id+"F0.wireOp",EDGE,"E10.1.9"),sQuery(id+"F0.wireOp",EDGE,"E10.1.10"),sQuery(id+"F0.wireOp",EDGE,"E10.1.11"),sQuery(id+"F0.wireOp",EDGE,"E10.1.12"),sQuery(id+"F0.wireOp",EDGE,"E10.1.14"),sQuery(id+"F0.wireOp",EDGE,"E10.1.15"),sQuery(id+"F0.wireOp",EDGE,"E10.1.16"),sQuery(id+"F0.wireOp",EDGE,"E10.1.18"),sQuery(id+"F0.wireOp",EDGE,"E10.1.20"),sQuery(id+"F0.wireOp",EDGE,"E10.2.0"),sQuery(id+"F0.wireOp",EDGE,"E10.2.1"),sQuery(id+"F0.wireOp",EDGE,"E10.2.2"),sQuery(id+"F0.wireOp",EDGE,"E10.2.3"),sQuery(id+"F0.wireOp",EDGE,"E10.2.5"),sQuery(id+"F0.wireOp",EDGE,"E10.2.7"),sQuery(id+"F0.wireOp",EDGE,"E10.2.8"),sQuery(id+"F0.wireOp",EDGE,"E10.2.9"),sQuery(id+"F0.wireOp",EDGE,"E10.2.10"),sQuery(id+"F0.wireOp",EDGE,"E10.2.11"),sQuery(id+"F0.wireOp",EDGE,"E10.2.12"),sQuery(id+"F0.wireOp",EDGE,"E1"),sQuery(id+"F0.wireOp",EDGE,"E10.2.14"),sQuery(id+"F0.wireOp",EDGE,"E10.2.15"),sQuery(id+"F0.wireOp",EDGE,"E10.2.16"),sQuery(id+"F0.wireOp",EDGE,"E10.2.18"),sQuery(id+"F0.wireOp",EDGE,"E10.2.20"),sQuery(id+"F0.wireOp",EDGE,"E8.trimOffspring"),sQuery(id+"F0.wireOp",EDGE,"E0"),sQuery(id+"F0.wireOp",EDGE,"E10.1.6"),sQuery(id+"F0.wireOp",EDGE,"E11"),sQuery(id+"F0.wireOp",EDGE,"E12"),sQuery(id+"F0.wireOp",EDGE,"E13.1.0"),sQuery(id+"F0.wireOp",EDGE,"E13.1.1"),sQuery(id+"F0.wireOp",EDGE,"E13.2.0"),sQuery(id+"F0.wireOp",EDGE,"E13.2.1")])]}),"instanceName":"1"}),"instanceName":"1"});
            var Q7;
            Q7=makeQuery(id+"F23.opPattern","COPY",BODY,{"derivedFrom":makeQuery(id+"F7.opPattern","COPY",BODY,{"derivedFrom":makeQuery(id+"F1.opExtrude","SWEPT_BODY",BODY,{"disambiguationData":[OSD([sQuery(id+"F0.wireOp",EDGE,"E2.0"),sQuery(id+"F0.wireOp",EDGE,"E2.1"),sQuery(id+"F0.wireOp",EDGE,"E2.2"),sQuery(id+"F0.wireOp",EDGE,"E2.3"),sQuery(id+"F0.wireOp",EDGE,"E2.4"),sQuery(id+"F0.wireOp",EDGE,"E2.5"),sQuery(id+"F0.wireOp",EDGE,"E3"),sQuery(id+"F0.wireOp",EDGE,"E4"),sQuery(id+"F0.wireOp",EDGE,"E5.0"),sQuery(id+"F0.wireOp",EDGE,"E5.1"),sQuery(id+"F0.wireOp",EDGE,"E5.3"),sQuery(id+"F0.wireOp",EDGE,"E5.4"),sQuery(id+"F0.wireOp",EDGE,"E5.5"),sQuery(id+"F0.wireOp",EDGE,"E6.trimOffspring"),sQuery(id+"F0.wireOp",EDGE,"E7.trimOffspring"),sQuery(id+"F0.wireOp",EDGE,"E9.trimOffspring"),sQuery(id+"F0.wireOp",EDGE,"E10.1.0"),sQuery(id+"F0.wireOp",EDGE,"E10.1.1"),sQuery(id+"F0.wireOp",EDGE,"E10.1.2"),sQuery(id+"F0.wireOp",EDGE,"E10.1.3"),sQuery(id+"F0.wireOp",EDGE,"E10.1.5"),sQuery(id+"F0.wireOp",EDGE,"E10.1.7"),sQuery(id+"F0.wireOp",EDGE,"E10.1.8"),sQuery(id+"F0.wireOp",EDGE,"E10.1.9"),sQuery(id+"F0.wireOp",EDGE,"E10.1.10"),sQuery(id+"F0.wireOp",EDGE,"E10.1.11"),sQuery(id+"F0.wireOp",EDGE,"E10.1.12"),sQuery(id+"F0.wireOp",EDGE,"E10.1.14"),sQuery(id+"F0.wireOp",EDGE,"E10.1.15"),sQuery(id+"F0.wireOp",EDGE,"E10.1.16"),sQuery(id+"F0.wireOp",EDGE,"E10.1.18"),sQuery(id+"F0.wireOp",EDGE,"E10.1.20"),sQuery(id+"F0.wireOp",EDGE,"E10.2.0"),sQuery(id+"F0.wireOp",EDGE,"E10.2.1"),sQuery(id+"F0.wireOp",EDGE,"E10.2.2"),sQuery(id+"F0.wireOp",EDGE,"E10.2.3"),sQuery(id+"F0.wireOp",EDGE,"E10.2.5"),sQuery(id+"F0.wireOp",EDGE,"E10.2.7"),sQuery(id+"F0.wireOp",EDGE,"E10.2.8"),sQuery(id+"F0.wireOp",EDGE,"E10.2.9"),sQuery(id+"F0.wireOp",EDGE,"E10.2.10"),sQuery(id+"F0.wireOp",EDGE,"E10.2.11"),sQuery(id+"F0.wireOp",EDGE,"E10.2.12"),sQuery(id+"F0.wireOp",EDGE,"E1"),sQuery(id+"F0.wireOp",EDGE,"E10.2.14"),sQuery(id+"F0.wireOp",EDGE,"E10.2.15"),sQuery(id+"F0.wireOp",EDGE,"E10.2.16"),sQuery(id+"F0.wireOp",EDGE,"E10.2.18"),sQuery(id+"F0.wireOp",EDGE,"E10.2.20"),sQuery(id+"F0.wireOp",EDGE,"E8.trimOffspring"),sQuery(id+"F0.wireOp",EDGE,"E0"),sQuery(id+"F0.wireOp",EDGE,"E10.1.6"),sQuery(id+"F0.wireOp",EDGE,"E11"),sQuery(id+"F0.wireOp",EDGE,"E12"),sQuery(id+"F0.wireOp",EDGE,"E13.1.0"),sQuery(id+"F0.wireOp",EDGE,"E13.1.1"),sQuery(id+"F0.wireOp",EDGE,"E13.2.0"),sQuery(id+"F0.wireOp",EDGE,"E13.2.1")])]}),"instanceName":"1"}),"instanceName":"1"});
            var Q8;
            Q8=makeQuery(id+"F23.opPattern","COPY",BODY,{"derivedFrom":makeQuery(id+"F8.opPattern","COPY",BODY,{"derivedFrom":makeQuery(id+"F7.opPattern","COPY",BODY,{"derivedFrom":makeQuery(id+"F1.opExtrude","SWEPT_BODY",BODY,{"disambiguationData":[OSD([sQuery(id+"F0.wireOp",EDGE,"E2.0"),sQuery(id+"F0.wireOp",EDGE,"E2.1"),sQuery(id+"F0.wireOp",EDGE,"E2.2"),sQuery(id+"F0.wireOp",EDGE,"E2.3"),sQuery(id+"F0.wireOp",EDGE,"E2.4"),sQuery(id+"F0.wireOp",EDGE,"E2.5"),sQuery(id+"F0.wireOp",EDGE,"E3"),sQuery(id+"F0.wireOp",EDGE,"E4"),sQuery(id+"F0.wireOp",EDGE,"E5.0"),sQuery(id+"F0.wireOp",EDGE,"E5.1"),sQuery(id+"F0.wireOp",EDGE,"E5.3"),sQuery(id+"F0.wireOp",EDGE,"E5.4"),sQuery(id+"F0.wireOp",EDGE,"E5.5"),sQuery(id+"F0.wireOp",EDGE,"E6.trimOffspring"),sQuery(id+"F0.wireOp",EDGE,"E7.trimOffspring"),sQuery(id+"F0.wireOp",EDGE,"E9.trimOffspring"),sQuery(id+"F0.wireOp",EDGE,"E10.1.0"),sQuery(id+"F0.wireOp",EDGE,"E10.1.1"),sQuery(id+"F0.wireOp",EDGE,"E10.1.2"),sQuery(id+"F0.wireOp",EDGE,"E10.1.3"),sQuery(id+"F0.wireOp",EDGE,"E10.1.5"),sQuery(id+"F0.wireOp",EDGE,"E10.1.7"),sQuery(id+"F0.wireOp",EDGE,"E10.1.8"),sQuery(id+"F0.wireOp",EDGE,"E10.1.9"),sQuery(id+"F0.wireOp",EDGE,"E10.1.10"),sQuery(id+"F0.wireOp",EDGE,"E10.1.11"),sQuery(id+"F0.wireOp",EDGE,"E10.1.12"),sQuery(id+"F0.wireOp",EDGE,"E10.1.14"),sQuery(id+"F0.wireOp",EDGE,"E10.1.15"),sQuery(id+"F0.wireOp",EDGE,"E10.1.16"),sQuery(id+"F0.wireOp",EDGE,"E10.1.18"),sQuery(id+"F0.wireOp",EDGE,"E10.1.20"),sQuery(id+"F0.wireOp",EDGE,"E10.2.0"),sQuery(id+"F0.wireOp",EDGE,"E10.2.1"),sQuery(id+"F0.wireOp",EDGE,"E10.2.2"),sQuery(id+"F0.wireOp",EDGE,"E10.2.3"),sQuery(id+"F0.wireOp",EDGE,"E10.2.5"),sQuery(id+"F0.wireOp",EDGE,"E10.2.7"),sQuery(id+"F0.wireOp",EDGE,"E10.2.8"),sQuery(id+"F0.wireOp",EDGE,"E10.2.9"),sQuery(id+"F0.wireOp",EDGE,"E10.2.10"),sQuery(id+"F0.wireOp",EDGE,"E10.2.11"),sQuery(id+"F0.wireOp",EDGE,"E10.2.12"),sQuery(id+"F0.wireOp",EDGE,"E1"),sQuery(id+"F0.wireOp",EDGE,"E10.2.14"),sQuery(id+"F0.wireOp",EDGE,"E10.2.15"),sQuery(id+"F0.wireOp",EDGE,"E10.2.16"),sQuery(id+"F0.wireOp",EDGE,"E10.2.18"),sQuery(id+"F0.wireOp",EDGE,"E10.2.20"),sQuery(id+"F0.wireOp",EDGE,"E8.trimOffspring"),sQuery(id+"F0.wireOp",EDGE,"E0"),sQuery(id+"F0.wireOp",EDGE,"E10.1.6"),sQuery(id+"F0.wireOp",EDGE,"E11"),sQuery(id+"F0.wireOp",EDGE,"E12"),sQuery(id+"F0.wireOp",EDGE,"E13.1.0"),sQuery(id+"F0.wireOp",EDGE,"E13.1.1"),sQuery(id+"F0.wireOp",EDGE,"E13.2.0"),sQuery(id+"F0.wireOp",EDGE,"E13.2.1")])]}),"instanceName":"1"}),"instanceName":"1"}),"instanceName":"1"});
            var Q9;
            Q9=makeQuery(id+"F36.opPattern","COPY",BODY,{"derivedFrom":makeQuery(id+"F23.opPattern","COPY",BODY,{"derivedFrom":makeQuery(id+"F7.opPattern","COPY",BODY,{"derivedFrom":makeQuery(id+"F1.opExtrude","SWEPT_BODY",BODY,{"disambiguationData":[OSD([sQuery(id+"F0.wireOp",EDGE,"E2.0"),sQuery(id+"F0.wireOp",EDGE,"E2.1"),sQuery(id+"F0.wireOp",EDGE,"E2.2"),sQuery(id+"F0.wireOp",EDGE,"E2.3"),sQuery(id+"F0.wireOp",EDGE,"E2.4"),sQuery(id+"F0.wireOp",EDGE,"E2.5"),sQuery(id+"F0.wireOp",EDGE,"E3"),sQuery(id+"F0.wireOp",EDGE,"E4"),sQuery(id+"F0.wireOp",EDGE,"E5.0"),sQuery(id+"F0.wireOp",EDGE,"E5.1"),sQuery(id+"F0.wireOp",EDGE,"E5.3"),sQuery(id+"F0.wireOp",EDGE,"E5.4"),sQuery(id+"F0.wireOp",EDGE,"E5.5"),sQuery(id+"F0.wireOp",EDGE,"E6.trimOffspring"),sQuery(id+"F0.wireOp",EDGE,"E7.trimOffspring"),sQuery(id+"F0.wireOp",EDGE,"E9.trimOffspring"),sQuery(id+"F0.wireOp",EDGE,"E10.1.0"),sQuery(id+"F0.wireOp",EDGE,"E10.1.1"),sQuery(id+"F0.wireOp",EDGE,"E10.1.2"),sQuery(id+"F0.wireOp",EDGE,"E10.1.3"),sQuery(id+"F0.wireOp",EDGE,"E10.1.5"),sQuery(id+"F0.wireOp",EDGE,"E10.1.7"),sQuery(id+"F0.wireOp",EDGE,"E10.1.8"),sQuery(id+"F0.wireOp",EDGE,"E10.1.9"),sQuery(id+"F0.wireOp",EDGE,"E10.1.10"),sQuery(id+"F0.wireOp",EDGE,"E10.1.11"),sQuery(id+"F0.wireOp",EDGE,"E10.1.12"),sQuery(id+"F0.wireOp",EDGE,"E10.1.14"),sQuery(id+"F0.wireOp",EDGE,"E10.1.15"),sQuery(id+"F0.wireOp",EDGE,"E10.1.16"),sQuery(id+"F0.wireOp",EDGE,"E10.1.18"),sQuery(id+"F0.wireOp",EDGE,"E10.1.20"),sQuery(id+"F0.wireOp",EDGE,"E10.2.0"),sQuery(id+"F0.wireOp",EDGE,"E10.2.1"),sQuery(id+"F0.wireOp",EDGE,"E10.2.2"),sQuery(id+"F0.wireOp",EDGE,"E10.2.3"),sQuery(id+"F0.wireOp",EDGE,"E10.2.5"),sQuery(id+"F0.wireOp",EDGE,"E10.2.7"),sQuery(id+"F0.wireOp",EDGE,"E10.2.8"),sQuery(id+"F0.wireOp",EDGE,"E10.2.9"),sQuery(id+"F0.wireOp",EDGE,"E10.2.10"),sQuery(id+"F0.wireOp",EDGE,"E10.2.11"),sQuery(id+"F0.wireOp",EDGE,"E10.2.12"),sQuery(id+"F0.wireOp",EDGE,"E1"),sQuery(id+"F0.wireOp",EDGE,"E10.2.14"),sQuery(id+"F0.wireOp",EDGE,"E10.2.15"),sQuery(id+"F0.wireOp",EDGE,"E10.2.16"),sQuery(id+"F0.wireOp",EDGE,"E10.2.18"),sQuery(id+"F0.wireOp",EDGE,"E10.2.20"),sQuery(id+"F0.wireOp",EDGE,"E8.trimOffspring"),sQuery(id+"F0.wireOp",EDGE,"E0"),sQuery(id+"F0.wireOp",EDGE,"E10.1.6"),sQuery(id+"F0.wireOp",EDGE,"E11"),sQuery(id+"F0.wireOp",EDGE,"E12"),sQuery(id+"F0.wireOp",EDGE,"E13.1.0"),sQuery(id+"F0.wireOp",EDGE,"E13.1.1"),sQuery(id+"F0.wireOp",EDGE,"E13.2.0"),sQuery(id+"F0.wireOp",EDGE,"E13.2.1")])]}),"instanceName":"1"}),"instanceName":"1"}),"instanceName":"1"});
            var Q10;
            Q10=makeQuery(id+"F39.opPattern","COPY",BODY,{"derivedFrom":makeQuery(id+"F36.opPattern","COPY",BODY,{"derivedFrom":makeQuery(id+"F23.opPattern","COPY",BODY,{"derivedFrom":makeQuery(id+"F7.opPattern","COPY",BODY,{"derivedFrom":makeQuery(id+"F1.opExtrude","SWEPT_BODY",BODY,{"disambiguationData":[OSD([sQuery(id+"F0.wireOp",EDGE,"E2.0"),sQuery(id+"F0.wireOp",EDGE,"E2.1"),sQuery(id+"F0.wireOp",EDGE,"E2.2"),sQuery(id+"F0.wireOp",EDGE,"E2.3"),sQuery(id+"F0.wireOp",EDGE,"E2.4"),sQuery(id+"F0.wireOp",EDGE,"E2.5"),sQuery(id+"F0.wireOp",EDGE,"E3"),sQuery(id+"F0.wireOp",EDGE,"E4"),sQuery(id+"F0.wireOp",EDGE,"E5.0"),sQuery(id+"F0.wireOp",EDGE,"E5.1"),sQuery(id+"F0.wireOp",EDGE,"E5.3"),sQuery(id+"F0.wireOp",EDGE,"E5.4"),sQuery(id+"F0.wireOp",EDGE,"E5.5"),sQuery(id+"F0.wireOp",EDGE,"E6.trimOffspring"),sQuery(id+"F0.wireOp",EDGE,"E7.trimOffspring"),sQuery(id+"F0.wireOp",EDGE,"E9.trimOffspring"),sQuery(id+"F0.wireOp",EDGE,"E10.1.0"),sQuery(id+"F0.wireOp",EDGE,"E10.1.1"),sQuery(id+"F0.wireOp",EDGE,"E10.1.2"),sQuery(id+"F0.wireOp",EDGE,"E10.1.3"),sQuery(id+"F0.wireOp",EDGE,"E10.1.5"),sQuery(id+"F0.wireOp",EDGE,"E10.1.7"),sQuery(id+"F0.wireOp",EDGE,"E10.1.8"),sQuery(id+"F0.wireOp",EDGE,"E10.1.9"),sQuery(id+"F0.wireOp",EDGE,"E10.1.10"),sQuery(id+"F0.wireOp",EDGE,"E10.1.11"),sQuery(id+"F0.wireOp",EDGE,"E10.1.12"),sQuery(id+"F0.wireOp",EDGE,"E10.1.14"),sQuery(id+"F0.wireOp",EDGE,"E10.1.15"),sQuery(id+"F0.wireOp",EDGE,"E10.1.16"),sQuery(id+"F0.wireOp",EDGE,"E10.1.18"),sQuery(id+"F0.wireOp",EDGE,"E10.1.20"),sQuery(id+"F0.wireOp",EDGE,"E10.2.0"),sQuery(id+"F0.wireOp",EDGE,"E10.2.1"),sQuery(id+"F0.wireOp",EDGE,"E10.2.2"),sQuery(id+"F0.wireOp",EDGE,"E10.2.3"),sQuery(id+"F0.wireOp",EDGE,"E10.2.5"),sQuery(id+"F0.wireOp",EDGE,"E10.2.7"),sQuery(id+"F0.wireOp",EDGE,"E10.2.8"),sQuery(id+"F0.wireOp",EDGE,"E10.2.9"),sQuery(id+"F0.wireOp",EDGE,"E10.2.10"),sQuery(id+"F0.wireOp",EDGE,"E10.2.11"),sQuery(id+"F0.wireOp",EDGE,"E10.2.12"),sQuery(id+"F0.wireOp",EDGE,"E1"),sQuery(id+"F0.wireOp",EDGE,"E10.2.14"),sQuery(id+"F0.wireOp",EDGE,"E10.2.15"),sQuery(id+"F0.wireOp",EDGE,"E10.2.16"),sQuery(id+"F0.wireOp",EDGE,"E10.2.18"),sQuery(id+"F0.wireOp",EDGE,"E10.2.20"),sQuery(id+"F0.wireOp",EDGE,"E8.trimOffspring"),sQuery(id+"F0.wireOp",EDGE,"E0"),sQuery(id+"F0.wireOp",EDGE,"E10.1.6"),sQuery(id+"F0.wireOp",EDGE,"E11"),sQuery(id+"F0.wireOp",EDGE,"E12"),sQuery(id+"F0.wireOp",EDGE,"E13.1.0"),sQuery(id+"F0.wireOp",EDGE,"E13.1.1"),sQuery(id+"F0.wireOp",EDGE,"E13.2.0"),sQuery(id+"F0.wireOp",EDGE,"E13.2.1")])]}),"instanceName":"1"}),"instanceName":"1"}),"instanceName":"1"}),"instanceName":"1"});
            var Q11;
            Q11=makeQuery(id+"F42.opPattern","COPY",BODY,{"derivedFrom":makeQuery(id+"F13.opPattern","COPY",BODY,{"derivedFrom":makeQuery(id+"F1.opExtrude","SWEPT_BODY",BODY,{"disambiguationData":[OSD([sQuery(id+"F0.wireOp",EDGE,"E2.0"),sQuery(id+"F0.wireOp",EDGE,"E2.1"),sQuery(id+"F0.wireOp",EDGE,"E2.2"),sQuery(id+"F0.wireOp",EDGE,"E2.3"),sQuery(id+"F0.wireOp",EDGE,"E2.4"),sQuery(id+"F0.wireOp",EDGE,"E2.5"),sQuery(id+"F0.wireOp",EDGE,"E3"),sQuery(id+"F0.wireOp",EDGE,"E4"),sQuery(id+"F0.wireOp",EDGE,"E5.0"),sQuery(id+"F0.wireOp",EDGE,"E5.1"),sQuery(id+"F0.wireOp",EDGE,"E5.3"),sQuery(id+"F0.wireOp",EDGE,"E5.4"),sQuery(id+"F0.wireOp",EDGE,"E5.5"),sQuery(id+"F0.wireOp",EDGE,"E6.trimOffspring"),sQuery(id+"F0.wireOp",EDGE,"E7.trimOffspring"),sQuery(id+"F0.wireOp",EDGE,"E9.trimOffspring"),sQuery(id+"F0.wireOp",EDGE,"E10.1.0"),sQuery(id+"F0.wireOp",EDGE,"E10.1.1"),sQuery(id+"F0.wireOp",EDGE,"E10.1.2"),sQuery(id+"F0.wireOp",EDGE,"E10.1.3"),sQuery(id+"F0.wireOp",EDGE,"E10.1.5"),sQuery(id+"F0.wireOp",EDGE,"E10.1.7"),sQuery(id+"F0.wireOp",EDGE,"E10.1.8"),sQuery(id+"F0.wireOp",EDGE,"E10.1.9"),sQuery(id+"F0.wireOp",EDGE,"E10.1.10"),sQuery(id+"F0.wireOp",EDGE,"E10.1.11"),sQuery(id+"F0.wireOp",EDGE,"E10.1.12"),sQuery(id+"F0.wireOp",EDGE,"E10.1.14"),sQuery(id+"F0.wireOp",EDGE,"E10.1.15"),sQuery(id+"F0.wireOp",EDGE,"E10.1.16"),sQuery(id+"F0.wireOp",EDGE,"E10.1.18"),sQuery(id+"F0.wireOp",EDGE,"E10.1.20"),sQuery(id+"F0.wireOp",EDGE,"E10.2.0"),sQuery(id+"F0.wireOp",EDGE,"E10.2.1"),sQuery(id+"F0.wireOp",EDGE,"E10.2.2"),sQuery(id+"F0.wireOp",EDGE,"E10.2.3"),sQuery(id+"F0.wireOp",EDGE,"E10.2.5"),sQuery(id+"F0.wireOp",EDGE,"E10.2.7"),sQuery(id+"F0.wireOp",EDGE,"E10.2.8"),sQuery(id+"F0.wireOp",EDGE,"E10.2.9"),sQuery(id+"F0.wireOp",EDGE,"E10.2.10"),sQuery(id+"F0.wireOp",EDGE,"E10.2.11"),sQuery(id+"F0.wireOp",EDGE,"E10.2.12"),sQuery(id+"F0.wireOp",EDGE,"E1"),sQuery(id+"F0.wireOp",EDGE,"E10.2.14"),sQuery(id+"F0.wireOp",EDGE,"E10.2.15"),sQuery(id+"F0.wireOp",EDGE,"E10.2.16"),sQuery(id+"F0.wireOp",EDGE,"E10.2.18"),sQuery(id+"F0.wireOp",EDGE,"E10.2.20"),sQuery(id+"F0.wireOp",EDGE,"E8.trimOffspring"),sQuery(id+"F0.wireOp",EDGE,"E0"),sQuery(id+"F0.wireOp",EDGE,"E10.1.6"),sQuery(id+"F0.wireOp",EDGE,"E11"),sQuery(id+"F0.wireOp",EDGE,"E12"),sQuery(id+"F0.wireOp",EDGE,"E13.1.0"),sQuery(id+"F0.wireOp",EDGE,"E13.1.1"),sQuery(id+"F0.wireOp",EDGE,"E13.2.0"),sQuery(id+"F0.wireOp",EDGE,"E13.2.1")])]}),"instanceName":"1"}),"instanceName":"1"});
            var Q12;
            Q12=makeQuery(id+"F45.opPattern","COPY",BODY,{"derivedFrom":makeQuery(id+"F5.opPattern","COPY",BODY,{"derivedFrom":makeQuery(id+"F1.opExtrude","SWEPT_BODY",BODY,{"disambiguationData":[OSD([sQuery(id+"F0.wireOp",EDGE,"E2.0"),sQuery(id+"F0.wireOp",EDGE,"E2.1"),sQuery(id+"F0.wireOp",EDGE,"E2.2"),sQuery(id+"F0.wireOp",EDGE,"E2.3"),sQuery(id+"F0.wireOp",EDGE,"E2.4"),sQuery(id+"F0.wireOp",EDGE,"E2.5"),sQuery(id+"F0.wireOp",EDGE,"E3"),sQuery(id+"F0.wireOp",EDGE,"E4"),sQuery(id+"F0.wireOp",EDGE,"E5.0"),sQuery(id+"F0.wireOp",EDGE,"E5.1"),sQuery(id+"F0.wireOp",EDGE,"E5.3"),sQuery(id+"F0.wireOp",EDGE,"E5.4"),sQuery(id+"F0.wireOp",EDGE,"E5.5"),sQuery(id+"F0.wireOp",EDGE,"E6.trimOffspring"),sQuery(id+"F0.wireOp",EDGE,"E7.trimOffspring"),sQuery(id+"F0.wireOp",EDGE,"E9.trimOffspring"),sQuery(id+"F0.wireOp",EDGE,"E10.1.0"),sQuery(id+"F0.wireOp",EDGE,"E10.1.1"),sQuery(id+"F0.wireOp",EDGE,"E10.1.2"),sQuery(id+"F0.wireOp",EDGE,"E10.1.3"),sQuery(id+"F0.wireOp",EDGE,"E10.1.5"),sQuery(id+"F0.wireOp",EDGE,"E10.1.7"),sQuery(id+"F0.wireOp",EDGE,"E10.1.8"),sQuery(id+"F0.wireOp",EDGE,"E10.1.9"),sQuery(id+"F0.wireOp",EDGE,"E10.1.10"),sQuery(id+"F0.wireOp",EDGE,"E10.1.11"),sQuery(id+"F0.wireOp",EDGE,"E10.1.12"),sQuery(id+"F0.wireOp",EDGE,"E10.1.14"),sQuery(id+"F0.wireOp",EDGE,"E10.1.15"),sQuery(id+"F0.wireOp",EDGE,"E10.1.16"),sQuery(id+"F0.wireOp",EDGE,"E10.1.18"),sQuery(id+"F0.wireOp",EDGE,"E10.1.20"),sQuery(id+"F0.wireOp",EDGE,"E10.2.0"),sQuery(id+"F0.wireOp",EDGE,"E10.2.1"),sQuery(id+"F0.wireOp",EDGE,"E10.2.2"),sQuery(id+"F0.wireOp",EDGE,"E10.2.3"),sQuery(id+"F0.wireOp",EDGE,"E10.2.5"),sQuery(id+"F0.wireOp",EDGE,"E10.2.7"),sQuery(id+"F0.wireOp",EDGE,"E10.2.8"),sQuery(id+"F0.wireOp",EDGE,"E10.2.9"),sQuery(id+"F0.wireOp",EDGE,"E10.2.10"),sQuery(id+"F0.wireOp",EDGE,"E10.2.11"),sQuery(id+"F0.wireOp",EDGE,"E10.2.12"),sQuery(id+"F0.wireOp",EDGE,"E1"),sQuery(id+"F0.wireOp",EDGE,"E10.2.14"),sQuery(id+"F0.wireOp",EDGE,"E10.2.15"),sQuery(id+"F0.wireOp",EDGE,"E10.2.16"),sQuery(id+"F0.wireOp",EDGE,"E10.2.18"),sQuery(id+"F0.wireOp",EDGE,"E10.2.20"),sQuery(id+"F0.wireOp",EDGE,"E8.trimOffspring"),sQuery(id+"F0.wireOp",EDGE,"E0"),sQuery(id+"F0.wireOp",EDGE,"E10.1.6"),sQuery(id+"F0.wireOp",EDGE,"E11"),sQuery(id+"F0.wireOp",EDGE,"E12"),sQuery(id+"F0.wireOp",EDGE,"E13.1.0"),sQuery(id+"F0.wireOp",EDGE,"E13.1.1"),sQuery(id+"F0.wireOp",EDGE,"E13.2.0"),sQuery(id+"F0.wireOp",EDGE,"E13.2.1")])]}),"instanceName":"1"}),"instanceName":"1"});
            var Q13;
            Q13=makeQuery(id+"F46.opPattern","COPY",BODY,{"derivedFrom":makeQuery(id+"F45.opPattern","COPY",BODY,{"derivedFrom":makeQuery(id+"F5.opPattern","COPY",BODY,{"derivedFrom":makeQuery(id+"F1.opExtrude","SWEPT_BODY",BODY,{"disambiguationData":[OSD([sQuery(id+"F0.wireOp",EDGE,"E2.0"),sQuery(id+"F0.wireOp",EDGE,"E2.1"),sQuery(id+"F0.wireOp",EDGE,"E2.2"),sQuery(id+"F0.wireOp",EDGE,"E2.3"),sQuery(id+"F0.wireOp",EDGE,"E2.4"),sQuery(id+"F0.wireOp",EDGE,"E2.5"),sQuery(id+"F0.wireOp",EDGE,"E3"),sQuery(id+"F0.wireOp",EDGE,"E4"),sQuery(id+"F0.wireOp",EDGE,"E5.0"),sQuery(id+"F0.wireOp",EDGE,"E5.1"),sQuery(id+"F0.wireOp",EDGE,"E5.3"),sQuery(id+"F0.wireOp",EDGE,"E5.4"),sQuery(id+"F0.wireOp",EDGE,"E5.5"),sQuery(id+"F0.wireOp",EDGE,"E6.trimOffspring"),sQuery(id+"F0.wireOp",EDGE,"E7.trimOffspring"),sQuery(id+"F0.wireOp",EDGE,"E9.trimOffspring"),sQuery(id+"F0.wireOp",EDGE,"E10.1.0"),sQuery(id+"F0.wireOp",EDGE,"E10.1.1"),sQuery(id+"F0.wireOp",EDGE,"E10.1.2"),sQuery(id+"F0.wireOp",EDGE,"E10.1.3"),sQuery(id+"F0.wireOp",EDGE,"E10.1.5"),sQuery(id+"F0.wireOp",EDGE,"E10.1.7"),sQuery(id+"F0.wireOp",EDGE,"E10.1.8"),sQuery(id+"F0.wireOp",EDGE,"E10.1.9"),sQuery(id+"F0.wireOp",EDGE,"E10.1.10"),sQuery(id+"F0.wireOp",EDGE,"E10.1.11"),sQuery(id+"F0.wireOp",EDGE,"E10.1.12"),sQuery(id+"F0.wireOp",EDGE,"E10.1.14"),sQuery(id+"F0.wireOp",EDGE,"E10.1.15"),sQuery(id+"F0.wireOp",EDGE,"E10.1.16"),sQuery(id+"F0.wireOp",EDGE,"E10.1.18"),sQuery(id+"F0.wireOp",EDGE,"E10.1.20"),sQuery(id+"F0.wireOp",EDGE,"E10.2.0"),sQuery(id+"F0.wireOp",EDGE,"E10.2.1"),sQuery(id+"F0.wireOp",EDGE,"E10.2.2"),sQuery(id+"F0.wireOp",EDGE,"E10.2.3"),sQuery(id+"F0.wireOp",EDGE,"E10.2.5"),sQuery(id+"F0.wireOp",EDGE,"E10.2.7"),sQuery(id+"F0.wireOp",EDGE,"E10.2.8"),sQuery(id+"F0.wireOp",EDGE,"E10.2.9"),sQuery(id+"F0.wireOp",EDGE,"E10.2.10"),sQuery(id+"F0.wireOp",EDGE,"E10.2.11"),sQuery(id+"F0.wireOp",EDGE,"E10.2.12"),sQuery(id+"F0.wireOp",EDGE,"E1"),sQuery(id+"F0.wireOp",EDGE,"E10.2.14"),sQuery(id+"F0.wireOp",EDGE,"E10.2.15"),sQuery(id+"F0.wireOp",EDGE,"E10.2.16"),sQuery(id+"F0.wireOp",EDGE,"E10.2.18"),sQuery(id+"F0.wireOp",EDGE,"E10.2.20"),sQuery(id+"F0.wireOp",EDGE,"E8.trimOffspring"),sQuery(id+"F0.wireOp",EDGE,"E0"),sQuery(id+"F0.wireOp",EDGE,"E10.1.6"),sQuery(id+"F0.wireOp",EDGE,"E11"),sQuery(id+"F0.wireOp",EDGE,"E12"),sQuery(id+"F0.wireOp",EDGE,"E13.1.0"),sQuery(id+"F0.wireOp",EDGE,"E13.1.1"),sQuery(id+"F0.wireOp",EDGE,"E13.2.0"),sQuery(id+"F0.wireOp",EDGE,"E13.2.1")])]}),"instanceName":"1"}),"instanceName":"1"}),"instanceName":"1"});
            var Q14;
            Q14=makeQuery(id+"F47.opPattern","COPY",BODY,{"derivedFrom":makeQuery(id+"F42.opPattern","COPY",BODY,{"derivedFrom":makeQuery(id+"F13.opPattern","COPY",BODY,{"derivedFrom":makeQuery(id+"F1.opExtrude","SWEPT_BODY",BODY,{"disambiguationData":[OSD([sQuery(id+"F0.wireOp",EDGE,"E2.0"),sQuery(id+"F0.wireOp",EDGE,"E2.1"),sQuery(id+"F0.wireOp",EDGE,"E2.2"),sQuery(id+"F0.wireOp",EDGE,"E2.3"),sQuery(id+"F0.wireOp",EDGE,"E2.4"),sQuery(id+"F0.wireOp",EDGE,"E2.5"),sQuery(id+"F0.wireOp",EDGE,"E3"),sQuery(id+"F0.wireOp",EDGE,"E4"),sQuery(id+"F0.wireOp",EDGE,"E5.0"),sQuery(id+"F0.wireOp",EDGE,"E5.1"),sQuery(id+"F0.wireOp",EDGE,"E5.3"),sQuery(id+"F0.wireOp",EDGE,"E5.4"),sQuery(id+"F0.wireOp",EDGE,"E5.5"),sQuery(id+"F0.wireOp",EDGE,"E6.trimOffspring"),sQuery(id+"F0.wireOp",EDGE,"E7.trimOffspring"),sQuery(id+"F0.wireOp",EDGE,"E9.trimOffspring"),sQuery(id+"F0.wireOp",EDGE,"E10.1.0"),sQuery(id+"F0.wireOp",EDGE,"E10.1.1"),sQuery(id+"F0.wireOp",EDGE,"E10.1.2"),sQuery(id+"F0.wireOp",EDGE,"E10.1.3"),sQuery(id+"F0.wireOp",EDGE,"E10.1.5"),sQuery(id+"F0.wireOp",EDGE,"E10.1.7"),sQuery(id+"F0.wireOp",EDGE,"E10.1.8"),sQuery(id+"F0.wireOp",EDGE,"E10.1.9"),sQuery(id+"F0.wireOp",EDGE,"E10.1.10"),sQuery(id+"F0.wireOp",EDGE,"E10.1.11"),sQuery(id+"F0.wireOp",EDGE,"E10.1.12"),sQuery(id+"F0.wireOp",EDGE,"E10.1.14"),sQuery(id+"F0.wireOp",EDGE,"E10.1.15"),sQuery(id+"F0.wireOp",EDGE,"E10.1.16"),sQuery(id+"F0.wireOp",EDGE,"E10.1.18"),sQuery(id+"F0.wireOp",EDGE,"E10.1.20"),sQuery(id+"F0.wireOp",EDGE,"E10.2.0"),sQuery(id+"F0.wireOp",EDGE,"E10.2.1"),sQuery(id+"F0.wireOp",EDGE,"E10.2.2"),sQuery(id+"F0.wireOp",EDGE,"E10.2.3"),sQuery(id+"F0.wireOp",EDGE,"E10.2.5"),sQuery(id+"F0.wireOp",EDGE,"E10.2.7"),sQuery(id+"F0.wireOp",EDGE,"E10.2.8"),sQuery(id+"F0.wireOp",EDGE,"E10.2.9"),sQuery(id+"F0.wireOp",EDGE,"E10.2.10"),sQuery(id+"F0.wireOp",EDGE,"E10.2.11"),sQuery(id+"F0.wireOp",EDGE,"E10.2.12"),sQuery(id+"F0.wireOp",EDGE,"E1"),sQuery(id+"F0.wireOp",EDGE,"E10.2.14"),sQuery(id+"F0.wireOp",EDGE,"E10.2.15"),sQuery(id+"F0.wireOp",EDGE,"E10.2.16"),sQuery(id+"F0.wireOp",EDGE,"E10.2.18"),sQuery(id+"F0.wireOp",EDGE,"E10.2.20"),sQuery(id+"F0.wireOp",EDGE,"E8.trimOffspring"),sQuery(id+"F0.wireOp",EDGE,"E0"),sQuery(id+"F0.wireOp",EDGE,"E10.1.6"),sQuery(id+"F0.wireOp",EDGE,"E11"),sQuery(id+"F0.wireOp",EDGE,"E12"),sQuery(id+"F0.wireOp",EDGE,"E13.1.0"),sQuery(id+"F0.wireOp",EDGE,"E13.1.1"),sQuery(id+"F0.wireOp",EDGE,"E13.2.0"),sQuery(id+"F0.wireOp",EDGE,"E13.2.1")])]}),"instanceName":"1"}),"instanceName":"1"}),"instanceName":"1"});
            var Q15;
            Q15=makeQuery(id+"F48.opPattern","COPY",BODY,{"derivedFrom":makeQuery(id+"F39.opPattern","COPY",BODY,{"derivedFrom":makeQuery(id+"F36.opPattern","COPY",BODY,{"derivedFrom":makeQuery(id+"F23.opPattern","COPY",BODY,{"derivedFrom":makeQuery(id+"F7.opPattern","COPY",BODY,{"derivedFrom":makeQuery(id+"F1.opExtrude","SWEPT_BODY",BODY,{"disambiguationData":[OSD([sQuery(id+"F0.wireOp",EDGE,"E2.0"),sQuery(id+"F0.wireOp",EDGE,"E2.1"),sQuery(id+"F0.wireOp",EDGE,"E2.2"),sQuery(id+"F0.wireOp",EDGE,"E2.3"),sQuery(id+"F0.wireOp",EDGE,"E2.4"),sQuery(id+"F0.wireOp",EDGE,"E2.5"),sQuery(id+"F0.wireOp",EDGE,"E3"),sQuery(id+"F0.wireOp",EDGE,"E4"),sQuery(id+"F0.wireOp",EDGE,"E5.0"),sQuery(id+"F0.wireOp",EDGE,"E5.1"),sQuery(id+"F0.wireOp",EDGE,"E5.3"),sQuery(id+"F0.wireOp",EDGE,"E5.4"),sQuery(id+"F0.wireOp",EDGE,"E5.5"),sQuery(id+"F0.wireOp",EDGE,"E6.trimOffspring"),sQuery(id+"F0.wireOp",EDGE,"E7.trimOffspring"),sQuery(id+"F0.wireOp",EDGE,"E9.trimOffspring"),sQuery(id+"F0.wireOp",EDGE,"E10.1.0"),sQuery(id+"F0.wireOp",EDGE,"E10.1.1"),sQuery(id+"F0.wireOp",EDGE,"E10.1.2"),sQuery(id+"F0.wireOp",EDGE,"E10.1.3"),sQuery(id+"F0.wireOp",EDGE,"E10.1.5"),sQuery(id+"F0.wireOp",EDGE,"E10.1.7"),sQuery(id+"F0.wireOp",EDGE,"E10.1.8"),sQuery(id+"F0.wireOp",EDGE,"E10.1.9"),sQuery(id+"F0.wireOp",EDGE,"E10.1.10"),sQuery(id+"F0.wireOp",EDGE,"E10.1.11"),sQuery(id+"F0.wireOp",EDGE,"E10.1.12"),sQuery(id+"F0.wireOp",EDGE,"E10.1.14"),sQuery(id+"F0.wireOp",EDGE,"E10.1.15"),sQuery(id+"F0.wireOp",EDGE,"E10.1.16"),sQuery(id+"F0.wireOp",EDGE,"E10.1.18"),sQuery(id+"F0.wireOp",EDGE,"E10.1.20"),sQuery(id+"F0.wireOp",EDGE,"E10.2.0"),sQuery(id+"F0.wireOp",EDGE,"E10.2.1"),sQuery(id+"F0.wireOp",EDGE,"E10.2.2"),sQuery(id+"F0.wireOp",EDGE,"E10.2.3"),sQuery(id+"F0.wireOp",EDGE,"E10.2.5"),sQuery(id+"F0.wireOp",EDGE,"E10.2.7"),sQuery(id+"F0.wireOp",EDGE,"E10.2.8"),sQuery(id+"F0.wireOp",EDGE,"E10.2.9"),sQuery(id+"F0.wireOp",EDGE,"E10.2.10"),sQuery(id+"F0.wireOp",EDGE,"E10.2.11"),sQuery(id+"F0.wireOp",EDGE,"E10.2.12"),sQuery(id+"F0.wireOp",EDGE,"E1"),sQuery(id+"F0.wireOp",EDGE,"E10.2.14"),sQuery(id+"F0.wireOp",EDGE,"E10.2.15"),sQuery(id+"F0.wireOp",EDGE,"E10.2.16"),sQuery(id+"F0.wireOp",EDGE,"E10.2.18"),sQuery(id+"F0.wireOp",EDGE,"E10.2.20"),sQuery(id+"F0.wireOp",EDGE,"E8.trimOffspring"),sQuery(id+"F0.wireOp",EDGE,"E0"),sQuery(id+"F0.wireOp",EDGE,"E10.1.6"),sQuery(id+"F0.wireOp",EDGE,"E11"),sQuery(id+"F0.wireOp",EDGE,"E12"),sQuery(id+"F0.wireOp",EDGE,"E13.1.0"),sQuery(id+"F0.wireOp",EDGE,"E13.1.1"),sQuery(id+"F0.wireOp",EDGE,"E13.2.0"),sQuery(id+"F0.wireOp",EDGE,"E13.2.1")])]}),"instanceName":"1"}),"instanceName":"1"}),"instanceName":"1"}),"instanceName":"1"}),"instanceName":"1"});
            var Q16;
            Q16=makeQuery(id+"F51.opPattern","COPY",BODY,{"derivedFrom":makeQuery(id+"F39.opPattern","COPY",BODY,{"derivedFrom":makeQuery(id+"F36.opPattern","COPY",BODY,{"derivedFrom":makeQuery(id+"F23.opPattern","COPY",BODY,{"derivedFrom":makeQuery(id+"F7.opPattern","COPY",BODY,{"derivedFrom":makeQuery(id+"F1.opExtrude","SWEPT_BODY",BODY,{"disambiguationData":[OSD([sQuery(id+"F0.wireOp",EDGE,"E2.0"),sQuery(id+"F0.wireOp",EDGE,"E2.1"),sQuery(id+"F0.wireOp",EDGE,"E2.2"),sQuery(id+"F0.wireOp",EDGE,"E2.3"),sQuery(id+"F0.wireOp",EDGE,"E2.4"),sQuery(id+"F0.wireOp",EDGE,"E2.5"),sQuery(id+"F0.wireOp",EDGE,"E3"),sQuery(id+"F0.wireOp",EDGE,"E4"),sQuery(id+"F0.wireOp",EDGE,"E5.0"),sQuery(id+"F0.wireOp",EDGE,"E5.1"),sQuery(id+"F0.wireOp",EDGE,"E5.3"),sQuery(id+"F0.wireOp",EDGE,"E5.4"),sQuery(id+"F0.wireOp",EDGE,"E5.5"),sQuery(id+"F0.wireOp",EDGE,"E6.trimOffspring"),sQuery(id+"F0.wireOp",EDGE,"E7.trimOffspring"),sQuery(id+"F0.wireOp",EDGE,"E9.trimOffspring"),sQuery(id+"F0.wireOp",EDGE,"E10.1.0"),sQuery(id+"F0.wireOp",EDGE,"E10.1.1"),sQuery(id+"F0.wireOp",EDGE,"E10.1.2"),sQuery(id+"F0.wireOp",EDGE,"E10.1.3"),sQuery(id+"F0.wireOp",EDGE,"E10.1.5"),sQuery(id+"F0.wireOp",EDGE,"E10.1.7"),sQuery(id+"F0.wireOp",EDGE,"E10.1.8"),sQuery(id+"F0.wireOp",EDGE,"E10.1.9"),sQuery(id+"F0.wireOp",EDGE,"E10.1.10"),sQuery(id+"F0.wireOp",EDGE,"E10.1.11"),sQuery(id+"F0.wireOp",EDGE,"E10.1.12"),sQuery(id+"F0.wireOp",EDGE,"E10.1.14"),sQuery(id+"F0.wireOp",EDGE,"E10.1.15"),sQuery(id+"F0.wireOp",EDGE,"E10.1.16"),sQuery(id+"F0.wireOp",EDGE,"E10.1.18"),sQuery(id+"F0.wireOp",EDGE,"E10.1.20"),sQuery(id+"F0.wireOp",EDGE,"E10.2.0"),sQuery(id+"F0.wireOp",EDGE,"E10.2.1"),sQuery(id+"F0.wireOp",EDGE,"E10.2.2"),sQuery(id+"F0.wireOp",EDGE,"E10.2.3"),sQuery(id+"F0.wireOp",EDGE,"E10.2.5"),sQuery(id+"F0.wireOp",EDGE,"E10.2.7"),sQuery(id+"F0.wireOp",EDGE,"E10.2.8"),sQuery(id+"F0.wireOp",EDGE,"E10.2.9"),sQuery(id+"F0.wireOp",EDGE,"E10.2.10"),sQuery(id+"F0.wireOp",EDGE,"E10.2.11"),sQuery(id+"F0.wireOp",EDGE,"E10.2.12"),sQuery(id+"F0.wireOp",EDGE,"E1"),sQuery(id+"F0.wireOp",EDGE,"E10.2.14"),sQuery(id+"F0.wireOp",EDGE,"E10.2.15"),sQuery(id+"F0.wireOp",EDGE,"E10.2.16"),sQuery(id+"F0.wireOp",EDGE,"E10.2.18"),sQuery(id+"F0.wireOp",EDGE,"E10.2.20"),sQuery(id+"F0.wireOp",EDGE,"E8.trimOffspring"),sQuery(id+"F0.wireOp",EDGE,"E0"),sQuery(id+"F0.wireOp",EDGE,"E10.1.6"),sQuery(id+"F0.wireOp",EDGE,"E11"),sQuery(id+"F0.wireOp",EDGE,"E12"),sQuery(id+"F0.wireOp",EDGE,"E13.1.0"),sQuery(id+"F0.wireOp",EDGE,"E13.1.1"),sQuery(id+"F0.wireOp",EDGE,"E13.2.0"),sQuery(id+"F0.wireOp",EDGE,"E13.2.1")])]}),"instanceName":"1"}),"instanceName":"1"}),"instanceName":"1"}),"instanceName":"1"}),"instanceName":"1"});
            var Q17;
            Q17=makeQuery(id+"F52.opPattern","COPY",BODY,{"derivedFrom":makeQuery(id+"F39.opPattern","COPY",BODY,{"derivedFrom":makeQuery(id+"F36.opPattern","COPY",BODY,{"derivedFrom":makeQuery(id+"F23.opPattern","COPY",BODY,{"derivedFrom":makeQuery(id+"F7.opPattern","COPY",BODY,{"derivedFrom":makeQuery(id+"F1.opExtrude","SWEPT_BODY",BODY,{"disambiguationData":[OSD([sQuery(id+"F0.wireOp",EDGE,"E2.0"),sQuery(id+"F0.wireOp",EDGE,"E2.1"),sQuery(id+"F0.wireOp",EDGE,"E2.2"),sQuery(id+"F0.wireOp",EDGE,"E2.3"),sQuery(id+"F0.wireOp",EDGE,"E2.4"),sQuery(id+"F0.wireOp",EDGE,"E2.5"),sQuery(id+"F0.wireOp",EDGE,"E3"),sQuery(id+"F0.wireOp",EDGE,"E4"),sQuery(id+"F0.wireOp",EDGE,"E5.0"),sQuery(id+"F0.wireOp",EDGE,"E5.1"),sQuery(id+"F0.wireOp",EDGE,"E5.3"),sQuery(id+"F0.wireOp",EDGE,"E5.4"),sQuery(id+"F0.wireOp",EDGE,"E5.5"),sQuery(id+"F0.wireOp",EDGE,"E6.trimOffspring"),sQuery(id+"F0.wireOp",EDGE,"E7.trimOffspring"),sQuery(id+"F0.wireOp",EDGE,"E9.trimOffspring"),sQuery(id+"F0.wireOp",EDGE,"E10.1.0"),sQuery(id+"F0.wireOp",EDGE,"E10.1.1"),sQuery(id+"F0.wireOp",EDGE,"E10.1.2"),sQuery(id+"F0.wireOp",EDGE,"E10.1.3"),sQuery(id+"F0.wireOp",EDGE,"E10.1.5"),sQuery(id+"F0.wireOp",EDGE,"E10.1.7"),sQuery(id+"F0.wireOp",EDGE,"E10.1.8"),sQuery(id+"F0.wireOp",EDGE,"E10.1.9"),sQuery(id+"F0.wireOp",EDGE,"E10.1.10"),sQuery(id+"F0.wireOp",EDGE,"E10.1.11"),sQuery(id+"F0.wireOp",EDGE,"E10.1.12"),sQuery(id+"F0.wireOp",EDGE,"E10.1.14"),sQuery(id+"F0.wireOp",EDGE,"E10.1.15"),sQuery(id+"F0.wireOp",EDGE,"E10.1.16"),sQuery(id+"F0.wireOp",EDGE,"E10.1.18"),sQuery(id+"F0.wireOp",EDGE,"E10.1.20"),sQuery(id+"F0.wireOp",EDGE,"E10.2.0"),sQuery(id+"F0.wireOp",EDGE,"E10.2.1"),sQuery(id+"F0.wireOp",EDGE,"E10.2.2"),sQuery(id+"F0.wireOp",EDGE,"E10.2.3"),sQuery(id+"F0.wireOp",EDGE,"E10.2.5"),sQuery(id+"F0.wireOp",EDGE,"E10.2.7"),sQuery(id+"F0.wireOp",EDGE,"E10.2.8"),sQuery(id+"F0.wireOp",EDGE,"E10.2.9"),sQuery(id+"F0.wireOp",EDGE,"E10.2.10"),sQuery(id+"F0.wireOp",EDGE,"E10.2.11"),sQuery(id+"F0.wireOp",EDGE,"E10.2.12"),sQuery(id+"F0.wireOp",EDGE,"E1"),sQuery(id+"F0.wireOp",EDGE,"E10.2.14"),sQuery(id+"F0.wireOp",EDGE,"E10.2.15"),sQuery(id+"F0.wireOp",EDGE,"E10.2.16"),sQuery(id+"F0.wireOp",EDGE,"E10.2.18"),sQuery(id+"F0.wireOp",EDGE,"E10.2.20"),sQuery(id+"F0.wireOp",EDGE,"E8.trimOffspring"),sQuery(id+"F0.wireOp",EDGE,"E0"),sQuery(id+"F0.wireOp",EDGE,"E10.1.6"),sQuery(id+"F0.wireOp",EDGE,"E11"),sQuery(id+"F0.wireOp",EDGE,"E12"),sQuery(id+"F0.wireOp",EDGE,"E13.1.0"),sQuery(id+"F0.wireOp",EDGE,"E13.1.1"),sQuery(id+"F0.wireOp",EDGE,"E13.2.0"),sQuery(id+"F0.wireOp",EDGE,"E13.2.1")])]}),"instanceName":"1"}),"instanceName":"1"}),"instanceName":"1"}),"instanceName":"1"}),"instanceName":"1"});
            var Q18;
            Q18=makeQuery(id+"F53.opPattern","COPY",BODY,{"derivedFrom":makeQuery(id+"F52.opPattern","COPY",BODY,{"derivedFrom":makeQuery(id+"F39.opPattern","COPY",BODY,{"derivedFrom":makeQuery(id+"F36.opPattern","COPY",BODY,{"derivedFrom":makeQuery(id+"F23.opPattern","COPY",BODY,{"derivedFrom":makeQuery(id+"F7.opPattern","COPY",BODY,{"derivedFrom":makeQuery(id+"F1.opExtrude","SWEPT_BODY",BODY,{"disambiguationData":[OSD([sQuery(id+"F0.wireOp",EDGE,"E2.0"),sQuery(id+"F0.wireOp",EDGE,"E2.1"),sQuery(id+"F0.wireOp",EDGE,"E2.2"),sQuery(id+"F0.wireOp",EDGE,"E2.3"),sQuery(id+"F0.wireOp",EDGE,"E2.4"),sQuery(id+"F0.wireOp",EDGE,"E2.5"),sQuery(id+"F0.wireOp",EDGE,"E3"),sQuery(id+"F0.wireOp",EDGE,"E4"),sQuery(id+"F0.wireOp",EDGE,"E5.0"),sQuery(id+"F0.wireOp",EDGE,"E5.1"),sQuery(id+"F0.wireOp",EDGE,"E5.3"),sQuery(id+"F0.wireOp",EDGE,"E5.4"),sQuery(id+"F0.wireOp",EDGE,"E5.5"),sQuery(id+"F0.wireOp",EDGE,"E6.trimOffspring"),sQuery(id+"F0.wireOp",EDGE,"E7.trimOffspring"),sQuery(id+"F0.wireOp",EDGE,"E9.trimOffspring"),sQuery(id+"F0.wireOp",EDGE,"E10.1.0"),sQuery(id+"F0.wireOp",EDGE,"E10.1.1"),sQuery(id+"F0.wireOp",EDGE,"E10.1.2"),sQuery(id+"F0.wireOp",EDGE,"E10.1.3"),sQuery(id+"F0.wireOp",EDGE,"E10.1.5"),sQuery(id+"F0.wireOp",EDGE,"E10.1.7"),sQuery(id+"F0.wireOp",EDGE,"E10.1.8"),sQuery(id+"F0.wireOp",EDGE,"E10.1.9"),sQuery(id+"F0.wireOp",EDGE,"E10.1.10"),sQuery(id+"F0.wireOp",EDGE,"E10.1.11"),sQuery(id+"F0.wireOp",EDGE,"E10.1.12"),sQuery(id+"F0.wireOp",EDGE,"E10.1.14"),sQuery(id+"F0.wireOp",EDGE,"E10.1.15"),sQuery(id+"F0.wireOp",EDGE,"E10.1.16"),sQuery(id+"F0.wireOp",EDGE,"E10.1.18"),sQuery(id+"F0.wireOp",EDGE,"E10.1.20"),sQuery(id+"F0.wireOp",EDGE,"E10.2.0"),sQuery(id+"F0.wireOp",EDGE,"E10.2.1"),sQuery(id+"F0.wireOp",EDGE,"E10.2.2"),sQuery(id+"F0.wireOp",EDGE,"E10.2.3"),sQuery(id+"F0.wireOp",EDGE,"E10.2.5"),sQuery(id+"F0.wireOp",EDGE,"E10.2.7"),sQuery(id+"F0.wireOp",EDGE,"E10.2.8"),sQuery(id+"F0.wireOp",EDGE,"E10.2.9"),sQuery(id+"F0.wireOp",EDGE,"E10.2.10"),sQuery(id+"F0.wireOp",EDGE,"E10.2.11"),sQuery(id+"F0.wireOp",EDGE,"E10.2.12"),sQuery(id+"F0.wireOp",EDGE,"E1"),sQuery(id+"F0.wireOp",EDGE,"E10.2.14"),sQuery(id+"F0.wireOp",EDGE,"E10.2.15"),sQuery(id+"F0.wireOp",EDGE,"E10.2.16"),sQuery(id+"F0.wireOp",EDGE,"E10.2.18"),sQuery(id+"F0.wireOp",EDGE,"E10.2.20"),sQuery(id+"F0.wireOp",EDGE,"E8.trimOffspring"),sQuery(id+"F0.wireOp",EDGE,"E0"),sQuery(id+"F0.wireOp",EDGE,"E10.1.6"),sQuery(id+"F0.wireOp",EDGE,"E11"),sQuery(id+"F0.wireOp",EDGE,"E12"),sQuery(id+"F0.wireOp",EDGE,"E13.1.0"),sQuery(id+"F0.wireOp",EDGE,"E13.1.1"),sQuery(id+"F0.wireOp",EDGE,"E13.2.0"),sQuery(id+"F0.wireOp",EDGE,"E13.2.1")])]}),"instanceName":"1"}),"instanceName":"1"}),"instanceName":"1"}),"instanceName":"1"}),"instanceName":"1"}),"instanceName":"1"});
            var Q19;
            Q19=makeQuery(id+"F54.opPattern","COPY",BODY,{"derivedFrom":makeQuery(id+"F36.opPattern","COPY",BODY,{"derivedFrom":makeQuery(id+"F23.opPattern","COPY",BODY,{"derivedFrom":makeQuery(id+"F7.opPattern","COPY",BODY,{"derivedFrom":makeQuery(id+"F1.opExtrude","SWEPT_BODY",BODY,{"disambiguationData":[OSD([sQuery(id+"F0.wireOp",EDGE,"E2.0"),sQuery(id+"F0.wireOp",EDGE,"E2.1"),sQuery(id+"F0.wireOp",EDGE,"E2.2"),sQuery(id+"F0.wireOp",EDGE,"E2.3"),sQuery(id+"F0.wireOp",EDGE,"E2.4"),sQuery(id+"F0.wireOp",EDGE,"E2.5"),sQuery(id+"F0.wireOp",EDGE,"E3"),sQuery(id+"F0.wireOp",EDGE,"E4"),sQuery(id+"F0.wireOp",EDGE,"E5.0"),sQuery(id+"F0.wireOp",EDGE,"E5.1"),sQuery(id+"F0.wireOp",EDGE,"E5.3"),sQuery(id+"F0.wireOp",EDGE,"E5.4"),sQuery(id+"F0.wireOp",EDGE,"E5.5"),sQuery(id+"F0.wireOp",EDGE,"E6.trimOffspring"),sQuery(id+"F0.wireOp",EDGE,"E7.trimOffspring"),sQuery(id+"F0.wireOp",EDGE,"E9.trimOffspring"),sQuery(id+"F0.wireOp",EDGE,"E10.1.0"),sQuery(id+"F0.wireOp",EDGE,"E10.1.1"),sQuery(id+"F0.wireOp",EDGE,"E10.1.2"),sQuery(id+"F0.wireOp",EDGE,"E10.1.3"),sQuery(id+"F0.wireOp",EDGE,"E10.1.5"),sQuery(id+"F0.wireOp",EDGE,"E10.1.7"),sQuery(id+"F0.wireOp",EDGE,"E10.1.8"),sQuery(id+"F0.wireOp",EDGE,"E10.1.9"),sQuery(id+"F0.wireOp",EDGE,"E10.1.10"),sQuery(id+"F0.wireOp",EDGE,"E10.1.11"),sQuery(id+"F0.wireOp",EDGE,"E10.1.12"),sQuery(id+"F0.wireOp",EDGE,"E10.1.14"),sQuery(id+"F0.wireOp",EDGE,"E10.1.15"),sQuery(id+"F0.wireOp",EDGE,"E10.1.16"),sQuery(id+"F0.wireOp",EDGE,"E10.1.18"),sQuery(id+"F0.wireOp",EDGE,"E10.1.20"),sQuery(id+"F0.wireOp",EDGE,"E10.2.0"),sQuery(id+"F0.wireOp",EDGE,"E10.2.1"),sQuery(id+"F0.wireOp",EDGE,"E10.2.2"),sQuery(id+"F0.wireOp",EDGE,"E10.2.3"),sQuery(id+"F0.wireOp",EDGE,"E10.2.5"),sQuery(id+"F0.wireOp",EDGE,"E10.2.7"),sQuery(id+"F0.wireOp",EDGE,"E10.2.8"),sQuery(id+"F0.wireOp",EDGE,"E10.2.9"),sQuery(id+"F0.wireOp",EDGE,"E10.2.10"),sQuery(id+"F0.wireOp",EDGE,"E10.2.11"),sQuery(id+"F0.wireOp",EDGE,"E10.2.12"),sQuery(id+"F0.wireOp",EDGE,"E1"),sQuery(id+"F0.wireOp",EDGE,"E10.2.14"),sQuery(id+"F0.wireOp",EDGE,"E10.2.15"),sQuery(id+"F0.wireOp",EDGE,"E10.2.16"),sQuery(id+"F0.wireOp",EDGE,"E10.2.18"),sQuery(id+"F0.wireOp",EDGE,"E10.2.20"),sQuery(id+"F0.wireOp",EDGE,"E8.trimOffspring"),sQuery(id+"F0.wireOp",EDGE,"E0"),sQuery(id+"F0.wireOp",EDGE,"E10.1.6"),sQuery(id+"F0.wireOp",EDGE,"E11"),sQuery(id+"F0.wireOp",EDGE,"E12"),sQuery(id+"F0.wireOp",EDGE,"E13.1.0"),sQuery(id+"F0.wireOp",EDGE,"E13.1.1"),sQuery(id+"F0.wireOp",EDGE,"E13.2.0"),sQuery(id+"F0.wireOp",EDGE,"E13.2.1")])]}),"instanceName":"1"}),"instanceName":"1"}),"instanceName":"1"}),"instanceName":"1"});
            var Q20;
            Q20=makeQuery(id+"F55.opPattern","COPY",BODY,{"derivedFrom":makeQuery(id+"F46.opPattern","COPY",BODY,{"derivedFrom":makeQuery(id+"F45.opPattern","COPY",BODY,{"derivedFrom":makeQuery(id+"F5.opPattern","COPY",BODY,{"derivedFrom":makeQuery(id+"F1.opExtrude","SWEPT_BODY",BODY,{"disambiguationData":[OSD([sQuery(id+"F0.wireOp",EDGE,"E2.0"),sQuery(id+"F0.wireOp",EDGE,"E2.1"),sQuery(id+"F0.wireOp",EDGE,"E2.2"),sQuery(id+"F0.wireOp",EDGE,"E2.3"),sQuery(id+"F0.wireOp",EDGE,"E2.4"),sQuery(id+"F0.wireOp",EDGE,"E2.5"),sQuery(id+"F0.wireOp",EDGE,"E3"),sQuery(id+"F0.wireOp",EDGE,"E4"),sQuery(id+"F0.wireOp",EDGE,"E5.0"),sQuery(id+"F0.wireOp",EDGE,"E5.1"),sQuery(id+"F0.wireOp",EDGE,"E5.3"),sQuery(id+"F0.wireOp",EDGE,"E5.4"),sQuery(id+"F0.wireOp",EDGE,"E5.5"),sQuery(id+"F0.wireOp",EDGE,"E6.trimOffspring"),sQuery(id+"F0.wireOp",EDGE,"E7.trimOffspring"),sQuery(id+"F0.wireOp",EDGE,"E9.trimOffspring"),sQuery(id+"F0.wireOp",EDGE,"E10.1.0"),sQuery(id+"F0.wireOp",EDGE,"E10.1.1"),sQuery(id+"F0.wireOp",EDGE,"E10.1.2"),sQuery(id+"F0.wireOp",EDGE,"E10.1.3"),sQuery(id+"F0.wireOp",EDGE,"E10.1.5"),sQuery(id+"F0.wireOp",EDGE,"E10.1.7"),sQuery(id+"F0.wireOp",EDGE,"E10.1.8"),sQuery(id+"F0.wireOp",EDGE,"E10.1.9"),sQuery(id+"F0.wireOp",EDGE,"E10.1.10"),sQuery(id+"F0.wireOp",EDGE,"E10.1.11"),sQuery(id+"F0.wireOp",EDGE,"E10.1.12"),sQuery(id+"F0.wireOp",EDGE,"E10.1.14"),sQuery(id+"F0.wireOp",EDGE,"E10.1.15"),sQuery(id+"F0.wireOp",EDGE,"E10.1.16"),sQuery(id+"F0.wireOp",EDGE,"E10.1.18"),sQuery(id+"F0.wireOp",EDGE,"E10.1.20"),sQuery(id+"F0.wireOp",EDGE,"E10.2.0"),sQuery(id+"F0.wireOp",EDGE,"E10.2.1"),sQuery(id+"F0.wireOp",EDGE,"E10.2.2"),sQuery(id+"F0.wireOp",EDGE,"E10.2.3"),sQuery(id+"F0.wireOp",EDGE,"E10.2.5"),sQuery(id+"F0.wireOp",EDGE,"E10.2.7"),sQuery(id+"F0.wireOp",EDGE,"E10.2.8"),sQuery(id+"F0.wireOp",EDGE,"E10.2.9"),sQuery(id+"F0.wireOp",EDGE,"E10.2.10"),sQuery(id+"F0.wireOp",EDGE,"E10.2.11"),sQuery(id+"F0.wireOp",EDGE,"E10.2.12"),sQuery(id+"F0.wireOp",EDGE,"E1"),sQuery(id+"F0.wireOp",EDGE,"E10.2.14"),sQuery(id+"F0.wireOp",EDGE,"E10.2.15"),sQuery(id+"F0.wireOp",EDGE,"E10.2.16"),sQuery(id+"F0.wireOp",EDGE,"E10.2.18"),sQuery(id+"F0.wireOp",EDGE,"E10.2.20"),sQuery(id+"F0.wireOp",EDGE,"E8.trimOffspring"),sQuery(id+"F0.wireOp",EDGE,"E0"),sQuery(id+"F0.wireOp",EDGE,"E10.1.6"),sQuery(id+"F0.wireOp",EDGE,"E11"),sQuery(id+"F0.wireOp",EDGE,"E12"),sQuery(id+"F0.wireOp",EDGE,"E13.1.0"),sQuery(id+"F0.wireOp",EDGE,"E13.1.1"),sQuery(id+"F0.wireOp",EDGE,"E13.2.0"),sQuery(id+"F0.wireOp",EDGE,"E13.2.1")])]}),"instanceName":"1"}),"instanceName":"1"}),"instanceName":"1"}),"instanceName":"1"});
            var Q21;
            Q21=makeQuery(id+"F56.opPattern","COPY",BODY,{"derivedFrom":makeQuery(id+"F13.opPattern","COPY",BODY,{"derivedFrom":makeQuery(id+"F1.opExtrude","SWEPT_BODY",BODY,{"disambiguationData":[OSD([sQuery(id+"F0.wireOp",EDGE,"E2.0"),sQuery(id+"F0.wireOp",EDGE,"E2.1"),sQuery(id+"F0.wireOp",EDGE,"E2.2"),sQuery(id+"F0.wireOp",EDGE,"E2.3"),sQuery(id+"F0.wireOp",EDGE,"E2.4"),sQuery(id+"F0.wireOp",EDGE,"E2.5"),sQuery(id+"F0.wireOp",EDGE,"E3"),sQuery(id+"F0.wireOp",EDGE,"E4"),sQuery(id+"F0.wireOp",EDGE,"E5.0"),sQuery(id+"F0.wireOp",EDGE,"E5.1"),sQuery(id+"F0.wireOp",EDGE,"E5.3"),sQuery(id+"F0.wireOp",EDGE,"E5.4"),sQuery(id+"F0.wireOp",EDGE,"E5.5"),sQuery(id+"F0.wireOp",EDGE,"E6.trimOffspring"),sQuery(id+"F0.wireOp",EDGE,"E7.trimOffspring"),sQuery(id+"F0.wireOp",EDGE,"E9.trimOffspring"),sQuery(id+"F0.wireOp",EDGE,"E10.1.0"),sQuery(id+"F0.wireOp",EDGE,"E10.1.1"),sQuery(id+"F0.wireOp",EDGE,"E10.1.2"),sQuery(id+"F0.wireOp",EDGE,"E10.1.3"),sQuery(id+"F0.wireOp",EDGE,"E10.1.5"),sQuery(id+"F0.wireOp",EDGE,"E10.1.7"),sQuery(id+"F0.wireOp",EDGE,"E10.1.8"),sQuery(id+"F0.wireOp",EDGE,"E10.1.9"),sQuery(id+"F0.wireOp",EDGE,"E10.1.10"),sQuery(id+"F0.wireOp",EDGE,"E10.1.11"),sQuery(id+"F0.wireOp",EDGE,"E10.1.12"),sQuery(id+"F0.wireOp",EDGE,"E10.1.14"),sQuery(id+"F0.wireOp",EDGE,"E10.1.15"),sQuery(id+"F0.wireOp",EDGE,"E10.1.16"),sQuery(id+"F0.wireOp",EDGE,"E10.1.18"),sQuery(id+"F0.wireOp",EDGE,"E10.1.20"),sQuery(id+"F0.wireOp",EDGE,"E10.2.0"),sQuery(id+"F0.wireOp",EDGE,"E10.2.1"),sQuery(id+"F0.wireOp",EDGE,"E10.2.2"),sQuery(id+"F0.wireOp",EDGE,"E10.2.3"),sQuery(id+"F0.wireOp",EDGE,"E10.2.5"),sQuery(id+"F0.wireOp",EDGE,"E10.2.7"),sQuery(id+"F0.wireOp",EDGE,"E10.2.8"),sQuery(id+"F0.wireOp",EDGE,"E10.2.9"),sQuery(id+"F0.wireOp",EDGE,"E10.2.10"),sQuery(id+"F0.wireOp",EDGE,"E10.2.11"),sQuery(id+"F0.wireOp",EDGE,"E10.2.12"),sQuery(id+"F0.wireOp",EDGE,"E1"),sQuery(id+"F0.wireOp",EDGE,"E10.2.14"),sQuery(id+"F0.wireOp",EDGE,"E10.2.15"),sQuery(id+"F0.wireOp",EDGE,"E10.2.16"),sQuery(id+"F0.wireOp",EDGE,"E10.2.18"),sQuery(id+"F0.wireOp",EDGE,"E10.2.20"),sQuery(id+"F0.wireOp",EDGE,"E8.trimOffspring"),sQuery(id+"F0.wireOp",EDGE,"E0"),sQuery(id+"F0.wireOp",EDGE,"E10.1.6"),sQuery(id+"F0.wireOp",EDGE,"E11"),sQuery(id+"F0.wireOp",EDGE,"E12"),sQuery(id+"F0.wireOp",EDGE,"E13.1.0"),sQuery(id+"F0.wireOp",EDGE,"E13.1.1"),sQuery(id+"F0.wireOp",EDGE,"E13.2.0"),sQuery(id+"F0.wireOp",EDGE,"E13.2.1")])]}),"instanceName":"1"}),"instanceName":"1"});
            var Q22;
            Q22=makeQuery(id+"F56.opPattern","COPY",BODY,{"derivedFrom":makeQuery(id+"F18.opPattern","COPY",BODY,{"derivedFrom":makeQuery(id+"F13.opPattern","COPY",BODY,{"derivedFrom":makeQuery(id+"F1.opExtrude","SWEPT_BODY",BODY,{"disambiguationData":[OSD([sQuery(id+"F0.wireOp",EDGE,"E2.0"),sQuery(id+"F0.wireOp",EDGE,"E2.1"),sQuery(id+"F0.wireOp",EDGE,"E2.2"),sQuery(id+"F0.wireOp",EDGE,"E2.3"),sQuery(id+"F0.wireOp",EDGE,"E2.4"),sQuery(id+"F0.wireOp",EDGE,"E2.5"),sQuery(id+"F0.wireOp",EDGE,"E3"),sQuery(id+"F0.wireOp",EDGE,"E4"),sQuery(id+"F0.wireOp",EDGE,"E5.0"),sQuery(id+"F0.wireOp",EDGE,"E5.1"),sQuery(id+"F0.wireOp",EDGE,"E5.3"),sQuery(id+"F0.wireOp",EDGE,"E5.4"),sQuery(id+"F0.wireOp",EDGE,"E5.5"),sQuery(id+"F0.wireOp",EDGE,"E6.trimOffspring"),sQuery(id+"F0.wireOp",EDGE,"E7.trimOffspring"),sQuery(id+"F0.wireOp",EDGE,"E9.trimOffspring"),sQuery(id+"F0.wireOp",EDGE,"E10.1.0"),sQuery(id+"F0.wireOp",EDGE,"E10.1.1"),sQuery(id+"F0.wireOp",EDGE,"E10.1.2"),sQuery(id+"F0.wireOp",EDGE,"E10.1.3"),sQuery(id+"F0.wireOp",EDGE,"E10.1.5"),sQuery(id+"F0.wireOp",EDGE,"E10.1.7"),sQuery(id+"F0.wireOp",EDGE,"E10.1.8"),sQuery(id+"F0.wireOp",EDGE,"E10.1.9"),sQuery(id+"F0.wireOp",EDGE,"E10.1.10"),sQuery(id+"F0.wireOp",EDGE,"E10.1.11"),sQuery(id+"F0.wireOp",EDGE,"E10.1.12"),sQuery(id+"F0.wireOp",EDGE,"E10.1.14"),sQuery(id+"F0.wireOp",EDGE,"E10.1.15"),sQuery(id+"F0.wireOp",EDGE,"E10.1.16"),sQuery(id+"F0.wireOp",EDGE,"E10.1.18"),sQuery(id+"F0.wireOp",EDGE,"E10.1.20"),sQuery(id+"F0.wireOp",EDGE,"E10.2.0"),sQuery(id+"F0.wireOp",EDGE,"E10.2.1"),sQuery(id+"F0.wireOp",EDGE,"E10.2.2"),sQuery(id+"F0.wireOp",EDGE,"E10.2.3"),sQuery(id+"F0.wireOp",EDGE,"E10.2.5"),sQuery(id+"F0.wireOp",EDGE,"E10.2.7"),sQuery(id+"F0.wireOp",EDGE,"E10.2.8"),sQuery(id+"F0.wireOp",EDGE,"E10.2.9"),sQuery(id+"F0.wireOp",EDGE,"E10.2.10"),sQuery(id+"F0.wireOp",EDGE,"E10.2.11"),sQuery(id+"F0.wireOp",EDGE,"E10.2.12"),sQuery(id+"F0.wireOp",EDGE,"E1"),sQuery(id+"F0.wireOp",EDGE,"E10.2.14"),sQuery(id+"F0.wireOp",EDGE,"E10.2.15"),sQuery(id+"F0.wireOp",EDGE,"E10.2.16"),sQuery(id+"F0.wireOp",EDGE,"E10.2.18"),sQuery(id+"F0.wireOp",EDGE,"E10.2.20"),sQuery(id+"F0.wireOp",EDGE,"E8.trimOffspring"),sQuery(id+"F0.wireOp",EDGE,"E0"),sQuery(id+"F0.wireOp",EDGE,"E10.1.6"),sQuery(id+"F0.wireOp",EDGE,"E11"),sQuery(id+"F0.wireOp",EDGE,"E12"),sQuery(id+"F0.wireOp",EDGE,"E13.1.0"),sQuery(id+"F0.wireOp",EDGE,"E13.1.1"),sQuery(id+"F0.wireOp",EDGE,"E13.2.0"),sQuery(id+"F0.wireOp",EDGE,"E13.2.1")])]}),"instanceName":"1"}),"instanceName":"1"}),"instanceName":"1"});
            var Q23;
            Q23=makeQuery(id+"F56.opPattern","COPY",BODY,{"derivedFrom":makeQuery(id+"F19.opPattern","COPY",BODY,{"derivedFrom":makeQuery(id+"F18.opPattern","COPY",BODY,{"derivedFrom":makeQuery(id+"F13.opPattern","COPY",BODY,{"derivedFrom":makeQuery(id+"F1.opExtrude","SWEPT_BODY",BODY,{"disambiguationData":[OSD([sQuery(id+"F0.wireOp",EDGE,"E2.0"),sQuery(id+"F0.wireOp",EDGE,"E2.1"),sQuery(id+"F0.wireOp",EDGE,"E2.2"),sQuery(id+"F0.wireOp",EDGE,"E2.3"),sQuery(id+"F0.wireOp",EDGE,"E2.4"),sQuery(id+"F0.wireOp",EDGE,"E2.5"),sQuery(id+"F0.wireOp",EDGE,"E3"),sQuery(id+"F0.wireOp",EDGE,"E4"),sQuery(id+"F0.wireOp",EDGE,"E5.0"),sQuery(id+"F0.wireOp",EDGE,"E5.1"),sQuery(id+"F0.wireOp",EDGE,"E5.3"),sQuery(id+"F0.wireOp",EDGE,"E5.4"),sQuery(id+"F0.wireOp",EDGE,"E5.5"),sQuery(id+"F0.wireOp",EDGE,"E6.trimOffspring"),sQuery(id+"F0.wireOp",EDGE,"E7.trimOffspring"),sQuery(id+"F0.wireOp",EDGE,"E9.trimOffspring"),sQuery(id+"F0.wireOp",EDGE,"E10.1.0"),sQuery(id+"F0.wireOp",EDGE,"E10.1.1"),sQuery(id+"F0.wireOp",EDGE,"E10.1.2"),sQuery(id+"F0.wireOp",EDGE,"E10.1.3"),sQuery(id+"F0.wireOp",EDGE,"E10.1.5"),sQuery(id+"F0.wireOp",EDGE,"E10.1.7"),sQuery(id+"F0.wireOp",EDGE,"E10.1.8"),sQuery(id+"F0.wireOp",EDGE,"E10.1.9"),sQuery(id+"F0.wireOp",EDGE,"E10.1.10"),sQuery(id+"F0.wireOp",EDGE,"E10.1.11"),sQuery(id+"F0.wireOp",EDGE,"E10.1.12"),sQuery(id+"F0.wireOp",EDGE,"E10.1.14"),sQuery(id+"F0.wireOp",EDGE,"E10.1.15"),sQuery(id+"F0.wireOp",EDGE,"E10.1.16"),sQuery(id+"F0.wireOp",EDGE,"E10.1.18"),sQuery(id+"F0.wireOp",EDGE,"E10.1.20"),sQuery(id+"F0.wireOp",EDGE,"E10.2.0"),sQuery(id+"F0.wireOp",EDGE,"E10.2.1"),sQuery(id+"F0.wireOp",EDGE,"E10.2.2"),sQuery(id+"F0.wireOp",EDGE,"E10.2.3"),sQuery(id+"F0.wireOp",EDGE,"E10.2.5"),sQuery(id+"F0.wireOp",EDGE,"E10.2.7"),sQuery(id+"F0.wireOp",EDGE,"E10.2.8"),sQuery(id+"F0.wireOp",EDGE,"E10.2.9"),sQuery(id+"F0.wireOp",EDGE,"E10.2.10"),sQuery(id+"F0.wireOp",EDGE,"E10.2.11"),sQuery(id+"F0.wireOp",EDGE,"E10.2.12"),sQuery(id+"F0.wireOp",EDGE,"E1"),sQuery(id+"F0.wireOp",EDGE,"E10.2.14"),sQuery(id+"F0.wireOp",EDGE,"E10.2.15"),sQuery(id+"F0.wireOp",EDGE,"E10.2.16"),sQuery(id+"F0.wireOp",EDGE,"E10.2.18"),sQuery(id+"F0.wireOp",EDGE,"E10.2.20"),sQuery(id+"F0.wireOp",EDGE,"E8.trimOffspring"),sQuery(id+"F0.wireOp",EDGE,"E0"),sQuery(id+"F0.wireOp",EDGE,"E10.1.6"),sQuery(id+"F0.wireOp",EDGE,"E11"),sQuery(id+"F0.wireOp",EDGE,"E12"),sQuery(id+"F0.wireOp",EDGE,"E13.1.0"),sQuery(id+"F0.wireOp",EDGE,"E13.1.1"),sQuery(id+"F0.wireOp",EDGE,"E13.2.0"),sQuery(id+"F0.wireOp",EDGE,"E13.2.1")])]}),"instanceName":"1"}),"instanceName":"1"}),"instanceName":"1"}),"instanceName":"1"});
            var Q24;
            Q24=makeQuery(id+"F63.opPattern","COPY",BODY,{"derivedFrom":makeQuery(id+"F47.opPattern","COPY",BODY,{"derivedFrom":makeQuery(id+"F42.opPattern","COPY",BODY,{"derivedFrom":makeQuery(id+"F13.opPattern","COPY",BODY,{"derivedFrom":makeQuery(id+"F1.opExtrude","SWEPT_BODY",BODY,{"disambiguationData":[OSD([sQuery(id+"F0.wireOp",EDGE,"E2.0"),sQuery(id+"F0.wireOp",EDGE,"E2.1"),sQuery(id+"F0.wireOp",EDGE,"E2.2"),sQuery(id+"F0.wireOp",EDGE,"E2.3"),sQuery(id+"F0.wireOp",EDGE,"E2.4"),sQuery(id+"F0.wireOp",EDGE,"E2.5"),sQuery(id+"F0.wireOp",EDGE,"E3"),sQuery(id+"F0.wireOp",EDGE,"E4"),sQuery(id+"F0.wireOp",EDGE,"E5.0"),sQuery(id+"F0.wireOp",EDGE,"E5.1"),sQuery(id+"F0.wireOp",EDGE,"E5.3"),sQuery(id+"F0.wireOp",EDGE,"E5.4"),sQuery(id+"F0.wireOp",EDGE,"E5.5"),sQuery(id+"F0.wireOp",EDGE,"E6.trimOffspring"),sQuery(id+"F0.wireOp",EDGE,"E7.trimOffspring"),sQuery(id+"F0.wireOp",EDGE,"E9.trimOffspring"),sQuery(id+"F0.wireOp",EDGE,"E10.1.0"),sQuery(id+"F0.wireOp",EDGE,"E10.1.1"),sQuery(id+"F0.wireOp",EDGE,"E10.1.2"),sQuery(id+"F0.wireOp",EDGE,"E10.1.3"),sQuery(id+"F0.wireOp",EDGE,"E10.1.5"),sQuery(id+"F0.wireOp",EDGE,"E10.1.7"),sQuery(id+"F0.wireOp",EDGE,"E10.1.8"),sQuery(id+"F0.wireOp",EDGE,"E10.1.9"),sQuery(id+"F0.wireOp",EDGE,"E10.1.10"),sQuery(id+"F0.wireOp",EDGE,"E10.1.11"),sQuery(id+"F0.wireOp",EDGE,"E10.1.12"),sQuery(id+"F0.wireOp",EDGE,"E10.1.14"),sQuery(id+"F0.wireOp",EDGE,"E10.1.15"),sQuery(id+"F0.wireOp",EDGE,"E10.1.16"),sQuery(id+"F0.wireOp",EDGE,"E10.1.18"),sQuery(id+"F0.wireOp",EDGE,"E10.1.20"),sQuery(id+"F0.wireOp",EDGE,"E10.2.0"),sQuery(id+"F0.wireOp",EDGE,"E10.2.1"),sQuery(id+"F0.wireOp",EDGE,"E10.2.2"),sQuery(id+"F0.wireOp",EDGE,"E10.2.3"),sQuery(id+"F0.wireOp",EDGE,"E10.2.5"),sQuery(id+"F0.wireOp",EDGE,"E10.2.7"),sQuery(id+"F0.wireOp",EDGE,"E10.2.8"),sQuery(id+"F0.wireOp",EDGE,"E10.2.9"),sQuery(id+"F0.wireOp",EDGE,"E10.2.10"),sQuery(id+"F0.wireOp",EDGE,"E10.2.11"),sQuery(id+"F0.wireOp",EDGE,"E10.2.12"),sQuery(id+"F0.wireOp",EDGE,"E1"),sQuery(id+"F0.wireOp",EDGE,"E10.2.14"),sQuery(id+"F0.wireOp",EDGE,"E10.2.15"),sQuery(id+"F0.wireOp",EDGE,"E10.2.16"),sQuery(id+"F0.wireOp",EDGE,"E10.2.18"),sQuery(id+"F0.wireOp",EDGE,"E10.2.20"),sQuery(id+"F0.wireOp",EDGE,"E8.trimOffspring"),sQuery(id+"F0.wireOp",EDGE,"E0"),sQuery(id+"F0.wireOp",EDGE,"E10.1.6"),sQuery(id+"F0.wireOp",EDGE,"E11"),sQuery(id+"F0.wireOp",EDGE,"E12"),sQuery(id+"F0.wireOp",EDGE,"E13.1.0"),sQuery(id+"F0.wireOp",EDGE,"E13.1.1"),sQuery(id+"F0.wireOp",EDGE,"E13.2.0"),sQuery(id+"F0.wireOp",EDGE,"E13.2.1")])]}),"instanceName":"1"}),"instanceName":"1"}),"instanceName":"1"}),"instanceName":"1"});
            var Q25;
            Q25=makeQuery(id+"F64.opPattern","COPY",BODY,{"derivedFrom":makeQuery(id+"F48.opPattern","COPY",BODY,{"derivedFrom":makeQuery(id+"F39.opPattern","COPY",BODY,{"derivedFrom":makeQuery(id+"F36.opPattern","COPY",BODY,{"derivedFrom":makeQuery(id+"F23.opPattern","COPY",BODY,{"derivedFrom":makeQuery(id+"F7.opPattern","COPY",BODY,{"derivedFrom":makeQuery(id+"F1.opExtrude","SWEPT_BODY",BODY,{"disambiguationData":[OSD([sQuery(id+"F0.wireOp",EDGE,"E2.0"),sQuery(id+"F0.wireOp",EDGE,"E2.1"),sQuery(id+"F0.wireOp",EDGE,"E2.2"),sQuery(id+"F0.wireOp",EDGE,"E2.3"),sQuery(id+"F0.wireOp",EDGE,"E2.4"),sQuery(id+"F0.wireOp",EDGE,"E2.5"),sQuery(id+"F0.wireOp",EDGE,"E3"),sQuery(id+"F0.wireOp",EDGE,"E4"),sQuery(id+"F0.wireOp",EDGE,"E5.0"),sQuery(id+"F0.wireOp",EDGE,"E5.1"),sQuery(id+"F0.wireOp",EDGE,"E5.3"),sQuery(id+"F0.wireOp",EDGE,"E5.4"),sQuery(id+"F0.wireOp",EDGE,"E5.5"),sQuery(id+"F0.wireOp",EDGE,"E6.trimOffspring"),sQuery(id+"F0.wireOp",EDGE,"E7.trimOffspring"),sQuery(id+"F0.wireOp",EDGE,"E9.trimOffspring"),sQuery(id+"F0.wireOp",EDGE,"E10.1.0"),sQuery(id+"F0.wireOp",EDGE,"E10.1.1"),sQuery(id+"F0.wireOp",EDGE,"E10.1.2"),sQuery(id+"F0.wireOp",EDGE,"E10.1.3"),sQuery(id+"F0.wireOp",EDGE,"E10.1.5"),sQuery(id+"F0.wireOp",EDGE,"E10.1.7"),sQuery(id+"F0.wireOp",EDGE,"E10.1.8"),sQuery(id+"F0.wireOp",EDGE,"E10.1.9"),sQuery(id+"F0.wireOp",EDGE,"E10.1.10"),sQuery(id+"F0.wireOp",EDGE,"E10.1.11"),sQuery(id+"F0.wireOp",EDGE,"E10.1.12"),sQuery(id+"F0.wireOp",EDGE,"E10.1.14"),sQuery(id+"F0.wireOp",EDGE,"E10.1.15"),sQuery(id+"F0.wireOp",EDGE,"E10.1.16"),sQuery(id+"F0.wireOp",EDGE,"E10.1.18"),sQuery(id+"F0.wireOp",EDGE,"E10.1.20"),sQuery(id+"F0.wireOp",EDGE,"E10.2.0"),sQuery(id+"F0.wireOp",EDGE,"E10.2.1"),sQuery(id+"F0.wireOp",EDGE,"E10.2.2"),sQuery(id+"F0.wireOp",EDGE,"E10.2.3"),sQuery(id+"F0.wireOp",EDGE,"E10.2.5"),sQuery(id+"F0.wireOp",EDGE,"E10.2.7"),sQuery(id+"F0.wireOp",EDGE,"E10.2.8"),sQuery(id+"F0.wireOp",EDGE,"E10.2.9"),sQuery(id+"F0.wireOp",EDGE,"E10.2.10"),sQuery(id+"F0.wireOp",EDGE,"E10.2.11"),sQuery(id+"F0.wireOp",EDGE,"E10.2.12"),sQuery(id+"F0.wireOp",EDGE,"E1"),sQuery(id+"F0.wireOp",EDGE,"E10.2.14"),sQuery(id+"F0.wireOp",EDGE,"E10.2.15"),sQuery(id+"F0.wireOp",EDGE,"E10.2.16"),sQuery(id+"F0.wireOp",EDGE,"E10.2.18"),sQuery(id+"F0.wireOp",EDGE,"E10.2.20"),sQuery(id+"F0.wireOp",EDGE,"E8.trimOffspring"),sQuery(id+"F0.wireOp",EDGE,"E0"),sQuery(id+"F0.wireOp",EDGE,"E10.1.6"),sQuery(id+"F0.wireOp",EDGE,"E11"),sQuery(id+"F0.wireOp",EDGE,"E12"),sQuery(id+"F0.wireOp",EDGE,"E13.1.0"),sQuery(id+"F0.wireOp",EDGE,"E13.1.1"),sQuery(id+"F0.wireOp",EDGE,"E13.2.0"),sQuery(id+"F0.wireOp",EDGE,"E13.2.1")])]}),"instanceName":"1"}),"instanceName":"1"}),"instanceName":"1"}),"instanceName":"1"}),"instanceName":"1"}),"instanceName":"1"});
            var Q26;
            Q26=makeQuery(id+"F67.opPattern","COPY",BODY,{"derivedFrom":makeQuery(id+"F51.opPattern","COPY",BODY,{"derivedFrom":makeQuery(id+"F39.opPattern","COPY",BODY,{"derivedFrom":makeQuery(id+"F36.opPattern","COPY",BODY,{"derivedFrom":makeQuery(id+"F23.opPattern","COPY",BODY,{"derivedFrom":makeQuery(id+"F7.opPattern","COPY",BODY,{"derivedFrom":makeQuery(id+"F1.opExtrude","SWEPT_BODY",BODY,{"disambiguationData":[OSD([sQuery(id+"F0.wireOp",EDGE,"E2.0"),sQuery(id+"F0.wireOp",EDGE,"E2.1"),sQuery(id+"F0.wireOp",EDGE,"E2.2"),sQuery(id+"F0.wireOp",EDGE,"E2.3"),sQuery(id+"F0.wireOp",EDGE,"E2.4"),sQuery(id+"F0.wireOp",EDGE,"E2.5"),sQuery(id+"F0.wireOp",EDGE,"E3"),sQuery(id+"F0.wireOp",EDGE,"E4"),sQuery(id+"F0.wireOp",EDGE,"E5.0"),sQuery(id+"F0.wireOp",EDGE,"E5.1"),sQuery(id+"F0.wireOp",EDGE,"E5.3"),sQuery(id+"F0.wireOp",EDGE,"E5.4"),sQuery(id+"F0.wireOp",EDGE,"E5.5"),sQuery(id+"F0.wireOp",EDGE,"E6.trimOffspring"),sQuery(id+"F0.wireOp",EDGE,"E7.trimOffspring"),sQuery(id+"F0.wireOp",EDGE,"E9.trimOffspring"),sQuery(id+"F0.wireOp",EDGE,"E10.1.0"),sQuery(id+"F0.wireOp",EDGE,"E10.1.1"),sQuery(id+"F0.wireOp",EDGE,"E10.1.2"),sQuery(id+"F0.wireOp",EDGE,"E10.1.3"),sQuery(id+"F0.wireOp",EDGE,"E10.1.5"),sQuery(id+"F0.wireOp",EDGE,"E10.1.7"),sQuery(id+"F0.wireOp",EDGE,"E10.1.8"),sQuery(id+"F0.wireOp",EDGE,"E10.1.9"),sQuery(id+"F0.wireOp",EDGE,"E10.1.10"),sQuery(id+"F0.wireOp",EDGE,"E10.1.11"),sQuery(id+"F0.wireOp",EDGE,"E10.1.12"),sQuery(id+"F0.wireOp",EDGE,"E10.1.14"),sQuery(id+"F0.wireOp",EDGE,"E10.1.15"),sQuery(id+"F0.wireOp",EDGE,"E10.1.16"),sQuery(id+"F0.wireOp",EDGE,"E10.1.18"),sQuery(id+"F0.wireOp",EDGE,"E10.1.20"),sQuery(id+"F0.wireOp",EDGE,"E10.2.0"),sQuery(id+"F0.wireOp",EDGE,"E10.2.1"),sQuery(id+"F0.wireOp",EDGE,"E10.2.2"),sQuery(id+"F0.wireOp",EDGE,"E10.2.3"),sQuery(id+"F0.wireOp",EDGE,"E10.2.5"),sQuery(id+"F0.wireOp",EDGE,"E10.2.7"),sQuery(id+"F0.wireOp",EDGE,"E10.2.8"),sQuery(id+"F0.wireOp",EDGE,"E10.2.9"),sQuery(id+"F0.wireOp",EDGE,"E10.2.10"),sQuery(id+"F0.wireOp",EDGE,"E10.2.11"),sQuery(id+"F0.wireOp",EDGE,"E10.2.12"),sQuery(id+"F0.wireOp",EDGE,"E1"),sQuery(id+"F0.wireOp",EDGE,"E10.2.14"),sQuery(id+"F0.wireOp",EDGE,"E10.2.15"),sQuery(id+"F0.wireOp",EDGE,"E10.2.16"),sQuery(id+"F0.wireOp",EDGE,"E10.2.18"),sQuery(id+"F0.wireOp",EDGE,"E10.2.20"),sQuery(id+"F0.wireOp",EDGE,"E8.trimOffspring"),sQuery(id+"F0.wireOp",EDGE,"E0"),sQuery(id+"F0.wireOp",EDGE,"E10.1.6"),sQuery(id+"F0.wireOp",EDGE,"E11"),sQuery(id+"F0.wireOp",EDGE,"E12"),sQuery(id+"F0.wireOp",EDGE,"E13.1.0"),sQuery(id+"F0.wireOp",EDGE,"E13.1.1"),sQuery(id+"F0.wireOp",EDGE,"E13.2.0"),sQuery(id+"F0.wireOp",EDGE,"E13.2.1")])]}),"instanceName":"1"}),"instanceName":"1"}),"instanceName":"1"}),"instanceName":"1"}),"instanceName":"1"}),"instanceName":"1"});
            deleteBodies(context, id + "F68", {"entities" : qUnion([Q0, Q1, Q2, Q3, Q4, Q5, Q6, Q7, Q8, Q9, Q10, Q11, Q12, Q13, Q14, Q15, Q16, Q17, Q18, Q19, Q20, Q21, Q22, Q23, Q24, Q25, Q26])});
        }
        {
            var Q0;
            Q0=makeQuery(id+"F1.opExtrude","SWEPT_BODY",BODY,{"disambiguationData":[OSD([sQuery(id+"F0.wireOp",EDGE,"E2.0"),sQuery(id+"F0.wireOp",EDGE,"E2.1"),sQuery(id+"F0.wireOp",EDGE,"E2.2"),sQuery(id+"F0.wireOp",EDGE,"E2.3"),sQuery(id+"F0.wireOp",EDGE,"E2.4"),sQuery(id+"F0.wireOp",EDGE,"E2.5"),sQuery(id+"F0.wireOp",EDGE,"E3"),sQuery(id+"F0.wireOp",EDGE,"E4"),sQuery(id+"F0.wireOp",EDGE,"E5.0"),sQuery(id+"F0.wireOp",EDGE,"E5.1"),sQuery(id+"F0.wireOp",EDGE,"E5.3"),sQuery(id+"F0.wireOp",EDGE,"E5.4"),sQuery(id+"F0.wireOp",EDGE,"E5.5"),sQuery(id+"F0.wireOp",EDGE,"E6.trimOffspring"),sQuery(id+"F0.wireOp",EDGE,"E7.trimOffspring"),sQuery(id+"F0.wireOp",EDGE,"E9.trimOffspring"),sQuery(id+"F0.wireOp",EDGE,"E10.1.0"),sQuery(id+"F0.wireOp",EDGE,"E10.1.1"),sQuery(id+"F0.wireOp",EDGE,"E10.1.2"),sQuery(id+"F0.wireOp",EDGE,"E10.1.3"),sQuery(id+"F0.wireOp",EDGE,"E10.1.5"),sQuery(id+"F0.wireOp",EDGE,"E10.1.7"),sQuery(id+"F0.wireOp",EDGE,"E10.1.8"),sQuery(id+"F0.wireOp",EDGE,"E10.1.9"),sQuery(id+"F0.wireOp",EDGE,"E10.1.10"),sQuery(id+"F0.wireOp",EDGE,"E10.1.11"),sQuery(id+"F0.wireOp",EDGE,"E10.1.12"),sQuery(id+"F0.wireOp",EDGE,"E10.1.14"),sQuery(id+"F0.wireOp",EDGE,"E10.1.15"),sQuery(id+"F0.wireOp",EDGE,"E10.1.16"),sQuery(id+"F0.wireOp",EDGE,"E10.1.18"),sQuery(id+"F0.wireOp",EDGE,"E10.1.20"),sQuery(id+"F0.wireOp",EDGE,"E10.2.0"),sQuery(id+"F0.wireOp",EDGE,"E10.2.1"),sQuery(id+"F0.wireOp",EDGE,"E10.2.2"),sQuery(id+"F0.wireOp",EDGE,"E10.2.3"),sQuery(id+"F0.wireOp",EDGE,"E10.2.5"),sQuery(id+"F0.wireOp",EDGE,"E10.2.7"),sQuery(id+"F0.wireOp",EDGE,"E10.2.8"),sQuery(id+"F0.wireOp",EDGE,"E10.2.9"),sQuery(id+"F0.wireOp",EDGE,"E10.2.10"),sQuery(id+"F0.wireOp",EDGE,"E10.2.11"),sQuery(id+"F0.wireOp",EDGE,"E10.2.12"),sQuery(id+"F0.wireOp",EDGE,"E1"),sQuery(id+"F0.wireOp",EDGE,"E10.2.14"),sQuery(id+"F0.wireOp",EDGE,"E10.2.15"),sQuery(id+"F0.wireOp",EDGE,"E10.2.16"),sQuery(id+"F0.wireOp",EDGE,"E10.2.18"),sQuery(id+"F0.wireOp",EDGE,"E10.2.20"),sQuery(id+"F0.wireOp",EDGE,"E8.trimOffspring"),sQuery(id+"F0.wireOp",EDGE,"E0"),sQuery(id+"F0.wireOp",EDGE,"E10.1.6"),sQuery(id+"F0.wireOp",EDGE,"E11"),sQuery(id+"F0.wireOp",EDGE,"E12"),sQuery(id+"F0.wireOp",EDGE,"E13.1.0"),sQuery(id+"F0.wireOp",EDGE,"E13.1.1"),sQuery(id+"F0.wireOp",EDGE,"E13.2.0"),sQuery(id+"F0.wireOp",EDGE,"E13.2.1")])]});
            var Q1;
            Q1=makeQuery(id+"F5.opPattern","COPY",BODY,{"derivedFrom":makeQuery(id+"F1.opExtrude","SWEPT_BODY",BODY,{"disambiguationData":[OSD([sQuery(id+"F0.wireOp",EDGE,"E2.0"),sQuery(id+"F0.wireOp",EDGE,"E2.1"),sQuery(id+"F0.wireOp",EDGE,"E2.2"),sQuery(id+"F0.wireOp",EDGE,"E2.3"),sQuery(id+"F0.wireOp",EDGE,"E2.4"),sQuery(id+"F0.wireOp",EDGE,"E2.5"),sQuery(id+"F0.wireOp",EDGE,"E3"),sQuery(id+"F0.wireOp",EDGE,"E4"),sQuery(id+"F0.wireOp",EDGE,"E5.0"),sQuery(id+"F0.wireOp",EDGE,"E5.1"),sQuery(id+"F0.wireOp",EDGE,"E5.3"),sQuery(id+"F0.wireOp",EDGE,"E5.4"),sQuery(id+"F0.wireOp",EDGE,"E5.5"),sQuery(id+"F0.wireOp",EDGE,"E6.trimOffspring"),sQuery(id+"F0.wireOp",EDGE,"E7.trimOffspring"),sQuery(id+"F0.wireOp",EDGE,"E9.trimOffspring"),sQuery(id+"F0.wireOp",EDGE,"E10.1.0"),sQuery(id+"F0.wireOp",EDGE,"E10.1.1"),sQuery(id+"F0.wireOp",EDGE,"E10.1.2"),sQuery(id+"F0.wireOp",EDGE,"E10.1.3"),sQuery(id+"F0.wireOp",EDGE,"E10.1.5"),sQuery(id+"F0.wireOp",EDGE,"E10.1.7"),sQuery(id+"F0.wireOp",EDGE,"E10.1.8"),sQuery(id+"F0.wireOp",EDGE,"E10.1.9"),sQuery(id+"F0.wireOp",EDGE,"E10.1.10"),sQuery(id+"F0.wireOp",EDGE,"E10.1.11"),sQuery(id+"F0.wireOp",EDGE,"E10.1.12"),sQuery(id+"F0.wireOp",EDGE,"E10.1.14"),sQuery(id+"F0.wireOp",EDGE,"E10.1.15"),sQuery(id+"F0.wireOp",EDGE,"E10.1.16"),sQuery(id+"F0.wireOp",EDGE,"E10.1.18"),sQuery(id+"F0.wireOp",EDGE,"E10.1.20"),sQuery(id+"F0.wireOp",EDGE,"E10.2.0"),sQuery(id+"F0.wireOp",EDGE,"E10.2.1"),sQuery(id+"F0.wireOp",EDGE,"E10.2.2"),sQuery(id+"F0.wireOp",EDGE,"E10.2.3"),sQuery(id+"F0.wireOp",EDGE,"E10.2.5"),sQuery(id+"F0.wireOp",EDGE,"E10.2.7"),sQuery(id+"F0.wireOp",EDGE,"E10.2.8"),sQuery(id+"F0.wireOp",EDGE,"E10.2.9"),sQuery(id+"F0.wireOp",EDGE,"E10.2.10"),sQuery(id+"F0.wireOp",EDGE,"E10.2.11"),sQuery(id+"F0.wireOp",EDGE,"E10.2.12"),sQuery(id+"F0.wireOp",EDGE,"E1"),sQuery(id+"F0.wireOp",EDGE,"E10.2.14"),sQuery(id+"F0.wireOp",EDGE,"E10.2.15"),sQuery(id+"F0.wireOp",EDGE,"E10.2.16"),sQuery(id+"F0.wireOp",EDGE,"E10.2.18"),sQuery(id+"F0.wireOp",EDGE,"E10.2.20"),sQuery(id+"F0.wireOp",EDGE,"E8.trimOffspring"),sQuery(id+"F0.wireOp",EDGE,"E0"),sQuery(id+"F0.wireOp",EDGE,"E10.1.6"),sQuery(id+"F0.wireOp",EDGE,"E11"),sQuery(id+"F0.wireOp",EDGE,"E12"),sQuery(id+"F0.wireOp",EDGE,"E13.1.0"),sQuery(id+"F0.wireOp",EDGE,"E13.1.1"),sQuery(id+"F0.wireOp",EDGE,"E13.2.0"),sQuery(id+"F0.wireOp",EDGE,"E13.2.1")])]}),"instanceName":"1"});
            var Q2;
            Q2=makeQuery(id+"F7.opPattern","COPY",BODY,{"derivedFrom":makeQuery(id+"F1.opExtrude","SWEPT_BODY",BODY,{"disambiguationData":[OSD([sQuery(id+"F0.wireOp",EDGE,"E2.0"),sQuery(id+"F0.wireOp",EDGE,"E2.1"),sQuery(id+"F0.wireOp",EDGE,"E2.2"),sQuery(id+"F0.wireOp",EDGE,"E2.3"),sQuery(id+"F0.wireOp",EDGE,"E2.4"),sQuery(id+"F0.wireOp",EDGE,"E2.5"),sQuery(id+"F0.wireOp",EDGE,"E3"),sQuery(id+"F0.wireOp",EDGE,"E4"),sQuery(id+"F0.wireOp",EDGE,"E5.0"),sQuery(id+"F0.wireOp",EDGE,"E5.1"),sQuery(id+"F0.wireOp",EDGE,"E5.3"),sQuery(id+"F0.wireOp",EDGE,"E5.4"),sQuery(id+"F0.wireOp",EDGE,"E5.5"),sQuery(id+"F0.wireOp",EDGE,"E6.trimOffspring"),sQuery(id+"F0.wireOp",EDGE,"E7.trimOffspring"),sQuery(id+"F0.wireOp",EDGE,"E9.trimOffspring"),sQuery(id+"F0.wireOp",EDGE,"E10.1.0"),sQuery(id+"F0.wireOp",EDGE,"E10.1.1"),sQuery(id+"F0.wireOp",EDGE,"E10.1.2"),sQuery(id+"F0.wireOp",EDGE,"E10.1.3"),sQuery(id+"F0.wireOp",EDGE,"E10.1.5"),sQuery(id+"F0.wireOp",EDGE,"E10.1.7"),sQuery(id+"F0.wireOp",EDGE,"E10.1.8"),sQuery(id+"F0.wireOp",EDGE,"E10.1.9"),sQuery(id+"F0.wireOp",EDGE,"E10.1.10"),sQuery(id+"F0.wireOp",EDGE,"E10.1.11"),sQuery(id+"F0.wireOp",EDGE,"E10.1.12"),sQuery(id+"F0.wireOp",EDGE,"E10.1.14"),sQuery(id+"F0.wireOp",EDGE,"E10.1.15"),sQuery(id+"F0.wireOp",EDGE,"E10.1.16"),sQuery(id+"F0.wireOp",EDGE,"E10.1.18"),sQuery(id+"F0.wireOp",EDGE,"E10.1.20"),sQuery(id+"F0.wireOp",EDGE,"E10.2.0"),sQuery(id+"F0.wireOp",EDGE,"E10.2.1"),sQuery(id+"F0.wireOp",EDGE,"E10.2.2"),sQuery(id+"F0.wireOp",EDGE,"E10.2.3"),sQuery(id+"F0.wireOp",EDGE,"E10.2.5"),sQuery(id+"F0.wireOp",EDGE,"E10.2.7"),sQuery(id+"F0.wireOp",EDGE,"E10.2.8"),sQuery(id+"F0.wireOp",EDGE,"E10.2.9"),sQuery(id+"F0.wireOp",EDGE,"E10.2.10"),sQuery(id+"F0.wireOp",EDGE,"E10.2.11"),sQuery(id+"F0.wireOp",EDGE,"E10.2.12"),sQuery(id+"F0.wireOp",EDGE,"E1"),sQuery(id+"F0.wireOp",EDGE,"E10.2.14"),sQuery(id+"F0.wireOp",EDGE,"E10.2.15"),sQuery(id+"F0.wireOp",EDGE,"E10.2.16"),sQuery(id+"F0.wireOp",EDGE,"E10.2.18"),sQuery(id+"F0.wireOp",EDGE,"E10.2.20"),sQuery(id+"F0.wireOp",EDGE,"E8.trimOffspring"),sQuery(id+"F0.wireOp",EDGE,"E0"),sQuery(id+"F0.wireOp",EDGE,"E10.1.6"),sQuery(id+"F0.wireOp",EDGE,"E11"),sQuery(id+"F0.wireOp",EDGE,"E12"),sQuery(id+"F0.wireOp",EDGE,"E13.1.0"),sQuery(id+"F0.wireOp",EDGE,"E13.1.1"),sQuery(id+"F0.wireOp",EDGE,"E13.2.0"),sQuery(id+"F0.wireOp",EDGE,"E13.2.1")])]}),"instanceName":"1"});
            var Q3;
            Q3=makeQuery(id+"F8.opPattern","COPY",BODY,{"derivedFrom":makeQuery(id+"F7.opPattern","COPY",BODY,{"derivedFrom":makeQuery(id+"F1.opExtrude","SWEPT_BODY",BODY,{"disambiguationData":[OSD([sQuery(id+"F0.wireOp",EDGE,"E2.0"),sQuery(id+"F0.wireOp",EDGE,"E2.1"),sQuery(id+"F0.wireOp",EDGE,"E2.2"),sQuery(id+"F0.wireOp",EDGE,"E2.3"),sQuery(id+"F0.wireOp",EDGE,"E2.4"),sQuery(id+"F0.wireOp",EDGE,"E2.5"),sQuery(id+"F0.wireOp",EDGE,"E3"),sQuery(id+"F0.wireOp",EDGE,"E4"),sQuery(id+"F0.wireOp",EDGE,"E5.0"),sQuery(id+"F0.wireOp",EDGE,"E5.1"),sQuery(id+"F0.wireOp",EDGE,"E5.3"),sQuery(id+"F0.wireOp",EDGE,"E5.4"),sQuery(id+"F0.wireOp",EDGE,"E5.5"),sQuery(id+"F0.wireOp",EDGE,"E6.trimOffspring"),sQuery(id+"F0.wireOp",EDGE,"E7.trimOffspring"),sQuery(id+"F0.wireOp",EDGE,"E9.trimOffspring"),sQuery(id+"F0.wireOp",EDGE,"E10.1.0"),sQuery(id+"F0.wireOp",EDGE,"E10.1.1"),sQuery(id+"F0.wireOp",EDGE,"E10.1.2"),sQuery(id+"F0.wireOp",EDGE,"E10.1.3"),sQuery(id+"F0.wireOp",EDGE,"E10.1.5"),sQuery(id+"F0.wireOp",EDGE,"E10.1.7"),sQuery(id+"F0.wireOp",EDGE,"E10.1.8"),sQuery(id+"F0.wireOp",EDGE,"E10.1.9"),sQuery(id+"F0.wireOp",EDGE,"E10.1.10"),sQuery(id+"F0.wireOp",EDGE,"E10.1.11"),sQuery(id+"F0.wireOp",EDGE,"E10.1.12"),sQuery(id+"F0.wireOp",EDGE,"E10.1.14"),sQuery(id+"F0.wireOp",EDGE,"E10.1.15"),sQuery(id+"F0.wireOp",EDGE,"E10.1.16"),sQuery(id+"F0.wireOp",EDGE,"E10.1.18"),sQuery(id+"F0.wireOp",EDGE,"E10.1.20"),sQuery(id+"F0.wireOp",EDGE,"E10.2.0"),sQuery(id+"F0.wireOp",EDGE,"E10.2.1"),sQuery(id+"F0.wireOp",EDGE,"E10.2.2"),sQuery(id+"F0.wireOp",EDGE,"E10.2.3"),sQuery(id+"F0.wireOp",EDGE,"E10.2.5"),sQuery(id+"F0.wireOp",EDGE,"E10.2.7"),sQuery(id+"F0.wireOp",EDGE,"E10.2.8"),sQuery(id+"F0.wireOp",EDGE,"E10.2.9"),sQuery(id+"F0.wireOp",EDGE,"E10.2.10"),sQuery(id+"F0.wireOp",EDGE,"E10.2.11"),sQuery(id+"F0.wireOp",EDGE,"E10.2.12"),sQuery(id+"F0.wireOp",EDGE,"E1"),sQuery(id+"F0.wireOp",EDGE,"E10.2.14"),sQuery(id+"F0.wireOp",EDGE,"E10.2.15"),sQuery(id+"F0.wireOp",EDGE,"E10.2.16"),sQuery(id+"F0.wireOp",EDGE,"E10.2.18"),sQuery(id+"F0.wireOp",EDGE,"E10.2.20"),sQuery(id+"F0.wireOp",EDGE,"E8.trimOffspring"),sQuery(id+"F0.wireOp",EDGE,"E0"),sQuery(id+"F0.wireOp",EDGE,"E10.1.6"),sQuery(id+"F0.wireOp",EDGE,"E11"),sQuery(id+"F0.wireOp",EDGE,"E12"),sQuery(id+"F0.wireOp",EDGE,"E13.1.0"),sQuery(id+"F0.wireOp",EDGE,"E13.1.1"),sQuery(id+"F0.wireOp",EDGE,"E13.2.0"),sQuery(id+"F0.wireOp",EDGE,"E13.2.1")])]}),"instanceName":"1"}),"instanceName":"1"});
            var Q4;
            Q4=makeQuery(id+"F9.opPattern","COPY",BODY,{"derivedFrom":makeQuery(id+"F8.opPattern","COPY",BODY,{"derivedFrom":makeQuery(id+"F7.opPattern","COPY",BODY,{"derivedFrom":makeQuery(id+"F1.opExtrude","SWEPT_BODY",BODY,{"disambiguationData":[OSD([sQuery(id+"F0.wireOp",EDGE,"E2.0"),sQuery(id+"F0.wireOp",EDGE,"E2.1"),sQuery(id+"F0.wireOp",EDGE,"E2.2"),sQuery(id+"F0.wireOp",EDGE,"E2.3"),sQuery(id+"F0.wireOp",EDGE,"E2.4"),sQuery(id+"F0.wireOp",EDGE,"E2.5"),sQuery(id+"F0.wireOp",EDGE,"E3"),sQuery(id+"F0.wireOp",EDGE,"E4"),sQuery(id+"F0.wireOp",EDGE,"E5.0"),sQuery(id+"F0.wireOp",EDGE,"E5.1"),sQuery(id+"F0.wireOp",EDGE,"E5.3"),sQuery(id+"F0.wireOp",EDGE,"E5.4"),sQuery(id+"F0.wireOp",EDGE,"E5.5"),sQuery(id+"F0.wireOp",EDGE,"E6.trimOffspring"),sQuery(id+"F0.wireOp",EDGE,"E7.trimOffspring"),sQuery(id+"F0.wireOp",EDGE,"E9.trimOffspring"),sQuery(id+"F0.wireOp",EDGE,"E10.1.0"),sQuery(id+"F0.wireOp",EDGE,"E10.1.1"),sQuery(id+"F0.wireOp",EDGE,"E10.1.2"),sQuery(id+"F0.wireOp",EDGE,"E10.1.3"),sQuery(id+"F0.wireOp",EDGE,"E10.1.5"),sQuery(id+"F0.wireOp",EDGE,"E10.1.7"),sQuery(id+"F0.wireOp",EDGE,"E10.1.8"),sQuery(id+"F0.wireOp",EDGE,"E10.1.9"),sQuery(id+"F0.wireOp",EDGE,"E10.1.10"),sQuery(id+"F0.wireOp",EDGE,"E10.1.11"),sQuery(id+"F0.wireOp",EDGE,"E10.1.12"),sQuery(id+"F0.wireOp",EDGE,"E10.1.14"),sQuery(id+"F0.wireOp",EDGE,"E10.1.15"),sQuery(id+"F0.wireOp",EDGE,"E10.1.16"),sQuery(id+"F0.wireOp",EDGE,"E10.1.18"),sQuery(id+"F0.wireOp",EDGE,"E10.1.20"),sQuery(id+"F0.wireOp",EDGE,"E10.2.0"),sQuery(id+"F0.wireOp",EDGE,"E10.2.1"),sQuery(id+"F0.wireOp",EDGE,"E10.2.2"),sQuery(id+"F0.wireOp",EDGE,"E10.2.3"),sQuery(id+"F0.wireOp",EDGE,"E10.2.5"),sQuery(id+"F0.wireOp",EDGE,"E10.2.7"),sQuery(id+"F0.wireOp",EDGE,"E10.2.8"),sQuery(id+"F0.wireOp",EDGE,"E10.2.9"),sQuery(id+"F0.wireOp",EDGE,"E10.2.10"),sQuery(id+"F0.wireOp",EDGE,"E10.2.11"),sQuery(id+"F0.wireOp",EDGE,"E10.2.12"),sQuery(id+"F0.wireOp",EDGE,"E1"),sQuery(id+"F0.wireOp",EDGE,"E10.2.14"),sQuery(id+"F0.wireOp",EDGE,"E10.2.15"),sQuery(id+"F0.wireOp",EDGE,"E10.2.16"),sQuery(id+"F0.wireOp",EDGE,"E10.2.18"),sQuery(id+"F0.wireOp",EDGE,"E10.2.20"),sQuery(id+"F0.wireOp",EDGE,"E8.trimOffspring"),sQuery(id+"F0.wireOp",EDGE,"E0"),sQuery(id+"F0.wireOp",EDGE,"E10.1.6"),sQuery(id+"F0.wireOp",EDGE,"E11"),sQuery(id+"F0.wireOp",EDGE,"E12"),sQuery(id+"F0.wireOp",EDGE,"E13.1.0"),sQuery(id+"F0.wireOp",EDGE,"E13.1.1"),sQuery(id+"F0.wireOp",EDGE,"E13.2.0"),sQuery(id+"F0.wireOp",EDGE,"E13.2.1")])]}),"instanceName":"1"}),"instanceName":"1"}),"instanceName":"1"});
            var Q5;
            Q5=makeQuery(id+"F10.opPattern","COPY",BODY,{"derivedFrom":makeQuery(id+"F9.opPattern","COPY",BODY,{"derivedFrom":makeQuery(id+"F8.opPattern","COPY",BODY,{"derivedFrom":makeQuery(id+"F7.opPattern","COPY",BODY,{"derivedFrom":makeQuery(id+"F1.opExtrude","SWEPT_BODY",BODY,{"disambiguationData":[OSD([sQuery(id+"F0.wireOp",EDGE,"E2.0"),sQuery(id+"F0.wireOp",EDGE,"E2.1"),sQuery(id+"F0.wireOp",EDGE,"E2.2"),sQuery(id+"F0.wireOp",EDGE,"E2.3"),sQuery(id+"F0.wireOp",EDGE,"E2.4"),sQuery(id+"F0.wireOp",EDGE,"E2.5"),sQuery(id+"F0.wireOp",EDGE,"E3"),sQuery(id+"F0.wireOp",EDGE,"E4"),sQuery(id+"F0.wireOp",EDGE,"E5.0"),sQuery(id+"F0.wireOp",EDGE,"E5.1"),sQuery(id+"F0.wireOp",EDGE,"E5.3"),sQuery(id+"F0.wireOp",EDGE,"E5.4"),sQuery(id+"F0.wireOp",EDGE,"E5.5"),sQuery(id+"F0.wireOp",EDGE,"E6.trimOffspring"),sQuery(id+"F0.wireOp",EDGE,"E7.trimOffspring"),sQuery(id+"F0.wireOp",EDGE,"E9.trimOffspring"),sQuery(id+"F0.wireOp",EDGE,"E10.1.0"),sQuery(id+"F0.wireOp",EDGE,"E10.1.1"),sQuery(id+"F0.wireOp",EDGE,"E10.1.2"),sQuery(id+"F0.wireOp",EDGE,"E10.1.3"),sQuery(id+"F0.wireOp",EDGE,"E10.1.5"),sQuery(id+"F0.wireOp",EDGE,"E10.1.7"),sQuery(id+"F0.wireOp",EDGE,"E10.1.8"),sQuery(id+"F0.wireOp",EDGE,"E10.1.9"),sQuery(id+"F0.wireOp",EDGE,"E10.1.10"),sQuery(id+"F0.wireOp",EDGE,"E10.1.11"),sQuery(id+"F0.wireOp",EDGE,"E10.1.12"),sQuery(id+"F0.wireOp",EDGE,"E10.1.14"),sQuery(id+"F0.wireOp",EDGE,"E10.1.15"),sQuery(id+"F0.wireOp",EDGE,"E10.1.16"),sQuery(id+"F0.wireOp",EDGE,"E10.1.18"),sQuery(id+"F0.wireOp",EDGE,"E10.1.20"),sQuery(id+"F0.wireOp",EDGE,"E10.2.0"),sQuery(id+"F0.wireOp",EDGE,"E10.2.1"),sQuery(id+"F0.wireOp",EDGE,"E10.2.2"),sQuery(id+"F0.wireOp",EDGE,"E10.2.3"),sQuery(id+"F0.wireOp",EDGE,"E10.2.5"),sQuery(id+"F0.wireOp",EDGE,"E10.2.7"),sQuery(id+"F0.wireOp",EDGE,"E10.2.8"),sQuery(id+"F0.wireOp",EDGE,"E10.2.9"),sQuery(id+"F0.wireOp",EDGE,"E10.2.10"),sQuery(id+"F0.wireOp",EDGE,"E10.2.11"),sQuery(id+"F0.wireOp",EDGE,"E10.2.12"),sQuery(id+"F0.wireOp",EDGE,"E1"),sQuery(id+"F0.wireOp",EDGE,"E10.2.14"),sQuery(id+"F0.wireOp",EDGE,"E10.2.15"),sQuery(id+"F0.wireOp",EDGE,"E10.2.16"),sQuery(id+"F0.wireOp",EDGE,"E10.2.18"),sQuery(id+"F0.wireOp",EDGE,"E10.2.20"),sQuery(id+"F0.wireOp",EDGE,"E8.trimOffspring"),sQuery(id+"F0.wireOp",EDGE,"E0"),sQuery(id+"F0.wireOp",EDGE,"E10.1.6"),sQuery(id+"F0.wireOp",EDGE,"E11"),sQuery(id+"F0.wireOp",EDGE,"E12"),sQuery(id+"F0.wireOp",EDGE,"E13.1.0"),sQuery(id+"F0.wireOp",EDGE,"E13.1.1"),sQuery(id+"F0.wireOp",EDGE,"E13.2.0"),sQuery(id+"F0.wireOp",EDGE,"E13.2.1")])]}),"instanceName":"1"}),"instanceName":"1"}),"instanceName":"1"}),"instanceName":"1"});
            transform(context, id + "F69", {"entities" : qUnion([Q0, Q1, Q2, Q3, Q4, Q5]), "transformType" : TransformType.TRANSLATION_3D, "dx" : 0 * mm, "dy" : -68.8 * mm, "dz" : 0 * mm, "makeCopy" : true});
        }
        {
            var Q0;
            Q0=makeQuery(id+"F69.opPattern","COPY",BODY,{"derivedFrom":makeQuery(id+"F1.opExtrude","SWEPT_BODY",BODY,{"disambiguationData":[OSD([sQuery(id+"F0.wireOp",EDGE,"E2.0"),sQuery(id+"F0.wireOp",EDGE,"E2.1"),sQuery(id+"F0.wireOp",EDGE,"E2.2"),sQuery(id+"F0.wireOp",EDGE,"E2.3"),sQuery(id+"F0.wireOp",EDGE,"E2.4"),sQuery(id+"F0.wireOp",EDGE,"E2.5"),sQuery(id+"F0.wireOp",EDGE,"E3"),sQuery(id+"F0.wireOp",EDGE,"E4"),sQuery(id+"F0.wireOp",EDGE,"E5.0"),sQuery(id+"F0.wireOp",EDGE,"E5.1"),sQuery(id+"F0.wireOp",EDGE,"E5.3"),sQuery(id+"F0.wireOp",EDGE,"E5.4"),sQuery(id+"F0.wireOp",EDGE,"E5.5"),sQuery(id+"F0.wireOp",EDGE,"E6.trimOffspring"),sQuery(id+"F0.wireOp",EDGE,"E7.trimOffspring"),sQuery(id+"F0.wireOp",EDGE,"E9.trimOffspring"),sQuery(id+"F0.wireOp",EDGE,"E10.1.0"),sQuery(id+"F0.wireOp",EDGE,"E10.1.1"),sQuery(id+"F0.wireOp",EDGE,"E10.1.2"),sQuery(id+"F0.wireOp",EDGE,"E10.1.3"),sQuery(id+"F0.wireOp",EDGE,"E10.1.5"),sQuery(id+"F0.wireOp",EDGE,"E10.1.7"),sQuery(id+"F0.wireOp",EDGE,"E10.1.8"),sQuery(id+"F0.wireOp",EDGE,"E10.1.9"),sQuery(id+"F0.wireOp",EDGE,"E10.1.10"),sQuery(id+"F0.wireOp",EDGE,"E10.1.11"),sQuery(id+"F0.wireOp",EDGE,"E10.1.12"),sQuery(id+"F0.wireOp",EDGE,"E10.1.14"),sQuery(id+"F0.wireOp",EDGE,"E10.1.15"),sQuery(id+"F0.wireOp",EDGE,"E10.1.16"),sQuery(id+"F0.wireOp",EDGE,"E10.1.18"),sQuery(id+"F0.wireOp",EDGE,"E10.1.20"),sQuery(id+"F0.wireOp",EDGE,"E10.2.0"),sQuery(id+"F0.wireOp",EDGE,"E10.2.1"),sQuery(id+"F0.wireOp",EDGE,"E10.2.2"),sQuery(id+"F0.wireOp",EDGE,"E10.2.3"),sQuery(id+"F0.wireOp",EDGE,"E10.2.5"),sQuery(id+"F0.wireOp",EDGE,"E10.2.7"),sQuery(id+"F0.wireOp",EDGE,"E10.2.8"),sQuery(id+"F0.wireOp",EDGE,"E10.2.9"),sQuery(id+"F0.wireOp",EDGE,"E10.2.10"),sQuery(id+"F0.wireOp",EDGE,"E10.2.11"),sQuery(id+"F0.wireOp",EDGE,"E10.2.12"),sQuery(id+"F0.wireOp",EDGE,"E1"),sQuery(id+"F0.wireOp",EDGE,"E10.2.14"),sQuery(id+"F0.wireOp",EDGE,"E10.2.15"),sQuery(id+"F0.wireOp",EDGE,"E10.2.16"),sQuery(id+"F0.wireOp",EDGE,"E10.2.18"),sQuery(id+"F0.wireOp",EDGE,"E10.2.20"),sQuery(id+"F0.wireOp",EDGE,"E8.trimOffspring"),sQuery(id+"F0.wireOp",EDGE,"E0"),sQuery(id+"F0.wireOp",EDGE,"E10.1.6"),sQuery(id+"F0.wireOp",EDGE,"E11"),sQuery(id+"F0.wireOp",EDGE,"E12"),sQuery(id+"F0.wireOp",EDGE,"E13.1.0"),sQuery(id+"F0.wireOp",EDGE,"E13.1.1"),sQuery(id+"F0.wireOp",EDGE,"E13.2.0"),sQuery(id+"F0.wireOp",EDGE,"E13.2.1")])]}),"instanceName":"1"});
            var Q1;
            Q1=makeQuery(id+"F69.opPattern","COPY",BODY,{"derivedFrom":makeQuery(id+"F5.opPattern","COPY",BODY,{"derivedFrom":makeQuery(id+"F1.opExtrude","SWEPT_BODY",BODY,{"disambiguationData":[OSD([sQuery(id+"F0.wireOp",EDGE,"E2.0"),sQuery(id+"F0.wireOp",EDGE,"E2.1"),sQuery(id+"F0.wireOp",EDGE,"E2.2"),sQuery(id+"F0.wireOp",EDGE,"E2.3"),sQuery(id+"F0.wireOp",EDGE,"E2.4"),sQuery(id+"F0.wireOp",EDGE,"E2.5"),sQuery(id+"F0.wireOp",EDGE,"E3"),sQuery(id+"F0.wireOp",EDGE,"E4"),sQuery(id+"F0.wireOp",EDGE,"E5.0"),sQuery(id+"F0.wireOp",EDGE,"E5.1"),sQuery(id+"F0.wireOp",EDGE,"E5.3"),sQuery(id+"F0.wireOp",EDGE,"E5.4"),sQuery(id+"F0.wireOp",EDGE,"E5.5"),sQuery(id+"F0.wireOp",EDGE,"E6.trimOffspring"),sQuery(id+"F0.wireOp",EDGE,"E7.trimOffspring"),sQuery(id+"F0.wireOp",EDGE,"E9.trimOffspring"),sQuery(id+"F0.wireOp",EDGE,"E10.1.0"),sQuery(id+"F0.wireOp",EDGE,"E10.1.1"),sQuery(id+"F0.wireOp",EDGE,"E10.1.2"),sQuery(id+"F0.wireOp",EDGE,"E10.1.3"),sQuery(id+"F0.wireOp",EDGE,"E10.1.5"),sQuery(id+"F0.wireOp",EDGE,"E10.1.7"),sQuery(id+"F0.wireOp",EDGE,"E10.1.8"),sQuery(id+"F0.wireOp",EDGE,"E10.1.9"),sQuery(id+"F0.wireOp",EDGE,"E10.1.10"),sQuery(id+"F0.wireOp",EDGE,"E10.1.11"),sQuery(id+"F0.wireOp",EDGE,"E10.1.12"),sQuery(id+"F0.wireOp",EDGE,"E10.1.14"),sQuery(id+"F0.wireOp",EDGE,"E10.1.15"),sQuery(id+"F0.wireOp",EDGE,"E10.1.16"),sQuery(id+"F0.wireOp",EDGE,"E10.1.18"),sQuery(id+"F0.wireOp",EDGE,"E10.1.20"),sQuery(id+"F0.wireOp",EDGE,"E10.2.0"),sQuery(id+"F0.wireOp",EDGE,"E10.2.1"),sQuery(id+"F0.wireOp",EDGE,"E10.2.2"),sQuery(id+"F0.wireOp",EDGE,"E10.2.3"),sQuery(id+"F0.wireOp",EDGE,"E10.2.5"),sQuery(id+"F0.wireOp",EDGE,"E10.2.7"),sQuery(id+"F0.wireOp",EDGE,"E10.2.8"),sQuery(id+"F0.wireOp",EDGE,"E10.2.9"),sQuery(id+"F0.wireOp",EDGE,"E10.2.10"),sQuery(id+"F0.wireOp",EDGE,"E10.2.11"),sQuery(id+"F0.wireOp",EDGE,"E10.2.12"),sQuery(id+"F0.wireOp",EDGE,"E1"),sQuery(id+"F0.wireOp",EDGE,"E10.2.14"),sQuery(id+"F0.wireOp",EDGE,"E10.2.15"),sQuery(id+"F0.wireOp",EDGE,"E10.2.16"),sQuery(id+"F0.wireOp",EDGE,"E10.2.18"),sQuery(id+"F0.wireOp",EDGE,"E10.2.20"),sQuery(id+"F0.wireOp",EDGE,"E8.trimOffspring"),sQuery(id+"F0.wireOp",EDGE,"E0"),sQuery(id+"F0.wireOp",EDGE,"E10.1.6"),sQuery(id+"F0.wireOp",EDGE,"E11"),sQuery(id+"F0.wireOp",EDGE,"E12"),sQuery(id+"F0.wireOp",EDGE,"E13.1.0"),sQuery(id+"F0.wireOp",EDGE,"E13.1.1"),sQuery(id+"F0.wireOp",EDGE,"E13.2.0"),sQuery(id+"F0.wireOp",EDGE,"E13.2.1")])]}),"instanceName":"1"}),"instanceName":"1"});
            var Q2;
            Q2=makeQuery(id+"F69.opPattern","COPY",BODY,{"derivedFrom":makeQuery(id+"F7.opPattern","COPY",BODY,{"derivedFrom":makeQuery(id+"F1.opExtrude","SWEPT_BODY",BODY,{"disambiguationData":[OSD([sQuery(id+"F0.wireOp",EDGE,"E2.0"),sQuery(id+"F0.wireOp",EDGE,"E2.1"),sQuery(id+"F0.wireOp",EDGE,"E2.2"),sQuery(id+"F0.wireOp",EDGE,"E2.3"),sQuery(id+"F0.wireOp",EDGE,"E2.4"),sQuery(id+"F0.wireOp",EDGE,"E2.5"),sQuery(id+"F0.wireOp",EDGE,"E3"),sQuery(id+"F0.wireOp",EDGE,"E4"),sQuery(id+"F0.wireOp",EDGE,"E5.0"),sQuery(id+"F0.wireOp",EDGE,"E5.1"),sQuery(id+"F0.wireOp",EDGE,"E5.3"),sQuery(id+"F0.wireOp",EDGE,"E5.4"),sQuery(id+"F0.wireOp",EDGE,"E5.5"),sQuery(id+"F0.wireOp",EDGE,"E6.trimOffspring"),sQuery(id+"F0.wireOp",EDGE,"E7.trimOffspring"),sQuery(id+"F0.wireOp",EDGE,"E9.trimOffspring"),sQuery(id+"F0.wireOp",EDGE,"E10.1.0"),sQuery(id+"F0.wireOp",EDGE,"E10.1.1"),sQuery(id+"F0.wireOp",EDGE,"E10.1.2"),sQuery(id+"F0.wireOp",EDGE,"E10.1.3"),sQuery(id+"F0.wireOp",EDGE,"E10.1.5"),sQuery(id+"F0.wireOp",EDGE,"E10.1.7"),sQuery(id+"F0.wireOp",EDGE,"E10.1.8"),sQuery(id+"F0.wireOp",EDGE,"E10.1.9"),sQuery(id+"F0.wireOp",EDGE,"E10.1.10"),sQuery(id+"F0.wireOp",EDGE,"E10.1.11"),sQuery(id+"F0.wireOp",EDGE,"E10.1.12"),sQuery(id+"F0.wireOp",EDGE,"E10.1.14"),sQuery(id+"F0.wireOp",EDGE,"E10.1.15"),sQuery(id+"F0.wireOp",EDGE,"E10.1.16"),sQuery(id+"F0.wireOp",EDGE,"E10.1.18"),sQuery(id+"F0.wireOp",EDGE,"E10.1.20"),sQuery(id+"F0.wireOp",EDGE,"E10.2.0"),sQuery(id+"F0.wireOp",EDGE,"E10.2.1"),sQuery(id+"F0.wireOp",EDGE,"E10.2.2"),sQuery(id+"F0.wireOp",EDGE,"E10.2.3"),sQuery(id+"F0.wireOp",EDGE,"E10.2.5"),sQuery(id+"F0.wireOp",EDGE,"E10.2.7"),sQuery(id+"F0.wireOp",EDGE,"E10.2.8"),sQuery(id+"F0.wireOp",EDGE,"E10.2.9"),sQuery(id+"F0.wireOp",EDGE,"E10.2.10"),sQuery(id+"F0.wireOp",EDGE,"E10.2.11"),sQuery(id+"F0.wireOp",EDGE,"E10.2.12"),sQuery(id+"F0.wireOp",EDGE,"E1"),sQuery(id+"F0.wireOp",EDGE,"E10.2.14"),sQuery(id+"F0.wireOp",EDGE,"E10.2.15"),sQuery(id+"F0.wireOp",EDGE,"E10.2.16"),sQuery(id+"F0.wireOp",EDGE,"E10.2.18"),sQuery(id+"F0.wireOp",EDGE,"E10.2.20"),sQuery(id+"F0.wireOp",EDGE,"E8.trimOffspring"),sQuery(id+"F0.wireOp",EDGE,"E0"),sQuery(id+"F0.wireOp",EDGE,"E10.1.6"),sQuery(id+"F0.wireOp",EDGE,"E11"),sQuery(id+"F0.wireOp",EDGE,"E12"),sQuery(id+"F0.wireOp",EDGE,"E13.1.0"),sQuery(id+"F0.wireOp",EDGE,"E13.1.1"),sQuery(id+"F0.wireOp",EDGE,"E13.2.0"),sQuery(id+"F0.wireOp",EDGE,"E13.2.1")])]}),"instanceName":"1"}),"instanceName":"1"});
            var Q3;
            Q3=makeQuery(id+"F69.opPattern","COPY",BODY,{"derivedFrom":makeQuery(id+"F8.opPattern","COPY",BODY,{"derivedFrom":makeQuery(id+"F7.opPattern","COPY",BODY,{"derivedFrom":makeQuery(id+"F1.opExtrude","SWEPT_BODY",BODY,{"disambiguationData":[OSD([sQuery(id+"F0.wireOp",EDGE,"E2.0"),sQuery(id+"F0.wireOp",EDGE,"E2.1"),sQuery(id+"F0.wireOp",EDGE,"E2.2"),sQuery(id+"F0.wireOp",EDGE,"E2.3"),sQuery(id+"F0.wireOp",EDGE,"E2.4"),sQuery(id+"F0.wireOp",EDGE,"E2.5"),sQuery(id+"F0.wireOp",EDGE,"E3"),sQuery(id+"F0.wireOp",EDGE,"E4"),sQuery(id+"F0.wireOp",EDGE,"E5.0"),sQuery(id+"F0.wireOp",EDGE,"E5.1"),sQuery(id+"F0.wireOp",EDGE,"E5.3"),sQuery(id+"F0.wireOp",EDGE,"E5.4"),sQuery(id+"F0.wireOp",EDGE,"E5.5"),sQuery(id+"F0.wireOp",EDGE,"E6.trimOffspring"),sQuery(id+"F0.wireOp",EDGE,"E7.trimOffspring"),sQuery(id+"F0.wireOp",EDGE,"E9.trimOffspring"),sQuery(id+"F0.wireOp",EDGE,"E10.1.0"),sQuery(id+"F0.wireOp",EDGE,"E10.1.1"),sQuery(id+"F0.wireOp",EDGE,"E10.1.2"),sQuery(id+"F0.wireOp",EDGE,"E10.1.3"),sQuery(id+"F0.wireOp",EDGE,"E10.1.5"),sQuery(id+"F0.wireOp",EDGE,"E10.1.7"),sQuery(id+"F0.wireOp",EDGE,"E10.1.8"),sQuery(id+"F0.wireOp",EDGE,"E10.1.9"),sQuery(id+"F0.wireOp",EDGE,"E10.1.10"),sQuery(id+"F0.wireOp",EDGE,"E10.1.11"),sQuery(id+"F0.wireOp",EDGE,"E10.1.12"),sQuery(id+"F0.wireOp",EDGE,"E10.1.14"),sQuery(id+"F0.wireOp",EDGE,"E10.1.15"),sQuery(id+"F0.wireOp",EDGE,"E10.1.16"),sQuery(id+"F0.wireOp",EDGE,"E10.1.18"),sQuery(id+"F0.wireOp",EDGE,"E10.1.20"),sQuery(id+"F0.wireOp",EDGE,"E10.2.0"),sQuery(id+"F0.wireOp",EDGE,"E10.2.1"),sQuery(id+"F0.wireOp",EDGE,"E10.2.2"),sQuery(id+"F0.wireOp",EDGE,"E10.2.3"),sQuery(id+"F0.wireOp",EDGE,"E10.2.5"),sQuery(id+"F0.wireOp",EDGE,"E10.2.7"),sQuery(id+"F0.wireOp",EDGE,"E10.2.8"),sQuery(id+"F0.wireOp",EDGE,"E10.2.9"),sQuery(id+"F0.wireOp",EDGE,"E10.2.10"),sQuery(id+"F0.wireOp",EDGE,"E10.2.11"),sQuery(id+"F0.wireOp",EDGE,"E10.2.12"),sQuery(id+"F0.wireOp",EDGE,"E1"),sQuery(id+"F0.wireOp",EDGE,"E10.2.14"),sQuery(id+"F0.wireOp",EDGE,"E10.2.15"),sQuery(id+"F0.wireOp",EDGE,"E10.2.16"),sQuery(id+"F0.wireOp",EDGE,"E10.2.18"),sQuery(id+"F0.wireOp",EDGE,"E10.2.20"),sQuery(id+"F0.wireOp",EDGE,"E8.trimOffspring"),sQuery(id+"F0.wireOp",EDGE,"E0"),sQuery(id+"F0.wireOp",EDGE,"E10.1.6"),sQuery(id+"F0.wireOp",EDGE,"E11"),sQuery(id+"F0.wireOp",EDGE,"E12"),sQuery(id+"F0.wireOp",EDGE,"E13.1.0"),sQuery(id+"F0.wireOp",EDGE,"E13.1.1"),sQuery(id+"F0.wireOp",EDGE,"E13.2.0"),sQuery(id+"F0.wireOp",EDGE,"E13.2.1")])]}),"instanceName":"1"}),"instanceName":"1"}),"instanceName":"1"});
            var Q4;
            Q4=makeQuery(id+"F69.opPattern","COPY",BODY,{"derivedFrom":makeQuery(id+"F9.opPattern","COPY",BODY,{"derivedFrom":makeQuery(id+"F8.opPattern","COPY",BODY,{"derivedFrom":makeQuery(id+"F7.opPattern","COPY",BODY,{"derivedFrom":makeQuery(id+"F1.opExtrude","SWEPT_BODY",BODY,{"disambiguationData":[OSD([sQuery(id+"F0.wireOp",EDGE,"E2.0"),sQuery(id+"F0.wireOp",EDGE,"E2.1"),sQuery(id+"F0.wireOp",EDGE,"E2.2"),sQuery(id+"F0.wireOp",EDGE,"E2.3"),sQuery(id+"F0.wireOp",EDGE,"E2.4"),sQuery(id+"F0.wireOp",EDGE,"E2.5"),sQuery(id+"F0.wireOp",EDGE,"E3"),sQuery(id+"F0.wireOp",EDGE,"E4"),sQuery(id+"F0.wireOp",EDGE,"E5.0"),sQuery(id+"F0.wireOp",EDGE,"E5.1"),sQuery(id+"F0.wireOp",EDGE,"E5.3"),sQuery(id+"F0.wireOp",EDGE,"E5.4"),sQuery(id+"F0.wireOp",EDGE,"E5.5"),sQuery(id+"F0.wireOp",EDGE,"E6.trimOffspring"),sQuery(id+"F0.wireOp",EDGE,"E7.trimOffspring"),sQuery(id+"F0.wireOp",EDGE,"E9.trimOffspring"),sQuery(id+"F0.wireOp",EDGE,"E10.1.0"),sQuery(id+"F0.wireOp",EDGE,"E10.1.1"),sQuery(id+"F0.wireOp",EDGE,"E10.1.2"),sQuery(id+"F0.wireOp",EDGE,"E10.1.3"),sQuery(id+"F0.wireOp",EDGE,"E10.1.5"),sQuery(id+"F0.wireOp",EDGE,"E10.1.7"),sQuery(id+"F0.wireOp",EDGE,"E10.1.8"),sQuery(id+"F0.wireOp",EDGE,"E10.1.9"),sQuery(id+"F0.wireOp",EDGE,"E10.1.10"),sQuery(id+"F0.wireOp",EDGE,"E10.1.11"),sQuery(id+"F0.wireOp",EDGE,"E10.1.12"),sQuery(id+"F0.wireOp",EDGE,"E10.1.14"),sQuery(id+"F0.wireOp",EDGE,"E10.1.15"),sQuery(id+"F0.wireOp",EDGE,"E10.1.16"),sQuery(id+"F0.wireOp",EDGE,"E10.1.18"),sQuery(id+"F0.wireOp",EDGE,"E10.1.20"),sQuery(id+"F0.wireOp",EDGE,"E10.2.0"),sQuery(id+"F0.wireOp",EDGE,"E10.2.1"),sQuery(id+"F0.wireOp",EDGE,"E10.2.2"),sQuery(id+"F0.wireOp",EDGE,"E10.2.3"),sQuery(id+"F0.wireOp",EDGE,"E10.2.5"),sQuery(id+"F0.wireOp",EDGE,"E10.2.7"),sQuery(id+"F0.wireOp",EDGE,"E10.2.8"),sQuery(id+"F0.wireOp",EDGE,"E10.2.9"),sQuery(id+"F0.wireOp",EDGE,"E10.2.10"),sQuery(id+"F0.wireOp",EDGE,"E10.2.11"),sQuery(id+"F0.wireOp",EDGE,"E10.2.12"),sQuery(id+"F0.wireOp",EDGE,"E1"),sQuery(id+"F0.wireOp",EDGE,"E10.2.14"),sQuery(id+"F0.wireOp",EDGE,"E10.2.15"),sQuery(id+"F0.wireOp",EDGE,"E10.2.16"),sQuery(id+"F0.wireOp",EDGE,"E10.2.18"),sQuery(id+"F0.wireOp",EDGE,"E10.2.20"),sQuery(id+"F0.wireOp",EDGE,"E8.trimOffspring"),sQuery(id+"F0.wireOp",EDGE,"E0"),sQuery(id+"F0.wireOp",EDGE,"E10.1.6"),sQuery(id+"F0.wireOp",EDGE,"E11"),sQuery(id+"F0.wireOp",EDGE,"E12"),sQuery(id+"F0.wireOp",EDGE,"E13.1.0"),sQuery(id+"F0.wireOp",EDGE,"E13.1.1"),sQuery(id+"F0.wireOp",EDGE,"E13.2.0"),sQuery(id+"F0.wireOp",EDGE,"E13.2.1")])]}),"instanceName":"1"}),"instanceName":"1"}),"instanceName":"1"}),"instanceName":"1"});
            var Q5;
            Q5=makeQuery(id+"F69.opPattern","COPY",BODY,{"derivedFrom":makeQuery(id+"F10.opPattern","COPY",BODY,{"derivedFrom":makeQuery(id+"F9.opPattern","COPY",BODY,{"derivedFrom":makeQuery(id+"F8.opPattern","COPY",BODY,{"derivedFrom":makeQuery(id+"F7.opPattern","COPY",BODY,{"derivedFrom":makeQuery(id+"F1.opExtrude","SWEPT_BODY",BODY,{"disambiguationData":[OSD([sQuery(id+"F0.wireOp",EDGE,"E2.0"),sQuery(id+"F0.wireOp",EDGE,"E2.1"),sQuery(id+"F0.wireOp",EDGE,"E2.2"),sQuery(id+"F0.wireOp",EDGE,"E2.3"),sQuery(id+"F0.wireOp",EDGE,"E2.4"),sQuery(id+"F0.wireOp",EDGE,"E2.5"),sQuery(id+"F0.wireOp",EDGE,"E3"),sQuery(id+"F0.wireOp",EDGE,"E4"),sQuery(id+"F0.wireOp",EDGE,"E5.0"),sQuery(id+"F0.wireOp",EDGE,"E5.1"),sQuery(id+"F0.wireOp",EDGE,"E5.3"),sQuery(id+"F0.wireOp",EDGE,"E5.4"),sQuery(id+"F0.wireOp",EDGE,"E5.5"),sQuery(id+"F0.wireOp",EDGE,"E6.trimOffspring"),sQuery(id+"F0.wireOp",EDGE,"E7.trimOffspring"),sQuery(id+"F0.wireOp",EDGE,"E9.trimOffspring"),sQuery(id+"F0.wireOp",EDGE,"E10.1.0"),sQuery(id+"F0.wireOp",EDGE,"E10.1.1"),sQuery(id+"F0.wireOp",EDGE,"E10.1.2"),sQuery(id+"F0.wireOp",EDGE,"E10.1.3"),sQuery(id+"F0.wireOp",EDGE,"E10.1.5"),sQuery(id+"F0.wireOp",EDGE,"E10.1.7"),sQuery(id+"F0.wireOp",EDGE,"E10.1.8"),sQuery(id+"F0.wireOp",EDGE,"E10.1.9"),sQuery(id+"F0.wireOp",EDGE,"E10.1.10"),sQuery(id+"F0.wireOp",EDGE,"E10.1.11"),sQuery(id+"F0.wireOp",EDGE,"E10.1.12"),sQuery(id+"F0.wireOp",EDGE,"E10.1.14"),sQuery(id+"F0.wireOp",EDGE,"E10.1.15"),sQuery(id+"F0.wireOp",EDGE,"E10.1.16"),sQuery(id+"F0.wireOp",EDGE,"E10.1.18"),sQuery(id+"F0.wireOp",EDGE,"E10.1.20"),sQuery(id+"F0.wireOp",EDGE,"E10.2.0"),sQuery(id+"F0.wireOp",EDGE,"E10.2.1"),sQuery(id+"F0.wireOp",EDGE,"E10.2.2"),sQuery(id+"F0.wireOp",EDGE,"E10.2.3"),sQuery(id+"F0.wireOp",EDGE,"E10.2.5"),sQuery(id+"F0.wireOp",EDGE,"E10.2.7"),sQuery(id+"F0.wireOp",EDGE,"E10.2.8"),sQuery(id+"F0.wireOp",EDGE,"E10.2.9"),sQuery(id+"F0.wireOp",EDGE,"E10.2.10"),sQuery(id+"F0.wireOp",EDGE,"E10.2.11"),sQuery(id+"F0.wireOp",EDGE,"E10.2.12"),sQuery(id+"F0.wireOp",EDGE,"E1"),sQuery(id+"F0.wireOp",EDGE,"E10.2.14"),sQuery(id+"F0.wireOp",EDGE,"E10.2.15"),sQuery(id+"F0.wireOp",EDGE,"E10.2.16"),sQuery(id+"F0.wireOp",EDGE,"E10.2.18"),sQuery(id+"F0.wireOp",EDGE,"E10.2.20"),sQuery(id+"F0.wireOp",EDGE,"E8.trimOffspring"),sQuery(id+"F0.wireOp",EDGE,"E0"),sQuery(id+"F0.wireOp",EDGE,"E10.1.6"),sQuery(id+"F0.wireOp",EDGE,"E11"),sQuery(id+"F0.wireOp",EDGE,"E12"),sQuery(id+"F0.wireOp",EDGE,"E13.1.0"),sQuery(id+"F0.wireOp",EDGE,"E13.1.1"),sQuery(id+"F0.wireOp",EDGE,"E13.2.0"),sQuery(id+"F0.wireOp",EDGE,"E13.2.1")])]}),"instanceName":"1"}),"instanceName":"1"}),"instanceName":"1"}),"instanceName":"1"}),"instanceName":"1"});
            transform(context, id + "F70", {"entities" : qUnion([Q0, Q1, Q2, Q3, Q4, Q5]), "transformType" : TransformType.TRANSLATION_3D, "dx" : 0 * mm, "dy" : -68.8 * mm, "dz" : 0 * mm, "makeCopy" : true});
        }
        {
            var Q0;
            Q0=makeQuery(id+"F70.opPattern","COPY",BODY,{"derivedFrom":makeQuery(id+"F69.opPattern","COPY",BODY,{"derivedFrom":makeQuery(id+"F1.opExtrude","SWEPT_BODY",BODY,{"disambiguationData":[OSD([sQuery(id+"F0.wireOp",EDGE,"E2.0"),sQuery(id+"F0.wireOp",EDGE,"E2.1"),sQuery(id+"F0.wireOp",EDGE,"E2.2"),sQuery(id+"F0.wireOp",EDGE,"E2.3"),sQuery(id+"F0.wireOp",EDGE,"E2.4"),sQuery(id+"F0.wireOp",EDGE,"E2.5"),sQuery(id+"F0.wireOp",EDGE,"E3"),sQuery(id+"F0.wireOp",EDGE,"E4"),sQuery(id+"F0.wireOp",EDGE,"E5.0"),sQuery(id+"F0.wireOp",EDGE,"E5.1"),sQuery(id+"F0.wireOp",EDGE,"E5.3"),sQuery(id+"F0.wireOp",EDGE,"E5.4"),sQuery(id+"F0.wireOp",EDGE,"E5.5"),sQuery(id+"F0.wireOp",EDGE,"E6.trimOffspring"),sQuery(id+"F0.wireOp",EDGE,"E7.trimOffspring"),sQuery(id+"F0.wireOp",EDGE,"E9.trimOffspring"),sQuery(id+"F0.wireOp",EDGE,"E10.1.0"),sQuery(id+"F0.wireOp",EDGE,"E10.1.1"),sQuery(id+"F0.wireOp",EDGE,"E10.1.2"),sQuery(id+"F0.wireOp",EDGE,"E10.1.3"),sQuery(id+"F0.wireOp",EDGE,"E10.1.5"),sQuery(id+"F0.wireOp",EDGE,"E10.1.7"),sQuery(id+"F0.wireOp",EDGE,"E10.1.8"),sQuery(id+"F0.wireOp",EDGE,"E10.1.9"),sQuery(id+"F0.wireOp",EDGE,"E10.1.10"),sQuery(id+"F0.wireOp",EDGE,"E10.1.11"),sQuery(id+"F0.wireOp",EDGE,"E10.1.12"),sQuery(id+"F0.wireOp",EDGE,"E10.1.14"),sQuery(id+"F0.wireOp",EDGE,"E10.1.15"),sQuery(id+"F0.wireOp",EDGE,"E10.1.16"),sQuery(id+"F0.wireOp",EDGE,"E10.1.18"),sQuery(id+"F0.wireOp",EDGE,"E10.1.20"),sQuery(id+"F0.wireOp",EDGE,"E10.2.0"),sQuery(id+"F0.wireOp",EDGE,"E10.2.1"),sQuery(id+"F0.wireOp",EDGE,"E10.2.2"),sQuery(id+"F0.wireOp",EDGE,"E10.2.3"),sQuery(id+"F0.wireOp",EDGE,"E10.2.5"),sQuery(id+"F0.wireOp",EDGE,"E10.2.7"),sQuery(id+"F0.wireOp",EDGE,"E10.2.8"),sQuery(id+"F0.wireOp",EDGE,"E10.2.9"),sQuery(id+"F0.wireOp",EDGE,"E10.2.10"),sQuery(id+"F0.wireOp",EDGE,"E10.2.11"),sQuery(id+"F0.wireOp",EDGE,"E10.2.12"),sQuery(id+"F0.wireOp",EDGE,"E1"),sQuery(id+"F0.wireOp",EDGE,"E10.2.14"),sQuery(id+"F0.wireOp",EDGE,"E10.2.15"),sQuery(id+"F0.wireOp",EDGE,"E10.2.16"),sQuery(id+"F0.wireOp",EDGE,"E10.2.18"),sQuery(id+"F0.wireOp",EDGE,"E10.2.20"),sQuery(id+"F0.wireOp",EDGE,"E8.trimOffspring"),sQuery(id+"F0.wireOp",EDGE,"E0"),sQuery(id+"F0.wireOp",EDGE,"E10.1.6"),sQuery(id+"F0.wireOp",EDGE,"E11"),sQuery(id+"F0.wireOp",EDGE,"E12"),sQuery(id+"F0.wireOp",EDGE,"E13.1.0"),sQuery(id+"F0.wireOp",EDGE,"E13.1.1"),sQuery(id+"F0.wireOp",EDGE,"E13.2.0"),sQuery(id+"F0.wireOp",EDGE,"E13.2.1")])]}),"instanceName":"1"}),"instanceName":"1"});
            var Q1;
            Q1=makeQuery(id+"F70.opPattern","COPY",BODY,{"derivedFrom":makeQuery(id+"F69.opPattern","COPY",BODY,{"derivedFrom":makeQuery(id+"F5.opPattern","COPY",BODY,{"derivedFrom":makeQuery(id+"F1.opExtrude","SWEPT_BODY",BODY,{"disambiguationData":[OSD([sQuery(id+"F0.wireOp",EDGE,"E2.0"),sQuery(id+"F0.wireOp",EDGE,"E2.1"),sQuery(id+"F0.wireOp",EDGE,"E2.2"),sQuery(id+"F0.wireOp",EDGE,"E2.3"),sQuery(id+"F0.wireOp",EDGE,"E2.4"),sQuery(id+"F0.wireOp",EDGE,"E2.5"),sQuery(id+"F0.wireOp",EDGE,"E3"),sQuery(id+"F0.wireOp",EDGE,"E4"),sQuery(id+"F0.wireOp",EDGE,"E5.0"),sQuery(id+"F0.wireOp",EDGE,"E5.1"),sQuery(id+"F0.wireOp",EDGE,"E5.3"),sQuery(id+"F0.wireOp",EDGE,"E5.4"),sQuery(id+"F0.wireOp",EDGE,"E5.5"),sQuery(id+"F0.wireOp",EDGE,"E6.trimOffspring"),sQuery(id+"F0.wireOp",EDGE,"E7.trimOffspring"),sQuery(id+"F0.wireOp",EDGE,"E9.trimOffspring"),sQuery(id+"F0.wireOp",EDGE,"E10.1.0"),sQuery(id+"F0.wireOp",EDGE,"E10.1.1"),sQuery(id+"F0.wireOp",EDGE,"E10.1.2"),sQuery(id+"F0.wireOp",EDGE,"E10.1.3"),sQuery(id+"F0.wireOp",EDGE,"E10.1.5"),sQuery(id+"F0.wireOp",EDGE,"E10.1.7"),sQuery(id+"F0.wireOp",EDGE,"E10.1.8"),sQuery(id+"F0.wireOp",EDGE,"E10.1.9"),sQuery(id+"F0.wireOp",EDGE,"E10.1.10"),sQuery(id+"F0.wireOp",EDGE,"E10.1.11"),sQuery(id+"F0.wireOp",EDGE,"E10.1.12"),sQuery(id+"F0.wireOp",EDGE,"E10.1.14"),sQuery(id+"F0.wireOp",EDGE,"E10.1.15"),sQuery(id+"F0.wireOp",EDGE,"E10.1.16"),sQuery(id+"F0.wireOp",EDGE,"E10.1.18"),sQuery(id+"F0.wireOp",EDGE,"E10.1.20"),sQuery(id+"F0.wireOp",EDGE,"E10.2.0"),sQuery(id+"F0.wireOp",EDGE,"E10.2.1"),sQuery(id+"F0.wireOp",EDGE,"E10.2.2"),sQuery(id+"F0.wireOp",EDGE,"E10.2.3"),sQuery(id+"F0.wireOp",EDGE,"E10.2.5"),sQuery(id+"F0.wireOp",EDGE,"E10.2.7"),sQuery(id+"F0.wireOp",EDGE,"E10.2.8"),sQuery(id+"F0.wireOp",EDGE,"E10.2.9"),sQuery(id+"F0.wireOp",EDGE,"E10.2.10"),sQuery(id+"F0.wireOp",EDGE,"E10.2.11"),sQuery(id+"F0.wireOp",EDGE,"E10.2.12"),sQuery(id+"F0.wireOp",EDGE,"E1"),sQuery(id+"F0.wireOp",EDGE,"E10.2.14"),sQuery(id+"F0.wireOp",EDGE,"E10.2.15"),sQuery(id+"F0.wireOp",EDGE,"E10.2.16"),sQuery(id+"F0.wireOp",EDGE,"E10.2.18"),sQuery(id+"F0.wireOp",EDGE,"E10.2.20"),sQuery(id+"F0.wireOp",EDGE,"E8.trimOffspring"),sQuery(id+"F0.wireOp",EDGE,"E0"),sQuery(id+"F0.wireOp",EDGE,"E10.1.6"),sQuery(id+"F0.wireOp",EDGE,"E11"),sQuery(id+"F0.wireOp",EDGE,"E12"),sQuery(id+"F0.wireOp",EDGE,"E13.1.0"),sQuery(id+"F0.wireOp",EDGE,"E13.1.1"),sQuery(id+"F0.wireOp",EDGE,"E13.2.0"),sQuery(id+"F0.wireOp",EDGE,"E13.2.1")])]}),"instanceName":"1"}),"instanceName":"1"}),"instanceName":"1"});
            var Q2;
            Q2=makeQuery(id+"F70.opPattern","COPY",BODY,{"derivedFrom":makeQuery(id+"F69.opPattern","COPY",BODY,{"derivedFrom":makeQuery(id+"F7.opPattern","COPY",BODY,{"derivedFrom":makeQuery(id+"F1.opExtrude","SWEPT_BODY",BODY,{"disambiguationData":[OSD([sQuery(id+"F0.wireOp",EDGE,"E2.0"),sQuery(id+"F0.wireOp",EDGE,"E2.1"),sQuery(id+"F0.wireOp",EDGE,"E2.2"),sQuery(id+"F0.wireOp",EDGE,"E2.3"),sQuery(id+"F0.wireOp",EDGE,"E2.4"),sQuery(id+"F0.wireOp",EDGE,"E2.5"),sQuery(id+"F0.wireOp",EDGE,"E3"),sQuery(id+"F0.wireOp",EDGE,"E4"),sQuery(id+"F0.wireOp",EDGE,"E5.0"),sQuery(id+"F0.wireOp",EDGE,"E5.1"),sQuery(id+"F0.wireOp",EDGE,"E5.3"),sQuery(id+"F0.wireOp",EDGE,"E5.4"),sQuery(id+"F0.wireOp",EDGE,"E5.5"),sQuery(id+"F0.wireOp",EDGE,"E6.trimOffspring"),sQuery(id+"F0.wireOp",EDGE,"E7.trimOffspring"),sQuery(id+"F0.wireOp",EDGE,"E9.trimOffspring"),sQuery(id+"F0.wireOp",EDGE,"E10.1.0"),sQuery(id+"F0.wireOp",EDGE,"E10.1.1"),sQuery(id+"F0.wireOp",EDGE,"E10.1.2"),sQuery(id+"F0.wireOp",EDGE,"E10.1.3"),sQuery(id+"F0.wireOp",EDGE,"E10.1.5"),sQuery(id+"F0.wireOp",EDGE,"E10.1.7"),sQuery(id+"F0.wireOp",EDGE,"E10.1.8"),sQuery(id+"F0.wireOp",EDGE,"E10.1.9"),sQuery(id+"F0.wireOp",EDGE,"E10.1.10"),sQuery(id+"F0.wireOp",EDGE,"E10.1.11"),sQuery(id+"F0.wireOp",EDGE,"E10.1.12"),sQuery(id+"F0.wireOp",EDGE,"E10.1.14"),sQuery(id+"F0.wireOp",EDGE,"E10.1.15"),sQuery(id+"F0.wireOp",EDGE,"E10.1.16"),sQuery(id+"F0.wireOp",EDGE,"E10.1.18"),sQuery(id+"F0.wireOp",EDGE,"E10.1.20"),sQuery(id+"F0.wireOp",EDGE,"E10.2.0"),sQuery(id+"F0.wireOp",EDGE,"E10.2.1"),sQuery(id+"F0.wireOp",EDGE,"E10.2.2"),sQuery(id+"F0.wireOp",EDGE,"E10.2.3"),sQuery(id+"F0.wireOp",EDGE,"E10.2.5"),sQuery(id+"F0.wireOp",EDGE,"E10.2.7"),sQuery(id+"F0.wireOp",EDGE,"E10.2.8"),sQuery(id+"F0.wireOp",EDGE,"E10.2.9"),sQuery(id+"F0.wireOp",EDGE,"E10.2.10"),sQuery(id+"F0.wireOp",EDGE,"E10.2.11"),sQuery(id+"F0.wireOp",EDGE,"E10.2.12"),sQuery(id+"F0.wireOp",EDGE,"E1"),sQuery(id+"F0.wireOp",EDGE,"E10.2.14"),sQuery(id+"F0.wireOp",EDGE,"E10.2.15"),sQuery(id+"F0.wireOp",EDGE,"E10.2.16"),sQuery(id+"F0.wireOp",EDGE,"E10.2.18"),sQuery(id+"F0.wireOp",EDGE,"E10.2.20"),sQuery(id+"F0.wireOp",EDGE,"E8.trimOffspring"),sQuery(id+"F0.wireOp",EDGE,"E0"),sQuery(id+"F0.wireOp",EDGE,"E10.1.6"),sQuery(id+"F0.wireOp",EDGE,"E11"),sQuery(id+"F0.wireOp",EDGE,"E12"),sQuery(id+"F0.wireOp",EDGE,"E13.1.0"),sQuery(id+"F0.wireOp",EDGE,"E13.1.1"),sQuery(id+"F0.wireOp",EDGE,"E13.2.0"),sQuery(id+"F0.wireOp",EDGE,"E13.2.1")])]}),"instanceName":"1"}),"instanceName":"1"}),"instanceName":"1"});
            var Q3;
            Q3=makeQuery(id+"F70.opPattern","COPY",BODY,{"derivedFrom":makeQuery(id+"F69.opPattern","COPY",BODY,{"derivedFrom":makeQuery(id+"F8.opPattern","COPY",BODY,{"derivedFrom":makeQuery(id+"F7.opPattern","COPY",BODY,{"derivedFrom":makeQuery(id+"F1.opExtrude","SWEPT_BODY",BODY,{"disambiguationData":[OSD([sQuery(id+"F0.wireOp",EDGE,"E2.0"),sQuery(id+"F0.wireOp",EDGE,"E2.1"),sQuery(id+"F0.wireOp",EDGE,"E2.2"),sQuery(id+"F0.wireOp",EDGE,"E2.3"),sQuery(id+"F0.wireOp",EDGE,"E2.4"),sQuery(id+"F0.wireOp",EDGE,"E2.5"),sQuery(id+"F0.wireOp",EDGE,"E3"),sQuery(id+"F0.wireOp",EDGE,"E4"),sQuery(id+"F0.wireOp",EDGE,"E5.0"),sQuery(id+"F0.wireOp",EDGE,"E5.1"),sQuery(id+"F0.wireOp",EDGE,"E5.3"),sQuery(id+"F0.wireOp",EDGE,"E5.4"),sQuery(id+"F0.wireOp",EDGE,"E5.5"),sQuery(id+"F0.wireOp",EDGE,"E6.trimOffspring"),sQuery(id+"F0.wireOp",EDGE,"E7.trimOffspring"),sQuery(id+"F0.wireOp",EDGE,"E9.trimOffspring"),sQuery(id+"F0.wireOp",EDGE,"E10.1.0"),sQuery(id+"F0.wireOp",EDGE,"E10.1.1"),sQuery(id+"F0.wireOp",EDGE,"E10.1.2"),sQuery(id+"F0.wireOp",EDGE,"E10.1.3"),sQuery(id+"F0.wireOp",EDGE,"E10.1.5"),sQuery(id+"F0.wireOp",EDGE,"E10.1.7"),sQuery(id+"F0.wireOp",EDGE,"E10.1.8"),sQuery(id+"F0.wireOp",EDGE,"E10.1.9"),sQuery(id+"F0.wireOp",EDGE,"E10.1.10"),sQuery(id+"F0.wireOp",EDGE,"E10.1.11"),sQuery(id+"F0.wireOp",EDGE,"E10.1.12"),sQuery(id+"F0.wireOp",EDGE,"E10.1.14"),sQuery(id+"F0.wireOp",EDGE,"E10.1.15"),sQuery(id+"F0.wireOp",EDGE,"E10.1.16"),sQuery(id+"F0.wireOp",EDGE,"E10.1.18"),sQuery(id+"F0.wireOp",EDGE,"E10.1.20"),sQuery(id+"F0.wireOp",EDGE,"E10.2.0"),sQuery(id+"F0.wireOp",EDGE,"E10.2.1"),sQuery(id+"F0.wireOp",EDGE,"E10.2.2"),sQuery(id+"F0.wireOp",EDGE,"E10.2.3"),sQuery(id+"F0.wireOp",EDGE,"E10.2.5"),sQuery(id+"F0.wireOp",EDGE,"E10.2.7"),sQuery(id+"F0.wireOp",EDGE,"E10.2.8"),sQuery(id+"F0.wireOp",EDGE,"E10.2.9"),sQuery(id+"F0.wireOp",EDGE,"E10.2.10"),sQuery(id+"F0.wireOp",EDGE,"E10.2.11"),sQuery(id+"F0.wireOp",EDGE,"E10.2.12"),sQuery(id+"F0.wireOp",EDGE,"E1"),sQuery(id+"F0.wireOp",EDGE,"E10.2.14"),sQuery(id+"F0.wireOp",EDGE,"E10.2.15"),sQuery(id+"F0.wireOp",EDGE,"E10.2.16"),sQuery(id+"F0.wireOp",EDGE,"E10.2.18"),sQuery(id+"F0.wireOp",EDGE,"E10.2.20"),sQuery(id+"F0.wireOp",EDGE,"E8.trimOffspring"),sQuery(id+"F0.wireOp",EDGE,"E0"),sQuery(id+"F0.wireOp",EDGE,"E10.1.6"),sQuery(id+"F0.wireOp",EDGE,"E11"),sQuery(id+"F0.wireOp",EDGE,"E12"),sQuery(id+"F0.wireOp",EDGE,"E13.1.0"),sQuery(id+"F0.wireOp",EDGE,"E13.1.1"),sQuery(id+"F0.wireOp",EDGE,"E13.2.0"),sQuery(id+"F0.wireOp",EDGE,"E13.2.1")])]}),"instanceName":"1"}),"instanceName":"1"}),"instanceName":"1"}),"instanceName":"1"});
            var Q4;
            Q4=makeQuery(id+"F70.opPattern","COPY",BODY,{"derivedFrom":makeQuery(id+"F69.opPattern","COPY",BODY,{"derivedFrom":makeQuery(id+"F9.opPattern","COPY",BODY,{"derivedFrom":makeQuery(id+"F8.opPattern","COPY",BODY,{"derivedFrom":makeQuery(id+"F7.opPattern","COPY",BODY,{"derivedFrom":makeQuery(id+"F1.opExtrude","SWEPT_BODY",BODY,{"disambiguationData":[OSD([sQuery(id+"F0.wireOp",EDGE,"E2.0"),sQuery(id+"F0.wireOp",EDGE,"E2.1"),sQuery(id+"F0.wireOp",EDGE,"E2.2"),sQuery(id+"F0.wireOp",EDGE,"E2.3"),sQuery(id+"F0.wireOp",EDGE,"E2.4"),sQuery(id+"F0.wireOp",EDGE,"E2.5"),sQuery(id+"F0.wireOp",EDGE,"E3"),sQuery(id+"F0.wireOp",EDGE,"E4"),sQuery(id+"F0.wireOp",EDGE,"E5.0"),sQuery(id+"F0.wireOp",EDGE,"E5.1"),sQuery(id+"F0.wireOp",EDGE,"E5.3"),sQuery(id+"F0.wireOp",EDGE,"E5.4"),sQuery(id+"F0.wireOp",EDGE,"E5.5"),sQuery(id+"F0.wireOp",EDGE,"E6.trimOffspring"),sQuery(id+"F0.wireOp",EDGE,"E7.trimOffspring"),sQuery(id+"F0.wireOp",EDGE,"E9.trimOffspring"),sQuery(id+"F0.wireOp",EDGE,"E10.1.0"),sQuery(id+"F0.wireOp",EDGE,"E10.1.1"),sQuery(id+"F0.wireOp",EDGE,"E10.1.2"),sQuery(id+"F0.wireOp",EDGE,"E10.1.3"),sQuery(id+"F0.wireOp",EDGE,"E10.1.5"),sQuery(id+"F0.wireOp",EDGE,"E10.1.7"),sQuery(id+"F0.wireOp",EDGE,"E10.1.8"),sQuery(id+"F0.wireOp",EDGE,"E10.1.9"),sQuery(id+"F0.wireOp",EDGE,"E10.1.10"),sQuery(id+"F0.wireOp",EDGE,"E10.1.11"),sQuery(id+"F0.wireOp",EDGE,"E10.1.12"),sQuery(id+"F0.wireOp",EDGE,"E10.1.14"),sQuery(id+"F0.wireOp",EDGE,"E10.1.15"),sQuery(id+"F0.wireOp",EDGE,"E10.1.16"),sQuery(id+"F0.wireOp",EDGE,"E10.1.18"),sQuery(id+"F0.wireOp",EDGE,"E10.1.20"),sQuery(id+"F0.wireOp",EDGE,"E10.2.0"),sQuery(id+"F0.wireOp",EDGE,"E10.2.1"),sQuery(id+"F0.wireOp",EDGE,"E10.2.2"),sQuery(id+"F0.wireOp",EDGE,"E10.2.3"),sQuery(id+"F0.wireOp",EDGE,"E10.2.5"),sQuery(id+"F0.wireOp",EDGE,"E10.2.7"),sQuery(id+"F0.wireOp",EDGE,"E10.2.8"),sQuery(id+"F0.wireOp",EDGE,"E10.2.9"),sQuery(id+"F0.wireOp",EDGE,"E10.2.10"),sQuery(id+"F0.wireOp",EDGE,"E10.2.11"),sQuery(id+"F0.wireOp",EDGE,"E10.2.12"),sQuery(id+"F0.wireOp",EDGE,"E1"),sQuery(id+"F0.wireOp",EDGE,"E10.2.14"),sQuery(id+"F0.wireOp",EDGE,"E10.2.15"),sQuery(id+"F0.wireOp",EDGE,"E10.2.16"),sQuery(id+"F0.wireOp",EDGE,"E10.2.18"),sQuery(id+"F0.wireOp",EDGE,"E10.2.20"),sQuery(id+"F0.wireOp",EDGE,"E8.trimOffspring"),sQuery(id+"F0.wireOp",EDGE,"E0"),sQuery(id+"F0.wireOp",EDGE,"E10.1.6"),sQuery(id+"F0.wireOp",EDGE,"E11"),sQuery(id+"F0.wireOp",EDGE,"E12"),sQuery(id+"F0.wireOp",EDGE,"E13.1.0"),sQuery(id+"F0.wireOp",EDGE,"E13.1.1"),sQuery(id+"F0.wireOp",EDGE,"E13.2.0"),sQuery(id+"F0.wireOp",EDGE,"E13.2.1")])]}),"instanceName":"1"}),"instanceName":"1"}),"instanceName":"1"}),"instanceName":"1"}),"instanceName":"1"});
            var Q5;
            Q5=makeQuery(id+"F70.opPattern","COPY",BODY,{"derivedFrom":makeQuery(id+"F69.opPattern","COPY",BODY,{"derivedFrom":makeQuery(id+"F10.opPattern","COPY",BODY,{"derivedFrom":makeQuery(id+"F9.opPattern","COPY",BODY,{"derivedFrom":makeQuery(id+"F8.opPattern","COPY",BODY,{"derivedFrom":makeQuery(id+"F7.opPattern","COPY",BODY,{"derivedFrom":makeQuery(id+"F1.opExtrude","SWEPT_BODY",BODY,{"disambiguationData":[OSD([sQuery(id+"F0.wireOp",EDGE,"E2.0"),sQuery(id+"F0.wireOp",EDGE,"E2.1"),sQuery(id+"F0.wireOp",EDGE,"E2.2"),sQuery(id+"F0.wireOp",EDGE,"E2.3"),sQuery(id+"F0.wireOp",EDGE,"E2.4"),sQuery(id+"F0.wireOp",EDGE,"E2.5"),sQuery(id+"F0.wireOp",EDGE,"E3"),sQuery(id+"F0.wireOp",EDGE,"E4"),sQuery(id+"F0.wireOp",EDGE,"E5.0"),sQuery(id+"F0.wireOp",EDGE,"E5.1"),sQuery(id+"F0.wireOp",EDGE,"E5.3"),sQuery(id+"F0.wireOp",EDGE,"E5.4"),sQuery(id+"F0.wireOp",EDGE,"E5.5"),sQuery(id+"F0.wireOp",EDGE,"E6.trimOffspring"),sQuery(id+"F0.wireOp",EDGE,"E7.trimOffspring"),sQuery(id+"F0.wireOp",EDGE,"E9.trimOffspring"),sQuery(id+"F0.wireOp",EDGE,"E10.1.0"),sQuery(id+"F0.wireOp",EDGE,"E10.1.1"),sQuery(id+"F0.wireOp",EDGE,"E10.1.2"),sQuery(id+"F0.wireOp",EDGE,"E10.1.3"),sQuery(id+"F0.wireOp",EDGE,"E10.1.5"),sQuery(id+"F0.wireOp",EDGE,"E10.1.7"),sQuery(id+"F0.wireOp",EDGE,"E10.1.8"),sQuery(id+"F0.wireOp",EDGE,"E10.1.9"),sQuery(id+"F0.wireOp",EDGE,"E10.1.10"),sQuery(id+"F0.wireOp",EDGE,"E10.1.11"),sQuery(id+"F0.wireOp",EDGE,"E10.1.12"),sQuery(id+"F0.wireOp",EDGE,"E10.1.14"),sQuery(id+"F0.wireOp",EDGE,"E10.1.15"),sQuery(id+"F0.wireOp",EDGE,"E10.1.16"),sQuery(id+"F0.wireOp",EDGE,"E10.1.18"),sQuery(id+"F0.wireOp",EDGE,"E10.1.20"),sQuery(id+"F0.wireOp",EDGE,"E10.2.0"),sQuery(id+"F0.wireOp",EDGE,"E10.2.1"),sQuery(id+"F0.wireOp",EDGE,"E10.2.2"),sQuery(id+"F0.wireOp",EDGE,"E10.2.3"),sQuery(id+"F0.wireOp",EDGE,"E10.2.5"),sQuery(id+"F0.wireOp",EDGE,"E10.2.7"),sQuery(id+"F0.wireOp",EDGE,"E10.2.8"),sQuery(id+"F0.wireOp",EDGE,"E10.2.9"),sQuery(id+"F0.wireOp",EDGE,"E10.2.10"),sQuery(id+"F0.wireOp",EDGE,"E10.2.11"),sQuery(id+"F0.wireOp",EDGE,"E10.2.12"),sQuery(id+"F0.wireOp",EDGE,"E1"),sQuery(id+"F0.wireOp",EDGE,"E10.2.14"),sQuery(id+"F0.wireOp",EDGE,"E10.2.15"),sQuery(id+"F0.wireOp",EDGE,"E10.2.16"),sQuery(id+"F0.wireOp",EDGE,"E10.2.18"),sQuery(id+"F0.wireOp",EDGE,"E10.2.20"),sQuery(id+"F0.wireOp",EDGE,"E8.trimOffspring"),sQuery(id+"F0.wireOp",EDGE,"E0"),sQuery(id+"F0.wireOp",EDGE,"E10.1.6"),sQuery(id+"F0.wireOp",EDGE,"E11"),sQuery(id+"F0.wireOp",EDGE,"E12"),sQuery(id+"F0.wireOp",EDGE,"E13.1.0"),sQuery(id+"F0.wireOp",EDGE,"E13.1.1"),sQuery(id+"F0.wireOp",EDGE,"E13.2.0"),sQuery(id+"F0.wireOp",EDGE,"E13.2.1")])]}),"instanceName":"1"}),"instanceName":"1"}),"instanceName":"1"}),"instanceName":"1"}),"instanceName":"1"}),"instanceName":"1"});
            transform(context, id + "F71", {"entities" : qUnion([Q0, Q1, Q2, Q3, Q4, Q5]), "transformType" : TransformType.TRANSLATION_3D, "dx" : 0 * mm, "dy" : -68.8 * mm, "dz" : 0 * mm, "makeCopy" : true});
        }
        {
            var Q0;
            Q0=makeQuery(id+"F71.opPattern","COPY",BODY,{"derivedFrom":makeQuery(id+"F70.opPattern","COPY",BODY,{"derivedFrom":makeQuery(id+"F69.opPattern","COPY",BODY,{"derivedFrom":makeQuery(id+"F1.opExtrude","SWEPT_BODY",BODY,{"disambiguationData":[OSD([sQuery(id+"F0.wireOp",EDGE,"E2.0"),sQuery(id+"F0.wireOp",EDGE,"E2.1"),sQuery(id+"F0.wireOp",EDGE,"E2.2"),sQuery(id+"F0.wireOp",EDGE,"E2.3"),sQuery(id+"F0.wireOp",EDGE,"E2.4"),sQuery(id+"F0.wireOp",EDGE,"E2.5"),sQuery(id+"F0.wireOp",EDGE,"E3"),sQuery(id+"F0.wireOp",EDGE,"E4"),sQuery(id+"F0.wireOp",EDGE,"E5.0"),sQuery(id+"F0.wireOp",EDGE,"E5.1"),sQuery(id+"F0.wireOp",EDGE,"E5.3"),sQuery(id+"F0.wireOp",EDGE,"E5.4"),sQuery(id+"F0.wireOp",EDGE,"E5.5"),sQuery(id+"F0.wireOp",EDGE,"E6.trimOffspring"),sQuery(id+"F0.wireOp",EDGE,"E7.trimOffspring"),sQuery(id+"F0.wireOp",EDGE,"E9.trimOffspring"),sQuery(id+"F0.wireOp",EDGE,"E10.1.0"),sQuery(id+"F0.wireOp",EDGE,"E10.1.1"),sQuery(id+"F0.wireOp",EDGE,"E10.1.2"),sQuery(id+"F0.wireOp",EDGE,"E10.1.3"),sQuery(id+"F0.wireOp",EDGE,"E10.1.5"),sQuery(id+"F0.wireOp",EDGE,"E10.1.7"),sQuery(id+"F0.wireOp",EDGE,"E10.1.8"),sQuery(id+"F0.wireOp",EDGE,"E10.1.9"),sQuery(id+"F0.wireOp",EDGE,"E10.1.10"),sQuery(id+"F0.wireOp",EDGE,"E10.1.11"),sQuery(id+"F0.wireOp",EDGE,"E10.1.12"),sQuery(id+"F0.wireOp",EDGE,"E10.1.14"),sQuery(id+"F0.wireOp",EDGE,"E10.1.15"),sQuery(id+"F0.wireOp",EDGE,"E10.1.16"),sQuery(id+"F0.wireOp",EDGE,"E10.1.18"),sQuery(id+"F0.wireOp",EDGE,"E10.1.20"),sQuery(id+"F0.wireOp",EDGE,"E10.2.0"),sQuery(id+"F0.wireOp",EDGE,"E10.2.1"),sQuery(id+"F0.wireOp",EDGE,"E10.2.2"),sQuery(id+"F0.wireOp",EDGE,"E10.2.3"),sQuery(id+"F0.wireOp",EDGE,"E10.2.5"),sQuery(id+"F0.wireOp",EDGE,"E10.2.7"),sQuery(id+"F0.wireOp",EDGE,"E10.2.8"),sQuery(id+"F0.wireOp",EDGE,"E10.2.9"),sQuery(id+"F0.wireOp",EDGE,"E10.2.10"),sQuery(id+"F0.wireOp",EDGE,"E10.2.11"),sQuery(id+"F0.wireOp",EDGE,"E10.2.12"),sQuery(id+"F0.wireOp",EDGE,"E1"),sQuery(id+"F0.wireOp",EDGE,"E10.2.14"),sQuery(id+"F0.wireOp",EDGE,"E10.2.15"),sQuery(id+"F0.wireOp",EDGE,"E10.2.16"),sQuery(id+"F0.wireOp",EDGE,"E10.2.18"),sQuery(id+"F0.wireOp",EDGE,"E10.2.20"),sQuery(id+"F0.wireOp",EDGE,"E8.trimOffspring"),sQuery(id+"F0.wireOp",EDGE,"E0"),sQuery(id+"F0.wireOp",EDGE,"E10.1.6"),sQuery(id+"F0.wireOp",EDGE,"E11"),sQuery(id+"F0.wireOp",EDGE,"E12"),sQuery(id+"F0.wireOp",EDGE,"E13.1.0"),sQuery(id+"F0.wireOp",EDGE,"E13.1.1"),sQuery(id+"F0.wireOp",EDGE,"E13.2.0"),sQuery(id+"F0.wireOp",EDGE,"E13.2.1")])]}),"instanceName":"1"}),"instanceName":"1"}),"instanceName":"1"});
            var Q1;
            Q1=makeQuery(id+"F71.opPattern","COPY",BODY,{"derivedFrom":makeQuery(id+"F70.opPattern","COPY",BODY,{"derivedFrom":makeQuery(id+"F69.opPattern","COPY",BODY,{"derivedFrom":makeQuery(id+"F5.opPattern","COPY",BODY,{"derivedFrom":makeQuery(id+"F1.opExtrude","SWEPT_BODY",BODY,{"disambiguationData":[OSD([sQuery(id+"F0.wireOp",EDGE,"E2.0"),sQuery(id+"F0.wireOp",EDGE,"E2.1"),sQuery(id+"F0.wireOp",EDGE,"E2.2"),sQuery(id+"F0.wireOp",EDGE,"E2.3"),sQuery(id+"F0.wireOp",EDGE,"E2.4"),sQuery(id+"F0.wireOp",EDGE,"E2.5"),sQuery(id+"F0.wireOp",EDGE,"E3"),sQuery(id+"F0.wireOp",EDGE,"E4"),sQuery(id+"F0.wireOp",EDGE,"E5.0"),sQuery(id+"F0.wireOp",EDGE,"E5.1"),sQuery(id+"F0.wireOp",EDGE,"E5.3"),sQuery(id+"F0.wireOp",EDGE,"E5.4"),sQuery(id+"F0.wireOp",EDGE,"E5.5"),sQuery(id+"F0.wireOp",EDGE,"E6.trimOffspring"),sQuery(id+"F0.wireOp",EDGE,"E7.trimOffspring"),sQuery(id+"F0.wireOp",EDGE,"E9.trimOffspring"),sQuery(id+"F0.wireOp",EDGE,"E10.1.0"),sQuery(id+"F0.wireOp",EDGE,"E10.1.1"),sQuery(id+"F0.wireOp",EDGE,"E10.1.2"),sQuery(id+"F0.wireOp",EDGE,"E10.1.3"),sQuery(id+"F0.wireOp",EDGE,"E10.1.5"),sQuery(id+"F0.wireOp",EDGE,"E10.1.7"),sQuery(id+"F0.wireOp",EDGE,"E10.1.8"),sQuery(id+"F0.wireOp",EDGE,"E10.1.9"),sQuery(id+"F0.wireOp",EDGE,"E10.1.10"),sQuery(id+"F0.wireOp",EDGE,"E10.1.11"),sQuery(id+"F0.wireOp",EDGE,"E10.1.12"),sQuery(id+"F0.wireOp",EDGE,"E10.1.14"),sQuery(id+"F0.wireOp",EDGE,"E10.1.15"),sQuery(id+"F0.wireOp",EDGE,"E10.1.16"),sQuery(id+"F0.wireOp",EDGE,"E10.1.18"),sQuery(id+"F0.wireOp",EDGE,"E10.1.20"),sQuery(id+"F0.wireOp",EDGE,"E10.2.0"),sQuery(id+"F0.wireOp",EDGE,"E10.2.1"),sQuery(id+"F0.wireOp",EDGE,"E10.2.2"),sQuery(id+"F0.wireOp",EDGE,"E10.2.3"),sQuery(id+"F0.wireOp",EDGE,"E10.2.5"),sQuery(id+"F0.wireOp",EDGE,"E10.2.7"),sQuery(id+"F0.wireOp",EDGE,"E10.2.8"),sQuery(id+"F0.wireOp",EDGE,"E10.2.9"),sQuery(id+"F0.wireOp",EDGE,"E10.2.10"),sQuery(id+"F0.wireOp",EDGE,"E10.2.11"),sQuery(id+"F0.wireOp",EDGE,"E10.2.12"),sQuery(id+"F0.wireOp",EDGE,"E1"),sQuery(id+"F0.wireOp",EDGE,"E10.2.14"),sQuery(id+"F0.wireOp",EDGE,"E10.2.15"),sQuery(id+"F0.wireOp",EDGE,"E10.2.16"),sQuery(id+"F0.wireOp",EDGE,"E10.2.18"),sQuery(id+"F0.wireOp",EDGE,"E10.2.20"),sQuery(id+"F0.wireOp",EDGE,"E8.trimOffspring"),sQuery(id+"F0.wireOp",EDGE,"E0"),sQuery(id+"F0.wireOp",EDGE,"E10.1.6"),sQuery(id+"F0.wireOp",EDGE,"E11"),sQuery(id+"F0.wireOp",EDGE,"E12"),sQuery(id+"F0.wireOp",EDGE,"E13.1.0"),sQuery(id+"F0.wireOp",EDGE,"E13.1.1"),sQuery(id+"F0.wireOp",EDGE,"E13.2.0"),sQuery(id+"F0.wireOp",EDGE,"E13.2.1")])]}),"instanceName":"1"}),"instanceName":"1"}),"instanceName":"1"}),"instanceName":"1"});
            var Q2;
            Q2=makeQuery(id+"F71.opPattern","COPY",BODY,{"derivedFrom":makeQuery(id+"F70.opPattern","COPY",BODY,{"derivedFrom":makeQuery(id+"F69.opPattern","COPY",BODY,{"derivedFrom":makeQuery(id+"F7.opPattern","COPY",BODY,{"derivedFrom":makeQuery(id+"F1.opExtrude","SWEPT_BODY",BODY,{"disambiguationData":[OSD([sQuery(id+"F0.wireOp",EDGE,"E2.0"),sQuery(id+"F0.wireOp",EDGE,"E2.1"),sQuery(id+"F0.wireOp",EDGE,"E2.2"),sQuery(id+"F0.wireOp",EDGE,"E2.3"),sQuery(id+"F0.wireOp",EDGE,"E2.4"),sQuery(id+"F0.wireOp",EDGE,"E2.5"),sQuery(id+"F0.wireOp",EDGE,"E3"),sQuery(id+"F0.wireOp",EDGE,"E4"),sQuery(id+"F0.wireOp",EDGE,"E5.0"),sQuery(id+"F0.wireOp",EDGE,"E5.1"),sQuery(id+"F0.wireOp",EDGE,"E5.3"),sQuery(id+"F0.wireOp",EDGE,"E5.4"),sQuery(id+"F0.wireOp",EDGE,"E5.5"),sQuery(id+"F0.wireOp",EDGE,"E6.trimOffspring"),sQuery(id+"F0.wireOp",EDGE,"E7.trimOffspring"),sQuery(id+"F0.wireOp",EDGE,"E9.trimOffspring"),sQuery(id+"F0.wireOp",EDGE,"E10.1.0"),sQuery(id+"F0.wireOp",EDGE,"E10.1.1"),sQuery(id+"F0.wireOp",EDGE,"E10.1.2"),sQuery(id+"F0.wireOp",EDGE,"E10.1.3"),sQuery(id+"F0.wireOp",EDGE,"E10.1.5"),sQuery(id+"F0.wireOp",EDGE,"E10.1.7"),sQuery(id+"F0.wireOp",EDGE,"E10.1.8"),sQuery(id+"F0.wireOp",EDGE,"E10.1.9"),sQuery(id+"F0.wireOp",EDGE,"E10.1.10"),sQuery(id+"F0.wireOp",EDGE,"E10.1.11"),sQuery(id+"F0.wireOp",EDGE,"E10.1.12"),sQuery(id+"F0.wireOp",EDGE,"E10.1.14"),sQuery(id+"F0.wireOp",EDGE,"E10.1.15"),sQuery(id+"F0.wireOp",EDGE,"E10.1.16"),sQuery(id+"F0.wireOp",EDGE,"E10.1.18"),sQuery(id+"F0.wireOp",EDGE,"E10.1.20"),sQuery(id+"F0.wireOp",EDGE,"E10.2.0"),sQuery(id+"F0.wireOp",EDGE,"E10.2.1"),sQuery(id+"F0.wireOp",EDGE,"E10.2.2"),sQuery(id+"F0.wireOp",EDGE,"E10.2.3"),sQuery(id+"F0.wireOp",EDGE,"E10.2.5"),sQuery(id+"F0.wireOp",EDGE,"E10.2.7"),sQuery(id+"F0.wireOp",EDGE,"E10.2.8"),sQuery(id+"F0.wireOp",EDGE,"E10.2.9"),sQuery(id+"F0.wireOp",EDGE,"E10.2.10"),sQuery(id+"F0.wireOp",EDGE,"E10.2.11"),sQuery(id+"F0.wireOp",EDGE,"E10.2.12"),sQuery(id+"F0.wireOp",EDGE,"E1"),sQuery(id+"F0.wireOp",EDGE,"E10.2.14"),sQuery(id+"F0.wireOp",EDGE,"E10.2.15"),sQuery(id+"F0.wireOp",EDGE,"E10.2.16"),sQuery(id+"F0.wireOp",EDGE,"E10.2.18"),sQuery(id+"F0.wireOp",EDGE,"E10.2.20"),sQuery(id+"F0.wireOp",EDGE,"E8.trimOffspring"),sQuery(id+"F0.wireOp",EDGE,"E0"),sQuery(id+"F0.wireOp",EDGE,"E10.1.6"),sQuery(id+"F0.wireOp",EDGE,"E11"),sQuery(id+"F0.wireOp",EDGE,"E12"),sQuery(id+"F0.wireOp",EDGE,"E13.1.0"),sQuery(id+"F0.wireOp",EDGE,"E13.1.1"),sQuery(id+"F0.wireOp",EDGE,"E13.2.0"),sQuery(id+"F0.wireOp",EDGE,"E13.2.1")])]}),"instanceName":"1"}),"instanceName":"1"}),"instanceName":"1"}),"instanceName":"1"});
            var Q3;
            Q3=makeQuery(id+"F71.opPattern","COPY",BODY,{"derivedFrom":makeQuery(id+"F70.opPattern","COPY",BODY,{"derivedFrom":makeQuery(id+"F69.opPattern","COPY",BODY,{"derivedFrom":makeQuery(id+"F8.opPattern","COPY",BODY,{"derivedFrom":makeQuery(id+"F7.opPattern","COPY",BODY,{"derivedFrom":makeQuery(id+"F1.opExtrude","SWEPT_BODY",BODY,{"disambiguationData":[OSD([sQuery(id+"F0.wireOp",EDGE,"E2.0"),sQuery(id+"F0.wireOp",EDGE,"E2.1"),sQuery(id+"F0.wireOp",EDGE,"E2.2"),sQuery(id+"F0.wireOp",EDGE,"E2.3"),sQuery(id+"F0.wireOp",EDGE,"E2.4"),sQuery(id+"F0.wireOp",EDGE,"E2.5"),sQuery(id+"F0.wireOp",EDGE,"E3"),sQuery(id+"F0.wireOp",EDGE,"E4"),sQuery(id+"F0.wireOp",EDGE,"E5.0"),sQuery(id+"F0.wireOp",EDGE,"E5.1"),sQuery(id+"F0.wireOp",EDGE,"E5.3"),sQuery(id+"F0.wireOp",EDGE,"E5.4"),sQuery(id+"F0.wireOp",EDGE,"E5.5"),sQuery(id+"F0.wireOp",EDGE,"E6.trimOffspring"),sQuery(id+"F0.wireOp",EDGE,"E7.trimOffspring"),sQuery(id+"F0.wireOp",EDGE,"E9.trimOffspring"),sQuery(id+"F0.wireOp",EDGE,"E10.1.0"),sQuery(id+"F0.wireOp",EDGE,"E10.1.1"),sQuery(id+"F0.wireOp",EDGE,"E10.1.2"),sQuery(id+"F0.wireOp",EDGE,"E10.1.3"),sQuery(id+"F0.wireOp",EDGE,"E10.1.5"),sQuery(id+"F0.wireOp",EDGE,"E10.1.7"),sQuery(id+"F0.wireOp",EDGE,"E10.1.8"),sQuery(id+"F0.wireOp",EDGE,"E10.1.9"),sQuery(id+"F0.wireOp",EDGE,"E10.1.10"),sQuery(id+"F0.wireOp",EDGE,"E10.1.11"),sQuery(id+"F0.wireOp",EDGE,"E10.1.12"),sQuery(id+"F0.wireOp",EDGE,"E10.1.14"),sQuery(id+"F0.wireOp",EDGE,"E10.1.15"),sQuery(id+"F0.wireOp",EDGE,"E10.1.16"),sQuery(id+"F0.wireOp",EDGE,"E10.1.18"),sQuery(id+"F0.wireOp",EDGE,"E10.1.20"),sQuery(id+"F0.wireOp",EDGE,"E10.2.0"),sQuery(id+"F0.wireOp",EDGE,"E10.2.1"),sQuery(id+"F0.wireOp",EDGE,"E10.2.2"),sQuery(id+"F0.wireOp",EDGE,"E10.2.3"),sQuery(id+"F0.wireOp",EDGE,"E10.2.5"),sQuery(id+"F0.wireOp",EDGE,"E10.2.7"),sQuery(id+"F0.wireOp",EDGE,"E10.2.8"),sQuery(id+"F0.wireOp",EDGE,"E10.2.9"),sQuery(id+"F0.wireOp",EDGE,"E10.2.10"),sQuery(id+"F0.wireOp",EDGE,"E10.2.11"),sQuery(id+"F0.wireOp",EDGE,"E10.2.12"),sQuery(id+"F0.wireOp",EDGE,"E1"),sQuery(id+"F0.wireOp",EDGE,"E10.2.14"),sQuery(id+"F0.wireOp",EDGE,"E10.2.15"),sQuery(id+"F0.wireOp",EDGE,"E10.2.16"),sQuery(id+"F0.wireOp",EDGE,"E10.2.18"),sQuery(id+"F0.wireOp",EDGE,"E10.2.20"),sQuery(id+"F0.wireOp",EDGE,"E8.trimOffspring"),sQuery(id+"F0.wireOp",EDGE,"E0"),sQuery(id+"F0.wireOp",EDGE,"E10.1.6"),sQuery(id+"F0.wireOp",EDGE,"E11"),sQuery(id+"F0.wireOp",EDGE,"E12"),sQuery(id+"F0.wireOp",EDGE,"E13.1.0"),sQuery(id+"F0.wireOp",EDGE,"E13.1.1"),sQuery(id+"F0.wireOp",EDGE,"E13.2.0"),sQuery(id+"F0.wireOp",EDGE,"E13.2.1")])]}),"instanceName":"1"}),"instanceName":"1"}),"instanceName":"1"}),"instanceName":"1"}),"instanceName":"1"});
            var Q4;
            Q4=makeQuery(id+"F71.opPattern","COPY",BODY,{"derivedFrom":makeQuery(id+"F70.opPattern","COPY",BODY,{"derivedFrom":makeQuery(id+"F69.opPattern","COPY",BODY,{"derivedFrom":makeQuery(id+"F9.opPattern","COPY",BODY,{"derivedFrom":makeQuery(id+"F8.opPattern","COPY",BODY,{"derivedFrom":makeQuery(id+"F7.opPattern","COPY",BODY,{"derivedFrom":makeQuery(id+"F1.opExtrude","SWEPT_BODY",BODY,{"disambiguationData":[OSD([sQuery(id+"F0.wireOp",EDGE,"E2.0"),sQuery(id+"F0.wireOp",EDGE,"E2.1"),sQuery(id+"F0.wireOp",EDGE,"E2.2"),sQuery(id+"F0.wireOp",EDGE,"E2.3"),sQuery(id+"F0.wireOp",EDGE,"E2.4"),sQuery(id+"F0.wireOp",EDGE,"E2.5"),sQuery(id+"F0.wireOp",EDGE,"E3"),sQuery(id+"F0.wireOp",EDGE,"E4"),sQuery(id+"F0.wireOp",EDGE,"E5.0"),sQuery(id+"F0.wireOp",EDGE,"E5.1"),sQuery(id+"F0.wireOp",EDGE,"E5.3"),sQuery(id+"F0.wireOp",EDGE,"E5.4"),sQuery(id+"F0.wireOp",EDGE,"E5.5"),sQuery(id+"F0.wireOp",EDGE,"E6.trimOffspring"),sQuery(id+"F0.wireOp",EDGE,"E7.trimOffspring"),sQuery(id+"F0.wireOp",EDGE,"E9.trimOffspring"),sQuery(id+"F0.wireOp",EDGE,"E10.1.0"),sQuery(id+"F0.wireOp",EDGE,"E10.1.1"),sQuery(id+"F0.wireOp",EDGE,"E10.1.2"),sQuery(id+"F0.wireOp",EDGE,"E10.1.3"),sQuery(id+"F0.wireOp",EDGE,"E10.1.5"),sQuery(id+"F0.wireOp",EDGE,"E10.1.7"),sQuery(id+"F0.wireOp",EDGE,"E10.1.8"),sQuery(id+"F0.wireOp",EDGE,"E10.1.9"),sQuery(id+"F0.wireOp",EDGE,"E10.1.10"),sQuery(id+"F0.wireOp",EDGE,"E10.1.11"),sQuery(id+"F0.wireOp",EDGE,"E10.1.12"),sQuery(id+"F0.wireOp",EDGE,"E10.1.14"),sQuery(id+"F0.wireOp",EDGE,"E10.1.15"),sQuery(id+"F0.wireOp",EDGE,"E10.1.16"),sQuery(id+"F0.wireOp",EDGE,"E10.1.18"),sQuery(id+"F0.wireOp",EDGE,"E10.1.20"),sQuery(id+"F0.wireOp",EDGE,"E10.2.0"),sQuery(id+"F0.wireOp",EDGE,"E10.2.1"),sQuery(id+"F0.wireOp",EDGE,"E10.2.2"),sQuery(id+"F0.wireOp",EDGE,"E10.2.3"),sQuery(id+"F0.wireOp",EDGE,"E10.2.5"),sQuery(id+"F0.wireOp",EDGE,"E10.2.7"),sQuery(id+"F0.wireOp",EDGE,"E10.2.8"),sQuery(id+"F0.wireOp",EDGE,"E10.2.9"),sQuery(id+"F0.wireOp",EDGE,"E10.2.10"),sQuery(id+"F0.wireOp",EDGE,"E10.2.11"),sQuery(id+"F0.wireOp",EDGE,"E10.2.12"),sQuery(id+"F0.wireOp",EDGE,"E1"),sQuery(id+"F0.wireOp",EDGE,"E10.2.14"),sQuery(id+"F0.wireOp",EDGE,"E10.2.15"),sQuery(id+"F0.wireOp",EDGE,"E10.2.16"),sQuery(id+"F0.wireOp",EDGE,"E10.2.18"),sQuery(id+"F0.wireOp",EDGE,"E10.2.20"),sQuery(id+"F0.wireOp",EDGE,"E8.trimOffspring"),sQuery(id+"F0.wireOp",EDGE,"E0"),sQuery(id+"F0.wireOp",EDGE,"E10.1.6"),sQuery(id+"F0.wireOp",EDGE,"E11"),sQuery(id+"F0.wireOp",EDGE,"E12"),sQuery(id+"F0.wireOp",EDGE,"E13.1.0"),sQuery(id+"F0.wireOp",EDGE,"E13.1.1"),sQuery(id+"F0.wireOp",EDGE,"E13.2.0"),sQuery(id+"F0.wireOp",EDGE,"E13.2.1")])]}),"instanceName":"1"}),"instanceName":"1"}),"instanceName":"1"}),"instanceName":"1"}),"instanceName":"1"}),"instanceName":"1"});
            var Q5;
            Q5=makeQuery(id+"F71.opPattern","COPY",BODY,{"derivedFrom":makeQuery(id+"F70.opPattern","COPY",BODY,{"derivedFrom":makeQuery(id+"F69.opPattern","COPY",BODY,{"derivedFrom":makeQuery(id+"F10.opPattern","COPY",BODY,{"derivedFrom":makeQuery(id+"F9.opPattern","COPY",BODY,{"derivedFrom":makeQuery(id+"F8.opPattern","COPY",BODY,{"derivedFrom":makeQuery(id+"F7.opPattern","COPY",BODY,{"derivedFrom":makeQuery(id+"F1.opExtrude","SWEPT_BODY",BODY,{"disambiguationData":[OSD([sQuery(id+"F0.wireOp",EDGE,"E2.0"),sQuery(id+"F0.wireOp",EDGE,"E2.1"),sQuery(id+"F0.wireOp",EDGE,"E2.2"),sQuery(id+"F0.wireOp",EDGE,"E2.3"),sQuery(id+"F0.wireOp",EDGE,"E2.4"),sQuery(id+"F0.wireOp",EDGE,"E2.5"),sQuery(id+"F0.wireOp",EDGE,"E3"),sQuery(id+"F0.wireOp",EDGE,"E4"),sQuery(id+"F0.wireOp",EDGE,"E5.0"),sQuery(id+"F0.wireOp",EDGE,"E5.1"),sQuery(id+"F0.wireOp",EDGE,"E5.3"),sQuery(id+"F0.wireOp",EDGE,"E5.4"),sQuery(id+"F0.wireOp",EDGE,"E5.5"),sQuery(id+"F0.wireOp",EDGE,"E6.trimOffspring"),sQuery(id+"F0.wireOp",EDGE,"E7.trimOffspring"),sQuery(id+"F0.wireOp",EDGE,"E9.trimOffspring"),sQuery(id+"F0.wireOp",EDGE,"E10.1.0"),sQuery(id+"F0.wireOp",EDGE,"E10.1.1"),sQuery(id+"F0.wireOp",EDGE,"E10.1.2"),sQuery(id+"F0.wireOp",EDGE,"E10.1.3"),sQuery(id+"F0.wireOp",EDGE,"E10.1.5"),sQuery(id+"F0.wireOp",EDGE,"E10.1.7"),sQuery(id+"F0.wireOp",EDGE,"E10.1.8"),sQuery(id+"F0.wireOp",EDGE,"E10.1.9"),sQuery(id+"F0.wireOp",EDGE,"E10.1.10"),sQuery(id+"F0.wireOp",EDGE,"E10.1.11"),sQuery(id+"F0.wireOp",EDGE,"E10.1.12"),sQuery(id+"F0.wireOp",EDGE,"E10.1.14"),sQuery(id+"F0.wireOp",EDGE,"E10.1.15"),sQuery(id+"F0.wireOp",EDGE,"E10.1.16"),sQuery(id+"F0.wireOp",EDGE,"E10.1.18"),sQuery(id+"F0.wireOp",EDGE,"E10.1.20"),sQuery(id+"F0.wireOp",EDGE,"E10.2.0"),sQuery(id+"F0.wireOp",EDGE,"E10.2.1"),sQuery(id+"F0.wireOp",EDGE,"E10.2.2"),sQuery(id+"F0.wireOp",EDGE,"E10.2.3"),sQuery(id+"F0.wireOp",EDGE,"E10.2.5"),sQuery(id+"F0.wireOp",EDGE,"E10.2.7"),sQuery(id+"F0.wireOp",EDGE,"E10.2.8"),sQuery(id+"F0.wireOp",EDGE,"E10.2.9"),sQuery(id+"F0.wireOp",EDGE,"E10.2.10"),sQuery(id+"F0.wireOp",EDGE,"E10.2.11"),sQuery(id+"F0.wireOp",EDGE,"E10.2.12"),sQuery(id+"F0.wireOp",EDGE,"E1"),sQuery(id+"F0.wireOp",EDGE,"E10.2.14"),sQuery(id+"F0.wireOp",EDGE,"E10.2.15"),sQuery(id+"F0.wireOp",EDGE,"E10.2.16"),sQuery(id+"F0.wireOp",EDGE,"E10.2.18"),sQuery(id+"F0.wireOp",EDGE,"E10.2.20"),sQuery(id+"F0.wireOp",EDGE,"E8.trimOffspring"),sQuery(id+"F0.wireOp",EDGE,"E0"),sQuery(id+"F0.wireOp",EDGE,"E10.1.6"),sQuery(id+"F0.wireOp",EDGE,"E11"),sQuery(id+"F0.wireOp",EDGE,"E12"),sQuery(id+"F0.wireOp",EDGE,"E13.1.0"),sQuery(id+"F0.wireOp",EDGE,"E13.1.1"),sQuery(id+"F0.wireOp",EDGE,"E13.2.0"),sQuery(id+"F0.wireOp",EDGE,"E13.2.1")])]}),"instanceName":"1"}),"instanceName":"1"}),"instanceName":"1"}),"instanceName":"1"}),"instanceName":"1"}),"instanceName":"1"}),"instanceName":"1"});
            transform(context, id + "F72", {"entities" : qUnion([Q0, Q1, Q2, Q3, Q4, Q5]), "transformType" : TransformType.TRANSLATION_3D, "dx" : 0 * mm, "dy" : -68.8 * mm, "dz" : 0 * mm, "makeCopy" : true});
        }
        {
            var Q0;
            Q0=makeQuery(id+"F72.opPattern","COPY",BODY,{"derivedFrom":makeQuery(id+"F71.opPattern","COPY",BODY,{"derivedFrom":makeQuery(id+"F70.opPattern","COPY",BODY,{"derivedFrom":makeQuery(id+"F69.opPattern","COPY",BODY,{"derivedFrom":makeQuery(id+"F1.opExtrude","SWEPT_BODY",BODY,{"disambiguationData":[OSD([sQuery(id+"F0.wireOp",EDGE,"E2.0"),sQuery(id+"F0.wireOp",EDGE,"E2.1"),sQuery(id+"F0.wireOp",EDGE,"E2.2"),sQuery(id+"F0.wireOp",EDGE,"E2.3"),sQuery(id+"F0.wireOp",EDGE,"E2.4"),sQuery(id+"F0.wireOp",EDGE,"E2.5"),sQuery(id+"F0.wireOp",EDGE,"E3"),sQuery(id+"F0.wireOp",EDGE,"E4"),sQuery(id+"F0.wireOp",EDGE,"E5.0"),sQuery(id+"F0.wireOp",EDGE,"E5.1"),sQuery(id+"F0.wireOp",EDGE,"E5.3"),sQuery(id+"F0.wireOp",EDGE,"E5.4"),sQuery(id+"F0.wireOp",EDGE,"E5.5"),sQuery(id+"F0.wireOp",EDGE,"E6.trimOffspring"),sQuery(id+"F0.wireOp",EDGE,"E7.trimOffspring"),sQuery(id+"F0.wireOp",EDGE,"E9.trimOffspring"),sQuery(id+"F0.wireOp",EDGE,"E10.1.0"),sQuery(id+"F0.wireOp",EDGE,"E10.1.1"),sQuery(id+"F0.wireOp",EDGE,"E10.1.2"),sQuery(id+"F0.wireOp",EDGE,"E10.1.3"),sQuery(id+"F0.wireOp",EDGE,"E10.1.5"),sQuery(id+"F0.wireOp",EDGE,"E10.1.7"),sQuery(id+"F0.wireOp",EDGE,"E10.1.8"),sQuery(id+"F0.wireOp",EDGE,"E10.1.9"),sQuery(id+"F0.wireOp",EDGE,"E10.1.10"),sQuery(id+"F0.wireOp",EDGE,"E10.1.11"),sQuery(id+"F0.wireOp",EDGE,"E10.1.12"),sQuery(id+"F0.wireOp",EDGE,"E10.1.14"),sQuery(id+"F0.wireOp",EDGE,"E10.1.15"),sQuery(id+"F0.wireOp",EDGE,"E10.1.16"),sQuery(id+"F0.wireOp",EDGE,"E10.1.18"),sQuery(id+"F0.wireOp",EDGE,"E10.1.20"),sQuery(id+"F0.wireOp",EDGE,"E10.2.0"),sQuery(id+"F0.wireOp",EDGE,"E10.2.1"),sQuery(id+"F0.wireOp",EDGE,"E10.2.2"),sQuery(id+"F0.wireOp",EDGE,"E10.2.3"),sQuery(id+"F0.wireOp",EDGE,"E10.2.5"),sQuery(id+"F0.wireOp",EDGE,"E10.2.7"),sQuery(id+"F0.wireOp",EDGE,"E10.2.8"),sQuery(id+"F0.wireOp",EDGE,"E10.2.9"),sQuery(id+"F0.wireOp",EDGE,"E10.2.10"),sQuery(id+"F0.wireOp",EDGE,"E10.2.11"),sQuery(id+"F0.wireOp",EDGE,"E10.2.12"),sQuery(id+"F0.wireOp",EDGE,"E1"),sQuery(id+"F0.wireOp",EDGE,"E10.2.14"),sQuery(id+"F0.wireOp",EDGE,"E10.2.15"),sQuery(id+"F0.wireOp",EDGE,"E10.2.16"),sQuery(id+"F0.wireOp",EDGE,"E10.2.18"),sQuery(id+"F0.wireOp",EDGE,"E10.2.20"),sQuery(id+"F0.wireOp",EDGE,"E8.trimOffspring"),sQuery(id+"F0.wireOp",EDGE,"E0"),sQuery(id+"F0.wireOp",EDGE,"E10.1.6"),sQuery(id+"F0.wireOp",EDGE,"E11"),sQuery(id+"F0.wireOp",EDGE,"E12"),sQuery(id+"F0.wireOp",EDGE,"E13.1.0"),sQuery(id+"F0.wireOp",EDGE,"E13.1.1"),sQuery(id+"F0.wireOp",EDGE,"E13.2.0"),sQuery(id+"F0.wireOp",EDGE,"E13.2.1")])]}),"instanceName":"1"}),"instanceName":"1"}),"instanceName":"1"}),"instanceName":"1"});
            transform(context, id + "F73", {"entities" : qUnion([Q0]), "transformType" : TransformType.TRANSLATION_3D, "dx" : 36 * mm, "dy" : -51 * mm, "dz" : 0 * mm, "makeCopy" : true});
        }
        {
            var Q0;
            Q0=makeQuery(id+"F73.opPattern","COPY",BODY,{"derivedFrom":makeQuery(id+"F72.opPattern","COPY",BODY,{"derivedFrom":makeQuery(id+"F71.opPattern","COPY",BODY,{"derivedFrom":makeQuery(id+"F70.opPattern","COPY",BODY,{"derivedFrom":makeQuery(id+"F69.opPattern","COPY",BODY,{"derivedFrom":makeQuery(id+"F1.opExtrude","SWEPT_BODY",BODY,{"disambiguationData":[OSD([sQuery(id+"F0.wireOp",EDGE,"E2.0"),sQuery(id+"F0.wireOp",EDGE,"E2.1"),sQuery(id+"F0.wireOp",EDGE,"E2.2"),sQuery(id+"F0.wireOp",EDGE,"E2.3"),sQuery(id+"F0.wireOp",EDGE,"E2.4"),sQuery(id+"F0.wireOp",EDGE,"E2.5"),sQuery(id+"F0.wireOp",EDGE,"E3"),sQuery(id+"F0.wireOp",EDGE,"E4"),sQuery(id+"F0.wireOp",EDGE,"E5.0"),sQuery(id+"F0.wireOp",EDGE,"E5.1"),sQuery(id+"F0.wireOp",EDGE,"E5.3"),sQuery(id+"F0.wireOp",EDGE,"E5.4"),sQuery(id+"F0.wireOp",EDGE,"E5.5"),sQuery(id+"F0.wireOp",EDGE,"E6.trimOffspring"),sQuery(id+"F0.wireOp",EDGE,"E7.trimOffspring"),sQuery(id+"F0.wireOp",EDGE,"E9.trimOffspring"),sQuery(id+"F0.wireOp",EDGE,"E10.1.0"),sQuery(id+"F0.wireOp",EDGE,"E10.1.1"),sQuery(id+"F0.wireOp",EDGE,"E10.1.2"),sQuery(id+"F0.wireOp",EDGE,"E10.1.3"),sQuery(id+"F0.wireOp",EDGE,"E10.1.5"),sQuery(id+"F0.wireOp",EDGE,"E10.1.7"),sQuery(id+"F0.wireOp",EDGE,"E10.1.8"),sQuery(id+"F0.wireOp",EDGE,"E10.1.9"),sQuery(id+"F0.wireOp",EDGE,"E10.1.10"),sQuery(id+"F0.wireOp",EDGE,"E10.1.11"),sQuery(id+"F0.wireOp",EDGE,"E10.1.12"),sQuery(id+"F0.wireOp",EDGE,"E10.1.14"),sQuery(id+"F0.wireOp",EDGE,"E10.1.15"),sQuery(id+"F0.wireOp",EDGE,"E10.1.16"),sQuery(id+"F0.wireOp",EDGE,"E10.1.18"),sQuery(id+"F0.wireOp",EDGE,"E10.1.20"),sQuery(id+"F0.wireOp",EDGE,"E10.2.0"),sQuery(id+"F0.wireOp",EDGE,"E10.2.1"),sQuery(id+"F0.wireOp",EDGE,"E10.2.2"),sQuery(id+"F0.wireOp",EDGE,"E10.2.3"),sQuery(id+"F0.wireOp",EDGE,"E10.2.5"),sQuery(id+"F0.wireOp",EDGE,"E10.2.7"),sQuery(id+"F0.wireOp",EDGE,"E10.2.8"),sQuery(id+"F0.wireOp",EDGE,"E10.2.9"),sQuery(id+"F0.wireOp",EDGE,"E10.2.10"),sQuery(id+"F0.wireOp",EDGE,"E10.2.11"),sQuery(id+"F0.wireOp",EDGE,"E10.2.12"),sQuery(id+"F0.wireOp",EDGE,"E1"),sQuery(id+"F0.wireOp",EDGE,"E10.2.14"),sQuery(id+"F0.wireOp",EDGE,"E10.2.15"),sQuery(id+"F0.wireOp",EDGE,"E10.2.16"),sQuery(id+"F0.wireOp",EDGE,"E10.2.18"),sQuery(id+"F0.wireOp",EDGE,"E10.2.20"),sQuery(id+"F0.wireOp",EDGE,"E8.trimOffspring"),sQuery(id+"F0.wireOp",EDGE,"E0"),sQuery(id+"F0.wireOp",EDGE,"E10.1.6"),sQuery(id+"F0.wireOp",EDGE,"E11"),sQuery(id+"F0.wireOp",EDGE,"E12"),sQuery(id+"F0.wireOp",EDGE,"E13.1.0"),sQuery(id+"F0.wireOp",EDGE,"E13.1.1"),sQuery(id+"F0.wireOp",EDGE,"E13.2.0"),sQuery(id+"F0.wireOp",EDGE,"E13.2.1")])]}),"instanceName":"1"}),"instanceName":"1"}),"instanceName":"1"}),"instanceName":"1"}),"instanceName":"1"});
            var Q1;
            Q1=makeQuery(id+"F73.opPattern","COPY",EDGE,{"derivedFrom":makeQuery(id+"F72.opPattern","COPY",EDGE,{"derivedFrom":makeQuery(id+"F71.opPattern","COPY",EDGE,{"derivedFrom":makeQuery(id+"F70.opPattern","COPY",EDGE,{"derivedFrom":makeQuery(id+"F69.opPattern","COPY",EDGE,{"derivedFrom":makeQuery(id+"F1.opExtrude","CAP_EDGE",EDGE,{"disambiguationData":[OSD([sQuery(id+"F0.wireOp",EDGE,"E1")])],"isStart":false}),"instanceName":"1"}),"instanceName":"1"}),"instanceName":"1"}),"instanceName":"1"}),"instanceName":"1"});
            transform(context, id + "F74", {"entities" : qUnion([Q0]), "transformType" : TransformType.ROTATION, "transformAxis" : qUnion([Q1]), "angle" : 55 * degree, "oppositeDirection" : true, "makeCopy" : false});
        }
        {
            var Q0;
            Q0=makeQuery(id+"F73.opPattern","COPY",BODY,{"derivedFrom":makeQuery(id+"F72.opPattern","COPY",BODY,{"derivedFrom":makeQuery(id+"F71.opPattern","COPY",BODY,{"derivedFrom":makeQuery(id+"F70.opPattern","COPY",BODY,{"derivedFrom":makeQuery(id+"F69.opPattern","COPY",BODY,{"derivedFrom":makeQuery(id+"F1.opExtrude","SWEPT_BODY",BODY,{"disambiguationData":[OSD([sQuery(id+"F0.wireOp",EDGE,"E2.0"),sQuery(id+"F0.wireOp",EDGE,"E2.1"),sQuery(id+"F0.wireOp",EDGE,"E2.2"),sQuery(id+"F0.wireOp",EDGE,"E2.3"),sQuery(id+"F0.wireOp",EDGE,"E2.4"),sQuery(id+"F0.wireOp",EDGE,"E2.5"),sQuery(id+"F0.wireOp",EDGE,"E3"),sQuery(id+"F0.wireOp",EDGE,"E4"),sQuery(id+"F0.wireOp",EDGE,"E5.0"),sQuery(id+"F0.wireOp",EDGE,"E5.1"),sQuery(id+"F0.wireOp",EDGE,"E5.3"),sQuery(id+"F0.wireOp",EDGE,"E5.4"),sQuery(id+"F0.wireOp",EDGE,"E5.5"),sQuery(id+"F0.wireOp",EDGE,"E6.trimOffspring"),sQuery(id+"F0.wireOp",EDGE,"E7.trimOffspring"),sQuery(id+"F0.wireOp",EDGE,"E9.trimOffspring"),sQuery(id+"F0.wireOp",EDGE,"E10.1.0"),sQuery(id+"F0.wireOp",EDGE,"E10.1.1"),sQuery(id+"F0.wireOp",EDGE,"E10.1.2"),sQuery(id+"F0.wireOp",EDGE,"E10.1.3"),sQuery(id+"F0.wireOp",EDGE,"E10.1.5"),sQuery(id+"F0.wireOp",EDGE,"E10.1.7"),sQuery(id+"F0.wireOp",EDGE,"E10.1.8"),sQuery(id+"F0.wireOp",EDGE,"E10.1.9"),sQuery(id+"F0.wireOp",EDGE,"E10.1.10"),sQuery(id+"F0.wireOp",EDGE,"E10.1.11"),sQuery(id+"F0.wireOp",EDGE,"E10.1.12"),sQuery(id+"F0.wireOp",EDGE,"E10.1.14"),sQuery(id+"F0.wireOp",EDGE,"E10.1.15"),sQuery(id+"F0.wireOp",EDGE,"E10.1.16"),sQuery(id+"F0.wireOp",EDGE,"E10.1.18"),sQuery(id+"F0.wireOp",EDGE,"E10.1.20"),sQuery(id+"F0.wireOp",EDGE,"E10.2.0"),sQuery(id+"F0.wireOp",EDGE,"E10.2.1"),sQuery(id+"F0.wireOp",EDGE,"E10.2.2"),sQuery(id+"F0.wireOp",EDGE,"E10.2.3"),sQuery(id+"F0.wireOp",EDGE,"E10.2.5"),sQuery(id+"F0.wireOp",EDGE,"E10.2.7"),sQuery(id+"F0.wireOp",EDGE,"E10.2.8"),sQuery(id+"F0.wireOp",EDGE,"E10.2.9"),sQuery(id+"F0.wireOp",EDGE,"E10.2.10"),sQuery(id+"F0.wireOp",EDGE,"E10.2.11"),sQuery(id+"F0.wireOp",EDGE,"E10.2.12"),sQuery(id+"F0.wireOp",EDGE,"E1"),sQuery(id+"F0.wireOp",EDGE,"E10.2.14"),sQuery(id+"F0.wireOp",EDGE,"E10.2.15"),sQuery(id+"F0.wireOp",EDGE,"E10.2.16"),sQuery(id+"F0.wireOp",EDGE,"E10.2.18"),sQuery(id+"F0.wireOp",EDGE,"E10.2.20"),sQuery(id+"F0.wireOp",EDGE,"E8.trimOffspring"),sQuery(id+"F0.wireOp",EDGE,"E0"),sQuery(id+"F0.wireOp",EDGE,"E10.1.6"),sQuery(id+"F0.wireOp",EDGE,"E11"),sQuery(id+"F0.wireOp",EDGE,"E12"),sQuery(id+"F0.wireOp",EDGE,"E13.1.0"),sQuery(id+"F0.wireOp",EDGE,"E13.1.1"),sQuery(id+"F0.wireOp",EDGE,"E13.2.0"),sQuery(id+"F0.wireOp",EDGE,"E13.2.1")])]}),"instanceName":"1"}),"instanceName":"1"}),"instanceName":"1"}),"instanceName":"1"}),"instanceName":"1"});
            transform(context, id + "F75", {"entities" : qUnion([Q0]), "transformType" : TransformType.TRANSLATION_3D, "dx" : -7 * mm, "dy" : -7.7 * mm, "dz" : 0 * mm, "makeCopy" : false});
        }
        {
            var Q0;
            Q0=makeQuery(id+"F73.opPattern","COPY",BODY,{"derivedFrom":makeQuery(id+"F72.opPattern","COPY",BODY,{"derivedFrom":makeQuery(id+"F71.opPattern","COPY",BODY,{"derivedFrom":makeQuery(id+"F70.opPattern","COPY",BODY,{"derivedFrom":makeQuery(id+"F69.opPattern","COPY",BODY,{"derivedFrom":makeQuery(id+"F1.opExtrude","SWEPT_BODY",BODY,{"disambiguationData":[OSD([sQuery(id+"F0.wireOp",EDGE,"E2.0"),sQuery(id+"F0.wireOp",EDGE,"E2.1"),sQuery(id+"F0.wireOp",EDGE,"E2.2"),sQuery(id+"F0.wireOp",EDGE,"E2.3"),sQuery(id+"F0.wireOp",EDGE,"E2.4"),sQuery(id+"F0.wireOp",EDGE,"E2.5"),sQuery(id+"F0.wireOp",EDGE,"E3"),sQuery(id+"F0.wireOp",EDGE,"E4"),sQuery(id+"F0.wireOp",EDGE,"E5.0"),sQuery(id+"F0.wireOp",EDGE,"E5.1"),sQuery(id+"F0.wireOp",EDGE,"E5.3"),sQuery(id+"F0.wireOp",EDGE,"E5.4"),sQuery(id+"F0.wireOp",EDGE,"E5.5"),sQuery(id+"F0.wireOp",EDGE,"E6.trimOffspring"),sQuery(id+"F0.wireOp",EDGE,"E7.trimOffspring"),sQuery(id+"F0.wireOp",EDGE,"E9.trimOffspring"),sQuery(id+"F0.wireOp",EDGE,"E10.1.0"),sQuery(id+"F0.wireOp",EDGE,"E10.1.1"),sQuery(id+"F0.wireOp",EDGE,"E10.1.2"),sQuery(id+"F0.wireOp",EDGE,"E10.1.3"),sQuery(id+"F0.wireOp",EDGE,"E10.1.5"),sQuery(id+"F0.wireOp",EDGE,"E10.1.7"),sQuery(id+"F0.wireOp",EDGE,"E10.1.8"),sQuery(id+"F0.wireOp",EDGE,"E10.1.9"),sQuery(id+"F0.wireOp",EDGE,"E10.1.10"),sQuery(id+"F0.wireOp",EDGE,"E10.1.11"),sQuery(id+"F0.wireOp",EDGE,"E10.1.12"),sQuery(id+"F0.wireOp",EDGE,"E10.1.14"),sQuery(id+"F0.wireOp",EDGE,"E10.1.15"),sQuery(id+"F0.wireOp",EDGE,"E10.1.16"),sQuery(id+"F0.wireOp",EDGE,"E10.1.18"),sQuery(id+"F0.wireOp",EDGE,"E10.1.20"),sQuery(id+"F0.wireOp",EDGE,"E10.2.0"),sQuery(id+"F0.wireOp",EDGE,"E10.2.1"),sQuery(id+"F0.wireOp",EDGE,"E10.2.2"),sQuery(id+"F0.wireOp",EDGE,"E10.2.3"),sQuery(id+"F0.wireOp",EDGE,"E10.2.5"),sQuery(id+"F0.wireOp",EDGE,"E10.2.7"),sQuery(id+"F0.wireOp",EDGE,"E10.2.8"),sQuery(id+"F0.wireOp",EDGE,"E10.2.9"),sQuery(id+"F0.wireOp",EDGE,"E10.2.10"),sQuery(id+"F0.wireOp",EDGE,"E10.2.11"),sQuery(id+"F0.wireOp",EDGE,"E10.2.12"),sQuery(id+"F0.wireOp",EDGE,"E1"),sQuery(id+"F0.wireOp",EDGE,"E10.2.14"),sQuery(id+"F0.wireOp",EDGE,"E10.2.15"),sQuery(id+"F0.wireOp",EDGE,"E10.2.16"),sQuery(id+"F0.wireOp",EDGE,"E10.2.18"),sQuery(id+"F0.wireOp",EDGE,"E10.2.20"),sQuery(id+"F0.wireOp",EDGE,"E8.trimOffspring"),sQuery(id+"F0.wireOp",EDGE,"E0"),sQuery(id+"F0.wireOp",EDGE,"E10.1.6"),sQuery(id+"F0.wireOp",EDGE,"E11"),sQuery(id+"F0.wireOp",EDGE,"E12"),sQuery(id+"F0.wireOp",EDGE,"E13.1.0"),sQuery(id+"F0.wireOp",EDGE,"E13.1.1"),sQuery(id+"F0.wireOp",EDGE,"E13.2.0"),sQuery(id+"F0.wireOp",EDGE,"E13.2.1")])]}),"instanceName":"1"}),"instanceName":"1"}),"instanceName":"1"}),"instanceName":"1"}),"instanceName":"1"});
            transform(context, id + "F76", {"entities" : qUnion([Q0]), "transformType" : TransformType.TRANSLATION_3D, "dx" : 70 * mm, "dy" : 0 * mm, "dz" : 0 * mm, "makeCopy" : true});
        }
        {
            var Q0;
            Q0=makeQuery(id+"F76.opPattern","COPY",BODY,{"derivedFrom":makeQuery(id+"F73.opPattern","COPY",BODY,{"derivedFrom":makeQuery(id+"F72.opPattern","COPY",BODY,{"derivedFrom":makeQuery(id+"F71.opPattern","COPY",BODY,{"derivedFrom":makeQuery(id+"F70.opPattern","COPY",BODY,{"derivedFrom":makeQuery(id+"F69.opPattern","COPY",BODY,{"derivedFrom":makeQuery(id+"F1.opExtrude","SWEPT_BODY",BODY,{"disambiguationData":[OSD([sQuery(id+"F0.wireOp",EDGE,"E2.0"),sQuery(id+"F0.wireOp",EDGE,"E2.1"),sQuery(id+"F0.wireOp",EDGE,"E2.2"),sQuery(id+"F0.wireOp",EDGE,"E2.3"),sQuery(id+"F0.wireOp",EDGE,"E2.4"),sQuery(id+"F0.wireOp",EDGE,"E2.5"),sQuery(id+"F0.wireOp",EDGE,"E3"),sQuery(id+"F0.wireOp",EDGE,"E4"),sQuery(id+"F0.wireOp",EDGE,"E5.0"),sQuery(id+"F0.wireOp",EDGE,"E5.1"),sQuery(id+"F0.wireOp",EDGE,"E5.3"),sQuery(id+"F0.wireOp",EDGE,"E5.4"),sQuery(id+"F0.wireOp",EDGE,"E5.5"),sQuery(id+"F0.wireOp",EDGE,"E6.trimOffspring"),sQuery(id+"F0.wireOp",EDGE,"E7.trimOffspring"),sQuery(id+"F0.wireOp",EDGE,"E9.trimOffspring"),sQuery(id+"F0.wireOp",EDGE,"E10.1.0"),sQuery(id+"F0.wireOp",EDGE,"E10.1.1"),sQuery(id+"F0.wireOp",EDGE,"E10.1.2"),sQuery(id+"F0.wireOp",EDGE,"E10.1.3"),sQuery(id+"F0.wireOp",EDGE,"E10.1.5"),sQuery(id+"F0.wireOp",EDGE,"E10.1.7"),sQuery(id+"F0.wireOp",EDGE,"E10.1.8"),sQuery(id+"F0.wireOp",EDGE,"E10.1.9"),sQuery(id+"F0.wireOp",EDGE,"E10.1.10"),sQuery(id+"F0.wireOp",EDGE,"E10.1.11"),sQuery(id+"F0.wireOp",EDGE,"E10.1.12"),sQuery(id+"F0.wireOp",EDGE,"E10.1.14"),sQuery(id+"F0.wireOp",EDGE,"E10.1.15"),sQuery(id+"F0.wireOp",EDGE,"E10.1.16"),sQuery(id+"F0.wireOp",EDGE,"E10.1.18"),sQuery(id+"F0.wireOp",EDGE,"E10.1.20"),sQuery(id+"F0.wireOp",EDGE,"E10.2.0"),sQuery(id+"F0.wireOp",EDGE,"E10.2.1"),sQuery(id+"F0.wireOp",EDGE,"E10.2.2"),sQuery(id+"F0.wireOp",EDGE,"E10.2.3"),sQuery(id+"F0.wireOp",EDGE,"E10.2.5"),sQuery(id+"F0.wireOp",EDGE,"E10.2.7"),sQuery(id+"F0.wireOp",EDGE,"E10.2.8"),sQuery(id+"F0.wireOp",EDGE,"E10.2.9"),sQuery(id+"F0.wireOp",EDGE,"E10.2.10"),sQuery(id+"F0.wireOp",EDGE,"E10.2.11"),sQuery(id+"F0.wireOp",EDGE,"E10.2.12"),sQuery(id+"F0.wireOp",EDGE,"E1"),sQuery(id+"F0.wireOp",EDGE,"E10.2.14"),sQuery(id+"F0.wireOp",EDGE,"E10.2.15"),sQuery(id+"F0.wireOp",EDGE,"E10.2.16"),sQuery(id+"F0.wireOp",EDGE,"E10.2.18"),sQuery(id+"F0.wireOp",EDGE,"E10.2.20"),sQuery(id+"F0.wireOp",EDGE,"E8.trimOffspring"),sQuery(id+"F0.wireOp",EDGE,"E0"),sQuery(id+"F0.wireOp",EDGE,"E10.1.6"),sQuery(id+"F0.wireOp",EDGE,"E11"),sQuery(id+"F0.wireOp",EDGE,"E12"),sQuery(id+"F0.wireOp",EDGE,"E13.1.0"),sQuery(id+"F0.wireOp",EDGE,"E13.1.1"),sQuery(id+"F0.wireOp",EDGE,"E13.2.0"),sQuery(id+"F0.wireOp",EDGE,"E13.2.1")])]}),"instanceName":"1"}),"instanceName":"1"}),"instanceName":"1"}),"instanceName":"1"}),"instanceName":"1"}),"instanceName":"1"});
            transform(context, id + "F77", {"entities" : qUnion([Q0]), "transformType" : TransformType.TRANSLATION_3D, "dx" : 70 * mm, "dy" : 0 * mm, "dz" : 0 * mm, "makeCopy" : true});
        }
        {
            var Q0;
            Q0=makeQuery(id+"F77.opPattern","COPY",BODY,{"derivedFrom":makeQuery(id+"F76.opPattern","COPY",BODY,{"derivedFrom":makeQuery(id+"F73.opPattern","COPY",BODY,{"derivedFrom":makeQuery(id+"F72.opPattern","COPY",BODY,{"derivedFrom":makeQuery(id+"F71.opPattern","COPY",BODY,{"derivedFrom":makeQuery(id+"F70.opPattern","COPY",BODY,{"derivedFrom":makeQuery(id+"F69.opPattern","COPY",BODY,{"derivedFrom":makeQuery(id+"F1.opExtrude","SWEPT_BODY",BODY,{"disambiguationData":[OSD([sQuery(id+"F0.wireOp",EDGE,"E2.0"),sQuery(id+"F0.wireOp",EDGE,"E2.1"),sQuery(id+"F0.wireOp",EDGE,"E2.2"),sQuery(id+"F0.wireOp",EDGE,"E2.3"),sQuery(id+"F0.wireOp",EDGE,"E2.4"),sQuery(id+"F0.wireOp",EDGE,"E2.5"),sQuery(id+"F0.wireOp",EDGE,"E3"),sQuery(id+"F0.wireOp",EDGE,"E4"),sQuery(id+"F0.wireOp",EDGE,"E5.0"),sQuery(id+"F0.wireOp",EDGE,"E5.1"),sQuery(id+"F0.wireOp",EDGE,"E5.3"),sQuery(id+"F0.wireOp",EDGE,"E5.4"),sQuery(id+"F0.wireOp",EDGE,"E5.5"),sQuery(id+"F0.wireOp",EDGE,"E6.trimOffspring"),sQuery(id+"F0.wireOp",EDGE,"E7.trimOffspring"),sQuery(id+"F0.wireOp",EDGE,"E9.trimOffspring"),sQuery(id+"F0.wireOp",EDGE,"E10.1.0"),sQuery(id+"F0.wireOp",EDGE,"E10.1.1"),sQuery(id+"F0.wireOp",EDGE,"E10.1.2"),sQuery(id+"F0.wireOp",EDGE,"E10.1.3"),sQuery(id+"F0.wireOp",EDGE,"E10.1.5"),sQuery(id+"F0.wireOp",EDGE,"E10.1.7"),sQuery(id+"F0.wireOp",EDGE,"E10.1.8"),sQuery(id+"F0.wireOp",EDGE,"E10.1.9"),sQuery(id+"F0.wireOp",EDGE,"E10.1.10"),sQuery(id+"F0.wireOp",EDGE,"E10.1.11"),sQuery(id+"F0.wireOp",EDGE,"E10.1.12"),sQuery(id+"F0.wireOp",EDGE,"E10.1.14"),sQuery(id+"F0.wireOp",EDGE,"E10.1.15"),sQuery(id+"F0.wireOp",EDGE,"E10.1.16"),sQuery(id+"F0.wireOp",EDGE,"E10.1.18"),sQuery(id+"F0.wireOp",EDGE,"E10.1.20"),sQuery(id+"F0.wireOp",EDGE,"E10.2.0"),sQuery(id+"F0.wireOp",EDGE,"E10.2.1"),sQuery(id+"F0.wireOp",EDGE,"E10.2.2"),sQuery(id+"F0.wireOp",EDGE,"E10.2.3"),sQuery(id+"F0.wireOp",EDGE,"E10.2.5"),sQuery(id+"F0.wireOp",EDGE,"E10.2.7"),sQuery(id+"F0.wireOp",EDGE,"E10.2.8"),sQuery(id+"F0.wireOp",EDGE,"E10.2.9"),sQuery(id+"F0.wireOp",EDGE,"E10.2.10"),sQuery(id+"F0.wireOp",EDGE,"E10.2.11"),sQuery(id+"F0.wireOp",EDGE,"E10.2.12"),sQuery(id+"F0.wireOp",EDGE,"E1"),sQuery(id+"F0.wireOp",EDGE,"E10.2.14"),sQuery(id+"F0.wireOp",EDGE,"E10.2.15"),sQuery(id+"F0.wireOp",EDGE,"E10.2.16"),sQuery(id+"F0.wireOp",EDGE,"E10.2.18"),sQuery(id+"F0.wireOp",EDGE,"E10.2.20"),sQuery(id+"F0.wireOp",EDGE,"E8.trimOffspring"),sQuery(id+"F0.wireOp",EDGE,"E0"),sQuery(id+"F0.wireOp",EDGE,"E10.1.6"),sQuery(id+"F0.wireOp",EDGE,"E11"),sQuery(id+"F0.wireOp",EDGE,"E12"),sQuery(id+"F0.wireOp",EDGE,"E13.1.0"),sQuery(id+"F0.wireOp",EDGE,"E13.1.1"),sQuery(id+"F0.wireOp",EDGE,"E13.2.0"),sQuery(id+"F0.wireOp",EDGE,"E13.2.1")])]}),"instanceName":"1"}),"instanceName":"1"}),"instanceName":"1"}),"instanceName":"1"}),"instanceName":"1"}),"instanceName":"1"}),"instanceName":"1"});
            transform(context, id + "F78", {"entities" : qUnion([Q0]), "transformType" : TransformType.TRANSLATION_3D, "dx" : 70 * mm, "dy" : 0 * mm, "dz" : 0 * mm, "makeCopy" : true});
        }
    });
